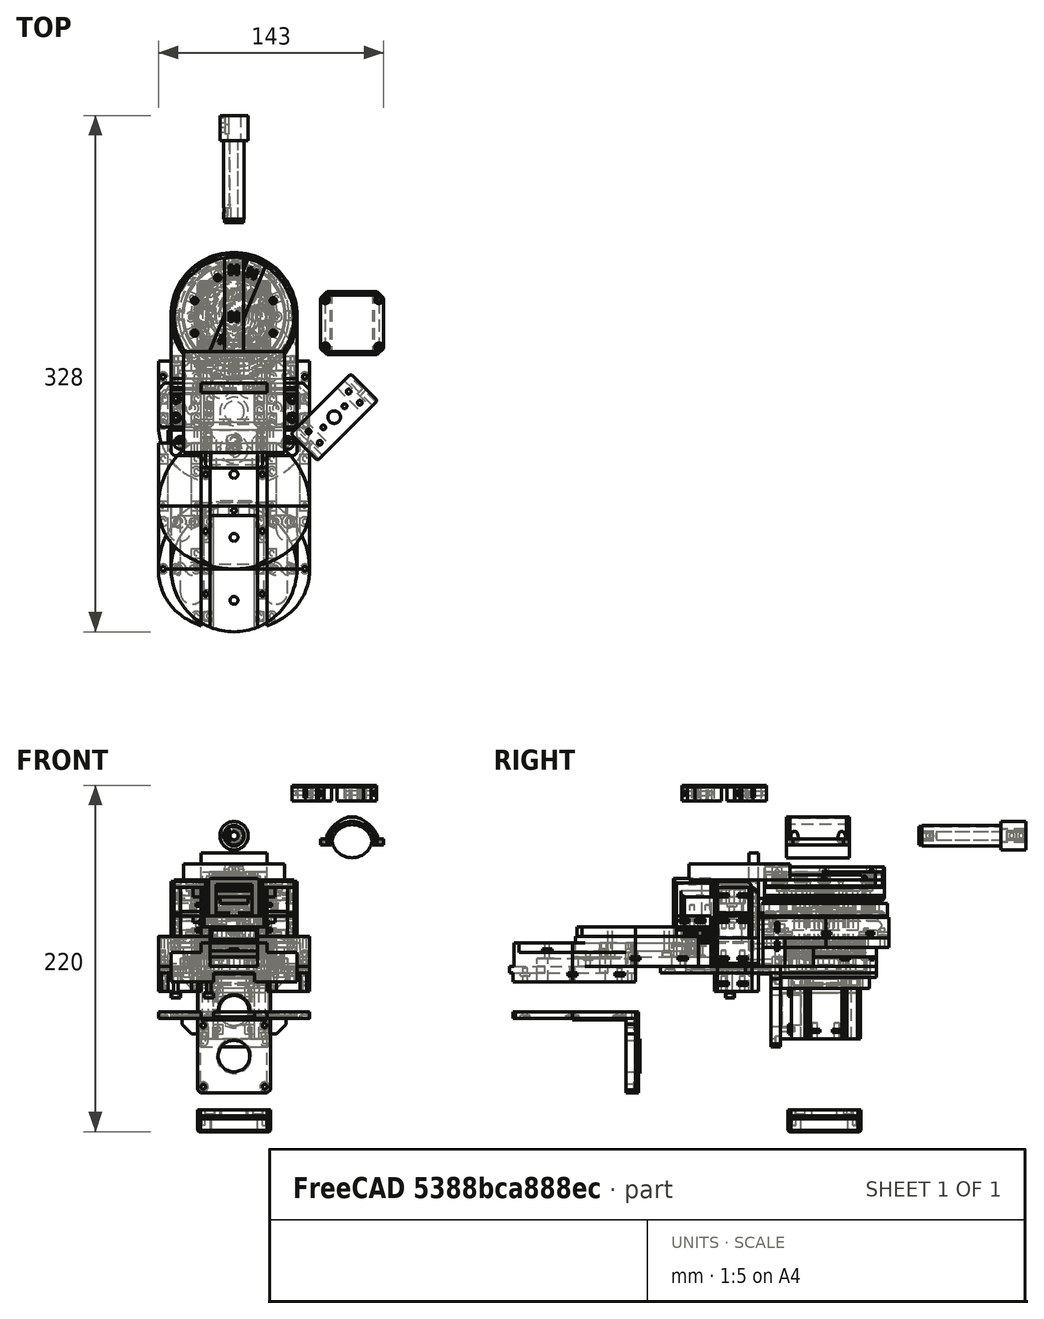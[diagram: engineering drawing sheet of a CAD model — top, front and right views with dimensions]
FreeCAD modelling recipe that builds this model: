
FCSTD DOCUMENT  (FreeCAD 0.19R24276 (Git))
Label: L-elbow_059
License: All rights reserved
LicenseURL: http://en.wikipedia.org/wiki/All_rights_reserved
objects: Part::Cylinder×884, Part::Box×401, Part::Cut×391, Part::Compound×387, Part::Chamfer×88, Part::FeaturePython×52, Mesh::Feature×41, Part::Fillet×8, Part::Common×8, Part::Torus×1, Part::Mirroring×1
note: 2221 computed .brp shape members not serialized (recipe doc carries the construction recipe); baked Part::Feature solids carry a one-line shape summary decoded from their .brp

FEATURE [Part::Cylinder] Cylinder2138  label="Válec2138"
  Angle = 360
  AttacherType = Attacher::AttachEngine3D
  Height = 15
  Placement = pos=(-34.5,-175,-69) rot=(0,0,1;0rad)
  Radius = 7.5
FEATURE [Part::Box] Box854  label="Krychle853"
  AttacherType = Attacher::AttachEngine3D
  Height = 30.1
  Length = 30.1
  Placement = pos=(-15.05,-310,-40.05) rot=(0,0,1;0rad)
  Width = 200
FEATURE [Part::Cylinder] Cylinder2140  label="Válec2140"
  Angle = 360
  AttacherType = Attacher::AttachEngine3D
  Height = 40
  Placement = pos=(24,-160,-70) rot=(0,0,1;0rad)
  Radius = 1.5
FEATURE [Part::Box] Box850  label="Krychle849"
  AttacherType = Attacher::AttachEngine3D
  Height = 30
  Length = 28
  Placement = pos=(-49,-210.5,-46) rot=(0,0,1;0rad)
  Width = 200
FEATURE [Part::Box] Box849  label="Krychle848"
  AttacherType = Attacher::AttachEngine3D
  Height = 30
  Length = 28
  Placement = pos=(21,-210.5,-46) rot=(0,0,1;0rad)
  Width = 200
FEATURE [Part::Cylinder] Cylinder2137  label="Válec2137"
  Angle = 360
  AttacherType = Attacher::AttachEngine3D
  Height = 25
  Placement = pos=(0,-160,-50) rot=(0,0,1;0rad)
  Radius = 48
FEATURE [Part::Box] Box851  label="Krychle850"
  AttacherType = Attacher::AttachEngine3D
  Height = 15
  Length = 15
  Placement = pos=(27,-175.6,-65) rot=(0,0,1;0rad)
  Width = 200
FEATURE [Part::Box] Box852  label="Krychle851"
  AttacherType = Attacher::AttachEngine3D
  Height = 15
  Length = 15
  Placement = pos=(-42,-175.5,-65) rot=(0,0,1;0rad)
  Width = 200
FEATURE [Part::Cylinder] Cylinder2139  label="Válec2139"
  Angle = 360
  AttacherType = Attacher::AttachEngine3D
  Height = 15
  Placement = pos=(34.5,-175,-69) rot=(0,0,1;0rad)
  Radius = 7.5
FEATURE [Part::Box] Box853  label="Krychle852"
  AttacherType = Attacher::AttachEngine3D
  Height = 30
  Length = 42
  Placement = pos=(-21,-290,-74) rot=(0,0,1;0rad)
  Width = 200
FEATURE [Part::Cylinder] Cylinder2142  label="Válec2142"
  Angle = 360
  AttacherType = Attacher::AttachEngine3D
  Height = 40
  Placement = pos=(-24,-190,-70) rot=(0,0,1;0rad)
  Radius = 1.5
FEATURE [Part::Cylinder] Cylinder2143  label="Válec2143"
  Angle = 360
  AttacherType = Attacher::AttachEngine3D
  Height = 20
  Placement = pos=(0,-140,-44) rot=(0,0,1;0rad)
  Radius = 2.5
FEATURE [Part::Cylinder] Cylinder2141  label="Válec2141"
  Angle = 360
  AttacherType = Attacher::AttachEngine3D
  Height = 40
  Placement = pos=(-45,-130,-70) rot=(0,0,1;0rad)
  Radius = 1.5
FEATURE [Part::Compound] Compound957
  Links = -> [Box850,Box849]
  Placement = pos=(0,0,15) rot=(0,0,1;0rad)
FEATURE [Part::Compound] Compound955
  Links = -> [Box852,Box851]
  Placement = pos=(0,0,15) rot=(0,0,1;0rad)
FEATURE [Part::Compound] Compound956
  Links = -> [Cylinder2138,Cylinder2139]
  Placement = pos=(0,0,19) rot=(0,0,1;0rad)
FEATURE [Part::Cut] Cut790
  Base = -> Cylinder2137
  Tool = -> Compound955
FEATURE [Part::Cut] Cut791
  Base = -> Cut790
  Tool = -> Box854
FEATURE [Part::Cut] Cut792
  Base = -> Cut791
  Tool = -> Box853
FEATURE [Part::Cut] Cut793
  Base = -> Cut792
  Tool = -> Compound956
FEATURE [Part::Cut] Cut796
  Base = -> Cut793
  Tool = -> Compound957
FEATURE [Part::Cylinder] Cylinder2149  label="Válec2149"
  Angle = 360
  AttacherType = Attacher::AttachEngine3D
  Height = 40
  Placement = pos=(-45,-160,-70) rot=(0,0,1;0rad)
  Radius = 1.5
FEATURE [Part::Box] Box855  label="Krychle854"
  AttacherType = Attacher::AttachEngine3D
  Height = 2
  Length = 6
  Placement = pos=(21,-193,-61) rot=(0,0,1;0rad)
  Width = 6
FEATURE [Part::Cylinder] Cylinder2145  label="Válec2145"
  Angle = 360
  AttacherType = Attacher::AttachEngine3D
  Height = 40
  Placement = pos=(24,-190,-70) rot=(0,0,1;0rad)
  Radius = 1.5
FEATURE [Part::Box] Box856  label="Krychle855"
  AttacherType = Attacher::AttachEngine3D
  Height = 2
  Length = 6
  Placement = pos=(-27,-133,-61) rot=(0,0,1;0rad)
  Width = 6
FEATURE [Part::Box] Box859  label="Krychle858"
  AttacherType = Attacher::AttachEngine3D
  Height = 2
  Length = 6
  Placement = pos=(-48,-163,-61) rot=(0,0,1;0rad)
  Width = 6
FEATURE [Part::Box] Box867  label="Krychle866"
  AttacherType = Attacher::AttachEngine3D
  Height = 2
  Length = 6
  Placement = pos=(-27,-163,-61) rot=(0,0,1;0rad)
  Width = 6
FEATURE [Part::Box] Box857  label="Krychle856"
  AttacherType = Attacher::AttachEngine3D
  Height = 2
  Length = 6
  Placement = pos=(42,-163,-61) rot=(0,0,1;0rad)
  Width = 6
FEATURE [Part::Cylinder] Cylinder2144  label="Válec2144"
  Angle = 360
  AttacherType = Attacher::AttachEngine3D
  Height = 40
  Placement = pos=(24,-130,-70) rot=(0,0,1;0rad)
  Radius = 1.5
FEATURE [Part::Box] Box861  label="Krychle860"
  AttacherType = Attacher::AttachEngine3D
  Height = 2
  Length = 6
  Placement = pos=(-21,-179,-31) rot=(0,0,1;0rad)
  Width = 6
FEATURE [Part::Cylinder] Cylinder2148  label="Válec2148"
  Angle = 360
  AttacherType = Attacher::AttachEngine3D
  Height = 20
  Placement = pos=(0,-180,-44) rot=(0,0,1;0rad)
  Radius = 2.5
FEATURE [Part::Compound] Compound958
  Links = -> [Cylinder2143,Cylinder2148]
FEATURE [Part::Cut] Cut786
  Base = -> Cut796
  Tool = -> Compound958
FEATURE [Part::Box] Box862  label="Krychle861"
  AttacherType = Attacher::AttachEngine3D
  Height = 2
  Length = 6
  Placement = pos=(-27,-193,-61) rot=(0,0,1;0rad)
  Width = 6
FEATURE [Part::Box] Box864  label="Krychle863"
  AttacherType = Attacher::AttachEngine3D
  Height = 2
  Length = 6
  Placement = pos=(-3,-126,-31) rot=(0,0,1;0rad)
  Width = 6
FEATURE [Part::Box] Box865  label="Krychle864"
  AttacherType = Attacher::AttachEngine3D
  Height = 2
  Length = 6
  Placement = pos=(21,-163,-61) rot=(0,0,1;0rad)
  Width = 6
FEATURE [Part::Cylinder] Cylinder2146  label="Válec2146"
  Angle = 360
  AttacherType = Attacher::AttachEngine3D
  Height = 40
  Placement = pos=(-24,-130,-70) rot=(0,0,1;0rad)
  Radius = 1.5
FEATURE [Part::Cylinder] Cylinder2147  label="Válec2147"
  Angle = 360
  AttacherType = Attacher::AttachEngine3D
  Height = 40
  Placement = pos=(45,-130,-70) rot=(0,0,1;0rad)
  Radius = 1.5
FEATURE [Part::Box] Box858  label="Krychle857"
  AttacherType = Attacher::AttachEngine3D
  Height = 2
  Length = 6
  Placement = pos=(42,-133,-61) rot=(0,0,1;0rad)
  Width = 6
FEATURE [Part::Cylinder] Cylinder2151  label="Válec2151"
  Angle = 360
  AttacherType = Attacher::AttachEngine3D
  Height = 40
  Placement = pos=(-24,-160,-70) rot=(0,0,1;0rad)
  Radius = 1.5
FEATURE [Part::Box] Box860  label="Krychle859"
  AttacherType = Attacher::AttachEngine3D
  Height = 2
  Length = 6
  Placement = pos=(15,-143,-31) rot=(0,0,1;0rad)
  Width = 6
FEATURE [Part::Cylinder] Cylinder2150  label="Válec2150"
  Angle = 360
  AttacherType = Attacher::AttachEngine3D
  Height = 40
  Placement = pos=(45,-160,-70) rot=(0,0,1;0rad)
  Radius = 1.5
FEATURE [Part::Compound] Compound959
  Links = -> [Cylinder2144,Cylinder2145,Cylinder2140,Cylinder2147,Cylinder2150,Cylinder2146,Cylinder2142,Cylinder2151,Cylinder2141,Cylinder2149]
  Placement = pos=(0,0,-11) rot=(0,0,1;0rad)
FEATURE [Part::Cut] Cut785
  Base = -> Cut786
  Tool = -> Compound959
FEATURE [Part::Box] Box863  label="Krychle862"
  AttacherType = Attacher::AttachEngine3D
  Height = 2
  Length = 6
  Placement = pos=(15,-179,-31) rot=(0,0,1;0rad)
  Width = 6
FEATURE [Part::Box] Box866  label="Krychle865"
  AttacherType = Attacher::AttachEngine3D
  Height = 2
  Length = 6
  Placement = pos=(21,-133,-61) rot=(0,0,1;0rad)
  Width = 6
FEATURE [Part::Cylinder] Cylinder2154  label="Válec2154"
  Angle = 360
  AttacherType = Attacher::AttachEngine3D
  Height = 40
  Placement = pos=(0,-123,-35) rot=(0,0,1;0rad)
  Radius = 1.5
FEATURE [Part::Box] Box868  label="Krychle867"
  AttacherType = Attacher::AttachEngine3D
  Height = 2
  Length = 6
  Placement = pos=(-21,-143,-31) rot=(0,0,1;0rad)
  Width = 6
FEATURE [Part::Box] Box872  label="Krychle871"
  AttacherType = Attacher::AttachEngine3D
  Height = 30
  Length = 29
  Placement = pos=(21,-210.5,-46) rot=(0,0,1;0rad)
  Width = 200
FEATURE [Part::Box] Box873  label="Krychle872"
  AttacherType = Attacher::AttachEngine3D
  Height = 25
  Length = 96
  Placement = pos=(-48,-160,-50) rot=(0,0,1;0rad)
  Width = 40
FEATURE [Part::Cylinder] Cylinder2153  label="Válec2153"
  Angle = 360
  AttacherType = Attacher::AttachEngine3D
  Height = 40
  Placement = pos=(18,-160,100) rot=(0,0,1;0rad)
  Radius = 1.5
FEATURE [Part::Cylinder] Cylinder2160  label="Válec2160"
  Angle = 360
  AttacherType = Attacher::AttachEngine3D
  Height = 40
  Placement = pos=(45,-130,-70) rot=(0,0,1;0rad)
  Radius = 1.5
FEATURE [Part::Cylinder] Cylinder2164  label="Válec2164"
  Angle = 360
  AttacherType = Attacher::AttachEngine3D
  Height = 20
  Placement = pos=(0,-140,-44) rot=(0,0,1;0rad)
  Radius = 2.5
FEATURE [Part::Cylinder] Cylinder2165  label="Válec2165"
  Angle = 360
  AttacherType = Attacher::AttachEngine3D
  Height = 40
  Placement = pos=(18,-176,-35) rot=(0,0,1;0rad)
  Radius = 1.5
FEATURE [Part::Box] Box869  label="Krychle868"
  AttacherType = Attacher::AttachEngine3D
  Height = 2
  Length = 6
  Placement = pos=(15,-163,100) rot=(0,0,1;0rad)
  Width = 6
FEATURE [Part::Cylinder] Cylinder2158  label="Válec2158"
  Angle = 360
  AttacherType = Attacher::AttachEngine3D
  Height = 40
  Placement = pos=(-45,-130,-70) rot=(0,0,1;0rad)
  Radius = 1.5
FEATURE [Part::Box] Box874  label="Krychle873"
  AttacherType = Attacher::AttachEngine3D
  Height = 30
  Length = 29
  Placement = pos=(-50,-210.5,-46) rot=(0,0,1;0rad)
  Width = 200
FEATURE [Part::Compound] Compound964
  Links = -> [Box874,Box872]
  Placement = pos=(0,0,15) rot=(0,0,1;0rad)
FEATURE [Part::Cylinder] Cylinder2152  label="Válec2152"
  Angle = 360
  AttacherType = Attacher::AttachEngine3D
  Height = 40
  Placement = pos=(-10,-123,100) rot=(0,0,1;0rad)
  Radius = 1.5
FEATURE [Part::Box] Box870  label="Krychle869"
  AttacherType = Attacher::AttachEngine3D
  Height = 2
  Length = 6
  Placement = pos=(-48,-133,-61) rot=(0,0,1;0rad)
  Width = 6
FEATURE [Part::Compound] Compound960
  Links = -> [Box870,Box859,Box856,Box867,Box862,Box858,Box857,Box866,Box865,Box855]
  Placement = pos=(0,0,15) rot=(0,0,1;0rad)
FEATURE [Part::Cylinder] Cylinder2156  label="Válec2156"
  Angle = 360
  AttacherType = Attacher::AttachEngine3D
  Height = 40
  Placement = pos=(-18,-140,-35) rot=(0,0,1;0rad)
  Radius = 1.5
FEATURE [Part::Cylinder] Cylinder2162  label="Válec2162"
  Angle = 360
  AttacherType = Attacher::AttachEngine3D
  Height = 40
  Placement = pos=(24,-130,-70) rot=(0,0,1;0rad)
  Radius = 1.5
FEATURE [Part::Cylinder] Cylinder2161  label="Válec2161"
  Angle = 360
  AttacherType = Attacher::AttachEngine3D
  Height = 40
  Placement = pos=(18,-140,-35) rot=(0,0,1;0rad)
  Radius = 1.5
FEATURE [Part::Box] Box871  label="Krychle870"
  AttacherType = Attacher::AttachEngine3D
  Height = 2
  Length = 6
  Placement = pos=(-21,-163,100) rot=(0,0,1;0rad)
  Width = 6
FEATURE [Part::Compound] Compound968
  Links = -> [Box864,Box871,Box861,Box868,Box869,Box863,Box860]
  Placement = pos=(0,0,20) rot=(0,0,1;0rad)
FEATURE [Part::Cylinder] Cylinder2155  label="Válec2155"
  Angle = 360
  AttacherType = Attacher::AttachEngine3D
  Height = 40
  Placement = pos=(-18,-176,-35) rot=(0,0,1;0rad)
  Radius = 1.5
FEATURE [Part::Cylinder] Cylinder2157  label="Válec2157"
  Angle = 360
  AttacherType = Attacher::AttachEngine3D
  Height = 40
  Placement = pos=(24,-160,-70) rot=(0,0,1;0rad)
  Radius = 1.5
FEATURE [Part::Cylinder] Cylinder2159  label="Válec2159"
  Angle = 360
  AttacherType = Attacher::AttachEngine3D
  Height = 20
  Placement = pos=(0,-180,-44) rot=(0,0,1;0rad)
  Radius = 2.5
FEATURE [Part::Compound] Compound961
  Links = -> [Cylinder2164,Cylinder2159]
FEATURE [Part::Box] Box875  label="Krychle874"
  AttacherType = Attacher::AttachEngine3D
  Height = 30.1
  Length = 30.1
  Placement = pos=(-15.05,-326,-40.05) rot=(0,0,1;0rad)
  Width = 200
FEATURE [Part::Cylinder] Cylinder2163  label="Válec2163"
  Angle = 360
  AttacherType = Attacher::AttachEngine3D
  Height = 40
  Placement = pos=(-18,-160,100) rot=(0,0,1;0rad)
  Radius = 1.5
FEATURE [Part::Compound] Compound970
  Links = -> [Cylinder2154,Cylinder2152,Cylinder2161,Cylinder2153,Cylinder2165,Cylinder2156,Cylinder2163,Cylinder2155]
FEATURE [Part::Cut] Cut787
  Base = -> Cut785
  Tool = -> Compound970
FEATURE [Part::Cut] Cut782
  Base = -> Cut787
  Tool = -> Compound968
FEATURE [Part::Cut] Cut794
  Base = -> Cut782
  Tool = -> Compound960
FEATURE [Part::Box] Box876  label="Krychle875"
  AttacherType = Attacher::AttachEngine3D
  Height = 30
  Length = 42
  Placement = pos=(-21,-290,-74) rot=(0,0,1;0rad)
  Width = 200
FEATURE [Part::Cut] Cut795
  Base = -> Box873
  Tool = -> Box876
FEATURE [Part::Cut] Cut788
  Base = -> Cut795
  Tool = -> Box875
FEATURE [Part::Box] Box878  label="Krychle877"
  AttacherType = Attacher::AttachEngine3D
  Height = 2
  Length = 6
  Placement = pos=(42,-133,-61) rot=(0,0,1;0rad)
  Width = 6
FEATURE [Part::Box] Box882  label="Krychle881"
  AttacherType = Attacher::AttachEngine3D
  Height = 2
  Length = 6
  Placement = pos=(42,-163,-61) rot=(0,0,1;0rad)
  Width = 6
FEATURE [Part::Cylinder] Cylinder2170  label="Válec2170"
  Angle = 360
  AttacherType = Attacher::AttachEngine3D
  Height = 40
  Placement = pos=(-24,-130,-70) rot=(0,0,1;0rad)
  Radius = 1.5
FEATURE [Part::Cylinder] Cylinder2166  label="Válec2166"
  Angle = 360
  AttacherType = Attacher::AttachEngine3D
  Height = 40
  Placement = pos=(-24,-160,-70) rot=(0,0,1;0rad)
  Radius = 1.5
FEATURE [Part::Box] Box879  label="Krychle878"
  AttacherType = Attacher::AttachEngine3D
  Height = 2
  Length = 6
  Placement = pos=(21,-163,-61) rot=(0,0,1;0rad)
  Width = 6
FEATURE [Part::Box] Box884  label="Krychle883"
  AttacherType = Attacher::AttachEngine3D
  Height = 2
  Length = 6
  Placement = pos=(-27,-193,-61) rot=(0,0,1;0rad)
  Width = 6
FEATURE [Part::Box] Box888  label="Krychle887"
  AttacherType = Attacher::AttachEngine3D
  Height = 2
  Length = 6
  Placement = pos=(15,-143,-31) rot=(0,0,1;0rad)
  Width = 6
FEATURE [Part::Box] Box877  label="Krychle876"
  AttacherType = Attacher::AttachEngine3D
  Height = 2
  Length = 6
  Placement = pos=(-48,-163,-61) rot=(0,0,1;0rad)
  Width = 6
FEATURE [Part::Box] Box881  label="Krychle880"
  AttacherType = Attacher::AttachEngine3D
  Height = 2
  Length = 6
  Placement = pos=(21,-193,-61) rot=(0,0,1;0rad)
  Width = 6
FEATURE [Part::Cylinder] Cylinder2169  label="Válec2169"
  Angle = 360
  AttacherType = Attacher::AttachEngine3D
  Height = 40
  Placement = pos=(-45,-160,-70) rot=(0,0,1;0rad)
  Radius = 1.5
FEATURE [Part::Box] Box880  label="Krychle879"
  AttacherType = Attacher::AttachEngine3D
  Height = 2
  Length = 6
  Placement = pos=(-27,-133,-61) rot=(0,0,1;0rad)
  Width = 6
FEATURE [Part::Cylinder] Cylinder2168  label="Válec2168"
  Angle = 360
  AttacherType = Attacher::AttachEngine3D
  Height = 40
  Placement = pos=(-24,-190,-70) rot=(0,0,1;0rad)
  Radius = 1.5
FEATURE [Part::Cylinder] Cylinder2167  label="Válec2167"
  Angle = 360
  AttacherType = Attacher::AttachEngine3D
  Height = 40
  Placement = pos=(24,-190,-70) rot=(0,0,1;0rad)
  Radius = 1.5
FEATURE [Part::Cylinder] Cylinder2171  label="Válec2171"
  Angle = 360
  AttacherType = Attacher::AttachEngine3D
  Height = 40
  Placement = pos=(45,-160,-70) rot=(0,0,1;0rad)
  Radius = 1.5
FEATURE [Part::Compound] Compound962
  Links = -> [Cylinder2162,Cylinder2167,Cylinder2157,Cylinder2160,Cylinder2171,Cylinder2170,Cylinder2168,Cylinder2166,Cylinder2158,Cylinder2169]
  Placement = pos=(0,0,-11) rot=(0,0,1;0rad)
FEATURE [Part::Box] Box886  label="Krychle885"
  AttacherType = Attacher::AttachEngine3D
  Height = 2
  Length = 6
  Placement = pos=(-48,-133,-61) rot=(0,0,1;0rad)
  Width = 6
FEATURE [Part::Cylinder] Cylinder2172  label="Válec2172"
  Angle = 360
  AttacherType = Attacher::AttachEngine3D
  Height = 40
  Placement = pos=(18,-176,-35) rot=(0,0,1;0rad)
  Radius = 1.5
FEATURE [Part::Box] Box883  label="Krychle882"
  AttacherType = Attacher::AttachEngine3D
  Height = 2
  Length = 6
  Placement = pos=(21,-133,-61) rot=(0,0,1;0rad)
  Width = 6
FEATURE [Part::Cylinder] Cylinder2173  label="Válec2173"
  Angle = 360
  AttacherType = Attacher::AttachEngine3D
  Height = 40
  Placement = pos=(-18,-140,-35) rot=(0,0,1;0rad)
  Radius = 1.5
FEATURE [Part::Box] Box885  label="Krychle884"
  AttacherType = Attacher::AttachEngine3D
  Height = 2
  Length = 6
  Placement = pos=(-27,-163,-61) rot=(0,0,1;0rad)
  Width = 6
FEATURE [Part::Compound] Compound965
  Links = -> [Box886,Box877,Box880,Box885,Box884,Box878,Box882,Box883,Box879,Box881]
  Placement = pos=(0,0,15) rot=(0,0,1;0rad)
FEATURE [Part::Cut] Cut778
  Base = -> Cut788
  Tool = -> Compound965
FEATURE [Part::Cut] Cut789
  Base = -> Cut778
  Tool = -> Compound962
FEATURE [Part::Cut] Cut779
  Base = -> Cut789
  Tool = -> Compound961
FEATURE [Part::Cut] Cut780
  Base = -> Cut779
  Tool = -> Compound964
FEATURE [Part::Box] Box887  label="Krychle886"
  AttacherType = Attacher::AttachEngine3D
  Height = 2
  Length = 6
  Placement = pos=(7,-126,100) rot=(0,0,1;0rad)
  Width = 6
FEATURE [Part::Cylinder] Cylinder2174  label="Válec2174"
  Angle = 360
  AttacherType = Attacher::AttachEngine3D
  Height = 40
  Placement = pos=(0,-123,-35) rot=(0,0,1;0rad)
  Radius = 1.5
FEATURE [Part::Box] Box889  label="Krychle888"
  AttacherType = Attacher::AttachEngine3D
  Height = 2
  Length = 6
  Placement = pos=(-3,-126,-31) rot=(0,0,1;0rad)
  Width = 6
FEATURE [Part::Box] Box890  label="Krychle889"
  AttacherType = Attacher::AttachEngine3D
  Height = 2
  Length = 6
  Placement = pos=(15,-179,-31) rot=(0,0,1;0rad)
  Width = 6
FEATURE [Part::Cylinder] Cylinder2178  label="Válec2178"
  Angle = 360
  AttacherType = Attacher::AttachEngine3D
  Height = 40
  Placement = pos=(-10,-123,100) rot=(0,0,1;0rad)
  Radius = 1.5
FEATURE [Part::Cylinder] Cylinder2180  label="Válec2180"
  Angle = 360
  AttacherType = Attacher::AttachEngine3D
  Height = 40
  Placement = pos=(18,-140,-35) rot=(0,0,1;0rad)
  Radius = 1.5
FEATURE [Part::Box] Box895  label="Krychle894"
  AttacherType = Attacher::AttachEngine3D
  Height = 15
  Length = 15
  Placement = pos=(-42,-175.5,-65) rot=(0,0,1;0rad)
  Width = 200
FEATURE [Part::Cylinder] Cylinder2184  label="Válec2184"
  Angle = 360
  AttacherType = Attacher::AttachEngine3D
  Height = 40
  Placement = pos=(18,-160,100) rot=(0,0,1;0rad)
  Radius = 1.5
FEATURE [Part::Cylinder] Cylinder2181  label="Válec2181"
  Angle = 360
  AttacherType = Attacher::AttachEngine3D
  Height = 40
  Placement = pos=(-18,-160,100) rot=(0,0,1;0rad)
  Radius = 1.5
FEATURE [Part::Cylinder] Cylinder2187  label="Válec2187"
  Angle = 360
  AttacherType = Attacher::AttachEngine3D
  Height = 40
  Placement = pos=(-18,-140,-35) rot=(0,0,1;0rad)
  Radius = 1.5
FEATURE [Part::Cylinder] Cylinder2189  label="Válec2189"
  Angle = 360
  AttacherType = Attacher::AttachEngine3D
  Height = 3
  Placement = pos=(-18,-160,100) rot=(0,0,1;0rad)
  Radius = 3
FEATURE [Part::Cylinder] Cylinder2191  label="Válec2191"
  Angle = 360
  AttacherType = Attacher::AttachEngine3D
  Height = 3
  Placement = pos=(-10,-123,100) rot=(0,0,1;0rad)
  Radius = 3
FEATURE [Part::Box] Box891  label="Krychle890"
  AttacherType = Attacher::AttachEngine3D
  Height = 2
  Length = 6
  Placement = pos=(15,-163,100) rot=(0,0,1;0rad)
  Width = 6
FEATURE [Part::Box] Box892  label="Krychle891"
  AttacherType = Attacher::AttachEngine3D
  Height = 2
  Length = 6
  Placement = pos=(-21,-163,100) rot=(0,0,1;0rad)
  Width = 6
FEATURE [Part::Box] Box893  label="Krychle892"
  AttacherType = Attacher::AttachEngine3D
  Height = 2
  Length = 6
  Placement = pos=(-21,-179,-31) rot=(0,0,1;0rad)
  Width = 6
FEATURE [Part::Box] Box894  label="Krychle893"
  AttacherType = Attacher::AttachEngine3D
  Height = 15
  Length = 15
  Placement = pos=(27,-175.6,-65) rot=(0,0,1;0rad)
  Width = 200
FEATURE [Part::Compound] Compound966
  Links = -> [Box895,Box894]
  Placement = pos=(0,0,15) rot=(0,0,1;0rad)
FEATURE [Part::Cut] Cut781
  Base = -> Cut780
  Tool = -> Compound966
FEATURE [Part::Cylinder] Cylinder2175  label="Válec2175"
  Angle = 360
  AttacherType = Attacher::AttachEngine3D
  Height = 40
  Placement = pos=(18,-140,-35) rot=(0,0,1;0rad)
  Radius = 1.5
FEATURE [Part::Cylinder] Cylinder2176  label="Válec2176"
  Angle = 360
  AttacherType = Attacher::AttachEngine3D
  Height = 40
  Placement = pos=(18,-160,100) rot=(0,0,1;0rad)
  Radius = 1.5
FEATURE [Part::Cylinder] Cylinder2177  label="Válec2177"
  Angle = 360
  AttacherType = Attacher::AttachEngine3D
  Height = 40
  Placement = pos=(-18,-160,100) rot=(0,0,1;0rad)
  Radius = 1.5
FEATURE [Part::Box] Box896  label="Krychle895"
  AttacherType = Attacher::AttachEngine3D
  Height = 2
  Length = 6
  Placement = pos=(-21,-143,-31) rot=(0,0,1;0rad)
  Width = 6
FEATURE [Part::Compound] Compound967
  Links = -> [Box889,Box892,Box893,Box896,Box887,Box891,Box890,Box888]
  Placement = pos=(0,0,20) rot=(0,0,1;0rad)
FEATURE [Part::Cut] Cut783
  Base = -> Cut781
  Tool = -> Compound967
FEATURE [Part::Cylinder] Cylinder2179  label="Válec2179"
  Angle = 360
  AttacherType = Attacher::AttachEngine3D
  Height = 40
  Placement = pos=(-18,-176,-35) rot=(0,0,1;0rad)
  Radius = 1.5
FEATURE [Part::Compound] Compound963
  Links = -> [Cylinder2174,Cylinder2178,Cylinder2175,Cylinder2176,Cylinder2172,Cylinder2173,Cylinder2177,Cylinder2179]
FEATURE [Part::Cut] Cut784
  Base = -> Cut783
  Tool = -> Compound963
FEATURE [Part::Cylinder] Cylinder2182  label="Válec2182"
  Angle = 360
  AttacherType = Attacher::AttachEngine3D
  Height = 40
  Placement = pos=(18,-176,-35) rot=(0,0,1;0rad)
  Radius = 1.5
FEATURE [Part::Cylinder] Cylinder2183  label="Válec2183"
  Angle = 360
  AttacherType = Attacher::AttachEngine3D
  Height = 40
  Placement = pos=(-10,-123,100) rot=(0,0,1;0rad)
  Radius = 1.5
FEATURE [Part::Cylinder] Cylinder2185  label="Válec2185"
  Angle = 360
  AttacherType = Attacher::AttachEngine3D
  Height = 40
  Placement = pos=(0,-123,-35) rot=(0,0,1;0rad)
  Radius = 1.5
FEATURE [Part::Cylinder] Cylinder2186  label="Válec2186"
  Angle = 360
  AttacherType = Attacher::AttachEngine3D
  Height = 40
  Placement = pos=(-18,-176,-35) rot=(0,0,1;0rad)
  Radius = 1.5
FEATURE [Part::Compound] Compound971
  Links = -> [Cylinder2185,Cylinder2183,Cylinder2180,Cylinder2184,Cylinder2182,Cylinder2187,Cylinder2181,Cylinder2186]
  Placement = pos=(0,0,-26) rot=(0,0,1;0rad)
FEATURE [Part::Cylinder] Cylinder2188  label="Válec2188"
  Angle = 360
  AttacherType = Attacher::AttachEngine3D
  Height = 3
  Placement = pos=(18,-140,-35) rot=(0,0,1;0rad)
  Radius = 3
FEATURE [Part::Cylinder] Cylinder2190  label="Válec2190"
  Angle = 360
  AttacherType = Attacher::AttachEngine3D
  Height = 3
  Placement = pos=(18,-176,-35) rot=(0,0,1;0rad)
  Radius = 3
FEATURE [Part::Cylinder] Cylinder2195  label="Válec2195"
  Angle = 360
  AttacherType = Attacher::AttachEngine3D
  Height = 3
  Placement = pos=(-18,-140,-35) rot=(0,0,1;0rad)
  Radius = 3
FEATURE [Part::Cylinder] Cylinder2203  label="Válec2203"
  Angle = 360
  AttacherType = Attacher::AttachEngine3D
  Height = 40
  Placement = pos=(-18,-140,-35) rot=(0,0,1;0rad)
  Radius = 1.5
FEATURE [Part::Cylinder] Cylinder2206  label="Válec2206"
  Angle = 360
  AttacherType = Attacher::AttachEngine3D
  Height = 3
  Placement = pos=(18,-176,-35) rot=(0,0,1;0rad)
  Radius = 3
FEATURE [Part::Cylinder] Cylinder2208  label="Válec2208"
  Angle = 360
  AttacherType = Attacher::AttachEngine3D
  Height = 3
  Placement = pos=(18,-160,100) rot=(0,0,1;0rad)
  Radius = 3
FEATURE [Part::Cylinder] Cylinder2210  label="Válec2210"
  Angle = 360
  AttacherType = Attacher::AttachEngine3D
  Height = 3
  Placement = pos=(-18,-176,-35) rot=(0,0,1;0rad)
  Radius = 3
FEATURE [Part::Cylinder] Cylinder2197  label="Válec2197"
  Angle = 360
  AttacherType = Attacher::AttachEngine3D
  Height = 40
  Placement = pos=(-18,-160,100) rot=(0,0,1;0rad)
  Radius = 1.5
FEATURE [Part::Cylinder] Cylinder2200  label="Válec2200"
  Angle = 360
  AttacherType = Attacher::AttachEngine3D
  Height = 40
  Placement = pos=(18,-160,100) rot=(0,0,1;0rad)
  Radius = 1.5
FEATURE [Part::Cylinder] Cylinder2199  label="Válec2199"
  Angle = 360
  AttacherType = Attacher::AttachEngine3D
  Height = 40
  Placement = pos=(-10,-123,100) rot=(0,0,1;0rad)
  Radius = 1.5
FEATURE [Part::Cylinder] Cylinder2198  label="Válec2198"
  Angle = 360
  AttacherType = Attacher::AttachEngine3D
  Height = 40
  Placement = pos=(18,-176,-35) rot=(0,0,1;0rad)
  Radius = 1.5
FEATURE [Part::Cylinder] Cylinder2193  label="Válec2193"
  Angle = 360
  AttacherType = Attacher::AttachEngine3D
  Height = 3
  Placement = pos=(0,-123,-35) rot=(0,0,1;0rad)
  Radius = 3
FEATURE [Part::Cylinder] Cylinder2196  label="Válec2196"
  Angle = 360
  AttacherType = Attacher::AttachEngine3D
  Height = 40
  Placement = pos=(18,-140,-35) rot=(0,0,1;0rad)
  Radius = 1.5
FEATURE [Part::Cylinder] Cylinder2201  label="Válec2201"
  Angle = 360
  AttacherType = Attacher::AttachEngine3D
  Height = 40
  Placement = pos=(0,-123,-35) rot=(0,0,1;0rad)
  Radius = 1.5
FEATURE [Part::Cylinder] Cylinder2194  label="Válec2194"
  Angle = 360
  AttacherType = Attacher::AttachEngine3D
  Height = 3
  Placement = pos=(-18,-176,-35) rot=(0,0,1;0rad)
  Radius = 3
FEATURE [Part::Cylinder] Cylinder2192  label="Válec2192"
  Angle = 360
  AttacherType = Attacher::AttachEngine3D
  Height = 3
  Placement = pos=(18,-160,100) rot=(0,0,1;0rad)
  Radius = 3
FEATURE [Part::Compound] Compound972
  Links = -> [Cylinder2193,Cylinder2191,Cylinder2188,Cylinder2192,Cylinder2190,Cylinder2195,Cylinder2189,Cylinder2194]
  Placement = pos=(0,0,-9) rot=(0,0,1;0rad)
FEATURE [Part::Cut] Cut800
  Base = -> Cut784
  Tool = -> Compound972
FEATURE [Part::Cut] Cut801
  Base = -> Cut800
  Tool = -> Compound971
FEATURE [Part::Fillet] Fillet003
  Base = -> Cut801
  Edges = 2 edges r=5: [Edge66,Edge70]
FEATURE [Part::Cylinder] Cylinder2202  label="Válec2202"
  Angle = 360
  AttacherType = Attacher::AttachEngine3D
  Height = 40
  Placement = pos=(-18,-176,-35) rot=(0,0,1;0rad)
  Radius = 1.5
FEATURE [Part::Compound] Compound973
  Links = -> [Cylinder2201,Cylinder2199,Cylinder2196,Cylinder2200,Cylinder2198,Cylinder2203,Cylinder2197,Cylinder2202]
  Placement = pos=(0,0,-26) rot=(0,0,1;0rad)
FEATURE [Part::Cylinder] Cylinder2204  label="Válec2204"
  Angle = 360
  AttacherType = Attacher::AttachEngine3D
  Height = 3
  Placement = pos=(18,-140,-35) rot=(0,0,1;0rad)
  Radius = 3
FEATURE [Part::Box] Box897  label="Krychle896"
  AttacherType = Attacher::AttachEngine3D
  Height = 25
  Length = 96
  Placement = pos=(-48,-120,-50) rot=(0,0,1;0rad)
  Width = 40
FEATURE [Part::Cut] Cut797
  Base = -> Cut794
  Tool = -> Box897
FEATURE [Part::Cylinder] Cylinder2205  label="Válec2205"
  Angle = 360
  AttacherType = Attacher::AttachEngine3D
  Height = 3
  Placement = pos=(-18,-160,100) rot=(0,0,1;0rad)
  Radius = 3
FEATURE [Part::Cylinder] Cylinder2207  label="Válec2207"
  Angle = 360
  AttacherType = Attacher::AttachEngine3D
  Height = 3
  Placement = pos=(-10,-123,100) rot=(0,0,1;0rad)
  Radius = 3
FEATURE [Part::Cylinder] Cylinder2209  label="Válec2209"
  Angle = 360
  AttacherType = Attacher::AttachEngine3D
  Height = 3
  Placement = pos=(0,-123,-35) rot=(0,0,1;0rad)
  Radius = 3
FEATURE [Part::Cylinder] Cylinder2211  label="Válec2211"
  Angle = 360
  AttacherType = Attacher::AttachEngine3D
  Height = 3
  Placement = pos=(-18,-140,-35) rot=(0,0,1;0rad)
  Radius = 3
FEATURE [Part::Compound] Compound974
  Links = -> [Cylinder2209,Cylinder2207,Cylinder2204,Cylinder2208,Cylinder2206,Cylinder2211,Cylinder2205,Cylinder2210]
  Placement = pos=(0,0,-9) rot=(0,0,1;0rad)
FEATURE [Part::Cut] Cut798
  Base = -> Cut797
  Tool = -> Compound974
FEATURE [Part::Cut] Cut799
  Base = -> Cut798
  Tool = -> Compound973
FEATURE [Part::Fillet] Fillet
  Base = -> Cut799
  Edges = 2 edges r=5: [Edge113,Edge122]
FEATURE [Part::Cylinder] Cylinder2337  label="Válec2337"
  Angle = 360
  AttacherType = Attacher::AttachEngine3D
  Height = 32
  Placement = pos=(0,-140,-57) rot=(0,0,1;0rad)
  Radius = 60
FEATURE [Part::FeaturePython] Tube  # WARN: FeaturePython — macro-defined, semantics opaque (R4)
  AttacherType = Attacher::AttachEngine3D
  Height = 10
  InnerRadius = 40
  OuterRadius = 60
  Placement = pos=(0,-160,-31) rot=(0,0,1;0rad)
FEATURE [Part::Common] Common
  Base = -> Fillet
  Tool = -> Cylinder2337
FEATURE [Part::Fillet] Fillet005
  Base = -> Common
  Edges = 2 edges r=4: [Edge150,Edge151]
FEATURE [Part::Fillet] Fillet006
  Base = -> Fillet005
  Edges = 2 edges r=36: [Edge21,Edge30]
FEATURE [Part::Cut] Cut843
  Base = -> Fillet006
  Tool = -> Tube
FEATURE [Part::Compound] Compound1019  label="L-elb_major-conno-moto"
  Links = -> [Fillet003,Cut843]
  Placement = pos=(0,40,10) rot=(0,0,1;0rad)
FEATURE [Part::Cylinder] Cylinder1647  label="Válec1647"
  Angle = 360
  AttacherType = Attacher::AttachEngine3D
  Height = 15
  Placement = pos=(26.5,-175,-69) rot=(0,0,1;0rad)
  Radius = 7.5
FEATURE [Part::Box] Box644  label="Krychle643"
  AttacherType = Attacher::AttachEngine3D
  Height = 15
  Length = 15
  Placement = pos=(-34,-175.5,-65) rot=(0,0,1;0rad)
  Width = 200
FEATURE [Part::Box] Box647  label="Krychle646"
  AttacherType = Attacher::AttachEngine3D
  Height = 30
  Length = 23
  Placement = pos=(21,-210.5,-46) rot=(0,0,1;0rad)
  Width = 200
FEATURE [Part::Box] Box648  label="Krychle647"
  AttacherType = Attacher::AttachEngine3D
  Height = 30
  Length = 23
  Placement = pos=(-44,-210.5,-46) rot=(0,0,1;0rad)
  Width = 200
FEATURE [Part::Box] Box643  label="Krychle642"
  AttacherType = Attacher::AttachEngine3D
  Height = 15
  Length = 15
  Placement = pos=(19,-175.6,-65) rot=(0,0,1;0rad)
  Width = 200
FEATURE [Part::Cylinder] Cylinder1645  label="Válec1645"
  Angle = 360
  AttacherType = Attacher::AttachEngine3D
  Height = 25
  Placement = pos=(0,-160,-50) rot=(0,0,1;0rad)
  Radius = 40
FEATURE [Part::Cylinder] Cylinder1646  label="Válec1646"
  Angle = 360
  AttacherType = Attacher::AttachEngine3D
  Height = 15
  Placement = pos=(-26.5,-175,-69) rot=(0,0,1;0rad)
  Radius = 7.5
FEATURE [Part::Compound] Compound783
  Links = -> [Box644,Box643]
  Placement = pos=(0,0,15) rot=(0,0,1;0rad)
FEATURE [Part::Compound] Compound784
  Links = -> [Box648,Box647]
  Placement = pos=(0,0,15) rot=(0,0,1;0rad)
FEATURE [Part::Compound] Compound782
  Links = -> [Cylinder1646,Cylinder1647]
  Placement = pos=(0,0,19) rot=(0,0,1;0rad)
FEATURE [Part::Box] Box646  label="Krychle645"
  AttacherType = Attacher::AttachEngine3D
  Height = 30.1
  Length = 30.1
  Placement = pos=(-15.05,-310,-40.05) rot=(0,0,1;0rad)
  Width = 200
FEATURE [Part::Cylinder] Cylinder1653  label="Válec1653"
  Angle = 360
  AttacherType = Attacher::AttachEngine3D
  Height = 40
  Placement = pos=(-37,-130,-70) rot=(0,0,1;0rad)
  Radius = 1.5
FEATURE [Part::Cylinder] Cylinder1654  label="Válec1654"
  Angle = 360
  AttacherType = Attacher::AttachEngine3D
  Height = 40
  Placement = pos=(-16,-190,-70) rot=(0,0,1;0rad)
  Radius = 1.5
FEATURE [Part::Cylinder] Cylinder1657  label="Válec1657"
  Angle = 360
  AttacherType = Attacher::AttachEngine3D
  Height = 40
  Placement = pos=(16,-160,-70) rot=(0,0,1;0rad)
  Radius = 1.5
FEATURE [Part::Cylinder] Cylinder1648  label="Válec1648"
  Angle = 360
  AttacherType = Attacher::AttachEngine3D
  Height = 20
  Placement = pos=(0,-140,-44) rot=(0,0,1;0rad)
  Radius = 2.5
FEATURE [Part::Cylinder] Cylinder1659  label="Válec1659"
  Angle = 360
  AttacherType = Attacher::AttachEngine3D
  Height = 40
  Placement = pos=(16,-130,-70) rot=(0,0,1;0rad)
  Radius = 1.5
FEATURE [Part::Box] Box645  label="Krychle644"
  AttacherType = Attacher::AttachEngine3D
  Height = 30
  Length = 26
  Placement = pos=(-13,-290,-74) rot=(0,0,1;0rad)
  Width = 200
FEATURE [Part::Box] Box650  label="Krychle649"
  AttacherType = Attacher::AttachEngine3D
  Height = 2
  Length = 6
  Placement = pos=(13,-193,-61) rot=(0,0,1;0rad)
  Width = 6
FEATURE [Part::Cut] Cut602
  Base = -> Cylinder1645
  Tool = -> Compound783
FEATURE [Part::Cut] Cut603
  Base = -> Cut602
  Tool = -> Box646
FEATURE [Part::Cut] Cut604
  Base = -> Cut603
  Tool = -> Box645
FEATURE [Part::Cut] Cut605
  Base = -> Cut604
  Tool = -> Compound782
FEATURE [Part::Cut] Cut606
  Base = -> Cut605
  Tool = -> Compound784
FEATURE [Part::Box] Box663  label="Krychle662"
  AttacherType = Attacher::AttachEngine3D
  Height = 2
  Length = 6
  Placement = pos=(15,-179,-31) rot=(0,0,1;0rad)
  Width = 6
FEATURE [Part::Box] Box662  label="Krychle661"
  AttacherType = Attacher::AttachEngine3D
  Height = 2
  Length = 6
  Placement = pos=(-3,-126,-31) rot=(0,0,1;0rad)
  Width = 6
FEATURE [Part::Cylinder] Cylinder1652  label="Válec1652"
  Angle = 360
  AttacherType = Attacher::AttachEngine3D
  Height = 40
  Placement = pos=(-16,-160,-70) rot=(0,0,1;0rad)
  Radius = 1.5
FEATURE [Part::Box] Box665  label="Krychle664"
  AttacherType = Attacher::AttachEngine3D
  Height = 2
  Length = 6
  Placement = pos=(15,-143,-31) rot=(0,0,1;0rad)
  Width = 6
FEATURE [Part::Box] Box660  label="Krychle659"
  AttacherType = Attacher::AttachEngine3D
  Height = 2
  Length = 6
  Placement = pos=(-21,-179,-31) rot=(0,0,1;0rad)
  Width = 6
FEATURE [Part::Cylinder] Cylinder1651  label="Válec1651"
  Angle = 360
  AttacherType = Attacher::AttachEngine3D
  Height = 40
  Placement = pos=(16,-190,-70) rot=(0,0,1;0rad)
  Radius = 1.5
FEATURE [Part::Box] Box651  label="Krychle650"
  AttacherType = Attacher::AttachEngine3D
  Height = 2
  Length = 6
  Placement = pos=(-19,-133,-61) rot=(0,0,1;0rad)
  Width = 6
FEATURE [Part::Cylinder] Cylinder1649  label="Válec1649"
  Angle = 360
  AttacherType = Attacher::AttachEngine3D
  Height = 20
  Placement = pos=(0,-180,-44) rot=(0,0,1;0rad)
  Radius = 2.5
FEATURE [Part::Compound] Compound785
  Links = -> [Cylinder1648,Cylinder1649]
FEATURE [Part::Cut] Cut607
  Base = -> Cut606
  Tool = -> Compound785
FEATURE [Part::Cylinder] Cylinder1655  label="Válec1655"
  Angle = 360
  AttacherType = Attacher::AttachEngine3D
  Height = 40
  Placement = pos=(-16,-130,-70) rot=(0,0,1;0rad)
  Radius = 1.5
FEATURE [Part::Cylinder] Cylinder1658  label="Válec1658"
  Angle = 360
  AttacherType = Attacher::AttachEngine3D
  Height = 40
  Placement = pos=(-37,-160,-70) rot=(0,0,1;0rad)
  Radius = 1.5
FEATURE [Part::Cylinder] Cylinder1650  label="Válec1650"
  Angle = 360
  AttacherType = Attacher::AttachEngine3D
  Height = 40
  Placement = pos=(37,-160,-70) rot=(0,0,1;0rad)
  Radius = 1.5
FEATURE [Part::Box] Box649  label="Krychle648"
  AttacherType = Attacher::AttachEngine3D
  Height = 2
  Length = 6
  Placement = pos=(34,-163,-61) rot=(0,0,1;0rad)
  Width = 6
FEATURE [Part::Cylinder] Cylinder1656  label="Válec1656"
  Angle = 360
  AttacherType = Attacher::AttachEngine3D
  Height = 40
  Placement = pos=(37,-130,-70) rot=(0,0,1;0rad)
  Radius = 1.5
FEATURE [Part::Compound] Compound786
  Links = -> [Cylinder1659,Cylinder1651,Cylinder1657,Cylinder1656,Cylinder1650,Cylinder1655,Cylinder1654,Cylinder1652,Cylinder1653,Cylinder1658]
  Placement = pos=(0,0,-11) rot=(0,0,1;0rad)
FEATURE [Part::Cut] Cut608
  Base = -> Cut607
  Tool = -> Compound786
FEATURE [Part::Box] Box652  label="Krychle651"
  AttacherType = Attacher::AttachEngine3D
  Height = 2
  Length = 6
  Placement = pos=(34,-133,-61) rot=(0,0,1;0rad)
  Width = 6
FEATURE [Part::Box] Box654  label="Krychle653"
  AttacherType = Attacher::AttachEngine3D
  Height = 2
  Length = 6
  Placement = pos=(-40,-163,-61) rot=(0,0,1;0rad)
  Width = 6
FEATURE [Part::Box] Box658  label="Krychle657"
  AttacherType = Attacher::AttachEngine3D
  Height = 2
  Length = 6
  Placement = pos=(-19,-193,-61) rot=(0,0,1;0rad)
  Width = 6
FEATURE [Part::Box] Box655  label="Krychle654"
  AttacherType = Attacher::AttachEngine3D
  Height = 2
  Length = 6
  Placement = pos=(13,-133,-61) rot=(0,0,1;0rad)
  Width = 6
FEATURE [Part::Box] Box656  label="Krychle655"
  AttacherType = Attacher::AttachEngine3D
  Height = 2
  Length = 6
  Placement = pos=(-19,-163,-61) rot=(0,0,1;0rad)
  Width = 6
FEATURE [Part::Cylinder] Cylinder1660  label="Válec1660"
  Angle = 360
  AttacherType = Attacher::AttachEngine3D
  Height = 40
  Placement = pos=(-10,-123,100) rot=(0,0,1;0rad)
  Radius = 1.5
FEATURE [Part::Box] Box664  label="Krychle663"
  AttacherType = Attacher::AttachEngine3D
  Height = 2
  Length = 6
  Placement = pos=(15,-163,100) rot=(0,0,1;0rad)
  Width = 6
FEATURE [Part::Cylinder] Cylinder1662  label="Válec1662"
  Angle = 360
  AttacherType = Attacher::AttachEngine3D
  Height = 40
  Placement = pos=(0,-123,-35) rot=(0,0,1;0rad)
  Radius = 1.5
FEATURE [Part::Box] Box661  label="Krychle660"
  AttacherType = Attacher::AttachEngine3D
  Height = 2
  Length = 6
  Placement = pos=(-21,-143,-31) rot=(0,0,1;0rad)
  Width = 6
FEATURE [Part::Box] Box657  label="Krychle656"
  AttacherType = Attacher::AttachEngine3D
  Height = 2
  Length = 6
  Placement = pos=(-40,-133,-61) rot=(0,0,1;0rad)
  Width = 6
FEATURE [Part::Box] Box653  label="Krychle652"
  AttacherType = Attacher::AttachEngine3D
  Height = 2
  Length = 6
  Placement = pos=(13,-163,-61) rot=(0,0,1;0rad)
  Width = 6
FEATURE [Part::Compound] Compound787
  Links = -> [Box657,Box654,Box651,Box656,Box658,Box652,Box649,Box655,Box653,Box650]
  Placement = pos=(0,0,15) rot=(0,0,1;0rad)
FEATURE [Part::Cylinder] Cylinder1672  label="Válec1672"
  Angle = 360
  AttacherType = Attacher::AttachEngine3D
  Height = 40
  Placement = pos=(16,-160,-70) rot=(0,0,1;0rad)
  Radius = 1.5
FEATURE [Part::Cylinder] Cylinder1673  label="Válec1673"
  Angle = 360
  AttacherType = Attacher::AttachEngine3D
  Height = 40
  Placement = pos=(-37,-130,-70) rot=(0,0,1;0rad)
  Radius = 1.5
FEATURE [Part::Box] Box666  label="Krychle665"
  AttacherType = Attacher::AttachEngine3D
  Height = 25
  Length = 80
  Placement = pos=(-40,-160,-50) rot=(0,0,1;0rad)
  Width = 40
FEATURE [Part::Cylinder] Cylinder1667  label="Válec1667"
  Angle = 360
  AttacherType = Attacher::AttachEngine3D
  Height = 40
  Placement = pos=(-18,-176,-35) rot=(0,0,1;0rad)
  Radius = 1.5
FEATURE [Part::Cylinder] Cylinder1669  label="Válec1669"
  Angle = 360
  AttacherType = Attacher::AttachEngine3D
  Height = 20
  Placement = pos=(0,-180,-44) rot=(0,0,1;0rad)
  Radius = 2.5
FEATURE [Part::Cylinder] Cylinder1670  label="Válec1670"
  Angle = 360
  AttacherType = Attacher::AttachEngine3D
  Height = 40
  Placement = pos=(37,-130,-70) rot=(0,0,1;0rad)
  Radius = 1.5
FEATURE [Part::Cylinder] Cylinder1665  label="Válec1665"
  Angle = 360
  AttacherType = Attacher::AttachEngine3D
  Height = 40
  Placement = pos=(18,-140,-35) rot=(0,0,1;0rad)
  Radius = 1.5
FEATURE [Part::Cylinder] Cylinder1671  label="Válec1671"
  Angle = 360
  AttacherType = Attacher::AttachEngine3D
  Height = 40
  Placement = pos=(16,-130,-70) rot=(0,0,1;0rad)
  Radius = 1.5
FEATURE [Part::Box] Box668  label="Krychle667"
  AttacherType = Attacher::AttachEngine3D
  Height = 30.1
  Length = 30.1
  Placement = pos=(-15.05,-326,-40.05) rot=(0,0,1;0rad)
  Width = 200
FEATURE [Part::Cylinder] Cylinder1668  label="Válec1668"
  Angle = 360
  AttacherType = Attacher::AttachEngine3D
  Height = 20
  Placement = pos=(0,-140,-44) rot=(0,0,1;0rad)
  Radius = 2.5
FEATURE [Part::Compound] Compound791
  Links = -> [Cylinder1668,Cylinder1669]
FEATURE [Part::Box] Box670  label="Krychle669"
  AttacherType = Attacher::AttachEngine3D
  Height = 30
  Length = 23
  Placement = pos=(-44,-210.5,-46) rot=(0,0,1;0rad)
  Width = 200
FEATURE [Part::Box] Box667  label="Krychle666"
  AttacherType = Attacher::AttachEngine3D
  Height = 30
  Length = 26
  Placement = pos=(-13,-290,-74) rot=(0,0,1;0rad)
  Width = 200
FEATURE [Part::Cut] Cut612
  Base = -> Box666
  Tool = -> Box667
FEATURE [Part::Cut] Cut613
  Base = -> Cut612
  Tool = -> Box668
FEATURE [Part::Cylinder] Cylinder1666  label="Válec1666"
  Angle = 360
  AttacherType = Attacher::AttachEngine3D
  Height = 40
  Placement = pos=(18,-176,-35) rot=(0,0,1;0rad)
  Radius = 1.5
FEATURE [Part::Box] Box659  label="Krychle658"
  AttacherType = Attacher::AttachEngine3D
  Height = 2
  Length = 6
  Placement = pos=(-21,-163,100) rot=(0,0,1;0rad)
  Width = 6
FEATURE [Part::Compound] Compound788
  Links = -> [Box662,Box659,Box660,Box661,Box664,Box663,Box665]
FEATURE [Part::Cylinder] Cylinder1663  label="Válec1663"
  Angle = 360
  AttacherType = Attacher::AttachEngine3D
  Height = 40
  Placement = pos=(-18,-140,-35) rot=(0,0,1;0rad)
  Radius = 1.5
FEATURE [Part::Box] Box669  label="Krychle668"
  AttacherType = Attacher::AttachEngine3D
  Height = 30
  Length = 23
  Placement = pos=(21,-210.5,-46) rot=(0,0,1;0rad)
  Width = 200
FEATURE [Part::Compound] Compound790
  Links = -> [Box670,Box669]
  Placement = pos=(0,0,15) rot=(0,0,1;0rad)
FEATURE [Part::Cylinder] Cylinder1674  label="Válec1674"
  Angle = 360
  AttacherType = Attacher::AttachEngine3D
  Height = 40
  Placement = pos=(-16,-190,-70) rot=(0,0,1;0rad)
  Radius = 1.5
FEATURE [Part::Box] Box673  label="Krychle672"
  AttacherType = Attacher::AttachEngine3D
  Height = 2
  Length = 6
  Placement = pos=(-19,-133,-61) rot=(0,0,1;0rad)
  Width = 6
FEATURE [Part::Box] Box679  label="Krychle678"
  AttacherType = Attacher::AttachEngine3D
  Height = 2
  Length = 6
  Placement = pos=(34,-163,-61) rot=(0,0,1;0rad)
  Width = 6
FEATURE [Part::Box] Box672  label="Krychle671"
  AttacherType = Attacher::AttachEngine3D
  Height = 2
  Length = 6
  Placement = pos=(-19,-193,-61) rot=(0,0,1;0rad)
  Width = 6
FEATURE [Part::Box] Box671  label="Krychle670"
  AttacherType = Attacher::AttachEngine3D
  Height = 2
  Length = 6
  Placement = pos=(-19,-163,-61) rot=(0,0,1;0rad)
  Width = 6
FEATURE [Part::Cylinder] Cylinder1676  label="Válec1676"
  Angle = 360
  AttacherType = Attacher::AttachEngine3D
  Height = 40
  Placement = pos=(37,-160,-70) rot=(0,0,1;0rad)
  Radius = 1.5
FEATURE [Part::Box] Box680  label="Krychle679"
  AttacherType = Attacher::AttachEngine3D
  Height = 2
  Length = 6
  Placement = pos=(13,-133,-61) rot=(0,0,1;0rad)
  Width = 6
FEATURE [Part::Box] Box674  label="Krychle673"
  AttacherType = Attacher::AttachEngine3D
  Height = 2
  Length = 6
  Placement = pos=(-40,-133,-61) rot=(0,0,1;0rad)
  Width = 6
FEATURE [Part::Box] Box675  label="Krychle674"
  AttacherType = Attacher::AttachEngine3D
  Height = 2
  Length = 6
  Placement = pos=(-40,-163,-61) rot=(0,0,1;0rad)
  Width = 6
FEATURE [Part::Cylinder] Cylinder1675  label="Válec1675"
  Angle = 360
  AttacherType = Attacher::AttachEngine3D
  Height = 40
  Placement = pos=(-16,-160,-70) rot=(0,0,1;0rad)
  Radius = 1.5
FEATURE [Part::Box] Box677  label="Krychle676"
  AttacherType = Attacher::AttachEngine3D
  Height = 2
  Length = 6
  Placement = pos=(34,-133,-61) rot=(0,0,1;0rad)
  Width = 6
FEATURE [Part::Cylinder] Cylinder1679  label="Válec1679"
  Angle = 360
  AttacherType = Attacher::AttachEngine3D
  Height = 40
  Placement = pos=(-37,-160,-70) rot=(0,0,1;0rad)
  Radius = 1.5
FEATURE [Part::Cylinder] Cylinder1678  label="Válec1678"
  Angle = 360
  AttacherType = Attacher::AttachEngine3D
  Height = 40
  Placement = pos=(16,-190,-70) rot=(0,0,1;0rad)
  Radius = 1.5
FEATURE [Part::Cylinder] Cylinder1677  label="Válec1677"
  Angle = 360
  AttacherType = Attacher::AttachEngine3D
  Height = 40
  Placement = pos=(-16,-130,-70) rot=(0,0,1;0rad)
  Radius = 1.5
FEATURE [Part::Compound] Compound792
  Links = -> [Cylinder1671,Cylinder1678,Cylinder1672,Cylinder1670,Cylinder1676,Cylinder1677,Cylinder1674,Cylinder1675,Cylinder1673,Cylinder1679]
  Placement = pos=(0,0,-11) rot=(0,0,1;0rad)
FEATURE [Part::Box] Box676  label="Krychle675"
  AttacherType = Attacher::AttachEngine3D
  Height = 2
  Length = 6
  Placement = pos=(13,-193,-61) rot=(0,0,1;0rad)
  Width = 6
FEATURE [Part::Box] Box678  label="Krychle677"
  AttacherType = Attacher::AttachEngine3D
  Height = 2
  Length = 6
  Placement = pos=(13,-163,-61) rot=(0,0,1;0rad)
  Width = 6
FEATURE [Part::Compound] Compound793
  Links = -> [Box674,Box675,Box673,Box671,Box672,Box677,Box679,Box680,Box678,Box676]
  Placement = pos=(0,0,15) rot=(0,0,1;0rad)
FEATURE [Part::Cut] Cut614
  Base = -> Cut613
  Tool = -> Compound793
FEATURE [Part::Cut] Cut615
  Base = -> Cut614
  Tool = -> Compound792
FEATURE [Part::Cut] Cut616
  Base = -> Cut615
  Tool = -> Compound791
FEATURE [Part::Cut] Cut617
  Base = -> Cut616
  Tool = -> Compound790
FEATURE [Part::Cylinder] Cylinder1680  label="Válec1680"
  Angle = 360
  AttacherType = Attacher::AttachEngine3D
  Height = 40
  Placement = pos=(-18,-160,100) rot=(0,0,1;0rad)
  Radius = 1.5
FEATURE [Part::Box] Box688  label="Krychle687"
  AttacherType = Attacher::AttachEngine3D
  Height = 2
  Length = 6
  Placement = pos=(7,-126,100) rot=(0,0,1;0rad)
  Width = 6
FEATURE [Part::Cylinder] Cylinder1684  label="Válec1684"
  Angle = 360
  AttacherType = Attacher::AttachEngine3D
  Height = 40
  Placement = pos=(18,-160,100) rot=(0,0,1;0rad)
  Radius = 1.5
FEATURE [Part::Box] Box682  label="Krychle681"
  AttacherType = Attacher::AttachEngine3D
  Height = 15
  Length = 15
  Placement = pos=(-34,-175.5,-65) rot=(0,0,1;0rad)
  Width = 200
FEATURE [Part::Cylinder] Cylinder1685  label="Válec1685"
  Angle = 360
  AttacherType = Attacher::AttachEngine3D
  Height = 40
  Placement = pos=(-18,-140,-35) rot=(0,0,1;0rad)
  Radius = 1.5
FEATURE [Part::Cylinder] Cylinder1682  label="Válec1682"
  Angle = 360
  AttacherType = Attacher::AttachEngine3D
  Height = 40
  Placement = pos=(18,-140,-35) rot=(0,0,1;0rad)
  Radius = 1.5
FEATURE [Part::Box] Box687  label="Krychle686"
  AttacherType = Attacher::AttachEngine3D
  Height = 2
  Length = 6
  Placement = pos=(15,-143,-31) rot=(0,0,1;0rad)
  Width = 6
FEATURE [Part::Cylinder] Cylinder1683  label="Válec1683"
  Angle = 360
  AttacherType = Attacher::AttachEngine3D
  Height = 40
  Placement = pos=(18,-176,-35) rot=(0,0,1;0rad)
  Radius = 1.5
FEATURE [Part::Cylinder] Cylinder1681  label="Válec1681"
  Angle = 360
  AttacherType = Attacher::AttachEngine3D
  Height = 40
  Placement = pos=(0,-123,-35) rot=(0,0,1;0rad)
  Radius = 1.5
FEATURE [Part::Box] Box684  label="Krychle683"
  AttacherType = Attacher::AttachEngine3D
  Height = 2
  Length = 6
  Placement = pos=(-3,-126,-31) rot=(0,0,1;0rad)
  Width = 6
FEATURE [Part::Box] Box685  label="Krychle684"
  AttacherType = Attacher::AttachEngine3D
  Height = 2
  Length = 6
  Placement = pos=(-21,-163,100) rot=(0,0,1;0rad)
  Width = 6
FEATURE [Part::Box] Box686  label="Krychle685"
  AttacherType = Attacher::AttachEngine3D
  Height = 2
  Length = 6
  Placement = pos=(15,-163,100) rot=(0,0,1;0rad)
  Width = 6
FEATURE [Part::Box] Box690  label="Krychle689"
  AttacherType = Attacher::AttachEngine3D
  Height = 2
  Length = 6
  Placement = pos=(15,-179,-31) rot=(0,0,1;0rad)
  Width = 6
FEATURE [Part::Box] Box681  label="Krychle680"
  AttacherType = Attacher::AttachEngine3D
  Height = 15
  Length = 15
  Placement = pos=(19,-175.6,-65) rot=(0,0,1;0rad)
  Width = 200
FEATURE [Part::Compound] Compound794
  Links = -> [Box682,Box681]
  Placement = pos=(0,0,15) rot=(0,0,1;0rad)
FEATURE [Part::Cut] Cut618
  Base = -> Cut617
  Tool = -> Compound794
FEATURE [Part::Box] Box689  label="Krychle688"
  AttacherType = Attacher::AttachEngine3D
  Height = 2
  Length = 6
  Placement = pos=(-21,-179,-31) rot=(0,0,1;0rad)
  Width = 6
FEATURE [Part::Box] Box683  label="Krychle682"
  AttacherType = Attacher::AttachEngine3D
  Height = 2
  Length = 6
  Placement = pos=(-21,-143,-31) rot=(0,0,1;0rad)
  Width = 6
FEATURE [Part::Compound] Compound795
  Links = -> [Box684,Box685,Box689,Box683,Box688,Box686,Box690,Box687]
FEATURE [Part::Cut] Cut619
  Base = -> Cut618
  Tool = -> Compound795
FEATURE [Part::Cylinder] Cylinder1687  label="Válec1687"
  Angle = 360
  AttacherType = Attacher::AttachEngine3D
  Height = 40
  Placement = pos=(-18,-176,-35) rot=(0,0,1;0rad)
  Radius = 1.5
FEATURE [Part::Cylinder] Cylinder1686  label="Válec1686"
  Angle = 360
  AttacherType = Attacher::AttachEngine3D
  Height = 40
  Placement = pos=(-10,-123,100) rot=(0,0,1;0rad)
  Radius = 1.5
FEATURE [Part::Compound] Compound796
  Links = -> [Cylinder1681,Cylinder1686,Cylinder1682,Cylinder1684,Cylinder1683,Cylinder1685,Cylinder1680,Cylinder1687]
FEATURE [Part::Cut] Cut620
  Base = -> Cut619
  Tool = -> Compound796
FEATURE [Part::Cylinder] Cylinder1664  label="Válec1664"
  Angle = 360
  AttacherType = Attacher::AttachEngine3D
  Height = 40
  Placement = pos=(-18,-160,100) rot=(0,0,1;0rad)
  Radius = 1.5
FEATURE [Part::Cylinder] Cylinder1661  label="Válec1661"
  Angle = 360
  AttacherType = Attacher::AttachEngine3D
  Height = 40
  Placement = pos=(18,-160,100) rot=(0,0,1;0rad)
  Radius = 1.5
FEATURE [Part::Compound] Compound789
  Links = -> [Cylinder1662,Cylinder1660,Cylinder1665,Cylinder1661,Cylinder1666,Cylinder1663,Cylinder1664,Cylinder1667]
FEATURE [Part::Cut] Cut609
  Base = -> Cut608
  Tool = -> Compound789
FEATURE [Part::Cut] Cut610
  Base = -> Cut609
  Tool = -> Compound788
FEATURE [Part::Cut] Cut611
  Base = -> Cut610
  Tool = -> Compound787
FEATURE [Part::Compound] Compound797  label="conno_major_redesi_nomoto1"
  Links = -> [Cut611,Cut620]
FEATURE [Part::Fillet] Fillet004  label="L-elb_major-conno-nomoto"
  Base = -> Compound797
  Edges = 2 edges r=5: [Edge418,Edge422]
FEATURE [Mesh::Feature] Mesh  label="L-elb_major-conno-moto (Meshed)"
FEATURE [Mesh::Feature] Mesh001  label="L-elb_major-conno-nomoto (Meshed)"
FEATURE [Part::Box] Box  label="Krychle"
  AttacherType = Attacher::AttachEngine3D
  Height = 18
  Length = 27
  Placement = pos=(-13.5,-66,-7) rot=(0,0,1;0rad)
  Width = 24
FEATURE [Part::Box] Box816  label="Krychle815"
  AttacherType = Attacher::AttachEngine3D
  Height = 15
  Length = 15
  Placement = pos=(-7.5,-174,-4) rot=(0,0,1;0rad)
  Width = 130
FEATURE [Part::Box] Box817  label="Krychle816"
  AttacherType = Attacher::AttachEngine3D
  Height = 50
  Length = 80
  Placement = pos=(-40,-48,-40) rot=(0,0,1;0rad)
  Width = 6
FEATURE [Part::Box] Box818  label="Krychle817"
  AttacherType = Attacher::AttachEngine3D
  Height = 18
  Length = 27
  Placement = pos=(-40,-66,-50) rot=(0,0,1;0rad)
  Width = 28
FEATURE [Part::Box] Box819  label="Krychle818"
  AttacherType = Attacher::AttachEngine3D
  Height = 18
  Length = 27
  Placement = pos=(13,-66,-50) rot=(0,0,1;0rad)
  Width = 28
FEATURE [Part::Box] Box824  label="Krychle823"
  AttacherType = Attacher::AttachEngine3D
  Height = 15
  Length = 15
  Placement = pos=(19,-174,-65) rot=(0,0,1;0rad)
  Width = 130
FEATURE [Part::Box] Box825  label="Krychle824"
  AttacherType = Attacher::AttachEngine3D
  Height = 15
  Length = 15
  Placement = pos=(-34,-174,-65) rot=(0,0,1;0rad)
  Width = 130
FEATURE [Part::Compound] Compound934
  Links = -> [Box825,Box824]
  Placement = pos=(0,-5,25) rot=(0,0,1;0rad)
FEATURE [Part::Box] Box826  label="Krychle825"
  AttacherType = Attacher::AttachEngine3D
  Height = 15
  Length = 15
  Placement = pos=(19,-174,-65) rot=(0,0,1;0rad)
  Width = 130
FEATURE [Part::Box] Box827  label="Krychle826"
  AttacherType = Attacher::AttachEngine3D
  Height = 15
  Length = 15
  Placement = pos=(-34,-174,-65) rot=(0,0,1;0rad)
  Width = 130
FEATURE [Part::Compound] Compound935
  Links = -> [Box827,Box826]
  Placement = pos=(0,0,15) rot=(0,0,1;0rad)
FEATURE [Part::Box] Box828  label="Krychle827"
  AttacherType = Attacher::AttachEngine3D
  Height = 15
  Length = 15
  Placement = pos=(19,-174,-65) rot=(0,0,1;0rad)
  Width = 130
FEATURE [Part::Box] Box829  label="Krychle828"
  AttacherType = Attacher::AttachEngine3D
  Height = 15
  Length = 15
  Placement = pos=(-34,-174,-65) rot=(0,0,1;0rad)
  Width = 130
FEATURE [Part::Cylinder] Cylinder  label="Válec"
  Angle = 360
  AttacherType = Attacher::AttachEngine3D
  Height = 20
  Placement = pos=(-16,-48,-60) rot=(0,0,1;0rad)
  Radius = 1.5
FEATURE [Part::Cylinder] Cylinder2098  label="Válec2098"
  Angle = 360
  AttacherType = Attacher::AttachEngine3D
  Height = 20
  Placement = pos=(-16,-60,-60) rot=(0,0,1;0rad)
  Radius = 1.5
FEATURE [Part::Cylinder] Cylinder2099  label="Válec2099"
  Angle = 360
  AttacherType = Attacher::AttachEngine3D
  Height = 20
  Placement = pos=(-37,-48,-60) rot=(0,0,1;0rad)
  Radius = 1.5
FEATURE [Part::Cylinder] Cylinder2100  label="Válec2100"
  Angle = 360
  AttacherType = Attacher::AttachEngine3D
  Height = 20
  Placement = pos=(-37,-60,-60) rot=(0,0,1;0rad)
  Radius = 1.5
FEATURE [Part::Box] Box830  label="Krychle829"
  AttacherType = Attacher::AttachEngine3D
  Height = 2
  Length = 6
  Placement = pos=(-19,-51,-46) rot=(0,0,1;0rad)
  Width = 6
FEATURE [Part::Box] Box831  label="Krychle830"
  AttacherType = Attacher::AttachEngine3D
  Height = 2
  Length = 6
  Placement = pos=(-19,-63,-46) rot=(0,0,1;0rad)
  Width = 6
FEATURE [Part::Box] Box832  label="Krychle831"
  AttacherType = Attacher::AttachEngine3D
  Height = 2
  Length = 6
  Placement = pos=(-40,-51,-46) rot=(0,0,1;0rad)
  Width = 6
FEATURE [Part::Box] Box833  label="Krychle832"
  AttacherType = Attacher::AttachEngine3D
  Height = 2
  Length = 6
  Placement = pos=(-40,-63,-46) rot=(0,0,1;0rad)
  Width = 6
FEATURE [Part::Cylinder] Cylinder2101  label="Válec2101"
  Angle = 360
  AttacherType = Attacher::AttachEngine3D
  Height = 20
  Placement = pos=(-37,-60,-60) rot=(0,0,1;0rad)
  Radius = 1.5
FEATURE [Part::Cylinder] Cylinder2102  label="Válec2102"
  Angle = 360
  AttacherType = Attacher::AttachEngine3D
  Height = 20
  Placement = pos=(-37,-48,-60) rot=(0,0,1;0rad)
  Radius = 1.5
FEATURE [Part::Cut] Cut757
  Base = -> Box
  Tool = -> Box816
FEATURE [Part::Cut] Cut758
  Base = -> Box817
  Tool = -> Compound934
FEATURE [Part::Cut] Cut759
  Base = -> Box819
  Tool = -> Compound935
FEATURE [Part::Compound] Compound936
  Links = -> [Box829,Box828]
  Placement = pos=(0,0,15) rot=(0,0,1;0rad)
FEATURE [Part::Cut] Cut760
  Base = -> Box818
  Tool = -> Compound936
FEATURE [Part::Compound] Compound937
  Links = -> [Box830,Box831,Box832,Box833]
FEATURE [Part::Compound] Compound938
  Links = -> [Cylinder,Cylinder2098,Cylinder2099,Cylinder2100]
FEATURE [Part::Cut] Cut761
  Base = -> Cut760
  Tool = -> Compound937
FEATURE [Part::Cut] Cut762
  Base = -> Cut761
  Placement = pos=(-8,-4,10) rot=(0,0,1;0rad)
  Tool = -> Compound938
FEATURE [Part::Cylinder] Cylinder2103  label="Válec2103"
  Angle = 360
  AttacherType = Attacher::AttachEngine3D
  Height = 20
  Placement = pos=(-16,-48,-60) rot=(0,0,1;0rad)
  Radius = 1.5
FEATURE [Part::Cylinder] Cylinder2104  label="Válec2104"
  Angle = 360
  AttacherType = Attacher::AttachEngine3D
  Height = 20
  Placement = pos=(-16,-60,-60) rot=(0,0,1;0rad)
  Radius = 1.5
FEATURE [Part::Compound] Compound940
  Links = -> [Cylinder2103,Cylinder2104,Cylinder2102,Cylinder2101]
  Placement = pos=(53,0,0) rot=(0,0,1;0rad)
FEATURE [Part::Box] Box834  label="Krychle833"
  AttacherType = Attacher::AttachEngine3D
  Height = 2
  Length = 6
  Placement = pos=(-19,-51,-46) rot=(0,0,1;0rad)
  Width = 6
FEATURE [Part::Box] Box835  label="Krychle834"
  AttacherType = Attacher::AttachEngine3D
  Height = 2
  Length = 6
  Placement = pos=(-19,-63,-46) rot=(0,0,1;0rad)
  Width = 6
FEATURE [Part::Box] Box836  label="Krychle835"
  AttacherType = Attacher::AttachEngine3D
  Height = 2
  Length = 6
  Placement = pos=(-40,-51,-46) rot=(0,0,1;0rad)
  Width = 6
FEATURE [Part::Box] Box837  label="Krychle836"
  AttacherType = Attacher::AttachEngine3D
  Height = 2
  Length = 6
  Placement = pos=(-40,-63,-46) rot=(0,0,1;0rad)
  Width = 6
FEATURE [Part::Compound] Compound939
  Links = -> [Box834,Box835,Box836,Box837]
  Placement = pos=(53,0,0) rot=(0,0,1;0rad)
FEATURE [Part::Cut] Cut763
  Base = -> Cut759
  Tool = -> Compound939
FEATURE [Part::Cut] Cut764
  Base = -> Cut763
  Placement = pos=(8,-4,10) rot=(0,0,1;0rad)
  Tool = -> Compound940
FEATURE [Part::Box] Box838  label="Krychle837"
  AttacherType = Attacher::AttachEngine3D
  Height = 2
  Length = 6
  Placement = pos=(-19,-51,-46) rot=(0,0,1;0rad)
  Width = 6
FEATURE [Part::Box] Box839  label="Krychle838"
  AttacherType = Attacher::AttachEngine3D
  Height = 2
  Length = 6
  Placement = pos=(-19,-63,-46) rot=(0,0,1;0rad)
  Width = 6
FEATURE [Part::Box] Box840  label="Krychle839"
  AttacherType = Attacher::AttachEngine3D
  Height = 2
  Length = 6
  Placement = pos=(-40,-51,-46) rot=(0,0,1;0rad)
  Width = 6
FEATURE [Part::Box] Box841  label="Krychle840"
  AttacherType = Attacher::AttachEngine3D
  Height = 2
  Length = 6
  Placement = pos=(-40,-63,-46) rot=(0,0,1;0rad)
  Width = 6
FEATURE [Part::Compound] Compound941
  Links = -> [Box838,Box839,Box840,Box841]
  Placement = pos=(-26.5,0,-39) rot=(0,1,0;3.14159rad)
FEATURE [Part::Cut] Cut765
  Base = -> Cut757
  Tool = -> Compound941
FEATURE [Part::Cylinder] Cylinder2105  label="Válec2105"
  Angle = 360
  AttacherType = Attacher::AttachEngine3D
  Height = 20
  Placement = pos=(-37,-60,-60) rot=(0,0,1;0rad)
  Radius = 1.5
FEATURE [Part::Cylinder] Cylinder2106  label="Válec2106"
  Angle = 360
  AttacherType = Attacher::AttachEngine3D
  Height = 20
  Placement = pos=(-16,-48,-60) rot=(0,0,1;0rad)
  Radius = 1.5
FEATURE [Part::Cylinder] Cylinder2107  label="Válec2107"
  Angle = 360
  AttacherType = Attacher::AttachEngine3D
  Height = 20
  Placement = pos=(-37,-48,-60) rot=(0,0,1;0rad)
  Radius = 1.5
FEATURE [Part::Cylinder] Cylinder2108  label="Válec2108"
  Angle = 360
  AttacherType = Attacher::AttachEngine3D
  Height = 20
  Placement = pos=(-16,-60,-60) rot=(0,0,1;0rad)
  Radius = 1.5
FEATURE [Part::Compound] Compound942
  Links = -> [Cylinder2106,Cylinder2108,Cylinder2107,Cylinder2105]
  Placement = pos=(-26.5,0,-39) rot=(0,1,0;3.14159rad)
FEATURE [Part::Cylinder] Cylinder2109  label="Válec2109"
  Angle = 360
  AttacherType = Attacher::AttachEngine3D
  Height = 20
  Placement = pos=(31,21,22) rot=(0,1,0;1.5708rad)
  Radius = 1.5
FEATURE [Part::Cylinder] Cylinder2110  label="Válec2110"
  Angle = 360
  AttacherType = Attacher::AttachEngine3D
  Height = 20
  Placement = pos=(31,-21,22) rot=(0,1,0;1.5708rad)
  Radius = 1.5
FEATURE [Part::Cylinder] Cylinder2111  label="Válec2111"
  Angle = 360
  AttacherType = Attacher::AttachEngine3D
  Height = 20
  Placement = pos=(26,37,19) rot=(0,1,0;1.5708rad)
  Radius = 1.5
FEATURE [Part::Cylinder] Cylinder2112  label="Válec2112"
  Angle = 360
  AttacherType = Attacher::AttachEngine3D
  Height = 20
  Placement = pos=(26,-37,19) rot=(0,1,0;1.5708rad)
  Radius = 1.5
FEATURE [Part::Compound] Compound943
  Links = -> [Cylinder2111,Cylinder2109,Cylinder2110,Cylinder2112]
  Placement = pos=(0,-80,-34) rot=(0,0,1;1.5708rad)
FEATURE [Part::Cylinder] Cylinder2113  label="Válec2113"
  Angle = 360
  AttacherType = Attacher::AttachEngine3D
  Height = 20
  Placement = pos=(28,8,-3) rot=(0,1,0;1.5708rad)
  Radius = 1.5
FEATURE [Part::Cylinder] Cylinder2114  label="Válec2114"
  Angle = 360
  AttacherType = Attacher::AttachEngine3D
  Height = 20
  Placement = pos=(26,37,7) rot=(0,1,0;1.5708rad)
  Radius = 1.5
FEATURE [Part::Cylinder] Cylinder2115  label="Válec2115"
  Angle = 360
  AttacherType = Attacher::AttachEngine3D
  Height = 20
  Placement = pos=(28,-8,-3) rot=(0,1,0;1.5708rad)
  Radius = 1.5
FEATURE [Part::Cylinder] Cylinder2116  label="Válec2116"
  Angle = 360
  AttacherType = Attacher::AttachEngine3D
  Height = 20
  Placement = pos=(26,-37,7) rot=(0,1,0;1.5708rad)
  Radius = 1.5
FEATURE [Part::Compound] Compound944
  Links = -> [Cylinder2116,Cylinder2113,Cylinder2114,Cylinder2115]
  Placement = pos=(0,-80,-34) rot=(0,0,1;1.5708rad)
FEATURE [Part::Cut] Cut766
  Base = -> Cut765
  Placement = pos=(26.5,-4,-1) rot=(0,0,1;0rad)
  Tool = -> Compound942
FEATURE [Part::Cut] Cut767
  Base = -> Cut758
  Tool = -> Compound943
FEATURE [Part::Cut] Cut768  label="xori_xoro"
  Base = -> Cut767
  Tool = -> Compound944
FEATURE [Part::Box] Box843  label="Krychle842"
  AttacherType = Attacher::AttachEngine3D
  Height = 18
  Length = 27
  Placement = pos=(-13.5,-66,-7) rot=(0,0,1;0rad)
  Width = 24
FEATURE [Part::Box] Box844  label="Krychle843"
  AttacherType = Attacher::AttachEngine3D
  Height = 15
  Length = 15
  Placement = pos=(-7.5,-174,-4) rot=(0,0,1;0rad)
  Width = 130
FEATURE [Part::Cylinder] Cylinder2133  label="Válec2133"
  Angle = 360
  AttacherType = Attacher::AttachEngine3D
  Height = 20
  Placement = pos=(-37,-60,-60) rot=(0,0,1;0rad)
  Radius = 1.5
FEATURE [Part::Box] Box845  label="Krychle844"
  AttacherType = Attacher::AttachEngine3D
  Height = 2
  Length = 6
  Placement = pos=(-40,-51,-46) rot=(0,0,1;0rad)
  Width = 6
FEATURE [Part::Box] Box846  label="Krychle845"
  AttacherType = Attacher::AttachEngine3D
  Height = 2
  Length = 6
  Placement = pos=(-19,-51,-46) rot=(0,0,1;0rad)
  Width = 6
FEATURE [Part::Box] Box847  label="Krychle846"
  AttacherType = Attacher::AttachEngine3D
  Height = 2
  Length = 6
  Placement = pos=(-19,-63,-46) rot=(0,0,1;0rad)
  Width = 6
FEATURE [Part::Box] Box848  label="Krychle847"
  AttacherType = Attacher::AttachEngine3D
  Height = 2
  Length = 6
  Placement = pos=(-40,-63,-46) rot=(0,0,1;0rad)
  Width = 6
FEATURE [Part::Cylinder] Cylinder2134  label="Válec2134"
  Angle = 360
  AttacherType = Attacher::AttachEngine3D
  Height = 20
  Placement = pos=(-16,-48,-60) rot=(0,0,1;0rad)
  Radius = 1.5
FEATURE [Part::Cylinder] Cylinder2135  label="Válec2135"
  Angle = 360
  AttacherType = Attacher::AttachEngine3D
  Height = 20
  Placement = pos=(-37,-48,-60) rot=(0,0,1;0rad)
  Radius = 1.5
FEATURE [Part::Cylinder] Cylinder2136  label="Válec2136"
  Angle = 360
  AttacherType = Attacher::AttachEngine3D
  Height = 20
  Placement = pos=(-16,-60,-60) rot=(0,0,1;0rad)
  Radius = 1.5
FEATURE [Part::Cut] Cut775
  Base = -> Box843
  Tool = -> Box844
FEATURE [Part::Compound] Compound952
  Links = -> [Cylinder2134,Cylinder2136,Cylinder2135,Cylinder2133]
  Placement = pos=(-26.5,0,-39) rot=(0,1,0;3.14159rad)
FEATURE [Part::Compound] Compound953
  Links = -> [Box846,Box847,Box845,Box848]
  Placement = pos=(-26.5,0,-39) rot=(0,1,0;3.14159rad)
FEATURE [Part::Cut] Cut776
  Base = -> Cut775
  Tool = -> Compound953
FEATURE [Part::Cut] Cut777
  Base = -> Cut776
  Placement = pos=(-26.5,-4,-1) rot=(0,0,1;0rad)
  Tool = -> Compound952
FEATURE [Part::Cylinder] Cylinder2282  label="Válec2282"
  Angle = 360
  AttacherType = Attacher::AttachEngine3D
  Height = 20
  Placement = pos=(28,8,-3) rot=(0,1,0;1.5708rad)
  Radius = 1.5
FEATURE [Part::Cylinder] Cylinder2283  label="Válec2283"
  Angle = 360
  AttacherType = Attacher::AttachEngine3D
  Height = 20
  Placement = pos=(26,37,7) rot=(0,1,0;1.5708rad)
  Radius = 1.5
FEATURE [Part::Cylinder] Cylinder2284  label="Válec2284"
  Angle = 360
  AttacherType = Attacher::AttachEngine3D
  Height = 20
  Placement = pos=(28,-8,-3) rot=(0,1,0;1.5708rad)
  Radius = 1.5
FEATURE [Part::Cylinder] Cylinder2285  label="Válec2285"
  Angle = 360
  AttacherType = Attacher::AttachEngine3D
  Height = 20
  Placement = pos=(26,-37,7) rot=(0,1,0;1.5708rad)
  Radius = 1.5
FEATURE [Part::Compound] Compound994  label="xori_drzaky"
  Links = -> [Cut762,Cut764,Cut766,Cut777]
FEATURE [Part::Compound] Compound996
  Links = -> [Cylinder2285,Cylinder2282,Cylinder2283,Cylinder2284]
  Placement = pos=(0,-80,-34) rot=(0,0,1;1.5708rad)
FEATURE [Part::Cylinder] Cylinder2298  label="Válec2298"
  Angle = 360
  AttacherType = Attacher::AttachEngine3D
  Height = 20
  Placement = pos=(26,37,7) rot=(0,1,0;1.5708rad)
  Radius = 3
FEATURE [Part::Cylinder] Cylinder2300  label="Válec2300"
  Angle = 360
  AttacherType = Attacher::AttachEngine3D
  Height = 20
  Placement = pos=(26,-37,7) rot=(0,1,0;1.5708rad)
  Radius = 3
FEATURE [Part::Compound] Compound1000
  Links = -> [Cylinder2300,Cylinder2298]
  Placement = pos=(0,-91,-34) rot=(0,0,1;1.5708rad)
FEATURE [Part::Cylinder] Cylinder2301  label="Válec2301"
  Angle = 360
  AttacherType = Attacher::AttachEngine3D
  Height = 30
  Placement = pos=(26,37,7) rot=(0,1,0;1.5708rad)
  Radius = 3
FEATURE [Part::Cylinder] Cylinder2302  label="Válec2302"
  Angle = 360
  AttacherType = Attacher::AttachEngine3D
  Height = 30
  Placement = pos=(26,-37,7) rot=(0,1,0;1.5708rad)
  Radius = 3
FEATURE [Part::Compound] Compound1001
  Links = -> [Cylinder2302,Cylinder2301]
  Placement = pos=(0,-101,-34) rot=(0,0,1;1.5708rad)
FEATURE [Part::Cut] Cut820
  Base = -> Cut768
  Tool = -> Compound1000
FEATURE [Part::Chamfer] Chamfer064
  Base = -> Cut820
  Edges = 1 edges r=4: [Edge24]
FEATURE [Part::Cut] Cut821
  Base = -> Compound994
  Tool = -> Compound1001
FEATURE [Part::Cut] Cut822
  Base = -> Cut821
  Tool = -> Compound996
FEATURE [Part::Chamfer] Chamfer065
  Base = -> Cut822
  Edges = 2 edges r=4: [Edge4,Edge141]
FEATURE [Part::Chamfer] Chamfer066
  Base = -> Chamfer065
  Edges = 8 edges r=2: [Edge3,Edge26,Edge123,Edge133,Edge223,Edge235,Edge319,Edge331]
FEATURE [Part::Compound] Compound1002  label="L-elb_xorior-old"
  Links = -> [Chamfer064,Chamfer066]
FEATURE [Part::Torus] Torus002  label="Anuloid002"
  Angle1 = -180
  Angle2 = 180
  Angle3 = 360
  AttacherType = Attacher::AttachEngine3D
  Placement = pos=(0,0,20) rot=(0,0,1;0rad)
  Radius1 = 32
  Radius2 = 3.1
FEATURE [Part::Cylinder] Cylinder190  label="Válec190"
  Angle = 360
  AttacherType = Attacher::AttachEngine3D
  Height = 20
  Placement = pos=(25.4558,-25.4558,0) rot=(0,0,-1;0.785398rad)
  Radius = 1.5
FEATURE [Part::Cylinder] Cylinder188  label="Válec188"
  Angle = 360
  AttacherType = Attacher::AttachEngine3D
  Height = 6
  Radius = 32
FEATURE [Part::Cylinder] Cylinder189  label="Válec189"
  Angle = 360
  AttacherType = Attacher::AttachEngine3D
  Height = 6
  Radius = 40
FEATURE [Part::Cylinder] Cylinder193  label="Válec193"
  Angle = 360
  AttacherType = Attacher::AttachEngine3D
  Height = 20
  Placement = pos=(25.4558,25.4558,0) rot=(0,0,1;0.785398rad)
  Radius = 1.5
FEATURE [Part::Cylinder] Cylinder196  label="Válec196"
  Angle = 360
  AttacherType = Attacher::AttachEngine3D
  Height = 20
  Placement = pos=(1.2e-14,-36,0) rot=(0,0,-1;1.5708rad)
  Radius = 1.5
FEATURE [Part::FeaturePython] wormgear032  # WARN: FeaturePython — macro-defined, semantics opaque (R4)
  AttacherType = Attacher::AttachEngine3D
  beta = 34.5085
  clearance = 0.25
  diameter = 48
  head = 0
  height = 20
  module = 1
  pressure_angle = 20
  reverse_pitch = true
  teeth = 33
  version = 0.0.3
FEATURE [Part::FeaturePython] wormgear033  # WARN: FeaturePython — macro-defined, semantics opaque (R4)
  AttacherType = Attacher::AttachEngine3D
  beta = 34.5085
  clearance = 0.25
  diameter = 48
  head = 0
  height = 20
  module = 1
  pressure_angle = 20
  reverse_pitch = false
  teeth = 33
  version = 0.0.3
FEATURE [Part::Cut] Cut141
  Base = -> Cylinder188
  Tool = -> wormgear033
FEATURE [Part::Cut] Cut142
  Base = -> Cylinder189
  Placement = pos=(0,0,6) rot=(0,0,-1;0.017453rad)
  Tool = -> wormgear032
FEATURE [Part::Cylinder] Cylinder191  label="Válec191"
  Angle = 360
  AttacherType = Attacher::AttachEngine3D
  Height = 20
  Placement = pos=(-25.4558,-25.4558,0) rot=(0,0,1;3.92699rad)
  Radius = 1.5
FEATURE [Part::Cylinder] Cylinder197  label="Válec197"
  Angle = 360
  AttacherType = Attacher::AttachEngine3D
  Height = 20
  Placement = pos=(-36,-1.1e-14,0) rot=(0,0,1;3.14159rad)
  Radius = 1.5
FEATURE [Part::Box] Box055  label="Krychle055"
  AttacherType = Attacher::AttachEngine3D
  Height = 2
  Length = 6
  Placement = pos=(22.8728,-12.7214,-2) rot=(0,0,-1;0.392699rad)
  Width = 6
FEATURE [Part::Cylinder] Cylinder194  label="Válec194"
  Angle = 360
  AttacherType = Attacher::AttachEngine3D
  Height = 20
  Placement = pos=(36,0,0) rot=(0,0,1;0rad)
  Radius = 1.5
FEATURE [Part::Cylinder] Cylinder192  label="Válec192"
  Angle = 360
  AttacherType = Attacher::AttachEngine3D
  Height = 20
  Placement = pos=(-25.4558,25.4558,0) rot=(0,0,1;2.35619rad)
  Radius = 1.5
FEATURE [Part::Cylinder] Cylinder195  label="Válec195"
  Angle = 360
  AttacherType = Attacher::AttachEngine3D
  Height = 20
  Placement = pos=(-4e-15,36,0) rot=(0,0,1;1.5708rad)
  Radius = 1.5
FEATURE [Part::Compound] Compound127
  Links = -> [Cylinder190,Cylinder194,Cylinder193,Cylinder195,Cylinder192,Cylinder197,Cylinder191,Cylinder196]
FEATURE [Part::Cut] Cut144
  Base = -> Cut142
  Tool = -> Compound127
FEATURE [Part::Box] Box061  label="Krychle061"
  AttacherType = Attacher::AttachEngine3D
  Height = 2
  Length = 6
  Placement = pos=(25.1689,7.17813,-2) rot=(0,0,1;0.392699rad)
  Width = 6
FEATURE [Part::Cylinder] Cylinder198  label="Válec198"
  Angle = 360
  AttacherType = Attacher::AttachEngine3D
  Height = 10
  Placement = pos=(11.0978,-26.7925,-10) rot=(0,0,-1;1.1781rad)
  Radius = 1.5
FEATURE [Part::FeaturePython] Tube010  # WARN: FeaturePython — macro-defined, semantics opaque (R4)
  AttacherType = Attacher::AttachEngine3D
  Height = 6
  InnerRadius = 26
  OuterRadius = 32
  Placement = pos=(0,0,-6) rot=(0,0,1;0rad)
FEATURE [Part::Box] Box056  label="Krychle056"
  AttacherType = Attacher::AttachEngine3D
  Height = 2
  Length = 6
  Placement = pos=(-7.17813,25.1689,-2) rot=(0,0,1;1.96349rad)
  Width = 6
FEATURE [Part::Box] Box058  label="Krychle058"
  AttacherType = Attacher::AttachEngine3D
  Height = 2
  Length = 6
  Placement = pos=(12.7214,22.8728,-2) rot=(0,0,1;1.1781rad)
  Width = 6
FEATURE [Part::Box] Box059  label="Krychle059"
  AttacherType = Attacher::AttachEngine3D
  Height = 2
  Length = 6
  Placement = pos=(-25.1689,-7.17813,-2) rot=(0,0,1;3.53429rad)
  Width = 6
FEATURE [Part::Cylinder] Cylinder199  label="Válec199"
  Angle = 360
  AttacherType = Attacher::AttachEngine3D
  Height = 10
  Placement = pos=(26.7925,11.0978,-10) rot=(0,0,1;0.392699rad)
  Radius = 1.5
FEATURE [Part::Box] Box057  label="Krychle057"
  AttacherType = Attacher::AttachEngine3D
  Height = 6
  Length = 2
  Placement = pos=(30,34,4) rot=(0,0,1;0rad)
  Width = 6
FEATURE [Part::Box] Box060  label="Krychle060"
  AttacherType = Attacher::AttachEngine3D
  Height = 2
  Length = 6
  Placement = pos=(-22.8728,12.7214,-2) rot=(0,0,1;2.74889rad)
  Width = 6
FEATURE [Part::Box] Box062  label="Krychle062"
  AttacherType = Attacher::AttachEngine3D
  Height = 2
  Length = 6
  Placement = pos=(-12.7214,-22.8728,-2) rot=(0,0,-1;1.96349rad)
  Width = 6
FEATURE [Part::Cylinder] Cylinder203  label="Válec203"
  Angle = 360
  AttacherType = Attacher::AttachEngine3D
  Height = 10
  Placement = pos=(-11.0978,-26.7925,-10) rot=(0,0,-1;1.96349rad)
  Radius = 1.5
FEATURE [Part::Cylinder] Cylinder202  label="Válec202"
  Angle = 360
  AttacherType = Attacher::AttachEngine3D
  Height = 10
  Placement = pos=(-26.7925,-11.0978,-10) rot=(0,0,1;3.53429rad)
  Radius = 1.5
FEATURE [Part::Cylinder] Cylinder205  label="Válec205"
  Angle = 360
  AttacherType = Attacher::AttachEngine3D
  Height = 10
  Placement = pos=(26.7925,-11.0978,-10) rot=(0,0,-1;0.392699rad)
  Radius = 1.5
FEATURE [Part::Cylinder] Cylinder201  label="Válec201"
  Angle = 360
  AttacherType = Attacher::AttachEngine3D
  Height = 10
  Placement = pos=(-11.0978,26.7925,-10) rot=(0,0,1;1.96349rad)
  Radius = 1.5
FEATURE [Part::Cylinder] Cylinder200  label="Válec200"
  Angle = 360
  AttacherType = Attacher::AttachEngine3D
  Height = 10
  Placement = pos=(11.0978,26.7925,-10) rot=(0,0,1;1.1781rad)
  Radius = 1.5
FEATURE [Part::Box] Box063  label="Krychle063"
  AttacherType = Attacher::AttachEngine3D
  Height = 2
  Length = 6
  Placement = pos=(7.17813,-25.1689,-2) rot=(0,0,-1;1.1781rad)
  Width = 6
FEATURE [Part::Compound] Compound126
  Links = -> [Box061,Box058,Box056,Box060,Box059,Box062,Box063,Box055]
FEATURE [Part::Cut] Cut151
  Base = -> Tube010
  Tool = -> Compound126
FEATURE [Part::Cylinder] Cylinder204  label="Válec204"
  Angle = 360
  AttacherType = Attacher::AttachEngine3D
  Height = 10
  Placement = pos=(-26.7925,11.0978,-10) rot=(0,0,1;2.74889rad)
  Radius = 1.5
FEATURE [Part::Compound] Compound125
  Links = -> [Cylinder199,Cylinder200,Cylinder201,Cylinder204,Cylinder202,Cylinder203,Cylinder198,Cylinder205]
FEATURE [Part::Cut] Cut136
  Base = -> Cut151
  Tool = -> Compound125
FEATURE [Part::Cylinder] Cylinder206  label="Válec206"
  Angle = 360
  AttacherType = Attacher::AttachEngine3D
  Height = 20
  Placement = pos=(26,37,7) rot=(0,1,0;1.5708rad)
  Radius = 1.5
FEATURE [Part::Cylinder] Cylinder210  label="Válec210"
  Angle = 360
  AttacherType = Attacher::AttachEngine3D
  Height = 30
  Placement = pos=(36,0,-24) rot=(0,0,1;0rad)
  Radius = 4
FEATURE [Part::Cylinder] Cylinder207  label="Válec207"
  Angle = 360
  AttacherType = Attacher::AttachEngine3D
  Height = 6
  Placement = pos=(0,0,6) rot=(0,0,1;0rad)
  Radius = 40
FEATURE [Part::Cylinder] Cylinder208  label="Válec208"
  Angle = 360
  AttacherType = Attacher::AttachEngine3D
  Height = 20
  Placement = pos=(36,0,0) rot=(0,0,1;0rad)
  Radius = 1.5
FEATURE [Part::Box] Box064  label="Krychle064"
  AttacherType = Attacher::AttachEngine3D
  Height = 6
  Length = 40
  Placement = pos=(0,0,6) rot=(0,0,1;0rad)
  Width = 40
FEATURE [Part::Cut] Cut138
  Base = -> Box064
  Tool = -> Cylinder207
FEATURE [Part::Cut] Cut135
  Base = -> Cut138
  Tool = -> Box057
FEATURE [Part::Cut] Cut134
  Base = -> Cut135
  Tool = -> Cylinder206
FEATURE [Part::Box] Box065  label="Krychle065"
  AttacherType = Attacher::AttachEngine3D
  Height = 6
  Length = 2
  Placement = pos=(30,34,4) rot=(0,0,1;0rad)
  Width = 6
FEATURE [Part::Cylinder] Cylinder209  label="Válec209"
  Angle = 360
  AttacherType = Attacher::AttachEngine3D
  Height = 20
  Placement = pos=(25.4558,25.4558,0) rot=(0,0,1;0.785398rad)
  Radius = 1.5
FEATURE [Part::Box] Box066  label="Krychle066"
  AttacherType = Attacher::AttachEngine3D
  Height = 18
  Length = 14
  Placement = pos=(26,0,-6) rot=(0,0,1;0rad)
  Width = 40
FEATURE [Part::Cylinder] Cylinder212  label="Válec212"
  Angle = 360
  AttacherType = Attacher::AttachEngine3D
  Height = 20
  Placement = pos=(26,37,7) rot=(0,1,0;1.5708rad)
  Radius = 1.5
FEATURE [Part::Cylinder] Cylinder213  label="Válec213"
  Angle = 360
  AttacherType = Attacher::AttachEngine3D
  Height = 30
  Placement = pos=(25.4558,25.4558,-24) rot=(0,0,1;0.785398rad)
  Radius = 4
FEATURE [Part::Box] Box068  label="Krychle068"
  AttacherType = Attacher::AttachEngine3D
  Height = 6
  Length = 2
  Placement = pos=(30,34,4) rot=(0,0,1;0rad)
  Width = 6
FEATURE [Part::Cylinder] Cylinder214  label="Válec214"
  Angle = 360
  AttacherType = Attacher::AttachEngine3D
  Height = 20
  Placement = pos=(28,16,-3) rot=(0,1,0;1.5708rad)
  Radius = 1.5
FEATURE [Part::Compound] Compound132
  Links = -> [Cylinder214,Cylinder212]
FEATURE [Part::Cylinder] Cylinder215  label="Válec215"
  Angle = 360
  AttacherType = Attacher::AttachEngine3D
  Height = 20
  Placement = pos=(26,37,7) rot=(0,1,0;1.5708rad)
  Radius = 1.5
FEATURE [Part::Cylinder] Cylinder216  label="Válec216"
  Angle = 360
  AttacherType = Attacher::AttachEngine3D
  Height = 20
  Placement = pos=(36,0,0) rot=(0,0,1;0rad)
  Radius = 1.5
FEATURE [Part::Cylinder] Cylinder211  label="Válec211"
  Angle = 360
  AttacherType = Attacher::AttachEngine3D
  Height = 12
  Placement = pos=(0,0,-6) rot=(0,0,1;0rad)
  Radius = 32
FEATURE [Part::Cut] Cut162
  Base = -> Box066
  Tool = -> Cylinder211
FEATURE [Part::Cut] Cut137
  Base = -> Cut162
  Tool = -> Cylinder210
FEATURE [Part::Cut] Cut140
  Base = -> Cut137
  Tool = -> Cylinder208
FEATURE [Part::Cut] Cut163
  Base = -> Cut140
  Tool = -> Cylinder213
FEATURE [Part::Cut] Cut146
  Base = -> Cut163
  Tool = -> Cylinder209
FEATURE [Part::Cut] Cut164
  Base = -> Cut146
  Tool = -> Compound132
FEATURE [Part::Box] Box067  label="Krychle067"
  AttacherType = Attacher::AttachEngine3D
  Height = 6
  Length = 2
  Placement = pos=(32,13,-6) rot=(0,0,1;0rad)
  Width = 6
FEATURE [Part::Compound] Compound131
  Links = -> [Box067,Box065]
FEATURE [Part::Cut] Cut145
  Base = -> Cut164
  Tool = -> Compound131
FEATURE [Part::Box] Box069  label="Krychle069"
  AttacherType = Attacher::AttachEngine3D
  Height = 6
  Length = 2
  Placement = pos=(30,34,4) rot=(0,0,1;0rad)
  Width = 6
FEATURE [Part::Cylinder] Cylinder221  label="Válec221"
  Angle = 360
  AttacherType = Attacher::AttachEngine3D
  Height = 6
  Placement = pos=(0,0,6) rot=(0,0,1;0rad)
  Radius = 40
FEATURE [Part::Box] Box070  label="Krychle070"
  AttacherType = Attacher::AttachEngine3D
  Height = 12
  Length = 18
  Placement = pos=(8,10,-6) rot=(0,0,1;0rad)
  Width = 30
FEATURE [Part::Box] Box071  label="Krychle071"
  AttacherType = Attacher::AttachEngine3D
  Height = 6
  Length = 40
  Placement = pos=(0,0,6) rot=(0,0,1;0rad)
  Width = 40
FEATURE [Part::Cut] Cut152
  Base = -> Box071
  Tool = -> Cylinder221
FEATURE [Part::Cut] Cut150
  Base = -> Cut152
  Tool = -> Box069
FEATURE [Part::Cut] Cut143
  Base = -> Cut150
  Tool = -> Cylinder215
FEATURE [Part::Cylinder] Cylinder220  label="Válec220"
  Angle = 360
  AttacherType = Attacher::AttachEngine3D
  Height = 30
  Placement = pos=(25.4558,25.4558,-24) rot=(0,0,1;0.785398rad)
  Radius = 4
FEATURE [Part::Cylinder] Cylinder217  label="Válec217"
  Angle = 360
  AttacherType = Attacher::AttachEngine3D
  Height = 12
  Placement = pos=(0,0,-6) rot=(0,0,1;0rad)
  Radius = 32
FEATURE [Part::Cylinder] Cylinder218  label="Válec218"
  Angle = 360
  AttacherType = Attacher::AttachEngine3D
  Height = 12
  Placement = pos=(0,0,-6) rot=(0,0,1;0rad)
  Radius = 32
FEATURE [Part::Cylinder] Cylinder219  label="Válec219"
  Angle = 360
  AttacherType = Attacher::AttachEngine3D
  Height = 12
  Placement = pos=(6,41.8,-6) rot=(0,0,1;0rad)
  Radius = 11
FEATURE [Part::Cut] Cut148
  Base = -> Box070
  Tool = -> Cylinder219
FEATURE [Part::Cut] Cut147
  Base = -> Cut148
  Tool = -> Cylinder218
FEATURE [Part::Cut] Cut149
  Base = -> Cut147
  Tool = -> Cylinder220
FEATURE [Part::Compound] Compound133
  Links = -> [Cut145,Cut149,Cut134]
FEATURE [Part::Box] Box072  label="Krychle072"
  AttacherType = Attacher::AttachEngine3D
  Height = 18
  Length = 14
  Placement = pos=(26,0,-6) rot=(0,0,1;0rad)
  Width = 40
FEATURE [Part::Cut] Cut160
  Base = -> Box072
  Tool = -> Cylinder217
FEATURE [Part::Cylinder] Cylinder225  label="Válec225"
  Angle = 360
  AttacherType = Attacher::AttachEngine3D
  Height = 12
  Placement = pos=(0,0,-6) rot=(0,0,1;0rad)
  Radius = 32
FEATURE [Part::Box] Box074  label="Krychle074"
  AttacherType = Attacher::AttachEngine3D
  Height = 6
  Length = 2
  Placement = pos=(32,13,-6) rot=(0,0,1;0rad)
  Width = 6
FEATURE [Part::Compound] Compound128
  Links = -> [Box074,Box068]
FEATURE [Part::Cylinder] Cylinder226  label="Válec226"
  Angle = 360
  AttacherType = Attacher::AttachEngine3D
  Height = 20
  Placement = pos=(26,37,7) rot=(0,1,0;1.5708rad)
  Radius = 1.5
FEATURE [Part::Cylinder] Cylinder222  label="Válec222"
  Angle = 360
  AttacherType = Attacher::AttachEngine3D
  Height = 20
  Placement = pos=(25.4558,25.4558,0) rot=(0,0,1;0.785398rad)
  Radius = 1.5
FEATURE [Part::Box] Box073  label="Krychle073"
  AttacherType = Attacher::AttachEngine3D
  Height = 12
  Length = 18
  Placement = pos=(8,10,-6) rot=(0,0,1;0rad)
  Width = 30
FEATURE [Part::Cylinder] Cylinder224  label="Válec224"
  Angle = 360
  AttacherType = Attacher::AttachEngine3D
  Height = 30
  Placement = pos=(25.4558,25.4558,-24) rot=(0,0,1;0.785398rad)
  Radius = 4
FEATURE [Part::Cylinder] Cylinder223  label="Válec223"
  Angle = 360
  AttacherType = Attacher::AttachEngine3D
  Height = 30
  Placement = pos=(36,0,-24) rot=(0,0,1;0rad)
  Radius = 4
FEATURE [Part::Cut] Cut139
  Base = -> Cut160
  Tool = -> Cylinder223
FEATURE [Part::Cut] Cut161
  Base = -> Cut139
  Tool = -> Cylinder216
FEATURE [Part::Cut] Cut157
  Base = -> Cut161
  Tool = -> Cylinder224
FEATURE [Part::Cut] Cut153
  Base = -> Cut157
  Tool = -> Cylinder222
FEATURE [Part::Cylinder] Cylinder228  label="Válec228"
  Angle = 360
  AttacherType = Attacher::AttachEngine3D
  Height = 30
  Placement = pos=(25.4558,25.4558,-24) rot=(0,0,1;0.785398rad)
  Radius = 4
FEATURE [Part::Cylinder] Cylinder229  label="Válec229"
  Angle = 360
  AttacherType = Attacher::AttachEngine3D
  Height = 20
  Placement = pos=(28,16,-3) rot=(0,1,0;1.5708rad)
  Radius = 1.5
FEATURE [Part::Compound] Compound130
  Links = -> [Cylinder229,Cylinder226]
FEATURE [Part::Cut] Cut159
  Base = -> Cut153
  Tool = -> Compound130
FEATURE [Part::Cut] Cut154
  Base = -> Cut159
  Tool = -> Compound128
FEATURE [Part::Cylinder] Cylinder227  label="Válec227"
  Angle = 360
  AttacherType = Attacher::AttachEngine3D
  Height = 12
  Placement = pos=(6,41.8,-6) rot=(0,0,1;0rad)
  Radius = 11
FEATURE [Part::Cut] Cut155
  Base = -> Box073
  Tool = -> Cylinder227
FEATURE [Part::Cut] Cut158
  Base = -> Cut155
  Tool = -> Cylinder225
FEATURE [Part::Cut] Cut156
  Base = -> Cut158
  Tool = -> Cylinder228
FEATURE [Part::Compound] Compound129
  Links = -> [Cut154,Cut156,Cut143]
FEATURE [Part::Mirroring] mirror001  label="Compound123 (mirrored)001"
  Base = (1,0,0)
  Normal = (1e-16,-1,0)
  Source = -> Compound129
FEATURE [Part::Compound] Compound134  label="jointovina_micro_monoblok_hrubo001"
  Links = -> [Compound133,mirror001,Cut136,Cut141,Cut144]
FEATURE [Part::Fillet] Fillet001  label="jointovina_micro_monoblok"
  Base = -> Compound134
  Edges = 2 edges r=8: [Edge90,Edge230]
  Placement = pos=(0,1,-34) rot=(0,0,-1;1.5708rad)
FEATURE [Part::Box] Box082  label="Krychle082"
  AttacherType = Attacher::AttachEngine3D
  Height = 2
  Length = 8
  Placement = pos=(-25.46,-21.21,14) rot=(0,0,1;3.92699rad)
  Width = 6
FEATURE [Part::Box] Box078  label="Krychle078"
  AttacherType = Attacher::AttachEngine3D
  Height = 2
  Length = 8
  Placement = pos=(25.46,21.21,14) rot=(0,0,1;0.785398rad)
  Width = 6
FEATURE [Part::Box] Box079  label="Krychle079"
  AttacherType = Attacher::AttachEngine3D
  Height = 2
  Length = 8
  Placement = pos=(3,33,14) rot=(0,0,1;1.5708rad)
  Width = 6
FEATURE [Part::FeaturePython] Tube011  # WARN: FeaturePython — macro-defined, semantics opaque (R4)
  AttacherType = Attacher::AttachEngine3D
  Height = 13
  InnerRadius = 33
  OuterRadius = 40
  Placement = pos=(0,0,12) rot=(0,0,1;0rad)
FEATURE [Part::Cut] Cut166
  Base = -> Tube011
  Tool = -> Torus002
FEATURE [Part::Box] Box077  label="Krychle077"
  AttacherType = Attacher::AttachEngine3D
  Height = 2
  Length = 8
  Placement = pos=(33,-3,14) rot=(0,0,1;0rad)
  Width = 6
FEATURE [Part::Box] Box080  label="Krychle080"
  AttacherType = Attacher::AttachEngine3D
  Height = 2
  Length = 8
  Placement = pos=(-21.21,25.46,14) rot=(0,0,1;2.35619rad)
  Width = 6
FEATURE [Part::Box] Box081  label="Krychle081"
  AttacherType = Attacher::AttachEngine3D
  Height = 2
  Length = 8
  Placement = pos=(-33,3,14) rot=(0,0,1;3.14159rad)
  Width = 6
FEATURE [Part::Cylinder] Cylinder231  label="Válec231"
  Angle = 360
  AttacherType = Attacher::AttachEngine3D
  Height = 18
  Placement = pos=(25.4558,25.4558,0) rot=(0,0,1;0.785398rad)
  Radius = 1.5
FEATURE [Part::Box] Box083  label="Krychle083"
  AttacherType = Attacher::AttachEngine3D
  Height = 2
  Length = 8
  Placement = pos=(-3,-33,14) rot=(0,0,-1;1.5708rad)
  Width = 6
FEATURE [Part::Box] Box084  label="Krychle084"
  AttacherType = Attacher::AttachEngine3D
  Height = 2
  Length = 8
  Placement = pos=(21.21,-25.46,14) rot=(0,0,-1;0.785398rad)
  Width = 6
FEATURE [Part::Compound] Compound136
  Links = -> [Box077,Box078,Box079,Box080,Box081,Box082,Box083,Box084]
FEATURE [Part::Cylinder] Cylinder230  label="Válec230"
  Angle = 360
  AttacherType = Attacher::AttachEngine3D
  Height = 18
  Placement = pos=(36,0,0) rot=(0,0,1;0rad)
  Radius = 1.5
FEATURE [Part::Cylinder] Cylinder235  label="Válec235"
  Angle = 360
  AttacherType = Attacher::AttachEngine3D
  Height = 18
  Placement = pos=(-25.4558,-25.4558,0) rot=(0,0,1;3.92699rad)
  Radius = 1.5
FEATURE [Part::Box] Box092  label="Krychle092"
  AttacherType = Attacher::AttachEngine3D
  Height = 6
  Length = 2
  Placement = pos=(34,18,19) rot=(0,0,1;0rad)
  Width = 6
FEATURE [Part::Cylinder] Cylinder246  label="Válec246"
  Angle = 360
  AttacherType = Attacher::AttachEngine3D
  Height = 20
  Placement = pos=(31,21,22) rot=(0,1,0;1.5708rad)
  Radius = 1.5
FEATURE [Part::Box] Box090  label="Krychle090"
  AttacherType = Attacher::AttachEngine3D
  Height = 13
  Length = 40
  Placement = pos=(0,-40,12) rot=(0,0,1;0rad)
  Width = 80
FEATURE [Part::Cylinder] Cylinder245  label="Válec245"
  Angle = 360
  AttacherType = Attacher::AttachEngine3D
  Height = 20
  Placement = pos=(26,37,19) rot=(0,1,0;1.5708rad)
  Radius = 1.5
FEATURE [Part::Box] Box093  label="Krychle093"
  AttacherType = Attacher::AttachEngine3D
  Height = 6
  Length = 2
  Placement = pos=(30,-40,16) rot=(0,0,1;0rad)
  Width = 6
FEATURE [Part::Cylinder] Cylinder234  label="Válec234"
  Angle = 360
  AttacherType = Attacher::AttachEngine3D
  Height = 18
  Placement = pos=(-36,-1.1e-14,0) rot=(0,0,1;3.14159rad)
  Radius = 1.5
FEATURE [Part::Cylinder] Cylinder247  label="Válec247"
  Angle = 360
  AttacherType = Attacher::AttachEngine3D
  Height = 20
  Placement = pos=(31,-21,22) rot=(0,1,0;1.5708rad)
  Radius = 1.5
FEATURE [Part::Box] Box091  label="Krychle091"
  AttacherType = Attacher::AttachEngine3D
  Height = 6
  Length = 2
  Placement = pos=(30,34,16) rot=(0,0,1;0rad)
  Width = 6
FEATURE [Part::Cylinder] Cylinder248  label="Válec248"
  Angle = 360
  AttacherType = Attacher::AttachEngine3D
  Height = 20
  Placement = pos=(26,-37,19) rot=(0,1,0;1.5708rad)
  Radius = 1.5
FEATURE [Part::Compound] Compound146
  Links = -> [Cylinder245,Cylinder246,Cylinder247,Cylinder248]
FEATURE [Part::Box] Box094  label="Krychle094"
  AttacherType = Attacher::AttachEngine3D
  Height = 6
  Length = 2
  Placement = pos=(34,-24,19) rot=(0,0,1;0rad)
  Width = 6
FEATURE [Part::Compound] Compound145
  Links = -> [Box091,Box092,Box093,Box094]
FEATURE [Part::Cylinder] Cylinder232  label="Válec232"
  Angle = 360
  AttacherType = Attacher::AttachEngine3D
  Height = 18
  Placement = pos=(-4e-15,36,0) rot=(0,0,1;1.5708rad)
  Radius = 1.5
FEATURE [Part::Cylinder] Cylinder236  label="Válec236"
  Angle = 360
  AttacherType = Attacher::AttachEngine3D
  Height = 18
  Placement = pos=(1.2e-14,-36,0) rot=(0,0,-1;1.5708rad)
  Radius = 1.5
FEATURE [Part::Cylinder] Cylinder233  label="Válec233"
  Angle = 360
  AttacherType = Attacher::AttachEngine3D
  Height = 18
  Placement = pos=(-25.4558,25.4558,0) rot=(0,0,1;2.35619rad)
  Radius = 1.5
FEATURE [Part::Cylinder] Cylinder237  label="Válec237"
  Angle = 360
  AttacherType = Attacher::AttachEngine3D
  Height = 18
  Placement = pos=(25.4558,-25.4558,0) rot=(0,0,-1;0.785398rad)
  Radius = 1.5
FEATURE [Part::Compound] Compound137
  Links = -> [Cylinder231,Cylinder232,Cylinder233,Cylinder234,Cylinder235,Cylinder236,Cylinder237,Cylinder230]
FEATURE [Part::Cylinder] Cylinder238  label="Válec238"
  Angle = 360
  AttacherType = Attacher::AttachEngine3D
  Height = 10
  Placement = pos=(0,-31.6,20) rot=(0,0,1;0rad)
  Radius = 3.5
FEATURE [Part::Cylinder] Cylinder244  label="Válec244"
  Angle = 360
  AttacherType = Attacher::AttachEngine3D
  Height = 13
  Placement = pos=(0,0,12) rot=(0,0,1;0rad)
  Radius = 40
FEATURE [Part::Cut] Cut173
  Base = -> Box090
  Tool = -> Cylinder244
FEATURE [Part::Cut] Cut174
  Base = -> Cut173
  Tool = -> Compound145
FEATURE [Part::Cut] Cut175
  Base = -> Cut174
  Tool = -> Compound146
FEATURE [Part::Box] Box097  label="Krychle097"
  AttacherType = Attacher::AttachEngine3D
  Height = 6
  Length = 2
  Placement = pos=(34,-24,19) rot=(0,0,1;0rad)
  Width = 6
FEATURE [Part::Cylinder] Cylinder250  label="Válec250"
  Angle = 360
  AttacherType = Attacher::AttachEngine3D
  Height = 20
  Placement = pos=(26,37,19) rot=(0,1,0;1.5708rad)
  Radius = 1.5
FEATURE [Part::Cylinder] Cylinder252  label="Válec252"
  Angle = 360
  AttacherType = Attacher::AttachEngine3D
  Height = 20
  Placement = pos=(26,-37,19) rot=(0,1,0;1.5708rad)
  Radius = 1.5
FEATURE [Part::Cylinder] Cylinder249  label="Válec249"
  Angle = 360
  AttacherType = Attacher::AttachEngine3D
  Height = 20
  Placement = pos=(31,21,22) rot=(0,1,0;1.5708rad)
  Radius = 1.5
FEATURE [Part::Box] Box096  label="Krychle096"
  AttacherType = Attacher::AttachEngine3D
  Height = 6
  Length = 2
  Placement = pos=(34,18,19) rot=(0,0,1;0rad)
  Width = 6
FEATURE [Part::Box] Box098  label="Krychle098"
  AttacherType = Attacher::AttachEngine3D
  Height = 6
  Length = 2
  Placement = pos=(30,-40,16) rot=(0,0,1;0rad)
  Width = 6
FEATURE [Part::Box] Box095  label="Krychle095"
  AttacherType = Attacher::AttachEngine3D
  Height = 6
  Length = 2
  Placement = pos=(30,34,16) rot=(0,0,1;0rad)
  Width = 6
FEATURE [Part::Compound] Compound147
  Links = -> [Box095,Box096,Box098,Box097]
FEATURE [Part::Cylinder] Cylinder251  label="Válec251"
  Angle = 360
  AttacherType = Attacher::AttachEngine3D
  Height = 20
  Placement = pos=(31,-21,22) rot=(0,1,0;1.5708rad)
  Radius = 1.5
FEATURE [Part::Compound] Compound148
  Links = -> [Cylinder250,Cylinder249,Cylinder251,Cylinder252]
FEATURE [Part::Cut] Cut167
  Base = -> Cut166
  Tool = -> Compound136
FEATURE [Part::Cut] Cut168
  Base = -> Cut167
  Tool = -> Compound137
FEATURE [Part::Cut] Cut169
  Base = -> Cut168
  Tool = -> Cylinder238
FEATURE [Part::Cut] Cut176
  Base = -> Cut169
  Tool = -> Compound147
FEATURE [Part::Cut] Cut177
  Base = -> Cut176
  Tool = -> Compound148
FEATURE [Part::Compound] Compound149  label="jointovina_micro_loziskovina"
  Links = -> [Cut177,Cut175]
  Placement = pos=(0,1,-34) rot=(0,0,-1;1.5708rad)
FEATURE [Part::Box] Box909  label="Krychle908"
  AttacherType = Attacher::AttachEngine3D
  Height = 7
  Length = 42
  Placement = pos=(-21,-12,34) rot=(0,0,1;0rad)
  Width = 24
FEATURE [Part::Cylinder] Cylinder2339  label="Válec2339"
  Angle = 360
  AttacherType = Attacher::AttachEngine3D
  Height = 5
  Placement = pos=(0,90,77) rot=(0,0,1;0rad)
  Radius = 5
FEATURE [Part::Cylinder] Cylinder2340  label="Válec2340"
  Angle = 360
  AttacherType = Attacher::AttachEngine3D
  Height = 5
  Placement = pos=(0,90,77) rot=(0,0,1;0rad)
  Radius = 3
FEATURE [Part::Box] Box910  label="Krychle909"
  AttacherType = Attacher::AttachEngine3D
  Height = 2
  Length = 6
  Placement = pos=(15,82,-56) rot=(0,0,1;0rad)
  Width = 6
FEATURE [Part::Box] Box911  label="Krychle910"
  AttacherType = Attacher::AttachEngine3D
  Height = 2
  Length = 6
  Placement = pos=(-21,82,-56) rot=(0,0,1;0rad)
  Width = 6
FEATURE [Part::Box] Box912  label="Krychle911"
  AttacherType = Attacher::AttachEngine3D
  Height = 2
  Length = 6
  Placement = pos=(-21,92,-56) rot=(0,0,1;0rad)
  Width = 6
FEATURE [Part::Box] Box913  label="Krychle912"
  AttacherType = Attacher::AttachEngine3D
  Height = 2
  Length = 6
  Placement = pos=(15,92,-56) rot=(0,0,1;0rad)
  Width = 6
FEATURE [Part::Cylinder] Cylinder1693  label="Válec1693"
  Angle = 360
  AttacherType = Attacher::AttachEngine3D
  Height = 60
  Placement = pos=(-18,85,-57) rot=(0,0,1;0rad)
  Radius = 1.5
FEATURE [Part::Cylinder] Cylinder1694  label="Válec1694"
  Angle = 360
  AttacherType = Attacher::AttachEngine3D
  Height = 60
  Placement = pos=(-18,95,-57) rot=(0,0,1;0rad)
  Radius = 1.5
FEATURE [Part::Cylinder] Cylinder1695  label="Válec1695"
  Angle = 360
  AttacherType = Attacher::AttachEngine3D
  Height = 60
  Placement = pos=(18,95,-57) rot=(0,0,1;0rad)
  Radius = 1.5
FEATURE [Part::Cylinder] Cylinder2341  label="Válec2341"
  Angle = 360
  AttacherType = Attacher::AttachEngine3D
  Height = 60
  Placement = pos=(18,85,-57) rot=(0,0,1;0rad)
  Radius = 1.5
FEATURE [Part::Box] Box914  label="Krychle913"
  AttacherType = Attacher::AttachEngine3D
  Height = 20
  Length = 28.8
  Placement = pos=(-14.4,-15.34,34) rot=(0,0,1;0rad)
  Width = 34.21
FEATURE [Part::Box] Box915  label="Krychle914"
  AttacherType = Attacher::AttachEngine3D
  Height = 24
  Length = 42
  Placement = pos=(-21,78,-49) rot=(0,0,1;0rad)
  Width = 24
FEATURE [Part::Cylinder] Cylinder2342  label="Válec2342"
  Angle = 360
  AttacherType = Attacher::AttachEngine3D
  Height = 48
  Placement = pos=(0,90,-55) rot=(0,0,1;0rad)
  Radius = 2.5
FEATURE [Part::Cylinder] Cylinder1699  label="Válec1699"
  Angle = 360
  AttacherType = Attacher::AttachEngine3D
  Height = 60
  Placement = pos=(18,95,-57) rot=(0,0,1;0rad)
  Radius = 1.5
FEATURE [Part::Cylinder] Cylinder1700  label="Válec1700"
  Angle = 360
  AttacherType = Attacher::AttachEngine3D
  Height = 60
  Placement = pos=(18,85,-57) rot=(0,0,1;0rad)
  Radius = 1.5
FEATURE [Part::Cylinder] Cylinder2343  label="Válec2343"
  Angle = 360
  AttacherType = Attacher::AttachEngine3D
  Height = 60
  Placement = pos=(-18,85,-57) rot=(0,0,1;0rad)
  Radius = 1.5
FEATURE [Part::Cylinder] Cylinder2344  label="Válec2344"
  Angle = 360
  AttacherType = Attacher::AttachEngine3D
  Height = 60
  Placement = pos=(-18,95,-57) rot=(0,0,1;0rad)
  Radius = 1.5
FEATURE [Part::Compound] Compound819
  Links = -> [Box909]
  Placement = pos=(63.64,-63.64,43) rot=(0,0,1;3.92699rad)
FEATURE [Part::Compound] Compound820
  Links = -> [Cylinder2339]
  Placement = pos=(0,0,2) rot=(0,0,1;3.92699rad)
FEATURE [Part::Cut] Cut473
  Base = -> Compound819
  Placement = pos=(0,0,-22) rot=(0,0,1;0rad)
  Tool = -> Compound820
FEATURE [Part::Compound] Compound821
  Links = -> [Cylinder2340]
  Placement = pos=(0,0,-24) rot=(0,0,1;3.92699rad)
FEATURE [Part::Cut] Cut474
  Base = -> Cut473
  Tool = -> Compound821
FEATURE [Part::Compound] Compound807
  Links = -> [Box911,Box912,Box910,Box913]
  Placement = pos=(0,0,117) rot=(0,0,1;3.92699rad)
FEATURE [Part::Compound] Compound1020
  Links = -> [Cylinder1695,Cylinder2341,Cylinder1693,Cylinder1694]
  Placement = pos=(0,0,100) rot=(0,0,1;3.92699rad)
FEATURE [Part::Compound] Compound805
  Links = -> [Box914]
  Placement = pos=(0,90,-83) rot=(0,0,1;0rad)
FEATURE [Part::Cut] Cut315
  Base = -> Box915
  Placement = pos=(0,0,21) rot=(0,0,1;0rad)
  Tool = -> Compound805
FEATURE [Part::Cut] Cut316
  Base = -> Cut315
  Tool = -> Cylinder2342
FEATURE [Part::Chamfer] Chamfer038
  Base = -> Cut316
  Edges = 2 edges r=6: [Edge6,Edge8]
FEATURE [Part::Compound] Compound843
  Links = -> [Cylinder1699,Cylinder1700,Cylinder2343,Cylinder2344]
  Placement = pos=(0,0,-16) rot=(0,0,1;0rad)
FEATURE [Part::Cut] Cut325
  Base = -> Chamfer038
  Tool = -> Compound843
FEATURE [Part::Chamfer] Chamfer039
  Base = -> Cut325
  Edges = 2 edges r=4: [Edge17,Edge20]
FEATURE [Part::Chamfer] Chamfer044
  Base = -> Chamfer039
  Edges = 2 edges r=2: [Edge14,Edge35]
  Placement = pos=(0,0,31) rot=(0.92388,0.382683,0;3.14159rad)
FEATURE [Part::FeaturePython] Tube037  # WARN: FeaturePython — macro-defined, semantics opaque (R4)
  AttacherType = Attacher::AttachEngine3D
  Height = 1
  InnerRadius = 4
  OuterRadius = 5
  Placement = pos=(0,90,81) rot=(0,0,1;0rad)
FEATURE [Part::Compound] Compound822
  Links = -> [Tube037]
  Placement = pos=(0,0,-24) rot=(0,0,1;3.92699rad)
FEATURE [Part::Compound] Compound823
  Links = -> [Compound822,Cut474]
  Placement = pos=(0,0,4) rot=(0,0,1;0rad)
FEATURE [Part::Cut] Cut482
  Base = -> Compound823
  Tool = -> Compound1020
FEATURE [Part::Cut] Cut486
  Base = -> Cut482
  Tool = -> Compound807
FEATURE [Part::Chamfer] Chamfer045
  Base = -> Cut486
  Edges = 2 edges r=2: [Edge10,Edge36]
FEATURE [Part::Compound] Compound845  label="Base_encoder-uphold"
  Links = -> [Chamfer044,Chamfer045]
  Placement = pos=(0,11,43) rot=(-0.382683,0.92388,0;3.14159rad)
FEATURE [Part::Box] Box923  label="Krychle922"
  AttacherType = Attacher::AttachEngine3D
  Height = 20
  Length = 22.8
  Placement = pos=(-11.4,-15.34,34) rot=(0,0,1;0rad)
  Width = 34.21
FEATURE [Part::Box] Box924  label="Krychle923"
  AttacherType = Attacher::AttachEngine3D
  Height = 24
  Length = 36
  Placement = pos=(-18,78,-49) rot=(0,0,1;0rad)
  Width = 24
FEATURE [Part::Cylinder] Cylinder2356  label="Válec2356"
  Angle = 360
  AttacherType = Attacher::AttachEngine3D
  Height = 48
  Placement = pos=(0,90,-55) rot=(0,0,1;0rad)
  Radius = 2.5
FEATURE [Part::Cylinder] Cylinder2357  label="Válec2357"
  Angle = 360
  AttacherType = Attacher::AttachEngine3D
  Height = 60
  Placement = pos=(18,95,-57) rot=(0,0,1;0rad)
  Radius = 1.5
FEATURE [Part::Cylinder] Cylinder2358  label="Válec2358"
  Angle = 360
  AttacherType = Attacher::AttachEngine3D
  Height = 60
  Placement = pos=(18,85,-57) rot=(0,0,1;0rad)
  Radius = 1.5
FEATURE [Part::Cylinder] Cylinder2359  label="Válec2359"
  Angle = 360
  AttacherType = Attacher::AttachEngine3D
  Height = 60
  Placement = pos=(-18,85,-57) rot=(0,0,1;0rad)
  Radius = 1.5
FEATURE [Part::Cylinder] Cylinder2360  label="Válec2360"
  Angle = 360
  AttacherType = Attacher::AttachEngine3D
  Height = 60
  Placement = pos=(-18,95,-57) rot=(0,0,1;0rad)
  Radius = 1.5
FEATURE [Part::Compound] Compound1031
  Links = -> [Box923]
  Placement = pos=(0,90,-83) rot=(0,0,1;0rad)
FEATURE [Part::Cut] Cut851
  Base = -> Box924
  Placement = pos=(0,0,21) rot=(0,0,1;0rad)
  Tool = -> Compound1031
FEATURE [Part::Compound] Compound1032
  Links = -> [Cylinder2357,Cylinder2358,Cylinder2359,Cylinder2360]
  Placement = pos=(0,0,-31) rot=(0,0,1;0rad)
FEATURE [Part::Cut] Cut852
  Base = -> Cut851
  Tool = -> Cylinder2356
FEATURE [Part::Chamfer] Chamfer071
  Base = -> Cut852
  Edges = 2 edges r=6: [Edge6,Edge8]
FEATURE [Part::Cut] Cut853
  Base = -> Chamfer071
  Tool = -> Compound1032
FEATURE [Part::Chamfer] Chamfer
  Base = -> Cut853
  Edges = 2 edges r=3: [Edge25,Edge33]
  Placement = pos=(0,180,0) rot=(0,0,1;3.14159rad)
FEATURE [Part::FeaturePython] Tube039  # WARN: FeaturePython — macro-defined, semantics opaque (R4)
  AttacherType = Attacher::AttachEngine3D
  Height = 1
  InnerRadius = 4
  OuterRadius = 5
  Placement = pos=(0,90,81) rot=(0,0,1;0rad)
FEATURE [Part::Box] Box925  label="Krychle924"
  AttacherType = Attacher::AttachEngine3D
  Height = 7
  Length = 42
  Placement = pos=(-21,-12,34) rot=(0,0,1;0rad)
  Width = 24
FEATURE [Part::Cylinder] Cylinder2361  label="Válec2361"
  Angle = 360
  AttacherType = Attacher::AttachEngine3D
  Height = 5
  Placement = pos=(0,90,77) rot=(0,0,1;0rad)
  Radius = 5
FEATURE [Part::Cylinder] Cylinder2362  label="Válec2362"
  Angle = 360
  AttacherType = Attacher::AttachEngine3D
  Height = 5
  Placement = pos=(0,90,77) rot=(0,0,1;0rad)
  Radius = 3
FEATURE [Part::Box] Box926  label="Krychle925"
  AttacherType = Attacher::AttachEngine3D
  Height = 2
  Length = 6
  Placement = pos=(15,82,-56) rot=(0,0,1;0rad)
  Width = 6
FEATURE [Part::Box] Box927  label="Krychle926"
  AttacherType = Attacher::AttachEngine3D
  Height = 2
  Length = 6
  Placement = pos=(-21,82,-56) rot=(0,0,1;0rad)
  Width = 6
FEATURE [Part::Box] Box928  label="Krychle927"
  AttacherType = Attacher::AttachEngine3D
  Height = 2
  Length = 6
  Placement = pos=(-21,92,-56) rot=(0,0,1;0rad)
  Width = 6
FEATURE [Part::Box] Box929  label="Krychle928"
  AttacherType = Attacher::AttachEngine3D
  Height = 2
  Length = 6
  Placement = pos=(15,92,-56) rot=(0,0,1;0rad)
  Width = 6
FEATURE [Part::Cylinder] Cylinder2363  label="Válec2363"
  Angle = 360
  AttacherType = Attacher::AttachEngine3D
  Height = 60
  Placement = pos=(-18,85,-57) rot=(0,0,1;0rad)
  Radius = 1.5
FEATURE [Part::Cylinder] Cylinder2364  label="Válec2364"
  Angle = 360
  AttacherType = Attacher::AttachEngine3D
  Height = 60
  Placement = pos=(-18,95,-57) rot=(0,0,1;0rad)
  Radius = 1.5
FEATURE [Part::Cylinder] Cylinder2365  label="Válec2365"
  Angle = 360
  AttacherType = Attacher::AttachEngine3D
  Height = 60
  Placement = pos=(18,95,-57) rot=(0,0,1;0rad)
  Radius = 1.5
FEATURE [Part::Cylinder] Cylinder2366  label="Válec2366"
  Angle = 360
  AttacherType = Attacher::AttachEngine3D
  Height = 60
  Placement = pos=(18,85,-57) rot=(0,0,1;0rad)
  Radius = 1.5
FEATURE [Part::Compound] Compound1033
  Links = -> [Box925]
  Placement = pos=(63.64,-63.64,43) rot=(0,0,1;3.92699rad)
FEATURE [Part::Compound] Compound1034
  Links = -> [Cylinder2361]
  Placement = pos=(0,0,2) rot=(0,0,1;3.92699rad)
FEATURE [Part::Cut] Cut854
  Base = -> Compound1033
  Placement = pos=(0,0,-22) rot=(0,0,1;0rad)
  Tool = -> Compound1034
FEATURE [Part::Compound] Compound1035
  Links = -> [Cylinder2362]
  Placement = pos=(0,0,-24) rot=(0,0,1;3.92699rad)
FEATURE [Part::Cut] Cut855
  Base = -> Cut854
  Tool = -> Compound1035
FEATURE [Part::Compound] Compound1036
  Links = -> [Tube039]
  Placement = pos=(0,0,-24) rot=(0,0,1;3.92699rad)
FEATURE [Part::Compound] Compound1037
  Links = -> [Compound1036,Cut855]
  Placement = pos=(0,0,4) rot=(0,0,1;0rad)
FEATURE [Part::Compound] Compound1038
  Links = -> [Box927,Box928,Box926,Box929]
  Placement = pos=(0,0,117) rot=(0,0,1;3.92699rad)
FEATURE [Part::Compound] Compound1039
  Links = -> [Cylinder2365,Cylinder2366,Cylinder2363,Cylinder2364]
  Placement = pos=(0,0,100) rot=(0,0,1;3.92699rad)
FEATURE [Part::Cut] Cut856
  Base = -> Compound1037
  Tool = -> Compound1039
FEATURE [Part::Cut] Cut857
  Base = -> Cut856
  Tool = -> Compound1038
FEATURE [Part::Chamfer] Chamfer072
  Base = -> Cut857
  Edges = 2 edges r=2: [Edge10,Edge36]
  Placement = pos=(0,180,31) rot=(-0.382683,0.92388,0;3.14159rad)
FEATURE [Part::Compound] Compound  label="L-elb_encoder-uphold2"
  Links = -> [Chamfer,Chamfer072]
  Placement = pos=(0,-174,20) rot=(0,0,1;0rad)
FEATURE [Part::Box] Box930  label="Krychle929"
  AttacherType = Attacher::AttachEngine3D
  Height = 2
  Length = 42
  Placement = pos=(-21,-12,34) rot=(0,0,1;0rad)
  Width = 24
FEATURE [Part::Cylinder] Cylinder2367  label="Válec2367"
  Angle = 360
  AttacherType = Attacher::AttachEngine3D
  Height = 4
  Placement = pos=(63.64,-63.64,76) rot=(0,0,1;3.92699rad)
  Radius = 4
FEATURE [Part::Compound] Compound818
  Links = -> [Box930]
  Placement = pos=(63.64,-63.64,42) rot=(0,0,1;3.92699rad)
FEATURE [Part::Cut] Cut472
  Base = -> Compound818
  Placement = pos=(0,0,-10) rot=(0,0,1;0rad)
  Tool = -> Cylinder2367
FEATURE [Part::Cylinder] Cylinder1689  label="Válec1689"
  Angle = 360
  AttacherType = Attacher::AttachEngine3D
  Height = 60
  Placement = pos=(-18,85,-57) rot=(0,0,1;0rad)
  Radius = 1.5
FEATURE [Part::Cylinder] Cylinder1690  label="Válec1690"
  Angle = 360
  AttacherType = Attacher::AttachEngine3D
  Height = 60
  Placement = pos=(-18,95,-57) rot=(0,0,1;0rad)
  Radius = 1.5
FEATURE [Part::Cylinder] Cylinder1691  label="Válec1691"
  Angle = 360
  AttacherType = Attacher::AttachEngine3D
  Height = 60
  Placement = pos=(18,95,-57) rot=(0,0,1;0rad)
  Radius = 1.5
FEATURE [Part::Cylinder] Cylinder1692  label="Válec1692"
  Angle = 360
  AttacherType = Attacher::AttachEngine3D
  Height = 60
  Placement = pos=(18,85,-57) rot=(0,0,1;0rad)
  Radius = 1.5
FEATURE [Part::Compound] Compound833
  Links = -> [Cylinder1691,Cylinder1692,Cylinder1689,Cylinder1690]
  Placement = pos=(0,0,100) rot=(0,0,1;3.92699rad)
FEATURE [Part::Cut] Cut481  label="Base_encoder-washer1"
  Base = -> Cut472
  Placement = pos=(0,0,-3) rot=(0,0,1;0rad)
  Tool = -> Compound833
FEATURE [Part::Box] Box711  label="Krychle711"
  AttacherType = Attacher::AttachEngine3D
  Height = 4
  Length = 28.8
  Placement = pos=(-14.4,10,24) rot=(0,0,1;0rad)
  Width = 2
FEATURE [Part::Cylinder] Cylinder1760  label="Válec1760"
  Angle = 360
  AttacherType = Attacher::AttachEngine3D
  Height = 4
  Placement = pos=(63.64,-63.64,64) rot=(0,0,1;3.92699rad)
  Radius = 9
FEATURE [Part::Compound] Compound890
  Links = -> [Box711]
  Placement = pos=(63.64,-63.64,38) rot=(0,0,1;3.92699rad)
FEATURE [Part::Cut] Cut522
  Base = -> Cut481
  Tool = -> Compound890
FEATURE [Part::Cut] Cut523
  Base = -> Cut522
  Tool = -> Cylinder1760
FEATURE [Part::Chamfer] Chamfer058  label="L-elb_encoder-washer"
  Base = -> Cut523
  Edges = 2 edges r=2: [Edge3,Edge31]
  Placement = pos=(0,6,48) rot=(-0.382683,0.92388,0;3.14159rad)
FEATURE [Part::Box] Box931  label="Krychle930"
  AttacherType = Attacher::AttachEngine3D
  Height = 9
  Length = 28.8
  Placement = pos=(-14.4,-14,34) rot=(0,0,1;0rad)
  Width = 34.4
FEATURE [Part::Compound] Compound804
  Links = -> [Box931]
  Placement = pos=(63.64,-63.64,33) rot=(0,0,1;3.92699rad)
FEATURE [Part::Box] Box932  label="Krychle931"
  AttacherType = Attacher::AttachEngine3D
  Height = 9
  Length = 42
  Placement = pos=(-21,-12,34) rot=(0,0,1;0rad)
  Width = 24
FEATURE [Part::Box] Box933  label="Krychle932"
  AttacherType = Attacher::AttachEngine3D
  Height = 1
  Length = 54
  Placement = pos=(-27,-12,34) rot=(0,0,1;0rad)
  Width = 24
FEATURE [Part::Compound] Compound809
  Links = -> [Box932]
  Placement = pos=(63.64,-63.64,33) rot=(0,0,1;3.92699rad)
FEATURE [Part::Cut] Cut469
  Base = -> Compound809
  Tool = -> Compound804
FEATURE [Part::Compound] Compound811
  Links = -> [Box933]
  Placement = pos=(63.64,-63.64,42) rot=(0,0,1;3.92699rad)
FEATURE [Part::Cylinder] Cylinder1643  label="Válec1643"
  Angle = 360
  AttacherType = Attacher::AttachEngine3D
  Height = 1
  Placement = pos=(63.64,-63.64,76) rot=(0,0,1;3.92699rad)
  Radius = 4
FEATURE [Part::Cut] Cut470
  Base = -> Compound811
  Tool = -> Cylinder1643
FEATURE [Part::Box] Box934  label="Krychle933"
  AttacherType = Attacher::AttachEngine3D
  Height = 9
  Length = 42
  Placement = pos=(-21,-14,34) rot=(0,0,1;0rad)
  Width = 28
FEATURE [Part::Box] Box935  label="Krychle934"
  AttacherType = Attacher::AttachEngine3D
  Height = 9
  Length = 54
  Placement = pos=(-27,-12,34) rot=(0,0,1;0rad)
  Width = 24
FEATURE [Part::Compound] Compound824
  Links = -> [Box934]
  Placement = pos=(63.64,-63.64,33) rot=(0,0,1;3.92699rad)
FEATURE [Part::Compound] Compound825
  Links = -> [Box935]
  Placement = pos=(63.64,-63.64,33) rot=(0,0,1;3.92699rad)
FEATURE [Part::Cut] Cut475
  Base = -> Compound825
  Tool = -> Compound824
FEATURE [Part::Cylinder] Cylinder2368  label="Válec2368"
  Angle = 360
  AttacherType = Attacher::AttachEngine3D
  Height = 20
  Placement = pos=(15.75,114,39.48) rot=(0,0.707107,0.707107;3.14159rad)
  Radius = 1.5
FEATURE [Part::Cylinder] Cylinder2369  label="Válec2369"
  Angle = 360
  AttacherType = Attacher::AttachEngine3D
  Height = 20
  Placement = pos=(15.75,114,58.525) rot=(0,0.707107,0.707107;3.14159rad)
  Radius = 1.5
FEATURE [Part::Compound] Compound826
  Links = -> [Cylinder2368,Cylinder2369]
  Placement = pos=(-49,0,-96) rot=(0.57735,0.57735,0.57735;2.0944rad)
FEATURE [Part::Compound] Compound827
  Links = -> [Compound826]
  Placement = pos=(52.33,-52.33,52) rot=(0,0,1;3.92699rad)
FEATURE [Part::Cut] Cut477
  Base = -> Cut470
  Tool = -> Compound827
FEATURE [Part::Cylinder] Cylinder1621  label="Válec1621"
  Angle = 360
  AttacherType = Attacher::AttachEngine3D
  Height = 60
  Placement = pos=(18,95,-57) rot=(0,0,1;0rad)
  Radius = 1.5
FEATURE [Part::Cylinder] Cylinder2370  label="Válec2370"
  Angle = 360
  AttacherType = Attacher::AttachEngine3D
  Height = 60
  Placement = pos=(18,85,-57) rot=(0,0,1;0rad)
  Radius = 1.5
FEATURE [Part::Cylinder] Cylinder2371  label="Válec2371"
  Angle = 360
  AttacherType = Attacher::AttachEngine3D
  Height = 60
  Placement = pos=(-18,85,-57) rot=(0,0,1;0rad)
  Radius = 1.5
FEATURE [Part::Cylinder] Cylinder2372  label="Válec2372"
  Angle = 360
  AttacherType = Attacher::AttachEngine3D
  Height = 60
  Placement = pos=(-18,95,-57) rot=(0,0,1;0rad)
  Radius = 1.5
FEATURE [Part::Compound] Compound806
  Links = -> [Cylinder1621,Cylinder2370,Cylinder2371,Cylinder2372]
  Placement = pos=(0,0,100) rot=(0,0,1;3.92699rad)
FEATURE [Part::Cylinder] Cylinder2373  label="Válec2373"
  Angle = 360
  AttacherType = Attacher::AttachEngine3D
  Height = 60
  Placement = pos=(-18,85,-57) rot=(0,0,1;0rad)
  Radius = 1.5
FEATURE [Part::Cylinder] Cylinder2374  label="Válec2374"
  Angle = 360
  AttacherType = Attacher::AttachEngine3D
  Height = 60
  Placement = pos=(-18,95,-57) rot=(0,0,1;0rad)
  Radius = 1.5
FEATURE [Part::Cylinder] Cylinder2375  label="Válec2375"
  Angle = 360
  AttacherType = Attacher::AttachEngine3D
  Height = 60
  Placement = pos=(18,95,-57) rot=(0,0,1;0rad)
  Radius = 1.5
FEATURE [Part::Cylinder] Cylinder2376  label="Válec2376"
  Angle = 360
  AttacherType = Attacher::AttachEngine3D
  Height = 60
  Placement = pos=(18,85,-57) rot=(0,0,1;0rad)
  Radius = 1.5
FEATURE [Part::Compound] Compound831
  Links = -> [Cylinder2375,Cylinder2376,Cylinder2373,Cylinder2374]
  Placement = pos=(0,0,100) rot=(0,0,1;3.92699rad)
FEATURE [Part::Cut] Cut480
  Base = -> Cut477
  Tool = -> Compound831
FEATURE [Part::Compound] Compound835
  Links = -> [Cut469,Cut475]
FEATURE [Part::Cut] Cut483
  Base = -> Compound835
  Tool = -> Compound806
FEATURE [Part::Compound] Compound836  label="Base_encoder-sidehold2"
  Links = -> [Cut483,Cut480]
FEATURE [Part::Box] Box936  label="Krychle935"
  AttacherType = Attacher::AttachEngine3D
  Height = 6
  Length = 6
  Placement = pos=(21,90,69) rot=(0,0,1;0rad)
  Width = 2
FEATURE [Part::Compound] Compound837
  Links = -> [Box936]
  Placement = pos=(0,0,0) rot=(0,0,1;3.92699rad)
FEATURE [Part::Box] Box937  label="Krychle936"
  AttacherType = Attacher::AttachEngine3D
  Height = 6
  Length = 6
  Placement = pos=(-27,90,69) rot=(0,0,1;0rad)
  Width = 2
FEATURE [Part::Compound] Compound838
  Links = -> [Box937]
  Placement = pos=(0,0,0) rot=(0,0,1;3.92699rad)
FEATURE [Part::Cylinder] Cylinder2377  label="Válec2377"
  Angle = 360
  AttacherType = Attacher::AttachEngine3D
  Height = 100
  Placement = pos=(-24,110,72) rot=(1,0,0;1.5708rad)
  Radius = 1.5
FEATURE [Part::Compound] Compound839
  Links = -> [Cylinder2377]
  Placement = pos=(0,0,0) rot=(0,0,1;3.92699rad)
FEATURE [Part::Cylinder] Cylinder1697  label="Válec1697"
  Angle = 360
  AttacherType = Attacher::AttachEngine3D
  Height = 100
  Placement = pos=(24,110,72) rot=(1,0,0;1.5708rad)
  Radius = 1.5
FEATURE [Part::Compound] Compound840
  Links = -> [Cylinder1697]
  Placement = pos=(0,0,0) rot=(0,0,1;3.92699rad)
FEATURE [Part::Compound] Compound841
  Links = -> [Compound837,Compound838]
FEATURE [Part::Cut] Cut484
  Base = -> Compound836
  Tool = -> Compound841
FEATURE [Part::Compound] Compound842
  Links = -> [Compound839,Compound840]
FEATURE [Part::Cut] Cut485  label="Base_encoder-sidehold004"
  Base = -> Cut484
  Tool = -> Compound842
FEATURE [Part::Chamfer] Chamfer049
  Base = -> Cut485
  Edges = 4 edges r=1: [Edge48,Edge82,Edge99,Edge114]
FEATURE [Part::Chamfer] Chamfer050
  Base = -> Chamfer049
  Edges = 2 edges r=1: [Edge3,Edge68]
FEATURE [Part::Chamfer] Chamfer051  label="Base_encoder-sidehold"
  Base = -> Chamfer050
  Edges = 2 edges r=1: [Edge69,Edge97]
  Placement = pos=(0,0,-2) rot=(0,0,1;0rad)
FEATURE [Part::Box] Box938  label="Krychle937"
  AttacherType = Attacher::AttachEngine3D
  Height = 9
  Length = 28.8
  Placement = pos=(-14.4,-14,34) rot=(0,0,1;0rad)
  Width = 34.4
FEATURE [Part::Box] Box939  label="Krychle938"
  AttacherType = Attacher::AttachEngine3D
  Height = 9
  Length = 42
  Placement = pos=(-21,-12,34) rot=(0,0,1;0rad)
  Width = 24
FEATURE [Part::Compound] Compound1040
  Links = -> [Box938]
  Placement = pos=(63.64,-63.64,33) rot=(0,0,1;3.92699rad)
FEATURE [Part::Compound] Compound1041
  Links = -> [Box939]
  Placement = pos=(63.64,-63.64,33) rot=(0,0,1;3.92699rad)
FEATURE [Part::Cut] Cut858
  Base = -> Compound1041
  Tool = -> Compound1040
FEATURE [Part::Cylinder] Cylinder2378  label="Válec2378"
  Angle = 360
  AttacherType = Attacher::AttachEngine3D
  Height = 60
  Placement = pos=(18,95,-57) rot=(0,0,1;0rad)
  Radius = 1.5
FEATURE [Part::Cylinder] Cylinder2379  label="Válec2379"
  Angle = 360
  AttacherType = Attacher::AttachEngine3D
  Height = 60
  Placement = pos=(18,85,-57) rot=(0,0,1;0rad)
  Radius = 1.5
FEATURE [Part::Cylinder] Cylinder2380  label="Válec2380"
  Angle = 360
  AttacherType = Attacher::AttachEngine3D
  Height = 60
  Placement = pos=(-18,85,-57) rot=(0,0,1;0rad)
  Radius = 1.5
FEATURE [Part::Cylinder] Cylinder2381  label="Válec2381"
  Angle = 360
  AttacherType = Attacher::AttachEngine3D
  Height = 60
  Placement = pos=(-18,95,-57) rot=(0,0,1;0rad)
  Radius = 1.5
FEATURE [Part::Compound] Compound1042
  Links = -> [Cylinder2378,Cylinder2379,Cylinder2380,Cylinder2381]
  Placement = pos=(0,0,100) rot=(0,0,1;3.92699rad)
FEATURE [Part::Cut] Cut
  Base = -> Cut858
  Placement = pos=(0,-174,50) rot=(0.92388,0.382683,0;3.14159rad)
  Tool = -> Compound1042
FEATURE [Part::Box] Box940  label="Krychle939"
  AttacherType = Attacher::AttachEngine3D
  Height = 1
  Length = 42
  Placement = pos=(-21,-12,34) rot=(0,0,1;0rad)
  Width = 24
FEATURE [Part::Cylinder] Cylinder2382  label="Válec2382"
  Angle = 360
  AttacherType = Attacher::AttachEngine3D
  Height = 1
  Placement = pos=(63.64,-63.64,76) rot=(0,0,1;3.92699rad)
  Radius = 4
FEATURE [Part::Cylinder] Cylinder2383  label="Válec2383"
  Angle = 360
  AttacherType = Attacher::AttachEngine3D
  Height = 20
  Placement = pos=(15.75,114,39.48) rot=(0,0.707107,0.707107;3.14159rad)
  Radius = 1.5
FEATURE [Part::Cylinder] Cylinder2384  label="Válec2384"
  Angle = 360
  AttacherType = Attacher::AttachEngine3D
  Height = 20
  Placement = pos=(15.75,114,58.525) rot=(0,0.707107,0.707107;3.14159rad)
  Radius = 1.5
FEATURE [Part::Cylinder] Cylinder2385  label="Válec2385"
  Angle = 360
  AttacherType = Attacher::AttachEngine3D
  Height = 60
  Placement = pos=(-18,95,-57) rot=(0,0,1;0rad)
  Radius = 1.5
FEATURE [Part::Cylinder] Cylinder2386  label="Válec2386"
  Angle = 360
  AttacherType = Attacher::AttachEngine3D
  Height = 60
  Placement = pos=(-18,85,-57) rot=(0,0,1;0rad)
  Radius = 1.5
FEATURE [Part::Compound] Compound1043
  Links = -> [Box940]
  Placement = pos=(63.64,-63.64,42) rot=(0,0,1;3.92699rad)
FEATURE [Part::Compound] Compound1044
  Links = -> [Cylinder2383,Cylinder2384]
  Placement = pos=(-49,0,-96) rot=(0.57735,0.57735,0.57735;2.0944rad)
FEATURE [Part::Compound] Compound1045
  Links = -> [Compound1044]
  Placement = pos=(52.33,-52.33,52) rot=(0,0,1;3.92699rad)
FEATURE [Part::Cut] Cut860
  Base = -> Compound1043
  Tool = -> Cylinder2382
FEATURE [Part::Cut] Cut861
  Base = -> Cut860
  Tool = -> Compound1045
FEATURE [Part::Cylinder] Cylinder2387  label="Válec2387"
  Angle = 360
  AttacherType = Attacher::AttachEngine3D
  Height = 60
  Placement = pos=(18,95,-57) rot=(0,0,1;0rad)
  Radius = 1.5
FEATURE [Part::Cylinder] Cylinder2388  label="Válec2388"
  Angle = 360
  AttacherType = Attacher::AttachEngine3D
  Height = 60
  Placement = pos=(18,85,-57) rot=(0,0,1;0rad)
  Radius = 1.5
FEATURE [Part::Compound] Compound1046
  Links = -> [Cylinder2387,Cylinder2388,Cylinder2386,Cylinder2385]
  Placement = pos=(0,0,100) rot=(0,0,1;3.92699rad)
FEATURE [Part::Cut] Cut859
  Base = -> Cut861
  Placement = pos=(0,-174,50) rot=(0.92388,0.382683,0;3.14159rad)
  Tool = -> Compound1046
FEATURE [Part::Chamfer] Chamfer073
  Base = -> Cut
  Edges = 1 edges r=2: [Edge20]
FEATURE [Part::Chamfer] Chamfer074
  Base = -> Cut
  Edges = 1 edges r=2: [Edge20]
FEATURE [Part::Chamfer] Chamfer075
  Base = -> Cut859
  Edges = 1 edges r=2: [Edge6]
FEATURE [Part::Chamfer] Chamfer076
  Base = -> Chamfer075
  Edges = 1 edges r=2: [Edge2]
FEATURE [Part::Chamfer] Chamfer077
  Base = -> Chamfer073
  Edges = 1 edges r=2: [Edge22]
FEATURE [Part::Chamfer] Chamfer078
  Base = -> Chamfer074
  Edges = 1 edges r=2: [Edge22]
FEATURE [Part::Compound] Compound1047
  Links = -> [Chamfer076,Chamfer078]
FEATURE [Part::Box] Box941  label="Krychle940"
  AttacherType = Attacher::AttachEngine3D
  Height = 4
  Length = 21
  Placement = pos=(-42,-88,-25) rot=(0,0,1;0rad)
  Width = 16
FEATURE [Part::Box] Box942  label="Krychle941"
  AttacherType = Attacher::AttachEngine3D
  Height = 4
  Length = 21
  Placement = pos=(21,-88,-25) rot=(0,0,1;0rad)
  Width = 16
FEATURE [Part::Cylinder] Cylinder2389  label="Válec2389"
  Angle = 360
  AttacherType = Attacher::AttachEngine3D
  Height = 20
  Placement = pos=(34,-80,-32) rot=(0,0,1;0rad)
  Radius = 2
FEATURE [Part::Cylinder] Cylinder2390  label="Válec2390"
  Angle = 360
  AttacherType = Attacher::AttachEngine3D
  Height = 20
  Placement = pos=(-34,-80,-32) rot=(0,0,1;0rad)
  Radius = 2
FEATURE [Part::Chamfer] Chamfer079
  Base = -> Box941
  Edges = 1 edges r=4: [Edge1]
FEATURE [Part::Chamfer] Chamfer080
  Base = -> Box942
  Edges = 1 edges r=4: [Edge5]
FEATURE [Part::Chamfer] Chamfer081
  Base = -> Chamfer079
  Edges = 1 edges r=2: [Edge1]
FEATURE [Part::Chamfer] Chamfer082
  Base = -> Chamfer080
  Edges = 1 edges r=2: [Edge1]
FEATURE [Part::Compound] Compound1048
  Links = -> [Cylinder2390,Cylinder2389]
FEATURE [Part::Cylinder] Cylinder2391  label="Válec2391"
  Angle = 360
  AttacherType = Attacher::AttachEngine3D
  Height = 3
  Placement = pos=(-34,-80,-32) rot=(0,0,1;0rad)
  Radius = 3
FEATURE [Part::Cylinder] Cylinder2392  label="Válec2392"
  Angle = 360
  AttacherType = Attacher::AttachEngine3D
  Height = 3
  Placement = pos=(34,-80,-32) rot=(0,0,1;0rad)
  Radius = 3
FEATURE [Part::Compound] Compound1049
  Links = -> [Cylinder2391,Cylinder2392]
  Placement = pos=(0,0,-13) rot=(0,0,1;0rad)
FEATURE [Part::Compound] Compound1050
  Links = -> [Chamfer081,Chamfer082]
FEATURE [Part::Box] Box943  label="Krychle942"
  AttacherType = Attacher::AttachEngine3D
  Height = 4
  Length = 84
  Placement = pos=(-42,-88,-44) rot=(0,0,1;0rad)
  Width = 16
FEATURE [Part::Chamfer] Chamfer083
  Base = -> Box943
  Edges = 2 edges r=4: [Edge1,Edge5]
FEATURE [Part::Chamfer] Chamfer084
  Base = -> Chamfer083
  Edges = 2 edges r=2: [Edge3,Edge16]
FEATURE [Part::Cylinder] Cylinder2393  label="Válec2393"
  Angle = 360
  AttacherType = Attacher::AttachEngine3D
  Height = 20
  Placement = pos=(-34,-80,-32) rot=(0,0,1;0rad)
  Radius = 1.5
FEATURE [Part::Cylinder] Cylinder2394  label="Válec2394"
  Angle = 360
  AttacherType = Attacher::AttachEngine3D
  Height = 20
  Placement = pos=(34,-80,-32) rot=(0,0,1;0rad)
  Radius = 1.5
FEATURE [Part::Compound] Compound1051
  Links = -> [Cylinder2393,Cylinder2394]
  Placement = pos=(0,0,-20) rot=(0,0,1;0rad)
FEATURE [Part::Cylinder] Cylinder2395  label="Válec2395"
  Angle = 360
  AttacherType = Attacher::AttachEngine3D
  Height = 3
  Placement = pos=(34,-80,-32) rot=(0,0,1;0rad)
  Radius = 4
FEATURE [Part::Cylinder] Cylinder2396  label="Válec2396"
  Angle = 360
  AttacherType = Attacher::AttachEngine3D
  Height = 3
  Placement = pos=(-34,-80,-32) rot=(0,0,1;0rad)
  Radius = 4
FEATURE [Part::Compound] Compound1052
  Links = -> [Cylinder2396,Cylinder2395]
  Placement = pos=(0,0,9) rot=(0,0,1;0rad)
FEATURE [Part::Cut] Cut862
  Base = -> Compound1050
  Tool = -> Compound1052
FEATURE [Part::Cut] Cut863
  Base = -> Cut862
  Tool = -> Compound1048
FEATURE [Part::Cut] Cut864
  Base = -> Chamfer084
  Tool = -> Compound1051
FEATURE [Part::Cut] Cut865
  Base = -> Cut864
  Tool = -> Compound1049
FEATURE [Part::FeaturePython] Tube040  # WARN: FeaturePython — macro-defined, semantics opaque (R4)
  AttacherType = Attacher::AttachEngine3D
  Height = 1
  InnerRadius = 4
  OuterRadius = 5
  Placement = pos=(0,90,81) rot=(0,0,1;0rad)
FEATURE [Part::Box] Box944  label="Krychle943"
  AttacherType = Attacher::AttachEngine3D
  Height = 7
  Length = 42
  Placement = pos=(-21,-12,34) rot=(0,0,1;0rad)
  Width = 24
FEATURE [Part::Compound] Compound814
  Links = -> [Tube040]
  Placement = pos=(0,0,0) rot=(0,0,1;3.92699rad)
FEATURE [Part::Compound] Compound815
  Links = -> [Box944]
  Placement = pos=(63.64,-63.64,43) rot=(0,0,1;3.92699rad)
FEATURE [Part::Cylinder] Cylinder1644  label="Válec1644"
  Angle = 360
  AttacherType = Attacher::AttachEngine3D
  Height = 5
  Placement = pos=(0,90,77) rot=(0,0,1;0rad)
  Radius = 5
FEATURE [Part::Compound] Compound816
  Links = -> [Cylinder1644]
  Placement = pos=(0,0,0) rot=(0,0,1;3.92699rad)
FEATURE [Part::Cut] Cut471
  Base = -> Compound815
  Tool = -> Compound816
FEATURE [Part::Compound] Compound817
  Links = -> [Compound814,Cut471]
FEATURE [Part::Cylinder] Cylinder2397  label="Válec2397"
  Angle = 360
  AttacherType = Attacher::AttachEngine3D
  Height = 20
  Placement = pos=(15.75,114,39.48) rot=(0,0.707107,0.707107;3.14159rad)
  Radius = 1.5
FEATURE [Part::Cylinder] Cylinder2398  label="Válec2398"
  Angle = 360
  AttacherType = Attacher::AttachEngine3D
  Height = 20
  Placement = pos=(15.75,114,58.525) rot=(0,0.707107,0.707107;3.14159rad)
  Radius = 1.5
FEATURE [Part::Compound] Compound828
  Links = -> [Cylinder2397,Cylinder2398]
  Placement = pos=(-49,0,-96) rot=(0.57735,0.57735,0.57735;2.0944rad)
FEATURE [Part::Compound] Compound829
  Links = -> [Compound828]
  Placement = pos=(52.33,-52.33,52) rot=(0,0,1;3.92699rad)
FEATURE [Part::Cut] Cut476
  Base = -> Compound817
  Tool = -> Compound829
FEATURE [Part::Cylinder] Cylinder2399  label="Válec2399"
  Angle = 360
  AttacherType = Attacher::AttachEngine3D
  Height = 3
  Placement = pos=(-18,85,-57) rot=(0,0,1;0rad)
  Radius = 3
FEATURE [Part::Cylinder] Cylinder2400  label="Válec2400"
  Angle = 360
  AttacherType = Attacher::AttachEngine3D
  Height = 3
  Placement = pos=(-18,95,-57) rot=(0,0,1;0rad)
  Radius = 3
FEATURE [Part::Cylinder] Cylinder2401  label="Válec2401"
  Angle = 360
  AttacherType = Attacher::AttachEngine3D
  Height = 3
  Placement = pos=(18,95,-57) rot=(0,0,1;0rad)
  Radius = 3
FEATURE [Part::Cylinder] Cylinder2402  label="Válec2402"
  Angle = 360
  AttacherType = Attacher::AttachEngine3D
  Height = 3
  Placement = pos=(18,85,-57) rot=(0,0,1;0rad)
  Radius = 3
FEATURE [Part::Compound] Compound830
  Links = -> [Cylinder2401,Cylinder2402,Cylinder2399,Cylinder2400]
  Placement = pos=(0,0,138) rot=(0,0,1;3.92699rad)
FEATURE [Part::Cut] Cut487
  Base = -> Cut476
  Tool = -> Compound830
FEATURE [Part::Cylinder] Cylinder1703  label="Válec1703"
  Angle = 360
  AttacherType = Attacher::AttachEngine3D
  Height = 60
  Placement = pos=(-18,85,-57) rot=(0,0,1;0rad)
  Radius = 1.5
FEATURE [Part::Cylinder] Cylinder1704  label="Válec1704"
  Angle = 360
  AttacherType = Attacher::AttachEngine3D
  Height = 60
  Placement = pos=(-18,95,-57) rot=(0,0,1;0rad)
  Radius = 1.5
FEATURE [Part::Cylinder] Cylinder1705  label="Válec1705"
  Angle = 360
  AttacherType = Attacher::AttachEngine3D
  Height = 60
  Placement = pos=(18,95,-57) rot=(0,0,1;0rad)
  Radius = 1.5
FEATURE [Part::Cylinder] Cylinder1706  label="Válec1706"
  Angle = 360
  AttacherType = Attacher::AttachEngine3D
  Height = 60
  Placement = pos=(18,85,-57) rot=(0,0,1;0rad)
  Radius = 1.5
FEATURE [Part::Compound] Compound844
  Links = -> [Cylinder1705,Cylinder1706,Cylinder1703,Cylinder1704]
  Placement = pos=(0,0,100) rot=(0,0,1;3.92699rad)
FEATURE [Part::Cut] Cut488
  Base = -> Cut487
  Placement = pos=(0,-174,52) rot=(0.92388,0.382683,0;3.14159rad)
  Tool = -> Compound844
FEATURE [Part::Box] Box945  label="Krychle944"
  AttacherType = Attacher::AttachEngine3D
  Height = 15
  Length = 4
  Placement = pos=(-25,-88,-40) rot=(0,0,1;0rad)
  Width = 16
FEATURE [Part::Chamfer] Chamfer085
  Base = -> Cut488
  Edges = 2 edges r=2: [Edge7,Edge16]
  Placement = pos=(0,0,-2) rot=(0,0,1;0rad)
FEATURE [Part::Box] Box946  label="Krychle945"
  AttacherType = Attacher::AttachEngine3D
  Height = 15
  Length = 4
  Placement = pos=(21,-88,-40) rot=(0,0,1;0rad)
  Width = 16
FEATURE [Part::Box] Box947  label="Krychle946"
  AttacherType = Attacher::AttachEngine3D
  Height = 15
  Length = 42
  Placement = pos=(-21,-89,-49) rot=(0,0,1;0rad)
  Width = 18
FEATURE [Part::Cut] Cut866
  Base = -> Cut865
  Tool = -> Box947
FEATURE [Part::Compound] Compound1053  label="L-elb_encoder-bottomhold1"
  Links = -> [Cut866,Box946,Box945,Chamfer085]
FEATURE [Part::Chamfer] Chamfer086  label="L-elb_encoder-bottomhold-old"
  Base = -> Compound1053
  Edges = 2 edges r=2: [Edge17,Edge30]
FEATURE [Part::Cylinder] Cylinder1641  label="Válec1641"
  Angle = 360
  AttacherType = Attacher::AttachEngine3D
  Height = 9
  Placement = pos=(0,-60,0) rot=(0,0,1;0.523599rad)
  Radius = 9
FEATURE [Part::Cylinder] Cylinder2403  label="L-elb_pulley-GT2-16-B"
  Angle = 360
  AttacherType = Attacher::AttachEngine3D
  Height = 9
  Placement = pos=(9,-45,-6) rot=(0,0,1;0.523599rad)
  Radius = 6.5
FEATURE [Part::Cylinder] Cylinder2404  label="Válec2404"
  Angle = 360
  AttacherType = Attacher::AttachEngine3D
  Height = 9
  Placement = pos=(0,-60,0) rot=(0,0,1;0.523599rad)
  Radius = 6.5
FEATURE [Part::Cylinder] Cylinder2405  label="L-elb_pulley-GT2-16-A"
  Angle = 360
  AttacherType = Attacher::AttachEngine3D
  Height = 9
  Placement = pos=(-9,-45,-6) rot=(0,0,1;0.523599rad)
  Radius = 6.5
FEATURE [Part::Box] Box948  label="Krychle947"
  AttacherType = Attacher::AttachEngine3D
  Height = 50
  Length = 80
  Placement = pos=(-40,-48,-40) rot=(0,0,1;0rad)
  Width = 6
FEATURE [Part::Box] Box949  label="Krychle948"
  AttacherType = Attacher::AttachEngine3D
  Height = 15
  Length = 15
  Placement = pos=(19,-174,-65) rot=(0,0,1;0rad)
  Width = 130
FEATURE [Part::Box] Box950  label="Krychle949"
  AttacherType = Attacher::AttachEngine3D
  Height = 15
  Length = 15
  Placement = pos=(-34,-174,-65) rot=(0,0,1;0rad)
  Width = 130
FEATURE [Part::Compound] Compound1054
  Links = -> [Box950,Box949]
  Placement = pos=(0,-5,25) rot=(0,0,1;0rad)
FEATURE [Part::Cut] Cut867
  Base = -> Box948
  Tool = -> Compound1054
FEATURE [Part::Cylinder] Cylinder2406  label="Válec2406"
  Angle = 360
  AttacherType = Attacher::AttachEngine3D
  Height = 20
  Placement = pos=(31,21,22) rot=(0,1,0;1.5708rad)
  Radius = 1.5
FEATURE [Part::Cylinder] Cylinder2407  label="Válec2407"
  Angle = 360
  AttacherType = Attacher::AttachEngine3D
  Height = 20
  Placement = pos=(31,-21,22) rot=(0,1,0;1.5708rad)
  Radius = 1.5
FEATURE [Part::Cylinder] Cylinder2408  label="Válec2408"
  Angle = 360
  AttacherType = Attacher::AttachEngine3D
  Height = 20
  Placement = pos=(26,37,19) rot=(0,1,0;1.5708rad)
  Radius = 1.5
FEATURE [Part::Cylinder] Cylinder2409  label="Válec2409"
  Angle = 360
  AttacherType = Attacher::AttachEngine3D
  Height = 20
  Placement = pos=(26,-37,19) rot=(0,1,0;1.5708rad)
  Radius = 1.5
FEATURE [Part::Compound] Compound1055
  Links = -> [Cylinder2408,Cylinder2406,Cylinder2407,Cylinder2409]
  Placement = pos=(0,-80,-34) rot=(0,0,1;1.5708rad)
FEATURE [Part::Cylinder] Cylinder2410  label="Válec2410"
  Angle = 360
  AttacherType = Attacher::AttachEngine3D
  Height = 20
  Placement = pos=(28,16,-3) rot=(0,1,0;1.5708rad)
  Radius = 1.5
FEATURE [Part::Cylinder] Cylinder2411  label="Válec2411"
  Angle = 360
  AttacherType = Attacher::AttachEngine3D
  Height = 20
  Placement = pos=(26,37,7) rot=(0,1,0;1.5708rad)
  Radius = 1.5
FEATURE [Part::Cylinder] Cylinder2412  label="Válec2412"
  Angle = 360
  AttacherType = Attacher::AttachEngine3D
  Height = 20
  Placement = pos=(28,-16,-3) rot=(0,1,0;1.5708rad)
  Radius = 1.5
FEATURE [Part::Cylinder] Cylinder2413  label="Válec2413"
  Angle = 360
  AttacherType = Attacher::AttachEngine3D
  Height = 20
  Placement = pos=(26,-37,7) rot=(0,1,0;1.5708rad)
  Radius = 1.5
FEATURE [Part::Compound] Compound1056
  Links = -> [Cylinder2413,Cylinder2410,Cylinder2411,Cylinder2412]
  Placement = pos=(0,-80,-34) rot=(0,0,1;1.5708rad)
FEATURE [Part::Cut] Cut868
  Base = -> Cut867
  Tool = -> Compound1055
FEATURE [Part::Cut] Cut869  label="xori_xoro001"
  Base = -> Cut868
  Tool = -> Compound1056
FEATURE [Part::Cylinder] Cylinder2414  label="Válec2414"
  Angle = 360
  AttacherType = Attacher::AttachEngine3D
  Height = 20
  Placement = pos=(26,37,7) rot=(0,1,0;1.5708rad)
  Radius = 3
FEATURE [Part::Cylinder] Cylinder2415  label="Válec2415"
  Angle = 360
  AttacherType = Attacher::AttachEngine3D
  Height = 20
  Placement = pos=(26,-37,7) rot=(0,1,0;1.5708rad)
  Radius = 3
FEATURE [Part::Compound] Compound1057
  Links = -> [Cylinder2415,Cylinder2414]
  Placement = pos=(0,-91,-34) rot=(0,0,1;1.5708rad)
FEATURE [Part::Cut] Cut870
  Base = -> Cut869
  Tool = -> Compound1057
FEATURE [Part::Chamfer] Chamfer087
  Base = -> Cut870
  Edges = 1 edges r=3: [Edge24]
FEATURE [Part::Box] Box951  label="Krychle950"
  AttacherType = Attacher::AttachEngine3D
  Height = 28
  Length = 26
  Placement = pos=(-13,-49,-9) rot=(0,0,1;0rad)
  Width = 8
FEATURE [Part::Cut] Cut871
  Base = -> Chamfer087
  Tool = -> Box951
FEATURE [Part::Cylinder] Cylinder2416  label="L-elb_pulley-GT2-16-A001"
  Angle = 360
  AttacherType = Attacher::AttachEngine3D
  Height = 19
  Placement = pos=(-8,-45,-9) rot=(0,0,1;0.523599rad)
  Radius = 9
FEATURE [Part::Cylinder] Cylinder2417  label="L-elb_pulley-GT2-16-B001"
  Angle = 360
  AttacherType = Attacher::AttachEngine3D
  Height = 19
  Placement = pos=(8,-45,-9) rot=(0,0,1;0.523599rad)
  Radius = 9
FEATURE [Part::Compound] Compound1058
  Links = -> [Cylinder2416,Cylinder2417]
FEATURE [Part::Cut] Cut872
  Base = -> Cut871
  Tool = -> Compound1058
FEATURE [Part::Box] Box952  label="Krychle951"
  AttacherType = Attacher::AttachEngine3D
  Height = 28
  Length = 42
  Placement = pos=(-21,-48,4) rot=(0,0,1;0rad)
  Width = 6
FEATURE [Part::Box] Box953  label="Krychle952"
  AttacherType = Attacher::AttachEngine3D
  Height = 6
  Length = 52
  Placement = pos=(-26,-48,4) rot=(0,0,1;0rad)
  Width = 6
FEATURE [Part::Chamfer] Chamfer088
  Base = -> Box953
  Edges = 1 edges r=3: [Edge12]
FEATURE [Part::Box] Box954  label="Krychle953"
  AttacherType = Attacher::AttachEngine3D
  Height = 6
  Length = 52
  Placement = pos=(-26,-48,4) rot=(0,0,1;0rad)
  Width = 6
FEATURE [Part::Cut] Cut873
  Base = -> Cut872
  Tool = -> Box954
FEATURE [Part::Cylinder] Cylinder2418  label="L-elb_pulley-GT2-16-A002"
  Angle = 360
  AttacherType = Attacher::AttachEngine3D
  Height = 20
  Placement = pos=(-21,-45,-8) rot=(0,0,1;0.523599rad)
  Radius = 1.5
FEATURE [Part::Box] Box955  label="Krychle954"
  AttacherType = Attacher::AttachEngine3D
  Height = 2
  Length = 6
  Placement = pos=(-24,-48,-2) rot=(0,0,1;0rad)
  Width = 6
FEATURE [Part::Cylinder] Cylinder2419  label="L-elb_pulley-GT2-16-A003"
  Angle = 360
  AttacherType = Attacher::AttachEngine3D
  Height = 20
  Placement = pos=(21,-45,-8) rot=(0,0,1;0.523599rad)
  Radius = 1.5
FEATURE [Part::Box] Box956  label="Krychle955"
  AttacherType = Attacher::AttachEngine3D
  Height = 2
  Length = 6
  Placement = pos=(18,-48,-2) rot=(0,0,1;0rad)
  Width = 6
FEATURE [Part::Compound] Compound1059
  Links = -> [Box955,Box956]
FEATURE [Part::Cut] Cut874
  Base = -> Cut873
  Tool = -> Compound1059
FEATURE [Part::Compound] Compound1060
  Links = -> [Cylinder2418,Cylinder2419]
FEATURE [Part::Cylinder] Cylinder2420  label="L-elb_pulley-GT2-16-A004"
  Angle = 360
  AttacherType = Attacher::AttachEngine3D
  Height = 3
  Placement = pos=(21,-45,-8) rot=(0,0,1;0.523599rad)
  Radius = 3
FEATURE [Part::Cylinder] Cylinder2421  label="L-elb_pulley-GT2-16-A005"
  Angle = 360
  AttacherType = Attacher::AttachEngine3D
  Height = 3
  Placement = pos=(-21,-45,-8) rot=(0,0,1;0.523599rad)
  Radius = 3
FEATURE [Part::Compound] Compound1061
  Links = -> [Cylinder2421,Cylinder2420]
  Placement = pos=(0,0,15) rot=(0,0,1;0rad)
FEATURE [Part::Cut] Cut875
  Base = -> Chamfer088
  Tool = -> Compound1061
FEATURE [Part::Cut] Cut876
  Base = -> Cut875
  Tool = -> Compound1060
FEATURE [Part::Cylinder] Cylinder2422  label="L-elb_pulley-GT2-16-B002"
  Angle = 360
  AttacherType = Attacher::AttachEngine3D
  Height = 36
  Placement = pos=(9,-45,-6) rot=(0,0,1;0.523599rad)
  Radius = 1.5
FEATURE [Part::Cylinder] Cylinder2423  label="L-elb_pulley-GT2-16-A006"
  Angle = 360
  AttacherType = Attacher::AttachEngine3D
  Height = 36
  Placement = pos=(-9,-45,-6) rot=(0,0,1;0.523599rad)
  Radius = 1.5
FEATURE [Part::Cylinder] Cylinder2424  label="L-elb_pulley-GT2-16-B003"
  Angle = 360
  AttacherType = Attacher::AttachEngine3D
  Height = 3
  Placement = pos=(9,-45,-6) rot=(0,0,1;0.523599rad)
  Radius = 3
FEATURE [Part::Cylinder] Cylinder2425  label="L-elb_pulley-GT2-16-A007"
  Angle = 360
  AttacherType = Attacher::AttachEngine3D
  Height = 3
  Placement = pos=(-9,-45,-6) rot=(0,0,1;0.523599rad)
  Radius = 3
FEATURE [Part::Compound] Compound1062
  Links = -> [Cylinder2424,Cylinder2425]
  Placement = pos=(0,0,13) rot=(0,0,1;0rad)
FEATURE [Part::Box] Box957  label="Krychle956"
  AttacherType = Attacher::AttachEngine3D
  Height = 2
  Length = 6
  Placement = pos=(-12,-48,8) rot=(0,0,1;0rad)
  Width = 6
FEATURE [Part::Box] Box958  label="Krychle957"
  AttacherType = Attacher::AttachEngine3D
  Height = 2
  Length = 6
  Placement = pos=(6,-48,8) rot=(0,0,1;0rad)
  Width = 6
FEATURE [Part::Compound] Compound1063
  Links = -> [Box957,Box958]
  Placement = pos=(0,0,-23) rot=(0,0,1;0rad)
FEATURE [Part::Cut] Cut877
  Base = -> Cut874
  Tool = -> Compound1063
FEATURE [Part::Compound] Compound1064
  Links = -> [Cylinder2423,Cylinder2422]
  Placement = pos=(0,0,-16) rot=(0,0,1;0rad)
FEATURE [Part::Cut] Cut878
  Base = -> Cut877
  Tool = -> Compound1064
FEATURE [Part::Cylinder] Cylinder2426  label="L-elb_pulley-GT2-16-B004"
  Angle = 360
  AttacherType = Attacher::AttachEngine3D
  Height = 36
  Placement = pos=(9,-45,-6) rot=(0,0,1;0.523599rad)
  Radius = 1.5
FEATURE [Part::Cylinder] Cylinder2427  label="L-elb_pulley-GT2-16-A008"
  Angle = 360
  AttacherType = Attacher::AttachEngine3D
  Height = 36
  Placement = pos=(-9,-45,-6) rot=(0,0,1;0.523599rad)
  Radius = 1.5
FEATURE [Part::Compound] Compound1065
  Links = -> [Cylinder2427,Cylinder2426]
  Placement = pos=(0,0,-16) rot=(0,0,1;0rad)
FEATURE [Part::Cut] Cut879
  Base = -> Cut876
  Tool = -> Compound1062
FEATURE [Part::Cut] Cut880
  Base = -> Cut879
  Tool = -> Compound1065
FEATURE [Part::Cylinder] Cylinder2428  label="L-elb_pulley-GT2-16-A009"
  Angle = 360
  AttacherType = Attacher::AttachEngine3D
  Height = 20
  Placement = pos=(21,-45,-8) rot=(0,0,1;0.523599rad)
  Radius = 1.5
FEATURE [Part::Cylinder] Cylinder2429  label="L-elb_pulley-GT2-16-A010"
  Angle = 360
  AttacherType = Attacher::AttachEngine3D
  Height = 20
  Placement = pos=(-21,-45,-8) rot=(0,0,1;0.523599rad)
  Radius = 1.5
FEATURE [Part::Compound] Compound1066
  Links = -> [Cylinder2429,Cylinder2428]
FEATURE [Part::Cut] Cut881
  Base = -> Cut878
  Tool = -> Compound1066
FEATURE [Part::Cylinder] Cylinder2430  label="Válec2416"
  Angle = 360
  AttacherType = Attacher::AttachEngine3D
  Height = 20
  Placement = pos=(31,21,22) rot=(0,1,0;1.5708rad)
  Radius = 1.5
FEATURE [Part::Cylinder] Cylinder2431  label="Válec2417"
  Angle = 360
  AttacherType = Attacher::AttachEngine3D
  Height = 20
  Placement = pos=(31,-21,22) rot=(0,1,0;1.5708rad)
  Radius = 1.5
FEATURE [Part::Cylinder] Cylinder2432  label="Válec2418"
  Angle = 360
  AttacherType = Attacher::AttachEngine3D
  Height = 20
  Placement = pos=(26,37,19) rot=(0,1,0;1.5708rad)
  Radius = 1.5
FEATURE [Part::Cylinder] Cylinder2433  label="Válec2419"
  Angle = 360
  AttacherType = Attacher::AttachEngine3D
  Height = 20
  Placement = pos=(26,-37,19) rot=(0,1,0;1.5708rad)
  Radius = 1.5
FEATURE [Part::Compound] Compound1067
  Links = -> [Cylinder2432,Cylinder2430,Cylinder2431,Cylinder2433]
  Placement = pos=(0,-80,-34) rot=(0,0,1;1.5708rad)
FEATURE [Part::Cylinder] Cylinder2434  label="Válec2420"
  Angle = 360
  AttacherType = Attacher::AttachEngine3D
  Height = 20
  Placement = pos=(28,16,-3) rot=(0,1,0;1.5708rad)
  Radius = 1.5
FEATURE [Part::Cylinder] Cylinder2435  label="Válec2421"
  Angle = 360
  AttacherType = Attacher::AttachEngine3D
  Height = 20
  Placement = pos=(26,37,7) rot=(0,1,0;1.5708rad)
  Radius = 1.5
FEATURE [Part::Cylinder] Cylinder2436  label="Válec2422"
  Angle = 360
  AttacherType = Attacher::AttachEngine3D
  Height = 20
  Placement = pos=(28,-16,-3) rot=(0,1,0;1.5708rad)
  Radius = 1.5
FEATURE [Part::Cylinder] Cylinder2437  label="Válec2423"
  Angle = 360
  AttacherType = Attacher::AttachEngine3D
  Height = 20
  Placement = pos=(26,-37,7) rot=(0,1,0;1.5708rad)
  Radius = 1.5
FEATURE [Part::Compound] Compound1068
  Links = -> [Cylinder2437,Cylinder2434,Cylinder2435,Cylinder2436]
  Placement = pos=(0,-80,-34) rot=(0,0,1;1.5708rad)
FEATURE [Part::Box] Box959  label="Krychle958"
  AttacherType = Attacher::AttachEngine3D
  Height = 31
  Length = 80
  Placement = pos=(-40,-42,-40) rot=(0,0,1;0rad)
  Width = 3
FEATURE [Part::Cut] Cut882
  Base = -> Box959
  Tool = -> Compound1068
FEATURE [Part::Cut] Cut883  label="L-elb_xorior-washer"
  Base = -> Cut882
  Tool = -> Compound1067
FEATURE [Part::FeaturePython] Tube038  # WARN: FeaturePython — macro-defined, semantics opaque (R4)
  AttacherType = Attacher::AttachEngine3D
  Height = 1
  InnerRadius = 4.5
  OuterRadius = 5
  Placement = pos=(16,0,54) rot=(0,0,1;0rad)
FEATURE [Part::FeaturePython] Tube041  # WARN: FeaturePython — macro-defined, semantics opaque (R4)
  AttacherType = Attacher::AttachEngine3D
  Height = 1
  InnerRadius = 4.5
  OuterRadius = 5
  Placement = pos=(-8,-13.8564,54) rot=(0,0,1;4.18879rad)
FEATURE [Part::FeaturePython] Tube042  # WARN: FeaturePython — macro-defined, semantics opaque (R4)
  AttacherType = Attacher::AttachEngine3D
  Height = 1
  InnerRadius = 4.5
  OuterRadius = 5
  Placement = pos=(-8,13.8564,54) rot=(0,0,1;2.0944rad)
FEATURE [Part::FeaturePython] Tube046  # WARN: FeaturePython — macro-defined, semantics opaque (R4)
  AttacherType = Attacher::AttachEngine3D
  Height = 1
  InnerRadius = 7
  OuterRadius = 8
  Placement = pos=(0,0,55) rot=(0,0,1;0rad)
FEATURE [Part::Cylinder] Cylinder1195  label="Válec1195"
  Angle = 360
  AttacherType = Attacher::AttachEngine3D
  Height = 16
  Placement = pos=(0,0,100) rot=(0,0,1;0rad)
  Radius = 8
FEATURE [Part::Cylinder] Cylinder1196  label="Válec1196"
  Angle = 360
  AttacherType = Attacher::AttachEngine3D
  Height = 5
  Placement = pos=(-8,13.8564,50) rot=(0,0,1;2.0944rad)
  Radius = 5
FEATURE [Part::Cylinder] Cylinder1197  label="Válec1197"
  Angle = 360
  AttacherType = Attacher::AttachEngine3D
  Height = 5
  Placement = pos=(16,0,50) rot=(0,0,1;0rad)
  Radius = 5
FEATURE [Part::Cylinder] Cylinder1198  label="Válec1198"
  Angle = 360
  AttacherType = Attacher::AttachEngine3D
  Height = 8
  Placement = pos=(0,0,50) rot=(0,0,1;0rad)
  Radius = 24
FEATURE [Part::Cylinder] Cylinder1199  label="Válec1199"
  Angle = 360
  AttacherType = Attacher::AttachEngine3D
  Height = 3
  Placement = pos=(3.5,16,55) rot=(0,0,1;0rad)
  Radius = 3
FEATURE [Part::Cylinder] Cylinder1200  label="Válec1200"
  Angle = 360
  AttacherType = Attacher::AttachEngine3D
  Height = 3
  Placement = pos=(-3.5,16,55) rot=(0,0,1;0rad)
  Radius = 3
FEATURE [Part::Compound] Compound639
  Links = -> [Cylinder1199,Cylinder1200]
  Placement = pos=(0,0,0) rot=(0,0,-1;0.523599rad)
FEATURE [Part::Cylinder] Cylinder1202  label="Válec1202"
  Angle = 360
  AttacherType = Attacher::AttachEngine3D
  Height = 20
  Placement = pos=(3.5,16,40) rot=(0,0,1;0rad)
  Radius = 1.5
FEATURE [Part::Cylinder] Cylinder1203  label="Válec1203"
  Angle = 360
  AttacherType = Attacher::AttachEngine3D
  Height = 5
  Placement = pos=(-8,-13.8564,50) rot=(0,0,1;4.18879rad)
  Radius = 5
FEATURE [Part::Compound] Compound638
  Links = -> [Cylinder1203,Cylinder1196,Cylinder1197]
FEATURE [Part::Cylinder] Cylinder1205  label="Válec1205"
  Angle = 360
  AttacherType = Attacher::AttachEngine3D
  Height = 20
  Placement = pos=(-3.5,16,40) rot=(0,0,1;0rad)
  Radius = 1.5
FEATURE [Part::Cylinder] Cylinder829  label="Válec829"
  Angle = 360
  AttacherType = Attacher::AttachEngine3D
  Height = 6
  Placement = pos=(0,0,50) rot=(0,0,1;0rad)
  Radius = 8
FEATURE [Part::Cut] Cut442
  Base = -> Cylinder1198
  Tool = -> Cylinder1195
FEATURE [Part::Cut] Cut445
  Base = -> Cut442
  Tool = -> Compound638
FEATURE [Part::Compound] Compound642
  Links = -> [Cylinder1199,Cylinder1200]
  Placement = pos=(0,0,0) rot=(0,0,1;1.5708rad)
FEATURE [Part::Compound] Compound643
  Links = -> [Cylinder1202,Cylinder1205]
  Placement = pos=(0,0,0) rot=(0,0,-1;0.523599rad)
FEATURE [Part::Compound] Compound644
  Links = -> [Cylinder1199,Cylinder1200]
  Placement = pos=(0,0,0) rot=(0,0,1;3.66519rad)
FEATURE [Part::Compound] Compound641
  Links = -> [Compound639,Compound644,Compound642]
FEATURE [Part::Cut] Cut443
  Base = -> Cut445
  Tool = -> Compound641
FEATURE [Part::Compound] Compound645
  Links = -> [Cylinder1202,Cylinder1205]
  Placement = pos=(0,0,0) rot=(0,0,1;3.66519rad)
FEATURE [Part::Compound] Compound649
  Links = -> [Tube042,Tube041,Tube038]
FEATURE [Part::Compound] Compound650
  Links = -> [Cylinder1202,Cylinder1205]
  Placement = pos=(0,0,0) rot=(0,0,1;1.5708rad)
FEATURE [Part::Compound] Compound646
  Links = -> [Compound643,Compound645,Compound650]
FEATURE [Part::Cut] Cut447
  Base = -> Cut443
  Tool = -> Compound646
FEATURE [Part::Compound] Compound640  label="jointovina_micro_quikovina1"
  Links = -> [Compound649,Cut447]
FEATURE [Part::Cut] Cut448
  Base = -> Compound640
  Tool = -> Cylinder829
FEATURE [Part::Compound] Compound651  label="jointovina_micro_quikovina"
  Links = -> [Cut448,Tube046]
FEATURE [Part::Cylinder] Cylinder1920  label="Válec1920"
  Angle = 360
  AttacherType = Attacher::AttachEngine3D
  Height = 8
  Placement = pos=(0,0,88) rot=(0,0,1;0rad)
  Radius = 6
FEATURE [Part::Chamfer] Chamfer011
  Base = -> Cylinder1920
  Edges = 1 edges r=1: [Edge1]
  Placement = pos=(0,0,-30) rot=(0,0,1;0rad)
FEATURE [Part::FeaturePython] Tube083  # WARN: FeaturePython — macro-defined, semantics opaque (R4)
  AttacherType = Attacher::AttachEngine3D
  Height = 1
  InnerRadius = 6
  OuterRadius = 8
  Placement = pos=(0,0,58) rot=(0,0,1;0rad)
FEATURE [Part::Compound] Compound874  label="J-mini_quikovina"
  Links = -> [Compound651,Chamfer011,Tube083]
  Placement = pos=(0,0,-58) rot=(0,0,1;0rad)
FEATURE [Part::Cylinder] Cylinder1512  label="Válec1512"
  Angle = 360
  AttacherType = Attacher::AttachEngine3D
  Height = 8
  Radius = 40
FEATURE [Part::Cylinder] Cylinder1513  label="Válec1513"
  Angle = 360
  AttacherType = Attacher::AttachEngine3D
  Height = 30
  Placement = pos=(1.1e-14,-27,19) rot=(0,0,1;3.14159rad)
  Radius = 1
FEATURE [Part::Cylinder] Cylinder1514  label="Válec1514"
  Angle = 360
  AttacherType = Attacher::AttachEngine3D
  Height = 30
  Placement = pos=(-19.0919,19.0919,19) rot=(0,0,1;0.785398rad)
  Radius = 1
FEATURE [Part::Cylinder] Cylinder1515  label="Válec1515"
  Angle = 360
  AttacherType = Attacher::AttachEngine3D
  Height = 30
  Placement = pos=(19.0919,19.0919,19) rot=(0,0,-1;0.785398rad)
  Radius = 1
FEATURE [Part::Cylinder] Cylinder1517  label="Válec1517"
  Angle = 360
  AttacherType = Attacher::AttachEngine3D
  Height = 30
  Placement = pos=(19.0919,-19.0919,19) rot=(0,0,1;3.92699rad)
  Radius = 1
FEATURE [Part::Cylinder] Cylinder1518  label="Válec1518"
  Angle = 360
  AttacherType = Attacher::AttachEngine3D
  Height = 30
  Placement = pos=(0,27,19) rot=(0,0,1;0rad)
  Radius = 1
FEATURE [Part::Cylinder] Cylinder1519  label="Válec1519"
  Angle = 360
  AttacherType = Attacher::AttachEngine3D
  Height = 30
  Placement = pos=(27,1e-14,19) rot=(0,0,-1;1.5708rad)
  Radius = 1
FEATURE [Part::Cylinder] Cylinder1520  label="Válec1520"
  Angle = 360
  AttacherType = Attacher::AttachEngine3D
  Height = 30
  Placement = pos=(-27,-4e-15,19) rot=(0,0,1;1.5708rad)
  Radius = 1
FEATURE [Part::Cylinder] Cylinder1521  label="Válec1521"
  Angle = 360
  AttacherType = Attacher::AttachEngine3D
  Height = 30
  Placement = pos=(-19.0919,-19.0919,19) rot=(0,0,1;2.35619rad)
  Radius = 1
FEATURE [Part::Compound] Compound743
  Links = -> [Cylinder1518,Cylinder1514,Cylinder1520,Cylinder1521,Cylinder1513,Cylinder1517,Cylinder1519,Cylinder1515]
  Placement = pos=(0,0,-33) rot=(0,0,1;0rad)
FEATURE [Part::Cut] Cut554  label="boko"
  Base = -> Cylinder1512
  Tool = -> Compound743
FEATURE [Part::Cylinder] Cylinder2438  label="Válec2424"
  Angle = 360
  AttacherType = Attacher::AttachEngine3D
  Height = 34
  Placement = pos=(0,0,-21) rot=(0,0,1;0rad)
  Radius = 25
FEATURE [Part::Cut] Cut884  label="J-mini_belt-ring-lower"
  Base = -> Cut554
  Placement = pos=(0,0,-8) rot=(0,0,1;0rad)
  Tool = -> Cylinder2438
FEATURE [Part::Cylinder] Cylinder2439  label="Válec2425"
  Angle = 360
  AttacherType = Attacher::AttachEngine3D
  Height = 34
  Placement = pos=(0,0,-21) rot=(0,0,1;0rad)
  Radius = 25
FEATURE [Part::Cylinder] Cylinder2440  label="Válec2426"
  Angle = 360
  AttacherType = Attacher::AttachEngine3D
  Height = 3
  Radius = 38
FEATURE [Part::Cut] Cut885
  Base = -> Cylinder2440
  Tool = -> Cylinder2439
FEATURE [Part::Chamfer] Chamfer089
  Base = -> Cut885
  Edges = 1 edges r=1: [Edge1]
FEATURE [Part::FeaturePython] Tube084  # WARN: FeaturePython — macro-defined, semantics opaque (R4)
  AttacherType = Attacher::AttachEngine3D
  Height = 7
  InnerRadius = 25
  OuterRadius = 35
  Placement = pos=(0,0,3) rot=(0,0,1;0rad)
FEATURE [Part::Cylinder] Cylinder1833  label="Válec1833"
  Angle = 360
  AttacherType = Attacher::AttachEngine3D
  Height = 7
  Placement = pos=(0,0,-22) rot=(0,0,1;0rad)
  Radius = 31
FEATURE [Part::Box] Box736  label="Krychle736"
  AttacherType = Attacher::AttachEngine3D
  Height = 7
  Length = 1.4
  Placement = pos=(0,0,-22) rot=(0,0,-1;0.05236rad)
  Width = 60
FEATURE [Part::Box] Box737  label="Krychle737"
  AttacherType = Attacher::AttachEngine3D
  Height = 7
  Length = 1.4
  Placement = pos=(0,0,-22) rot=(0,0,1;0.099484rad)
  Width = 60
FEATURE [Part::Compound] Compound906
  Links = -> [Box736,Box737]
FEATURE [Part::Cut] Cut549
  Base = -> Compound906
  Placement = pos=(0,0,25) rot=(0,0,1;0rad)
  Tool = -> Cylinder1833
FEATURE [Part::Box] Box731  label="Krychle731"
  AttacherType = Attacher::AttachEngine3D
  Height = 7
  Length = 60
  Placement = pos=(0,0,-22) rot=(0,0,-1;0.349066rad)
  Width = 60
FEATURE [Part::Box] Box732  label="Krychle732"
  AttacherType = Attacher::AttachEngine3D
  Height = 7
  Length = 60
  Placement = pos=(-56.3816,-20.5212,-22) rot=(0,0,1;0.349066rad)
  Width = 60
FEATURE [Part::Box] Box733  label="Krychle733"
  AttacherType = Attacher::AttachEngine3D
  Height = 7
  Length = 60
  Placement = pos=(0,0,-22) rot=(0,0,-1;0.034907rad)
  Width = 60
FEATURE [Part::Box] Box739  label="Krychle739"
  AttacherType = Attacher::AttachEngine3D
  Height = 7
  Length = 120
  Placement = pos=(-60,-60,-22) rot=(0,0,-1;0rad)
  Width = 60
FEATURE [Part::Box] Box740  label="Krychle740"
  AttacherType = Attacher::AttachEngine3D
  Height = 7
  Length = 60
  Placement = pos=(-59.9909,-1.04714,-22) rot=(0,0,1;0.017453rad)
  Width = 60
FEATURE [Part::Compound] Compound904
  Links = -> [Box733,Box740]
FEATURE [Part::Box] Box741  label="Krychle741"
  AttacherType = Attacher::AttachEngine3D
  Height = 7
  Length = 120
  Placement = pos=(-60,-60,-22) rot=(0,0,-1;0rad)
  Width = 60
FEATURE [Part::FeaturePython] Tube093  # WARN: FeaturePython — macro-defined, semantics opaque (R4)
  AttacherType = Attacher::AttachEngine3D
  Height = 7
  InnerRadius = 31
  OuterRadius = 32.4
  Placement = pos=(0,0,-22) rot=(0,0,1;0rad)
FEATURE [Part::Cut] Cut560
  Base = -> Tube093
  Tool = -> Box739
FEATURE [Part::FeaturePython] Tube094  # WARN: FeaturePython — macro-defined, semantics opaque (R4)
  AttacherType = Attacher::AttachEngine3D
  Height = 7
  InnerRadius = 31
  OuterRadius = 32.4
  Placement = pos=(0,0,-22) rot=(0,0,1;0rad)
FEATURE [Part::Cut] Cut556
  Base = -> Tube094
  Tool = -> Box741
FEATURE [Part::Cut] Cut555
  Base = -> Cut556
  Placement = pos=(0,0,-7) rot=(0,0,1;0rad)
  Tool = -> Compound904
FEATURE [Part::Compound] Compound908
  Links = -> [Box731,Box732]
FEATURE [Part::Cut] Cut557
  Base = -> Cut560
  Placement = pos=(0,0,-7) rot=(0,0,1;0rad)
  Tool = -> Compound908
FEATURE [Part::Cut] Cut553
  Base = -> Cut557
  Placement = pos=(0,0,32) rot=(0,0,1;0rad)
  Tool = -> Cut555
FEATURE [Part::Cut] Cut886
  Base = -> Tube084
  Tool = -> Cut549
FEATURE [Part::Cut] Cut887
  Base = -> Cut886
  Tool = -> Cut553
FEATURE [Part::Cylinder] Cylinder2441  label="Válec2427"
  Angle = 360
  AttacherType = Attacher::AttachEngine3D
  Height = 34
  Placement = pos=(0,0,-21) rot=(0,0,1;0rad)
  Radius = 14
FEATURE [Part::Cylinder] Cylinder2442  label="Válec2428"
  Angle = 360
  AttacherType = Attacher::AttachEngine3D
  Height = 3
  Radius = 38
FEATURE [Part::Cut] Cut888
  Base = -> Cylinder2442
  Placement = pos=(0,0,10) rot=(0,0,1;0rad)
  Tool = -> Cylinder2441
FEATURE [Part::Chamfer] Chamfer090  label="J-mini_encoder-belt-ring_front1"
  Base = -> Cut888
  Edges = 1 edges r=1: [Edge3]
  Placement = pos=(0,0,-8) rot=(0,0,1;0rad)
FEATURE [Part::Compound] Compound1069  label="J-mini_encoder-belt-ring_rear1"
  Links = -> [Chamfer089,Cut887]
  Placement = pos=(0,0,-8) rot=(0,0,1;0rad)
FEATURE [Part::FeaturePython] Tube100  # WARN: FeaturePython — macro-defined, semantics opaque (R4)
  AttacherType = Attacher::AttachEngine3D
  Height = 1
  InnerRadius = 12
  OuterRadius = 18
  Placement = pos=(0,0,96) rot=(0,0,1;0rad)
FEATURE [Part::FeaturePython] Tube099  # WARN: FeaturePython — macro-defined, semantics opaque (R4)
  AttacherType = Attacher::AttachEngine3D
  Height = 8
  InnerRadius = 14.1
  OuterRadius = 18
  Placement = pos=(0,0,88) rot=(0,0,1;0rad)
FEATURE [Part::Chamfer] Chamfer091
  Base = -> Tube099
  Edges = 1 edges r=1: [Edge5]
FEATURE [Part::Compound] Compound1070
  Links = -> [Tube100,Chamfer091]
  Placement = pos=(0,0,-88) rot=(0,0,1;0rad)
FEATURE [Part::FeaturePython] Tube057  label="6001-2RS"  # WARN: FeaturePython — macro-defined, semantics opaque (R4)
  AttacherType = Attacher::AttachEngine3D
  Height = 8
  InnerRadius = 6
  OuterRadius = 14
  Placement = pos=(0,0,1) rot=(0,0,1;0rad)
FEATURE [Part::Box] Box781  label="Krychle780"
  AttacherType = Attacher::AttachEngine3D
  Height = 80
  Length = 31
  Placement = pos=(-16,330,-48) rot=(0,0,1;0rad)
  Width = 6
FEATURE [Part::Box] Box782  label="Krychle781"
  AttacherType = Attacher::AttachEngine3D
  Height = 80
  Length = 12
  Placement = pos=(-6,25,-48) rot=(0,0,1;0rad)
  Width = 8
FEATURE [Part::Cylinder] Cylinder1983  label="Válec1983"
  Angle = 360
  AttacherType = Attacher::AttachEngine3D
  Height = 30
  Placement = pos=(51,-30,0) rot=(0,0,1;0rad)
  Radius = 1.5
FEATURE [Part::Cylinder] Cylinder1984  label="Válec1984"
  Angle = 360
  AttacherType = Attacher::AttachEngine3D
  Height = 30
  Placement = pos=(51,0,0) rot=(0,0,1;0rad)
  Radius = 1.5
FEATURE [Part::Cylinder] Cylinder1985  label="Válec1985"
  Angle = 360
  AttacherType = Attacher::AttachEngine3D
  Height = 30
  Placement = pos=(51,30,0) rot=(0,0,1;0rad)
  Radius = 1.5
FEATURE [Part::Compound] Compound896
  Links = -> [Cylinder1983,Cylinder1984,Cylinder1985]
FEATURE [Part::Box] Box783  label="Krychle782"
  AttacherType = Attacher::AttachEngine3D
  Height = 2
  Length = 6
  Placement = pos=(48,-3,7) rot=(0,0,1;0rad)
  Width = 6
FEATURE [Part::Box] Box784  label="Krychle783"
  AttacherType = Attacher::AttachEngine3D
  Height = 2
  Length = 6
  Placement = pos=(48,-3,11) rot=(0,0,1;0rad)
  Width = 6
FEATURE [Part::Box] Box785  label="Krychle784"
  AttacherType = Attacher::AttachEngine3D
  Height = 2
  Length = 6
  Placement = pos=(48,-33,11) rot=(0,0,1;0rad)
  Width = 6
FEATURE [Part::Box] Box786  label="Krychle785"
  AttacherType = Attacher::AttachEngine3D
  Height = 2
  Length = 6
  Placement = pos=(48,-33,7) rot=(0,0,1;0rad)
  Width = 6
FEATURE [Part::Box] Box787  label="Krychle786"
  AttacherType = Attacher::AttachEngine3D
  Height = 2
  Length = 6
  Placement = pos=(48,27,11) rot=(0,0,1;0rad)
  Width = 6
FEATURE [Part::Box] Box788  label="Krychle787"
  AttacherType = Attacher::AttachEngine3D
  Height = 2
  Length = 6
  Placement = pos=(48,27,7) rot=(0,0,1;0rad)
  Width = 6
FEATURE [Part::Compound] Compound897
  Links = -> [Box783,Box784,Box785,Box786,Box787,Box788]
FEATURE [Part::Cylinder] Cylinder1987  label="Válec1987"
  Angle = 360
  AttacherType = Attacher::AttachEngine3D
  Height = 10
  Placement = pos=(46,0,10) rot=(0,1,0;1.5708rad)
  Radius = 38
FEATURE [Part::Cylinder] Cylinder1988  label="Válec1988"
  Angle = 360
  AttacherType = Attacher::AttachEngine3D
  Height = 4
  Radius = 38
FEATURE [Part::Compound] Compound893
  Links = -> [Box782,Box781]
  Placement = pos=(79,-8,10) rot=(0.57735,-0.57735,0.57735;2.0944rad)
FEATURE [Part::Common] Common001
  Base = -> Compound893
  Tool = -> Cylinder1987
FEATURE [Part::Cut] Cut889
  Base = -> Common001
  Tool = -> Compound897
FEATURE [Part::Cut] Cut561
  Base = -> Cut889
  Tool = -> Compound896
FEATURE [Part::Cylinder] Cylinder1997  label="Válec1997"
  Angle = 360
  AttacherType = Attacher::AttachEngine3D
  Height = 20
  Placement = pos=(-27,-4e-15,19) rot=(0,0,1;1.5708rad)
  Radius = 1
FEATURE [Part::Cylinder] Cylinder1998  label="Válec1998"
  Angle = 360
  AttacherType = Attacher::AttachEngine3D
  Height = 20
  Placement = pos=(19.0919,19.0919,19) rot=(0,0,-1;0.785398rad)
  Radius = 1
FEATURE [Part::Cylinder] Cylinder1999  label="Válec1999"
  Angle = 360
  AttacherType = Attacher::AttachEngine3D
  Height = 20
  Placement = pos=(1.1e-14,-27,19) rot=(0,0,1;3.14159rad)
  Radius = 1
FEATURE [Part::Cylinder] Cylinder2000  label="Válec2000"
  Angle = 360
  AttacherType = Attacher::AttachEngine3D
  Height = 20
  Placement = pos=(19.0919,-19.0919,19) rot=(0,0,1;3.92699rad)
  Radius = 1
FEATURE [Part::Cylinder] Cylinder2001  label="Válec2001"
  Angle = 360
  AttacherType = Attacher::AttachEngine3D
  Height = 20
  Placement = pos=(27,1e-14,19) rot=(0,0,-1;1.5708rad)
  Radius = 1
FEATURE [Part::Cylinder] Cylinder2002  label="Válec2002"
  Angle = 360
  AttacherType = Attacher::AttachEngine3D
  Height = 20
  Placement = pos=(0,27,19) rot=(0,0,1;0rad)
  Radius = 1
FEATURE [Part::Cylinder] Cylinder2003  label="Válec2003"
  Angle = 360
  AttacherType = Attacher::AttachEngine3D
  Height = 20
  Placement = pos=(-19.0919,-19.0919,19) rot=(0,0,1;2.35619rad)
  Radius = 1
FEATURE [Part::Cylinder] Cylinder2004  label="Válec2004"
  Angle = 360
  AttacherType = Attacher::AttachEngine3D
  Height = 20
  Placement = pos=(-19.0919,19.0919,19) rot=(0,0,1;0.785398rad)
  Radius = 1
FEATURE [Part::Compound] Compound899
  Links = -> [Cylinder2002,Cylinder2004,Cylinder1997,Cylinder2003,Cylinder1999,Cylinder2000,Cylinder2001,Cylinder1998]
  Placement = pos=(0,0,-33) rot=(0,0,1;0rad)
FEATURE [Part::Cylinder] Cylinder2005  label="Válec2005"
  Angle = 360
  AttacherType = Attacher::AttachEngine3D
  Height = 2
  Placement = pos=(-27,-4e-15,19) rot=(0,0,1;1.5708rad)
  Radius = 2
FEATURE [Part::Cylinder] Cylinder2006  label="Válec2006"
  Angle = 360
  AttacherType = Attacher::AttachEngine3D
  Height = 2
  Placement = pos=(19.0919,19.0919,19) rot=(0,0,-1;0.785398rad)
  Radius = 2
FEATURE [Part::Cylinder] Cylinder2007  label="Válec2007"
  Angle = 360
  AttacherType = Attacher::AttachEngine3D
  Height = 2
  Placement = pos=(1.1e-14,-27,19) rot=(0,0,1;3.14159rad)
  Radius = 2
FEATURE [Part::Cylinder] Cylinder2008  label="Válec2008"
  Angle = 360
  AttacherType = Attacher::AttachEngine3D
  Height = 2
  Placement = pos=(-19.0919,-19.0919,19) rot=(0,0,1;2.35619rad)
  Radius = 2
FEATURE [Part::Cylinder] Cylinder2009  label="Válec2009"
  Angle = 360
  AttacherType = Attacher::AttachEngine3D
  Height = 2
  Placement = pos=(0,27,19) rot=(0,0,1;0rad)
  Radius = 2
FEATURE [Part::Cylinder] Cylinder2010  label="Válec2010"
  Angle = 360
  AttacherType = Attacher::AttachEngine3D
  Height = 2
  Placement = pos=(-19.0919,19.0919,19) rot=(0,0,1;0.785398rad)
  Radius = 2
FEATURE [Part::Cylinder] Cylinder2011  label="Válec2011"
  Angle = 360
  AttacherType = Attacher::AttachEngine3D
  Height = 2
  Placement = pos=(19.0919,-19.0919,19) rot=(0,0,1;3.92699rad)
  Radius = 2
FEATURE [Part::Cylinder] Cylinder2012  label="Válec2012"
  Angle = 360
  AttacherType = Attacher::AttachEngine3D
  Height = 2
  Placement = pos=(27,1e-14,19) rot=(0,0,-1;1.5708rad)
  Radius = 2
FEATURE [Part::Compound] Compound900
  Links = -> [Cylinder2009,Cylinder2010,Cylinder2005,Cylinder2008,Cylinder2007,Cylinder2011,Cylinder2012,Cylinder2006]
  Placement = pos=(0,0,-20) rot=(0,0,1;0rad)
FEATURE [Part::Cut] Cut621
  Base = -> Cylinder1988
  Tool = -> Compound900
FEATURE [Part::Cut] Cut622
  Base = -> Cut621
  Placement = pos=(46,0,10) rot=(-0.19148,-0.962637,0.19148;1.60887rad)
  Tool = -> Compound899
FEATURE [Part::Compound] Compound1071  label="J-mini_side-actuator"
  Links = -> [Cut622,Cut561]
  Placement = pos=(10,0,-31) rot=(0,-1,0;1.5708rad)
FEATURE [Part::Cylinder] Cylinder2443  label="Válec2429"
  Angle = 360
  AttacherType = Attacher::AttachEngine3D
  Height = 34
  Placement = pos=(0,0,-21) rot=(0,0,1;0rad)
  Radius = 25
FEATURE [Part::Cylinder] Cylinder2444  label="Válec2430"
  Angle = 360
  AttacherType = Attacher::AttachEngine3D
  Height = 5
  Radius = 38
FEATURE [Part::Cut] Cut890
  Base = -> Cylinder2444
  Placement = pos=(0,0,4) rot=(0,0,1;0rad)
  Tool = -> Cylinder2443
FEATURE [Part::FeaturePython] Tube101  # WARN: FeaturePython — macro-defined, semantics opaque (R4)
  AttacherType = Attacher::AttachEngine3D
  Height = 1
  InnerRadius = 25
  OuterRadius = 38
  Placement = pos=(0,0,9) rot=(0,0,1;0rad)
FEATURE [Part::Compound] Compound1072  label="J-micro_actuator-underwasher"
  Links = -> [Compound1070,Cut890,Tube101]
  Placement = pos=(0,0,1) rot=(0,0,1;0rad)
FEATURE [Part::Cylinder] Cylinder1911  label="Válec1911"
  Angle = 360
  AttacherType = Attacher::AttachEngine3D
  Height = 8
  Placement = pos=(0,0,50) rot=(0,0,1;0rad)
  Radius = 24
FEATURE [Part::Cylinder] Cylinder1909  label="Válec1909"
  Angle = 360
  AttacherType = Attacher::AttachEngine3D
  Height = 5
  Placement = pos=(16,0,50) rot=(0,0,1;0rad)
  Radius = 5
FEATURE [Part::Cylinder] Cylinder1910  label="Válec1910"
  Angle = 360
  AttacherType = Attacher::AttachEngine3D
  Height = 16
  Placement = pos=(0,0,48) rot=(0,0,1;0rad)
  Radius = 8
FEATURE [Part::Cylinder] Cylinder1912  label="Válec1912"
  Angle = 360
  AttacherType = Attacher::AttachEngine3D
  Height = 5
  Placement = pos=(-8,13.8564,50) rot=(0,0,1;2.0944rad)
  Radius = 5
FEATURE [Part::Cylinder] Cylinder1913  label="Válec1913"
  Angle = 360
  AttacherType = Attacher::AttachEngine3D
  Height = 5
  Placement = pos=(-8,-13.8564,50) rot=(0,0,1;4.18879rad)
  Radius = 5
FEATURE [Part::Cut] Cut699
  Base = -> Cylinder1911
  Tool = -> Cylinder1910
FEATURE [Part::FeaturePython] Tube079  # WARN: FeaturePython — macro-defined, semantics opaque (R4)
  AttacherType = Attacher::AttachEngine3D
  Height = 1
  InnerRadius = 4.5
  OuterRadius = 5
  Placement = pos=(16,0,54) rot=(0,0,1;0rad)
FEATURE [Part::FeaturePython] Tube080  # WARN: FeaturePython — macro-defined, semantics opaque (R4)
  AttacherType = Attacher::AttachEngine3D
  Height = 1
  InnerRadius = 4.5
  OuterRadius = 5
  Placement = pos=(-8,13.8564,54) rot=(0,0,1;2.0944rad)
FEATURE [Part::FeaturePython] Tube081  # WARN: FeaturePython — macro-defined, semantics opaque (R4)
  AttacherType = Attacher::AttachEngine3D
  Height = 1
  InnerRadius = 4.5
  OuterRadius = 5
  Placement = pos=(-8,-13.8564,54) rot=(0,0,1;4.18879rad)
FEATURE [Part::FeaturePython] Tube082  # WARN: FeaturePython — macro-defined, semantics opaque (R4)
  AttacherType = Attacher::AttachEngine3D
  Height = 27
  InnerRadius = 12
  OuterRadius = 20.5
  Placement = pos=(0,0,23) rot=(0,0,1;0rad)
FEATURE [Part::Compound] Compound861
  Links = -> [Cylinder1913,Cylinder1912,Cylinder1909]
FEATURE [Part::Cut] Cut700
  Base = -> Cut699
  Tool = -> Compound861
FEATURE [Part::Compound] Compound871
  Links = -> [Tube080,Tube081,Tube079]
FEATURE [Part::Cylinder] Cylinder1914  label="Válec1914"
  Angle = 360
  AttacherType = Attacher::AttachEngine3D
  Height = 3
  Placement = pos=(3.5,16,55) rot=(0,0,1;0rad)
  Radius = 3
FEATURE [Part::Cylinder] Cylinder1915  label="Válec1915"
  Angle = 360
  AttacherType = Attacher::AttachEngine3D
  Height = 3
  Placement = pos=(-3.5,16,55) rot=(0,0,1;0rad)
  Radius = 3
FEATURE [Part::Compound] Compound863
  Links = -> [Cylinder1914,Cylinder1915]
  Placement = pos=(0,0,0) rot=(0,0,-1;0.523599rad)
FEATURE [Part::Compound] Compound864
  Links = -> [Cylinder1914,Cylinder1915]
  Placement = pos=(0,0,0) rot=(0,0,1;3.66519rad)
FEATURE [Part::Compound] Compound865
  Links = -> [Cylinder1914,Cylinder1915]
  Placement = pos=(0,0,0) rot=(0,0,1;1.5708rad)
FEATURE [Part::Compound] Compound866
  Links = -> [Compound863,Compound864,Compound865]
FEATURE [Part::Cut] Cut704
  Base = -> Cut700
  Tool = -> Compound866
FEATURE [Part::Box] Box755  label="Krychle754"
  AttacherType = Attacher::AttachEngine3D
  Height = 60
  Length = 20
  Placement = pos=(-19.32,-5.18,0) rot=(0,0,1;0.383972rad)
  Width = 40
FEATURE [Part::Box] Box756  label="Krychle755"
  AttacherType = Attacher::AttachEngine3D
  Height = 60
  Length = 60
  Placement = pos=(-30,-35,0) rot=(0,0,1;0rad)
  Width = 40
FEATURE [Part::Cut] Cut701
  Base = -> Tube082
  Tool = -> Box756
FEATURE [Part::Cut] Cut702
  Base = -> Cut701
  Tool = -> Box755
FEATURE [Part::Box] Box757  label="Krychle756"
  AttacherType = Attacher::AttachEngine3D
  Height = 60
  Length = 20
  Placement = pos=(0,0,0) rot=(0,0,-1;0.383972rad)
  Width = 40
FEATURE [Part::Cut] Cut703
  Base = -> Cut702
  Tool = -> Box757
FEATURE [Part::Cylinder] Cylinder1916  label="Válec1916"
  Angle = 360
  AttacherType = Attacher::AttachEngine3D
  Height = 60
  Placement = pos=(3.5,16,0) rot=(0,0,1;0rad)
  Radius = 1.5
FEATURE [Part::Cylinder] Cylinder1917  label="Válec1917"
  Angle = 360
  AttacherType = Attacher::AttachEngine3D
  Height = 60
  Placement = pos=(-3.5,16,0) rot=(0,0,1;0rad)
  Radius = 1.5
FEATURE [Part::Compound] Compound862
  Links = -> [Cylinder1916,Cylinder1917]
FEATURE [Part::Cut] Cut708
  Base = -> Cut703
  Placement = pos=(0,0,0) rot=(0,0,1;3.66519rad)
  Tool = -> Compound862
FEATURE [Part::Cut] Cut707
  Base = -> Cut703
  Placement = pos=(0,0,0) rot=(0,0,1;1.5708rad)
  Tool = -> Compound862
FEATURE [Part::Cut] Cut706
  Base = -> Cut703
  Placement = pos=(0,0,0) rot=(0,0,-1;0.523599rad)
  Tool = -> Compound862
FEATURE [Part::Cylinder] Cylinder1918  label="Válec1918"
  Angle = 360
  AttacherType = Attacher::AttachEngine3D
  Height = 20
  Placement = pos=(3.5,16,40) rot=(0,0,1;0rad)
  Radius = 1.5
FEATURE [Part::Cylinder] Cylinder1919  label="Válec1919"
  Angle = 360
  AttacherType = Attacher::AttachEngine3D
  Height = 20
  Placement = pos=(-3.5,16,40) rot=(0,0,1;0rad)
  Radius = 1.5
FEATURE [Part::Compound] Compound867
  Links = -> [Cylinder1918,Cylinder1919]
  Placement = pos=(0,0,0) rot=(0,0,-1;0.523599rad)
FEATURE [Part::Compound] Compound868
  Links = -> [Cylinder1918,Cylinder1919]
  Placement = pos=(0,0,0) rot=(0,0,1;3.66519rad)
FEATURE [Part::Compound] Compound869
  Links = -> [Cylinder1918,Cylinder1919]
  Placement = pos=(0,0,0) rot=(0,0,1;1.5708rad)
FEATURE [Part::Compound] Compound870
  Links = -> [Compound867,Compound868,Compound869]
FEATURE [Part::Cut] Cut705
  Base = -> Cut704
  Tool = -> Compound870
FEATURE [Part::Compound] Compound872  label="jointovina_micro_pikovina002"
  Links = -> [Compound871,Cut705]
FEATURE [Part::Compound] Compound873  label="jointovina_micro_pikovina_rot"
  Links = -> [Compound872,Cut706,Cut707,Cut708]
  Placement = pos=(0,1,15) rot=(1,0,0;3.14159rad)
FEATURE [Part::FeaturePython] Tube012  # WARN: FeaturePython — macro-defined, semantics opaque (R4)
  AttacherType = Attacher::AttachEngine3D
  Height = 4
  InnerRadius = 26
  OuterRadius = 32
  Placement = pos=(0,0,-47) rot=(0,0,1;0rad)
FEATURE [Part::Cylinder] Cylinder1896  label="Válec1896"
  Angle = 360
  AttacherType = Attacher::AttachEngine3D
  Height = 20
  Placement = pos=(11.1,26.79,-50) rot=(0,0,1;1.1781rad)
  Radius = 1.5
FEATURE [Part::Cylinder] Cylinder1897  label="Válec1897"
  Angle = 360
  AttacherType = Attacher::AttachEngine3D
  Height = 20
  Placement = pos=(11.1,-26.79,-50) rot=(0,0,-1;1.1781rad)
  Radius = 1.5
FEATURE [Part::Cylinder] Cylinder1898  label="Válec1898"
  Angle = 360
  AttacherType = Attacher::AttachEngine3D
  Height = 20
  Placement = pos=(26.79,11.1,-50) rot=(0,0,1;0.392699rad)
  Radius = 1.5
FEATURE [Part::Cylinder] Cylinder1899  label="Válec1899"
  Angle = 360
  AttacherType = Attacher::AttachEngine3D
  Height = 20
  Placement = pos=(-11.1,26.79,-50) rot=(0,0,1;1.96349rad)
  Radius = 1.5
FEATURE [Part::Cylinder] Cylinder1900  label="Válec1900"
  Angle = 360
  AttacherType = Attacher::AttachEngine3D
  Height = 20
  Placement = pos=(-11.1,-26.79,-50) rot=(0,0,-1;1.96349rad)
  Radius = 1.5
FEATURE [Part::Cylinder] Cylinder1901  label="Válec1901"
  Angle = 360
  AttacherType = Attacher::AttachEngine3D
  Height = 20
  Placement = pos=(26.79,-11.1,-50) rot=(0,0,-1;0.392699rad)
  Radius = 1.5
FEATURE [Part::Cylinder] Cylinder1902  label="Válec1902"
  Angle = 360
  AttacherType = Attacher::AttachEngine3D
  Height = 20
  Placement = pos=(-26.79,11.1,-50) rot=(0,0,1;2.74889rad)
  Radius = 1.5
FEATURE [Part::Cylinder] Cylinder1903  label="Válec1903"
  Angle = 360
  AttacherType = Attacher::AttachEngine3D
  Height = 20
  Placement = pos=(-26.79,-11.1,-50) rot=(0,0,1;3.53429rad)
  Radius = 1.5
FEATURE [Part::Compound] Compound855
  Links = -> [Cylinder1898,Cylinder1896,Cylinder1899,Cylinder1902,Cylinder1903,Cylinder1900,Cylinder1897,Cylinder1901]
FEATURE [Part::Cut] Cut692
  Base = -> Tube012
  Placement = pos=(0,0,2) rot=(0,0,1;0rad)
  Tool = -> Compound855
FEATURE [Part::Cylinder] Cylinder1904  label="Válec1904"
  Angle = 360
  AttacherType = Attacher::AttachEngine3D
  Height = 3
  Placement = pos=(26.79,11.1,-50) rot=(0,0,1;0.392699rad)
  Radius = 3
FEATURE [Part::Cylinder] Cylinder1905  label="Válec1905"
  Angle = 360
  AttacherType = Attacher::AttachEngine3D
  Height = 3
  Placement = pos=(-11.1,26.79,-50) rot=(0,0,1;1.96349rad)
  Radius = 3
FEATURE [Part::Cylinder] Cylinder1906  label="Válec1906"
  Angle = 360
  AttacherType = Attacher::AttachEngine3D
  Height = 3
  Placement = pos=(11.1,-26.79,-50) rot=(0,0,-1;1.1781rad)
  Radius = 3
FEATURE [Part::Cylinder] Cylinder1907  label="Válec1907"
  Angle = 360
  AttacherType = Attacher::AttachEngine3D
  Height = 3
  Placement = pos=(11.1,26.79,-50) rot=(0,0,1;1.1781rad)
  Radius = 3
FEATURE [Part::Cylinder] Cylinder1908  label="Válec1908"
  Angle = 360
  AttacherType = Attacher::AttachEngine3D
  Height = 3
  Placement = pos=(-26.79,-11.1,-50) rot=(0,0,1;3.53429rad)
  Radius = 3
FEATURE [Part::Cylinder] Cylinder1296  label="Válec1296"
  Angle = 360
  AttacherType = Attacher::AttachEngine3D
  Height = 3
  Placement = pos=(-11.1,-26.79,-50) rot=(0,0,-1;1.96349rad)
  Radius = 3
FEATURE [Part::Cylinder] Cylinder1298  label="Válec1298"
  Angle = 360
  AttacherType = Attacher::AttachEngine3D
  Height = 3
  Placement = pos=(26.79,-11.1,-50) rot=(0,0,-1;0.392699rad)
  Radius = 3
FEATURE [Part::Cylinder] Cylinder1297  label="Válec1297"
  Angle = 360
  AttacherType = Attacher::AttachEngine3D
  Height = 3
  Placement = pos=(-26.79,11.1,-50) rot=(0,0,1;2.74889rad)
  Radius = 3
FEATURE [Part::Compound] Compound856
  Links = -> [Cylinder1904,Cylinder1907,Cylinder1905,Cylinder1297,Cylinder1908,Cylinder1296,Cylinder1906,Cylinder1298]
FEATURE [Part::Cut] Cut693  label="T-mini_washer"
  Base = -> Cut692
  Placement = pos=(0,1,1) rot=(0,0,1;0rad)
  Tool = -> Compound856
FEATURE [Part::FeaturePython] Tube049  # WARN: FeaturePython — macro-defined, semantics opaque (R4)
  AttacherType = Attacher::AttachEngine3D
  Height = 1
  InnerRadius = 8
  OuterRadius = 12
  Placement = pos=(0,0,-1) rot=(0,0,1;0rad)
FEATURE [Part::FeaturePython] Tube102  # WARN: FeaturePython — macro-defined, semantics opaque (R4)
  AttacherType = Attacher::AttachEngine3D
  Height = 7
  InnerRadius = 8
  OuterRadius = 9.9
  Placement = pos=(0,0,-8) rot=(0,0,1;0rad)
FEATURE [Part::Compound] Compound1073
  Links = -> [Tube049,Tube102]
  Placement = pos=(0,1,-43) rot=(0,0,1;0rad)
FEATURE [Part::FeaturePython] Tube103  label="ZKL-16006"  # WARN: FeaturePython — macro-defined, semantics opaque (R4)
  AttacherType = Attacher::AttachEngine3D
  Height = 9
  InnerRadius = 15
  OuterRadius = 27.5
  Placement = pos=(0,1,-54) rot=(0,0,1;0rad)
FEATURE [Part::FeaturePython] Tube104  label="ZKL-16005"  # WARN: FeaturePython — macro-defined, semantics opaque (R4)
  AttacherType = Attacher::AttachEngine3D
  Height = 8
  InnerRadius = 12.5
  OuterRadius = 23.5
  Placement = pos=(0,1,-54) rot=(0,0,1;0rad)
FEATURE [Part::FeaturePython] Tube105  label="ZKL-16004"  # WARN: FeaturePython — macro-defined, semantics opaque (R4)
  AttacherType = Attacher::AttachEngine3D
  Height = 8
  InnerRadius = 10
  OuterRadius = 21
  Placement = pos=(0,1,-52) rot=(0,0,1;0rad)
FEATURE [Part::Chamfer] Chamfer092
  Base = -> Compound1073
  Edges = 1 edges r=0.5: [Edge9]
FEATURE [Part::Box] Box525  label="Krychle525"
  AttacherType = Attacher::AttachEngine3D
  Height = 39
  Length = 44
  Placement = pos=(-22,-22,-116) rot=(0,0,1;0rad)
  Width = 44
FEATURE [Part::Box] Box524  label="Krychle524"
  AttacherType = Attacher::AttachEngine3D
  Height = 49
  Length = 32
  Placement = pos=(-16,-16,-126) rot=(0,0,1;0rad)
  Width = 32
FEATURE [Part::Cut] Cut503
  Base = -> Box525
  Tool = -> Box524
FEATURE [Part::Cylinder] Cylinder1364  label="Válec1364"
  Angle = 360
  AttacherType = Attacher::AttachEngine3D
  Height = 50
  Placement = pos=(22,-22,-126) rot=(0,0,1;0rad)
  Radius = 12
FEATURE [Part::Cylinder] Cylinder1367  label="Válec1367"
  Angle = 360
  AttacherType = Attacher::AttachEngine3D
  Height = 7
  Placement = pos=(0,-22,-98) rot=(1,0,0;1.5708rad)
  Radius = 11
FEATURE [Part::Cylinder] Cylinder1374  label="Válec1374"
  Angle = 360
  AttacherType = Attacher::AttachEngine3D
  Height = 20
  Placement = pos=(-19,7,-136) rot=(0,0,1;0rad)
  Radius = 1.5
FEATURE [Part::Box] Box531  label="Krychle531"
  AttacherType = Attacher::AttachEngine3D
  Height = 2
  Length = 6
  Placement = pos=(-22,4,-122) rot=(0,0,1;0rad)
  Width = 6
FEATURE [Part::Cylinder] Cylinder1376  label="Válec1376"
  Angle = 360
  AttacherType = Attacher::AttachEngine3D
  Height = 20
  Placement = pos=(10,-20,-112) rot=(1,0,0;1.5708rad)
  Radius = 1.5
FEATURE [Part::Box] Box528  label="Krychle528"
  AttacherType = Attacher::AttachEngine3D
  Height = 42
  Length = 26
  Placement = pos=(-13,-29,-116) rot=(0,0,1;0rad)
  Width = 7
FEATURE [Part::Cut] Cut506
  Base = -> Box528
  Tool = -> Cylinder1367
FEATURE [Part::Box] Box527  label="Krychle527"
  AttacherType = Attacher::AttachEngine3D
  Height = 39
  Length = 44
  Placement = pos=(-22,-22,-116) rot=(0,0,1;0rad)
  Width = 44
FEATURE [Part::Cylinder] Cylinder1365  label="Válec1365"
  Angle = 360
  AttacherType = Attacher::AttachEngine3D
  Height = 50
  Placement = pos=(-22,22,-126) rot=(0,0,1;0rad)
  Radius = 12
FEATURE [Part::Cylinder] Cylinder1363  label="Válec1363"
  Angle = 360
  AttacherType = Attacher::AttachEngine3D
  Height = 50
  Placement = pos=(22,22,-126) rot=(0,0,1;0rad)
  Radius = 12
FEATURE [Part::Cylinder] Cylinder1366  label="Válec1366"
  Angle = 360
  AttacherType = Attacher::AttachEngine3D
  Height = 50
  Placement = pos=(-22,-22,-126) rot=(0,0,1;0rad)
  Radius = 12
FEATURE [Part::Compound] Compound702
  Links = -> [Cylinder1366,Cylinder1364,Cylinder1365,Cylinder1363]
FEATURE [Part::Cut] Cut504
  Base = -> Cut503
  Tool = -> Compound702
FEATURE [Part::Cylinder] Cylinder1369  label="Válec1369"
  Angle = 360
  AttacherType = Attacher::AttachEngine3D
  Height = 20
  Placement = pos=(0,-22,-98) rot=(1,0,0;1.5708rad)
  Radius = 11
FEATURE [Part::Cut] Cut507
  Base = -> Cut504
  Tool = -> Cylinder1369
FEATURE [Part::Cylinder] Cylinder1370  label="Válec1370"
  Angle = 360
  AttacherType = Attacher::AttachEngine3D
  Height = 20
  Placement = pos=(0,-22,-98) rot=(1,0,0;1.5708rad)
  Radius = 11
FEATURE [Part::Cylinder] Cylinder1371  label="Válec1371"
  Angle = 360
  AttacherType = Attacher::AttachEngine3D
  Height = 20
  Placement = pos=(0,-10,-98) rot=(1,0,0;1.5708rad)
  Radius = 9.5
FEATURE [Part::Cut] Cut509
  Base = -> Cut507
  Tool = -> Cylinder1371
FEATURE [Part::Cylinder] Cylinder1372  label="Válec1372"
  Angle = 360
  AttacherType = Attacher::AttachEngine3D
  Height = 20
  Placement = pos=(19,7,-136) rot=(0,0,1;0rad)
  Radius = 1.5
FEATURE [Part::Box] Box529  label="Krychle529"
  AttacherType = Attacher::AttachEngine3D
  Height = 2
  Length = 6
  Placement = pos=(16,-10,-122) rot=(0,0,1;0rad)
  Width = 6
FEATURE [Part::Cylinder] Cylinder1373  label="Válec1373"
  Angle = 360
  AttacherType = Attacher::AttachEngine3D
  Height = 20
  Placement = pos=(19,-7,-136) rot=(0,0,1;0rad)
  Radius = 1.5
FEATURE [Part::Box] Box530  label="Krychle530"
  AttacherType = Attacher::AttachEngine3D
  Height = 2
  Length = 6
  Placement = pos=(16,4,-122) rot=(0,0,1;0rad)
  Width = 6
FEATURE [Part::Cylinder] Cylinder1375  label="Válec1375"
  Angle = 360
  AttacherType = Attacher::AttachEngine3D
  Height = 20
  Placement = pos=(-19,-7,-136) rot=(0,0,1;0rad)
  Radius = 1.5
FEATURE [Part::Compound] Compound704
  Links = -> [Cylinder1372,Cylinder1373,Cylinder1374,Cylinder1375]
  Placement = pos=(0,0,10) rot=(0,0,1;0rad)
FEATURE [Part::Cut] Cut510
  Base = -> Cut509
  Tool = -> Compound704
FEATURE [Part::Box] Box532  label="Krychle532"
  AttacherType = Attacher::AttachEngine3D
  Height = 2
  Length = 6
  Placement = pos=(-22,-10,-122) rot=(0,0,1;0rad)
  Width = 6
FEATURE [Part::Compound] Compound705
  Links = -> [Box529,Box530,Box531,Box532]
  Placement = pos=(0,0,10) rot=(0,0,1;0rad)
FEATURE [Part::Cut] Cut511
  Base = -> Cut510
  Tool = -> Compound705
FEATURE [Part::Cylinder] Cylinder1387  label="Válec1387"
  Angle = 360
  AttacherType = Attacher::AttachEngine3D
  Height = 20
  Placement = pos=(-10,-20,-88) rot=(1,0,0;1.5708rad)
  Radius = 1.5
FEATURE [Part::Cylinder] Cylinder1379  label="Válec1379"
  Angle = 360
  AttacherType = Attacher::AttachEngine3D
  Height = 20
  Placement = pos=(-10,-20,-88) rot=(1,0,0;1.5708rad)
  Radius = 1.5
FEATURE [Part::Cylinder] Cylinder1381  label="Válec1381"
  Angle = 360
  AttacherType = Attacher::AttachEngine3D
  Height = 20
  Placement = pos=(-10,-20,-112) rot=(1,0,0;1.5708rad)
  Radius = 1.5
FEATURE [Part::Cylinder] Cylinder1377  label="Válec1377"
  Angle = 360
  AttacherType = Attacher::AttachEngine3D
  Height = 20
  Placement = pos=(-10,-20,-112) rot=(1,0,0;1.5708rad)
  Radius = 1.5
FEATURE [Part::Box] Box533  label="Krychle533"
  AttacherType = Attacher::AttachEngine3D
  Height = 6
  Length = 6
  Placement = pos=(7,-24,-115) rot=(0,0,1;0rad)
  Width = 2
FEATURE [Part::Cylinder] Cylinder1378  label="Válec1378"
  Angle = 360
  AttacherType = Attacher::AttachEngine3D
  Height = 20
  Placement = pos=(10,-20,-88) rot=(1,0,0;1.5708rad)
  Radius = 1.5
FEATURE [Part::Compound] Compound707
  Links = -> [Cylinder1376,Cylinder1377,Cylinder1378,Cylinder1379]
  Placement = pos=(0,0,2) rot=(0,0,1;0rad)
FEATURE [Part::Cylinder] Cylinder1384  label="Válec1384"
  Angle = 360
  AttacherType = Attacher::AttachEngine3D
  Height = 20
  Placement = pos=(10,-20,-112) rot=(1,0,0;1.5708rad)
  Radius = 1.5
FEATURE [Part::Box] Box534  label="Krychle534"
  AttacherType = Attacher::AttachEngine3D
  Height = 6
  Length = 6
  Placement = pos=(7,-24,-91) rot=(0,0,1;0rad)
  Width = 2
FEATURE [Part::Box] Box535  label="Krychle535"
  AttacherType = Attacher::AttachEngine3D
  Height = 6
  Length = 6
  Placement = pos=(-13,-24,-91) rot=(0,0,1;0rad)
  Width = 2
FEATURE [Part::Cylinder] Cylinder1380  label="Válec1380"
  Angle = 360
  AttacherType = Attacher::AttachEngine3D
  Height = 20
  Placement = pos=(10,-20,-112) rot=(1,0,0;1.5708rad)
  Radius = 1.5
FEATURE [Part::Cylinder] Cylinder1382  label="Válec1382"
  Angle = 360
  AttacherType = Attacher::AttachEngine3D
  Height = 20
  Placement = pos=(10,-20,-88) rot=(1,0,0;1.5708rad)
  Radius = 1.5
FEATURE [Part::Cylinder] Cylinder1383  label="Válec1383"
  Angle = 360
  AttacherType = Attacher::AttachEngine3D
  Height = 20
  Placement = pos=(-10,-20,-88) rot=(1,0,0;1.5708rad)
  Radius = 1.5
FEATURE [Part::Compound] Compound708
  Links = -> [Cylinder1380,Cylinder1381,Cylinder1382,Cylinder1383]
  Placement = pos=(0,0,2) rot=(0,0,1;0rad)
FEATURE [Part::Cylinder] Cylinder1385  label="Válec1385"
  Angle = 360
  AttacherType = Attacher::AttachEngine3D
  Height = 20
  Placement = pos=(-10,-20,-112) rot=(1,0,0;1.5708rad)
  Radius = 1.5
FEATURE [Part::Box] Box536  label="Krychle536"
  AttacherType = Attacher::AttachEngine3D
  Height = 6
  Length = 6
  Placement = pos=(-13,-24,-115) rot=(0,0,1;0rad)
  Width = 2
FEATURE [Part::Compound] Compound706
  Links = -> [Box533,Box534,Box535,Box536]
  Placement = pos=(0,0,2) rot=(0,0,1;0rad)
FEATURE [Part::Cut] Cut512
  Base = -> Cut506
  Tool = -> Compound706
FEATURE [Part::Cylinder] Cylinder1386  label="Válec1386"
  Angle = 360
  AttacherType = Attacher::AttachEngine3D
  Height = 20
  Placement = pos=(10,-20,-88) rot=(1,0,0;1.5708rad)
  Radius = 1.5
FEATURE [Part::Compound] Compound709
  Links = -> [Cylinder1384,Cylinder1385,Cylinder1386,Cylinder1387]
  Placement = pos=(0,0,2) rot=(0,0,1;0rad)
FEATURE [Part::Cylinder] Cylinder1851  label="Válec1851"
  Angle = 360
  AttacherType = Attacher::AttachEngine3D
  Height = 10
  Placement = pos=(11.0978,-26.7925,-10) rot=(0,0,-1;1.1781rad)
  Radius = 1.5
FEATURE [Part::Cylinder] Cylinder1852  label="Válec1852"
  Angle = 360
  AttacherType = Attacher::AttachEngine3D
  Height = 10
  Placement = pos=(26.7925,11.0978,-10) rot=(0,0,1;0.392699rad)
  Radius = 1.5
FEATURE [Part::Cylinder] Cylinder1853  label="Válec1853"
  Angle = 360
  AttacherType = Attacher::AttachEngine3D
  Height = 10
  Placement = pos=(-26.7925,-11.0978,-10) rot=(0,0,1;3.53429rad)
  Radius = 1.5
FEATURE [Part::Cylinder] Cylinder1854  label="Válec1854"
  Angle = 360
  AttacherType = Attacher::AttachEngine3D
  Height = 10
  Placement = pos=(-11.0978,-26.7925,-10) rot=(0,0,-1;1.96349rad)
  Radius = 1.5
FEATURE [Part::Cylinder] Cylinder1855  label="Válec1855"
  Angle = 360
  AttacherType = Attacher::AttachEngine3D
  Height = 10
  Placement = pos=(11.0978,26.7925,-10) rot=(0,0,1;1.1781rad)
  Radius = 1.5
FEATURE [Part::Cylinder] Cylinder1856  label="Válec1856"
  Angle = 360
  AttacherType = Attacher::AttachEngine3D
  Height = 10
  Placement = pos=(-11.0978,26.7925,-10) rot=(0,0,1;1.96349rad)
  Radius = 1.5
FEATURE [Part::Cylinder] Cylinder1857  label="Válec1857"
  Angle = 360
  AttacherType = Attacher::AttachEngine3D
  Height = 10
  Placement = pos=(-26.7925,11.0978,-10) rot=(0,0,1;2.74889rad)
  Radius = 1.5
FEATURE [Part::Cylinder] Cylinder1858  label="Válec1858"
  Angle = 360
  AttacherType = Attacher::AttachEngine3D
  Height = 10
  Placement = pos=(26.7925,-11.0978,-10) rot=(0,0,-1;0.392699rad)
  Radius = 1.5
FEATURE [Part::Compound] Compound852
  Links = -> [Cylinder1852,Cylinder1855,Cylinder1856,Cylinder1857,Cylinder1853,Cylinder1854,Cylinder1851,Cylinder1858]
  Placement = pos=(0,0,-70) rot=(0,0,1;0rad)
FEATURE [Part::FeaturePython] Tube059  # WARN: FeaturePython — macro-defined, semantics opaque (R4)
  AttacherType = Attacher::AttachEngine3D
  Height = 9
  InnerRadius = 16.1
  OuterRadius = 20
  Placement = pos=(0,0,-87) rot=(0,0,1;0rad)
FEATURE [Part::Compound] Compound851  label="turno_bednicka_mikro1"
  Links = -> [Tube059]
FEATURE [Part::FeaturePython] Tube060  # WARN: FeaturePython — macro-defined, semantics opaque (R4)
  AttacherType = Attacher::AttachEngine3D
  Height = 49
  InnerRadius = 9
  OuterRadius = 12
  Placement = pos=(-22,-22,-126) rot=(0,0,1;0rad)
FEATURE [Part::FeaturePython] Tube061  # WARN: FeaturePython — macro-defined, semantics opaque (R4)
  AttacherType = Attacher::AttachEngine3D
  Height = 49
  InnerRadius = 9
  OuterRadius = 12
  Placement = pos=(-22,22,-126) rot=(0,0,1;0rad)
FEATURE [Part::FeaturePython] Tube062  # WARN: FeaturePython — macro-defined, semantics opaque (R4)
  AttacherType = Attacher::AttachEngine3D
  Height = 49
  InnerRadius = 9
  OuterRadius = 12
  Placement = pos=(22,-22,-126) rot=(0,0,1;0rad)
FEATURE [Part::FeaturePython] Tube063  # WARN: FeaturePython — macro-defined, semantics opaque (R4)
  AttacherType = Attacher::AttachEngine3D
  Height = 49
  InnerRadius = 9
  OuterRadius = 12
  Placement = pos=(22,22,-126) rot=(0,0,1;0rad)
FEATURE [Part::Compound] Compound703
  Links = -> [Tube060,Tube062,Tube061,Tube063]
FEATURE [Part::Common] Common002
  Base = -> Compound703
  Tool = -> Box527
FEATURE [Part::Cut] Cut508
  Base = -> Common002
  Tool = -> Cylinder1370
FEATURE [Part::Cut] Cut514
  Base = -> Cut508
  Tool = -> Compound709
FEATURE [Part::FeaturePython] Tube064  # WARN: FeaturePython — macro-defined, semantics opaque (R4)
  AttacherType = Attacher::AttachEngine3D
  Height = 3
  InnerRadius = 11.5
  OuterRadius = 32
  Placement = pos=(0,0,-77) rot=(0,0,1;0rad)
FEATURE [Part::Cut] Cut513
  Base = -> Cut512
  Tool = -> Compound707
FEATURE [Part::Cut] Cut515
  Base = -> Cut511
  Tool = -> Compound708
FEATURE [Part::Cut] Cut669
  Base = -> Tube064
  Tool = -> Compound852
FEATURE [Part::Compound] Compound853  label="turno_mikro_bednicka_zmensena1"
  Links = -> [Cut669,Cut515,Cut513,Cut514]
FEATURE [Part::Chamfer] Chamfer093
  Base = -> Compound853
  Edges = 4 edges r=2: [Edge336,Edge340,Edge349,Edge353]
FEATURE [Part::Chamfer] Chamfer006  label="turno_mikro_bednicka_zmensena002"
  Base = -> Chamfer093
  Edges = 2 edges r=2: [Edge323,Edge365]
FEATURE [Part::Compound] Compound854  label="T-mini_box"
  Links = -> [Compound851,Chamfer006]
  Placement = pos=(0,1,30) rot=(0,0,1;0rad)
FEATURE [Part::Compound] Compound1074  label="L-elb_encoder-sidehold"
  Links = -> [Cut863,Compound1047]
FEATURE [Part::Chamfer] Chamfer094  label="L-elb_encoder-uphold-old"
  Base = -> Compound
  Edges = 2 edges r=2: [Edge18,Edge45]
FEATURE [Part::Box] Box960  label="Krychle959"
  AttacherType = Attacher::AttachEngine3D
  Height = 15
  Length = 15
  Placement = pos=(19,-174,-65) rot=(0,0,1;0rad)
  Width = 130
FEATURE [Part::Box] Box961  label="Krychle960"
  AttacherType = Attacher::AttachEngine3D
  Height = 18
  Length = 27
  Placement = pos=(-13.5,-66,-7) rot=(0,0,1;0rad)
  Width = 24
FEATURE [Part::Box] Box962  label="Krychle961"
  AttacherType = Attacher::AttachEngine3D
  Height = 15
  Length = 15
  Placement = pos=(-7.5,-174,-4) rot=(0,0,1;0rad)
  Width = 130
FEATURE [Part::Cut] Cut891
  Base = -> Box961
  Tool = -> Box962
FEATURE [Part::Box] Box963  label="Krychle962"
  AttacherType = Attacher::AttachEngine3D
  Height = 18
  Length = 27
  Placement = pos=(-40,-66,-50) rot=(0,0,1;0rad)
  Width = 28
FEATURE [Part::Box] Box964  label="Krychle963"
  AttacherType = Attacher::AttachEngine3D
  Height = 18
  Length = 27
  Placement = pos=(13,-66,-50) rot=(0,0,1;0rad)
  Width = 28
FEATURE [Part::Box] Box965  label="Krychle964"
  AttacherType = Attacher::AttachEngine3D
  Height = 15
  Length = 15
  Placement = pos=(-34,-174,-65) rot=(0,0,1;0rad)
  Width = 130
FEATURE [Part::Compound] Compound1081
  Links = -> [Box965,Box960]
  Placement = pos=(0,0,15) rot=(0,0,1;0rad)
FEATURE [Part::Box] Box966  label="Krychle965"
  AttacherType = Attacher::AttachEngine3D
  Height = 15
  Length = 15
  Placement = pos=(19,-174,-65) rot=(0,0,1;0rad)
  Width = 130
FEATURE [Part::Box] Box967  label="Krychle966"
  AttacherType = Attacher::AttachEngine3D
  Height = 15
  Length = 15
  Placement = pos=(-34,-174,-65) rot=(0,0,1;0rad)
  Width = 130
FEATURE [Part::Compound] Compound1083
  Links = -> [Box967,Box966]
  Placement = pos=(0,0,15) rot=(0,0,1;0rad)
FEATURE [Part::Cylinder] Cylinder2445  label="Válec2431"
  Angle = 360
  AttacherType = Attacher::AttachEngine3D
  Height = 20
  Placement = pos=(-16,-60,-60) rot=(0,0,1;0rad)
  Radius = 1.5
FEATURE [Part::Cylinder] Cylinder2446  label="Válec2432"
  Angle = 360
  AttacherType = Attacher::AttachEngine3D
  Height = 20
  Placement = pos=(-16,-48,-60) rot=(0,0,1;0rad)
  Radius = 1.5
FEATURE [Part::Cylinder] Cylinder2447  label="Válec2433"
  Angle = 360
  AttacherType = Attacher::AttachEngine3D
  Height = 20
  Placement = pos=(-37,-48,-60) rot=(0,0,1;0rad)
  Radius = 1.5
FEATURE [Part::Cylinder] Cylinder2448  label="Válec2434"
  Angle = 360
  AttacherType = Attacher::AttachEngine3D
  Height = 20
  Placement = pos=(-37,-60,-60) rot=(0,0,1;0rad)
  Radius = 1.5
FEATURE [Part::Compound] Compound1076
  Links = -> [Cylinder2446,Cylinder2445,Cylinder2447,Cylinder2448]
FEATURE [Part::Box] Box968  label="Krychle967"
  AttacherType = Attacher::AttachEngine3D
  Height = 2
  Length = 6
  Placement = pos=(-19,-51,-46) rot=(0,0,1;0rad)
  Width = 6
FEATURE [Part::Box] Box969  label="Krychle968"
  AttacherType = Attacher::AttachEngine3D
  Height = 2
  Length = 6
  Placement = pos=(-40,-51,-46) rot=(0,0,1;0rad)
  Width = 6
FEATURE [Part::Box] Box970  label="Krychle969"
  AttacherType = Attacher::AttachEngine3D
  Height = 2
  Length = 6
  Placement = pos=(-40,-63,-46) rot=(0,0,1;0rad)
  Width = 6
FEATURE [Part::Box] Box971  label="Krychle970"
  AttacherType = Attacher::AttachEngine3D
  Height = 2
  Length = 6
  Placement = pos=(-40,-51,-46) rot=(0,0,1;0rad)
  Width = 6
FEATURE [Part::Box] Box972  label="Krychle971"
  AttacherType = Attacher::AttachEngine3D
  Height = 2
  Length = 6
  Placement = pos=(-19,-51,-46) rot=(0,0,1;0rad)
  Width = 6
FEATURE [Part::Box] Box973  label="Krychle972"
  AttacherType = Attacher::AttachEngine3D
  Height = 2
  Length = 6
  Placement = pos=(-40,-63,-46) rot=(0,0,1;0rad)
  Width = 6
FEATURE [Part::Box] Box974  label="Krychle973"
  AttacherType = Attacher::AttachEngine3D
  Height = 2
  Length = 6
  Placement = pos=(-40,-51,-46) rot=(0,0,1;0rad)
  Width = 6
FEATURE [Part::Cylinder] Cylinder2449  label="Válec2435"
  Angle = 360
  AttacherType = Attacher::AttachEngine3D
  Height = 20
  Placement = pos=(-16,-60,-60) rot=(0,0,1;0rad)
  Radius = 1.5
FEATURE [Part::Cylinder] Cylinder2450  label="Válec2436"
  Angle = 360
  AttacherType = Attacher::AttachEngine3D
  Height = 20
  Placement = pos=(-37,-48,-60) rot=(0,0,1;0rad)
  Radius = 1.5
FEATURE [Part::Cylinder] Cylinder2451  label="Válec2437"
  Angle = 360
  AttacherType = Attacher::AttachEngine3D
  Height = 20
  Placement = pos=(-16,-55,-60) rot=(0,0,1;0rad)
  Radius = 1.5
FEATURE [Part::Box] Box976  label="Krychle975"
  AttacherType = Attacher::AttachEngine3D
  Height = 2
  Length = 6
  Placement = pos=(-40,-63,-46) rot=(0,0,1;0rad)
  Width = 6
FEATURE [Part::Cylinder] Cylinder2452  label="Válec2438"
  Angle = 360
  AttacherType = Attacher::AttachEngine3D
  Height = 20
  Placement = pos=(-37,-60,-60) rot=(0,0,1;0rad)
  Radius = 1.5
FEATURE [Part::Cylinder] Cylinder2453  label="Válec2439"
  Angle = 360
  AttacherType = Attacher::AttachEngine3D
  Height = 20
  Placement = pos=(-16,-48,-60) rot=(0,0,1;0rad)
  Radius = 1.5
FEATURE [Part::Compound] Compound1075
  Links = -> [Cylinder2453,Cylinder2449,Cylinder2450,Cylinder2452]
  Placement = pos=(53,0,0) rot=(0,0,1;0rad)
FEATURE [Part::Box] Box977  label="Krychle976"
  AttacherType = Attacher::AttachEngine3D
  Height = 2
  Length = 6
  Placement = pos=(-19,-63,-46) rot=(0,0,1;0rad)
  Width = 6
FEATURE [Part::Compound] Compound1082
  Links = -> [Box968,Box977,Box971,Box976]
FEATURE [Part::Box] Box978  label="Krychle977"
  AttacherType = Attacher::AttachEngine3D
  Height = 2
  Length = 6
  Placement = pos=(-19,-63,-46) rot=(0,0,1;0rad)
  Width = 6
FEATURE [Part::Compound] Compound1084
  Links = -> [Box972,Box978,Box969,Box973]
  Placement = pos=(53,0,0) rot=(0,0,1;0rad)
FEATURE [Part::Box] Box979  label="Krychle978"
  AttacherType = Attacher::AttachEngine3D
  Height = 2
  Length = 6
  Placement = pos=(-19,-58,-46) rot=(0,0,1;0rad)
  Width = 6
FEATURE [Part::Compound] Compound1078
  Links = -> [Box979,Box974,Box970]
  Placement = pos=(-26.5,0,-39) rot=(0,1,0;3.14159rad)
FEATURE [Part::Cylinder] Cylinder2455  label="Válec2441"
  Angle = 360
  AttacherType = Attacher::AttachEngine3D
  Height = 20
  Placement = pos=(-37,-60,-60) rot=(0,0,1;0rad)
  Radius = 1.5
FEATURE [Part::Cylinder] Cylinder2456  label="Válec2442"
  Angle = 360
  AttacherType = Attacher::AttachEngine3D
  Height = 20
  Placement = pos=(-37,-48,-60) rot=(0,0,1;0rad)
  Radius = 1.5
FEATURE [Part::Compound] Compound1079
  Links = -> [Cylinder2451,Cylinder2456,Cylinder2455]
  Placement = pos=(-26.5,0,-39) rot=(0,1,0;3.14159rad)
FEATURE [Part::Box] Box980  label="Krychle979"
  AttacherType = Attacher::AttachEngine3D
  Height = 18
  Length = 27
  Placement = pos=(-13.5,-66,-7) rot=(0,0,1;0rad)
  Width = 24
FEATURE [Part::Box] Box981  label="Krychle980"
  AttacherType = Attacher::AttachEngine3D
  Height = 2
  Length = 6
  Placement = pos=(-19,-51,-46) rot=(0,0,1;0rad)
  Width = 6
FEATURE [Part::Box] Box982  label="Krychle981"
  AttacherType = Attacher::AttachEngine3D
  Height = 15
  Length = 15
  Placement = pos=(-7.5,-174,-4) rot=(0,0,1;0rad)
  Width = 130
FEATURE [Part::Box] Box984  label="Krychle983"
  AttacherType = Attacher::AttachEngine3D
  Height = 2
  Length = 6
  Placement = pos=(-19,-63,-46) rot=(0,0,1;0rad)
  Width = 6
FEATURE [Part::Cut] Cut892
  Base = -> Box980
  Tool = -> Box982
FEATURE [Part::Cut] Cut898
  Base = -> Cut891
  Tool = -> Compound1078
FEATURE [Part::Cut] Cut894
  Base = -> Cut898
  Placement = pos=(26.5,-4,-1) rot=(0,0,1;0rad)
  Tool = -> Compound1079
FEATURE [Part::Cut] Cut900
  Base = -> Box963
  Tool = -> Compound1083
FEATURE [Part::Cut] Cut901
  Base = -> Box964
  Tool = -> Compound1081
FEATURE [Part::Cut] Cut902
  Base = -> Cut900
  Tool = -> Compound1082
FEATURE [Part::Cut] Cut903
  Base = -> Cut901
  Tool = -> Compound1084
FEATURE [Part::Cut] Cut895
  Base = -> Cut903
  Placement = pos=(8,-4,10) rot=(0,0,1;0rad)
  Tool = -> Compound1075
FEATURE [Part::Cut] Cut904
  Base = -> Cut902
  Placement = pos=(-8,-4,10) rot=(0,0,1;0rad)
  Tool = -> Compound1076
FEATURE [Part::Cylinder] Cylinder2458  label="Válec2444"
  Angle = 360
  AttacherType = Attacher::AttachEngine3D
  Height = 30
  Placement = pos=(26,-37,7) rot=(0,1,0;1.5708rad)
  Radius = 3
FEATURE [Part::Cylinder] Cylinder2459  label="Válec2445"
  Angle = 360
  AttacherType = Attacher::AttachEngine3D
  Height = 20
  Placement = pos=(-16,-60,-60) rot=(0,0,1;0rad)
  Radius = 1.5
FEATURE [Part::Cylinder] Cylinder2460  label="Válec2446"
  Angle = 360
  AttacherType = Attacher::AttachEngine3D
  Height = 20
  Placement = pos=(28,-8,-3) rot=(0,1,0;1.5708rad)
  Radius = 1.5
FEATURE [Part::Cylinder] Cylinder2461  label="Válec2447"
  Angle = 360
  AttacherType = Attacher::AttachEngine3D
  Height = 20
  Placement = pos=(26,-37,7) rot=(0,1,0;1.5708rad)
  Radius = 1.5
FEATURE [Part::Cylinder] Cylinder2462  label="Válec2448"
  Angle = 360
  AttacherType = Attacher::AttachEngine3D
  Height = 20
  Placement = pos=(-37,-55,-60) rot=(0,0,1;0rad)
  Radius = 1.5
FEATURE [Part::Cylinder] Cylinder2463  label="Válec2449"
  Angle = 360
  AttacherType = Attacher::AttachEngine3D
  Height = 20
  Placement = pos=(28,8,-3) rot=(0,1,0;1.5708rad)
  Radius = 1.5
FEATURE [Part::Cylinder] Cylinder2464  label="Válec2450"
  Angle = 360
  AttacherType = Attacher::AttachEngine3D
  Height = 20
  Placement = pos=(26,37,7) rot=(0,1,0;1.5708rad)
  Radius = 1.5
FEATURE [Part::Cylinder] Cylinder2465  label="Válec2451"
  Angle = 360
  AttacherType = Attacher::AttachEngine3D
  Height = 30
  Placement = pos=(26,37,7) rot=(0,1,0;1.5708rad)
  Radius = 3
FEATURE [Part::Cylinder] Cylinder2466  label="Válec2452"
  Angle = 360
  AttacherType = Attacher::AttachEngine3D
  Height = 20
  Placement = pos=(-16,-48,-60) rot=(0,0,1;0rad)
  Radius = 1.5
FEATURE [Part::Compound] Compound1085
  Links = -> [Cylinder2466,Cylinder2459,Cylinder2462]
  Placement = pos=(-26.5,0,-39) rot=(0,1,0;3.14159rad)
FEATURE [Part::Box] Box985  label="Krychle984"
  AttacherType = Attacher::AttachEngine3D
  Height = 2
  Length = 6
  Placement = pos=(-40,-58,-46) rot=(0,0,1;0rad)
  Width = 6
FEATURE [Part::Compound] Compound1077
  Links = -> [Box984,Box981,Box985]
  Placement = pos=(-26.5,0,-39) rot=(0,1,0;3.14159rad)
FEATURE [Part::Cut] Cut893
  Base = -> Cut892
  Tool = -> Compound1077
FEATURE [Part::Cut] Cut899
  Base = -> Cut893
  Placement = pos=(-26.5,-4,-1) rot=(0,0,1;0rad)
  Tool = -> Compound1085
FEATURE [Part::Compound] Compound1080  label="xori_drzaky001"
  Links = -> [Cut904,Cut895,Cut894,Cut899]
FEATURE [Part::Compound] Compound1086
  Links = -> [Cylinder2461,Cylinder2463,Cylinder2464,Cylinder2460]
  Placement = pos=(0,-80,-34) rot=(0,0,1;1.5708rad)
FEATURE [Part::Compound] Compound1087
  Links = -> [Cylinder2458,Cylinder2465]
  Placement = pos=(0,-101,-34) rot=(0,0,1;1.5708rad)
FEATURE [Part::Cut] Cut896
  Base = -> Compound1080
  Tool = -> Compound1087
FEATURE [Part::Cut] Cut897
  Base = -> Cut896
  Tool = -> Compound1086
FEATURE [Part::Cylinder] Cylinder2467  label="L-elb_pulley-GT2-16-A011"
  Angle = 360
  AttacherType = Attacher::AttachEngine3D
  Height = 36
  Placement = pos=(-9,-45,-6) rot=(0,0,1;0.523599rad)
  Radius = 1.5
FEATURE [Part::Cylinder] Cylinder2468  label="L-elb_pulley-GT2-16-B005"
  Angle = 360
  AttacherType = Attacher::AttachEngine3D
  Height = 36
  Placement = pos=(9,-45,-6) rot=(0,0,1;0.523599rad)
  Radius = 1.5
FEATURE [Part::Cylinder] Cylinder2469  label="L-elb_pulley-GT2-16-A012"
  Angle = 360
  AttacherType = Attacher::AttachEngine3D
  Height = 20
  Placement = pos=(-21,-45,-8) rot=(0,0,1;0.523599rad)
  Radius = 1.5
FEATURE [Part::Cylinder] Cylinder2470  label="L-elb_pulley-GT2-16-A013"
  Angle = 360
  AttacherType = Attacher::AttachEngine3D
  Height = 20
  Placement = pos=(21,-45,-8) rot=(0,0,1;0.523599rad)
  Radius = 1.5
FEATURE [Part::Compound] Compound1089
  Links = -> [Cylinder2469,Cylinder2470]
FEATURE [Part::Cylinder] Cylinder2471  label="L-elb_pulley-GT2-16-A014"
  Angle = 360
  AttacherType = Attacher::AttachEngine3D
  Height = 13
  Placement = pos=(-8,-45,-9) rot=(0,0,1;0.523599rad)
  Radius = 9
FEATURE [Part::Cylinder] Cylinder2472  label="L-elb_pulley-GT2-16-B006"
  Angle = 360
  AttacherType = Attacher::AttachEngine3D
  Height = 13
  Placement = pos=(8,-45,-9) rot=(0,0,1;0.523599rad)
  Radius = 9
FEATURE [Part::Compound] Compound1090
  Links = -> [Cylinder2471,Cylinder2472]
FEATURE [Part::Cut] Cut905
  Base = -> Cut897
  Tool = -> Compound1090
FEATURE [Part::Box] Box987  label="Krychle986"
  AttacherType = Attacher::AttachEngine3D
  Height = 6
  Length = 52
  Placement = pos=(-26,-48,4) rot=(0,0,1;0rad)
  Width = 6
FEATURE [Part::Cut] Cut906
  Base = -> Cut905
  Tool = -> Box987
FEATURE [Part::Cut] Cut907
  Base = -> Cut906
  Tool = -> Compound1089
FEATURE [Part::Box] Box988  label="Krychle987"
  AttacherType = Attacher::AttachEngine3D
  Height = 2
  Length = 6
  Placement = pos=(-24,-48,-2) rot=(0,0,1;0rad)
  Width = 6
FEATURE [Part::Box] Box989  label="Krychle988"
  AttacherType = Attacher::AttachEngine3D
  Height = 2
  Length = 6
  Placement = pos=(18,-48,-2) rot=(0,0,1;0rad)
  Width = 6
FEATURE [Part::Compound] Compound1091
  Links = -> [Box988,Box989]
FEATURE [Part::Cut] Cut908
  Base = -> Cut907
  Tool = -> Compound1091
FEATURE [Part::Cylinder] Cylinder2473  label="L-elb_pulley-GT2-16-A015"
  Angle = 360
  AttacherType = Attacher::AttachEngine3D
  Height = 13
  Placement = pos=(-8,-45,-9) rot=(0,0,1;0.523599rad)
  Radius = 9
FEATURE [Part::Cylinder] Cylinder2474  label="L-elb_pulley-GT2-16-B007"
  Angle = 360
  AttacherType = Attacher::AttachEngine3D
  Height = 13
  Placement = pos=(8,-45,-9) rot=(0,0,1;0.523599rad)
  Radius = 9
FEATURE [Part::Compound] Compound1092
  Links = -> [Cylinder2473,Cylinder2474]
  Placement = pos=(0,0,6) rot=(0,0,1;0rad)
FEATURE [Part::Chamfer] Chamfer095
  Base = -> Cut908
  Edges = 2 edges r=5.9: [Edge227,Edge405]
FEATURE [Part::Cut] Cut909
  Base = -> Chamfer095
  Tool = -> Compound1092
FEATURE [Part::Chamfer] Chamfer096
  Base = -> Cut909
  Edges = 2 edges r=2: [Edge134,Edge161]
FEATURE [Part::Chamfer] Chamfer097
  Base = -> Chamfer096
  Edges = 2 edges r=2: [Edge137,Edge162]
FEATURE [Part::Chamfer] Chamfer098
  Base = -> Chamfer097
  Edges = 2 edges r=2: [Edge269,Edge288]
FEATURE [Part::Chamfer] Chamfer099
  Base = -> Chamfer098
  Edges = 2 edges r=2: [Edge383,Edge402]
FEATURE [Part::Chamfer] Chamfer100
  Base = -> Chamfer099
  Edges = 2 edges r=4: [Edge21,Edge117]
FEATURE [Part::Compound] Compound1088
  Links = -> [Cylinder2467,Cylinder2468,Chamfer100]
  Placement = pos=(0,0,-16) rot=(0,0,1;0rad)
FEATURE [Part::Cylinder] Cylinder2475  label="Válec2453"
  Angle = 360
  AttacherType = Attacher::AttachEngine3D
  Height = 20
  Placement = pos=(-37,-60,-60) rot=(0,0,1;0rad)
  Radius = 1.5
FEATURE [Part::Box] Box990  label="Krychle989"
  AttacherType = Attacher::AttachEngine3D
  Height = 2
  Length = 6
  Placement = pos=(-40,-51,-46) rot=(0,0,1;0rad)
  Width = 6
FEATURE [Part::Box] Box991  label="Krychle990"
  AttacherType = Attacher::AttachEngine3D
  Height = 18
  Length = 27
  Placement = pos=(-40,-66,-50) rot=(0,0,1;0rad)
  Width = 28
FEATURE [Part::Box] Box992  label="Krychle991"
  AttacherType = Attacher::AttachEngine3D
  Height = 2
  Length = 6
  Placement = pos=(-19,-51,-46) rot=(0,0,1;0rad)
  Width = 6
FEATURE [Part::Box] Box993  label="Krychle992"
  AttacherType = Attacher::AttachEngine3D
  Height = 2
  Length = 6
  Placement = pos=(-40,-51,-46) rot=(0,0,1;0rad)
  Width = 6
FEATURE [Part::Cylinder] Cylinder2476  label="Válec2454"
  Angle = 360
  AttacherType = Attacher::AttachEngine3D
  Height = 20
  Placement = pos=(-37,-48,-60) rot=(0,0,1;0rad)
  Radius = 1.5
FEATURE [Part::Box] Box994  label="Krychle993"
  AttacherType = Attacher::AttachEngine3D
  Height = 18
  Length = 27
  Placement = pos=(-13.5,-66,-7) rot=(0,0,1;0rad)
  Width = 24
FEATURE [Part::Box] Box995  label="Krychle994"
  AttacherType = Attacher::AttachEngine3D
  Height = 15
  Length = 15
  Placement = pos=(-7.5,-174,-4) rot=(0,0,1;0rad)
  Width = 130
FEATURE [Part::Cut] Cut910
  Base = -> Box994
  Tool = -> Box995
FEATURE [Part::Box] Box996  label="Krychle995"
  AttacherType = Attacher::AttachEngine3D
  Height = 15
  Length = 15
  Placement = pos=(19,-174,-65) rot=(0,0,1;0rad)
  Width = 130
FEATURE [Part::Box] Box997  label="Krychle996"
  AttacherType = Attacher::AttachEngine3D
  Height = 18
  Length = 27
  Placement = pos=(13,-66,-50) rot=(0,0,1;0rad)
  Width = 28
FEATURE [Part::Box] Box998  label="Krychle997"
  AttacherType = Attacher::AttachEngine3D
  Height = 15
  Length = 15
  Placement = pos=(19,-174,-65) rot=(0,0,1;0rad)
  Width = 130
FEATURE [Part::Cylinder] Cylinder2477  label="Válec2455"
  Angle = 360
  AttacherType = Attacher::AttachEngine3D
  Height = 20
  Placement = pos=(-16,-48,-60) rot=(0,0,1;0rad)
  Radius = 1.5
FEATURE [Part::Box] Box999  label="Krychle998"
  AttacherType = Attacher::AttachEngine3D
  Height = 15
  Length = 15
  Placement = pos=(-34,-174,-65) rot=(0,0,1;0rad)
  Width = 130
FEATURE [Part::Box] Box1000  label="Krychle999"
  AttacherType = Attacher::AttachEngine3D
  Height = 15
  Length = 15
  Placement = pos=(-34,-174,-65) rot=(0,0,1;0rad)
  Width = 130
FEATURE [Part::Cylinder] Cylinder2478  label="Válec2456"
  Angle = 360
  AttacherType = Attacher::AttachEngine3D
  Height = 20
  Placement = pos=(-16,-60,-60) rot=(0,0,1;0rad)
  Radius = 1.5
FEATURE [Part::Cylinder] Cylinder2479  label="Válec2457"
  Angle = 360
  AttacherType = Attacher::AttachEngine3D
  Height = 20
  Placement = pos=(-37,-48,-60) rot=(0,0,1;0rad)
  Radius = 1.5
FEATURE [Part::Box] Box1001  label="Krychle1000"
  AttacherType = Attacher::AttachEngine3D
  Height = 2
  Length = 6
  Placement = pos=(-19,-51,-46) rot=(0,0,1;0rad)
  Width = 6
FEATURE [Part::Box] Box1002  label="Krychle1001"
  AttacherType = Attacher::AttachEngine3D
  Height = 2
  Length = 6
  Placement = pos=(-40,-63,-46) rot=(0,0,1;0rad)
  Width = 6
FEATURE [Part::Box] Box1003  label="Krychle1002"
  AttacherType = Attacher::AttachEngine3D
  Height = 2
  Length = 6
  Placement = pos=(-40,-51,-46) rot=(0,0,1;0rad)
  Width = 6
FEATURE [Part::Box] Box1004  label="Krychle1003"
  AttacherType = Attacher::AttachEngine3D
  Height = 2
  Length = 6
  Placement = pos=(-40,-63,-46) rot=(0,0,1;0rad)
  Width = 6
FEATURE [Part::Cylinder] Cylinder2480  label="Válec2458"
  Angle = 360
  AttacherType = Attacher::AttachEngine3D
  Height = 20
  Placement = pos=(-16,-60,-60) rot=(0,0,1;0rad)
  Radius = 1.5
FEATURE [Part::Box] Box1005  label="Krychle1004"
  AttacherType = Attacher::AttachEngine3D
  Height = 2
  Length = 6
  Placement = pos=(-19,-63,-46) rot=(0,0,1;0rad)
  Width = 6
FEATURE [Part::Cylinder] Cylinder2481  label="Válec2459"
  Angle = 360
  AttacherType = Attacher::AttachEngine3D
  Height = 20
  Placement = pos=(-16,-60,-60) rot=(0,0,1;0rad)
  Radius = 1.5
FEATURE [Part::Box] Box1006  label="Krychle1005"
  AttacherType = Attacher::AttachEngine3D
  Height = 2
  Length = 6
  Placement = pos=(-40,-63,-46) rot=(0,0,1;0rad)
  Width = 6
FEATURE [Part::Cylinder] Cylinder2482  label="Válec2460"
  Angle = 360
  AttacherType = Attacher::AttachEngine3D
  Height = 20
  Placement = pos=(-37,-60,-60) rot=(0,0,1;0rad)
  Radius = 1.5
FEATURE [Part::Cylinder] Cylinder2483  label="Válec2461"
  Angle = 360
  AttacherType = Attacher::AttachEngine3D
  Height = 20
  Placement = pos=(26,37,7) rot=(0,1,0;1.5708rad)
  Radius = 1.5
FEATURE [Part::Box] Box1007  label="Krychle1006"
  AttacherType = Attacher::AttachEngine3D
  Height = 2
  Length = 6
  Placement = pos=(-19,-63,-46) rot=(0,0,1;0rad)
  Width = 6
FEATURE [Part::Cylinder] Cylinder2484  label="Válec2462"
  Angle = 360
  AttacherType = Attacher::AttachEngine3D
  Height = 20
  Placement = pos=(-37,-48,-60) rot=(0,0,1;0rad)
  Radius = 1.5
FEATURE [Part::Cylinder] Cylinder2485  label="Válec2463"
  Angle = 360
  AttacherType = Attacher::AttachEngine3D
  Height = 20
  Placement = pos=(-37,-60,-60) rot=(0,0,1;0rad)
  Radius = 1.5
FEATURE [Part::Cylinder] Cylinder2486  label="Válec2464"
  Angle = 360
  AttacherType = Attacher::AttachEngine3D
  Height = 20
  Placement = pos=(-16,-55,-54) rot=(0,0,1;0rad)
  Radius = 1.5
FEATURE [Part::Box] Box1008  label="Krychle1007"
  AttacherType = Attacher::AttachEngine3D
  Height = 2
  Length = 6
  Placement = pos=(-19,-58,-40) rot=(0,0,1;0rad)
  Width = 6
FEATURE [Part::Box] Box1009  label="Krychle1008"
  AttacherType = Attacher::AttachEngine3D
  Height = 18
  Length = 27
  Placement = pos=(-13.5,-66,-7) rot=(0,0,1;0rad)
  Width = 24
FEATURE [Part::Box] Box1010  label="Krychle1009"
  AttacherType = Attacher::AttachEngine3D
  Height = 2
  Length = 6
  Placement = pos=(-19,-63,-46) rot=(0,0,1;0rad)
  Width = 6
FEATURE [Part::Cylinder] Cylinder2487  label="Válec2465"
  Angle = 360
  AttacherType = Attacher::AttachEngine3D
  Height = 20
  Placement = pos=(-16,-48,-60) rot=(0,0,1;0rad)
  Radius = 1.5
FEATURE [Part::Box] Box1011  label="Krychle1010"
  AttacherType = Attacher::AttachEngine3D
  Height = 2
  Length = 6
  Placement = pos=(-19,-51,-46) rot=(0,0,1;0rad)
  Width = 6
FEATURE [Part::Box] Box1012  label="Krychle1011"
  AttacherType = Attacher::AttachEngine3D
  Height = 15
  Length = 15
  Placement = pos=(-7.5,-174,-4) rot=(0,0,1;0rad)
  Width = 130
FEATURE [Part::Cut] Cut911
  Base = -> Box1009
  Tool = -> Box1012
FEATURE [Part::Cylinder] Cylinder2488  label="Válec2466"
  Angle = 360
  AttacherType = Attacher::AttachEngine3D
  Height = 30
  Placement = pos=(26,-37,7) rot=(0,1,0;1.5708rad)
  Radius = 3
FEATURE [Part::Cylinder] Cylinder2489  label="Válec2467"
  Angle = 360
  AttacherType = Attacher::AttachEngine3D
  Height = 20
  Placement = pos=(26,-37,7) rot=(0,1,0;1.5708rad)
  Radius = 1.5
FEATURE [Part::Cylinder] Cylinder2490  label="Válec2468"
  Angle = 360
  AttacherType = Attacher::AttachEngine3D
  Height = 20
  Placement = pos=(-37,-55,-54) rot=(0,0,1;0rad)
  Radius = 1.5
FEATURE [Part::Cylinder] Cylinder2491  label="Válec2469"
  Angle = 360
  AttacherType = Attacher::AttachEngine3D
  Height = 20
  Placement = pos=(28,-8,-3) rot=(0,1,0;1.5708rad)
  Radius = 1.5
FEATURE [Part::Cylinder] Cylinder2492  label="Válec2470"
  Angle = 360
  AttacherType = Attacher::AttachEngine3D
  Height = 20
  Placement = pos=(28,8,-3) rot=(0,1,0;1.5708rad)
  Radius = 1.5
FEATURE [Part::Cylinder] Cylinder2493  label="L-elb_pulley-GT2-16-A016"
  Angle = 360
  AttacherType = Attacher::AttachEngine3D
  Height = 13
  Placement = pos=(-8,-45,-9) rot=(0,0,1;0.523599rad)
  Radius = 9
FEATURE [Part::Box] Box1013  label="Krychle1012"
  AttacherType = Attacher::AttachEngine3D
  Height = 2
  Length = 6
  Placement = pos=(-24,-48,-2) rot=(0,0,1;0rad)
  Width = 6
FEATURE [Part::Cylinder] Cylinder2494  label="L-elb_pulley-GT2-16-A017"
  Angle = 360
  AttacherType = Attacher::AttachEngine3D
  Height = 20
  Placement = pos=(21,-45,-8) rot=(0,0,1;0.523599rad)
  Radius = 1.5
FEATURE [Part::Cylinder] Cylinder2495  label="Válec2471"
  Angle = 360
  AttacherType = Attacher::AttachEngine3D
  Height = 30
  Placement = pos=(26,37,7) rot=(0,1,0;1.5708rad)
  Radius = 3
FEATURE [Part::Cylinder] Cylinder2496  label="L-elb_pulley-GT2-16-B008"
  Angle = 360
  AttacherType = Attacher::AttachEngine3D
  Height = 13
  Placement = pos=(8,-45,-9) rot=(0,0,1;0.523599rad)
  Radius = 9
FEATURE [Part::Box] Box1014  label="Krychle1013"
  AttacherType = Attacher::AttachEngine3D
  Height = 2
  Length = 6
  Placement = pos=(-40,-58,-40) rot=(0,0,1;0rad)
  Width = 6
FEATURE [Part::Box] Box1015  label="Krychle1014"
  AttacherType = Attacher::AttachEngine3D
  Height = 6
  Length = 52
  Placement = pos=(-26,-48,4) rot=(0,0,1;0rad)
  Width = 6
FEATURE [Part::Cylinder] Cylinder2497  label="L-elb_pulley-GT2-16-A018"
  Angle = 360
  AttacherType = Attacher::AttachEngine3D
  Height = 20
  Placement = pos=(-21,-45,-8) rot=(0,0,1;0.523599rad)
  Radius = 1.5
FEATURE [Part::Cylinder] Cylinder2498  label="Válec2472"
  Angle = 360
  AttacherType = Attacher::AttachEngine3D
  Height = 20
  Placement = pos=(-16,-48,-60) rot=(0,0,1;0rad)
  Radius = 1.5
FEATURE [Part::Box] Box1016  label="Krychle1015"
  AttacherType = Attacher::AttachEngine3D
  Height = 2
  Length = 6
  Placement = pos=(18,-48,-2) rot=(0,0,1;0rad)
  Width = 6
FEATURE [Part::Compound] Compound1094
  Links = -> [Cylinder2487,Cylinder2480,Cylinder2476,Cylinder2485]
  Placement = pos=(53,0,0) rot=(0,0,1;0rad)
FEATURE [Part::Compound] Compound1095
  Links = -> [Box992,Box1007,Box990,Box1004]
  Placement = pos=(53,0,0) rot=(0,0,1;0rad)
FEATURE [Part::Compound] Compound1096
  Links = -> [Cylinder2477,Cylinder2478,Cylinder2479,Cylinder2475]
FEATURE [Part::Compound] Compound1097
  Links = -> [Box1008,Box993,Box1002]
  Placement = pos=(-26.5,0,-39) rot=(0,1,0;3.14159rad)
FEATURE [Part::Compound] Compound1099
  Links = -> [Box999,Box996]
  Placement = pos=(0,0,15) rot=(0,0,1;0rad)
FEATURE [Part::Compound] Compound1100
  Links = -> [Box1005,Box1011,Box1014]
  Placement = pos=(-26.5,0,-39) rot=(0,1,0;3.14159rad)
FEATURE [Part::Compound] Compound1101
  Links = -> [Cylinder2486,Cylinder2484,Cylinder2482]
  Placement = pos=(-26.5,0,-39) rot=(0,1,0;3.14159rad)
FEATURE [Part::Compound] Compound1102
  Links = -> [Box1001,Box1010,Box1003,Box1006]
FEATURE [Part::Compound] Compound1103
  Links = -> [Box1000,Box998]
  Placement = pos=(0,0,15) rot=(0,0,1;0rad)
FEATURE [Part::Compound] Compound1104
  Links = -> [Cylinder2489,Cylinder2492,Cylinder2483,Cylinder2491]
  Placement = pos=(0,-80,-34) rot=(0,0,1;1.5708rad)
FEATURE [Part::Compound] Compound1105
  Links = -> [Cylinder2488,Cylinder2495]
  Placement = pos=(0,-101,-34) rot=(0,0,1;1.5708rad)
FEATURE [Part::Compound] Compound1106
  Links = -> [Cylinder2498,Cylinder2481,Cylinder2490]
  Placement = pos=(-26.5,0,-39) rot=(0,1,0;3.14159rad)
FEATURE [Part::Compound] Compound1107
  Links = -> [Box1013,Box1016]
FEATURE [Part::Compound] Compound1108
  Links = -> [Cylinder2497,Cylinder2494]
FEATURE [Part::Compound] Compound1109
  Links = -> [Cylinder2493,Cylinder2496]
FEATURE [Part::Cut] Cut912
  Base = -> Box997
  Tool = -> Compound1099
FEATURE [Part::Cut] Cut914
  Base = -> Cut912
  Tool = -> Compound1095
FEATURE [Part::Cut] Cut916
  Base = -> Box991
  Tool = -> Compound1103
FEATURE [Part::Cut] Cut921
  Base = -> Cut916
  Tool = -> Compound1102
FEATURE [Part::Cut] Cut919
  Base = -> Cut921
  Placement = pos=(-8,-4,10) rot=(0,0,1;0rad)
  Tool = -> Compound1096
FEATURE [Part::Cut] Cut923
  Base = -> Cut914
  Placement = pos=(8,-4,10) rot=(0,0,1;0rad)
  Tool = -> Compound1094
FEATURE [Part::Cut] Cut924
  Base = -> Cut910
  Tool = -> Compound1097
FEATURE [Part::Cut] Cut925
  Base = -> Cut924
  Placement = pos=(26.5,-4,-1) rot=(0,0,1;0rad)
  Tool = -> Compound1101
FEATURE [Part::Cut] Cut926
  Base = -> Cut911
  Tool = -> Compound1100
FEATURE [Part::Cut] Cut918
  Base = -> Cut926
  Placement = pos=(-26.5,-4,-1) rot=(0,0,1;0rad)
  Tool = -> Compound1106
FEATURE [Part::Compound] Compound1098  label="xori_drzaky002"
  Links = -> [Cut919,Cut923,Cut925,Cut918]
FEATURE [Part::Cut] Cut917
  Base = -> Compound1098
  Tool = -> Compound1105
FEATURE [Part::Cut] Cut922
  Base = -> Cut917
  Tool = -> Compound1104
FEATURE [Part::Cut] Cut913
  Base = -> Cut922
  Tool = -> Compound1109
FEATURE [Part::Cut] Cut927
  Base = -> Cut913
  Tool = -> Box1015
FEATURE [Part::Cut] Cut920
  Base = -> Cut927
  Tool = -> Compound1108
FEATURE [Part::Cut] Cut915
  Base = -> Cut920
  Tool = -> Compound1107
FEATURE [Part::Box] Box1017  label="Krychle1016"
  AttacherType = Attacher::AttachEngine3D
  Height = 6
  Length = 52
  Placement = pos=(-26,-70,4) rot=(0,0,1;0rad)
  Width = 28
FEATURE [Part::Chamfer] Chamfer101
  Base = -> Cut915
  Edges = 4 edges r=2: [Edge222,Edge243,Edge339,Edge351]
FEATURE [Part::Chamfer] Chamfer102
  Base = -> Chamfer101
  Edges = 4 edges r=2: [Edge257,Edge276,Edge365,Edge384]
FEATURE [Part::Chamfer] Chamfer103
  Base = -> Chamfer102
  Edges = 2 edges r=4: [Edge3,Edge135]
FEATURE [Part::Box] Box1018  label="Krychle1017"
  AttacherType = Attacher::AttachEngine3D
  Height = 2
  Length = 6
  Placement = pos=(-40,-51,-46) rot=(0,0,1;0rad)
  Width = 6
FEATURE [Part::Box] Box1019  label="Krychle1018"
  AttacherType = Attacher::AttachEngine3D
  Height = 15
  Length = 15
  Placement = pos=(19,-174,-65) rot=(0,0,1;0rad)
  Width = 130
FEATURE [Part::Box] Box1020  label="Krychle1019"
  AttacherType = Attacher::AttachEngine3D
  Height = 15
  Length = 15
  Placement = pos=(-34,-174,-65) rot=(0,0,1;0rad)
  Width = 130
FEATURE [Part::Cylinder] Cylinder2499  label="Válec2473"
  Angle = 360
  AttacherType = Attacher::AttachEngine3D
  Height = 20
  Placement = pos=(-37,-60,-60) rot=(0,0,1;0rad)
  Radius = 1.5
FEATURE [Part::Box] Box1021  label="Krychle1020"
  AttacherType = Attacher::AttachEngine3D
  Height = 15
  Length = 15
  Placement = pos=(19,-174,-65) rot=(0,0,1;0rad)
  Width = 130
FEATURE [Part::Box] Box1022  label="Krychle1021"
  AttacherType = Attacher::AttachEngine3D
  Height = 18
  Length = 27
  Placement = pos=(-40,-66,-50) rot=(0,0,1;0rad)
  Width = 28
FEATURE [Part::Box] Box1023  label="Krychle1022"
  AttacherType = Attacher::AttachEngine3D
  Height = 2
  Length = 6
  Placement = pos=(-19,-51,-46) rot=(0,0,1;0rad)
  Width = 6
FEATURE [Part::Cylinder] Cylinder2500  label="Válec2474"
  Angle = 360
  AttacherType = Attacher::AttachEngine3D
  Height = 20
  Placement = pos=(-37,-48,-60) rot=(0,0,1;0rad)
  Radius = 1.5
FEATURE [Part::Box] Box1024  label="Krychle1023"
  AttacherType = Attacher::AttachEngine3D
  Height = 15
  Length = 15
  Placement = pos=(-7.5,-174,-4) rot=(0,0,1;0rad)
  Width = 130
FEATURE [Part::Box] Box1025  label="Krychle1024"
  AttacherType = Attacher::AttachEngine3D
  Height = 18
  Length = 27
  Placement = pos=(13,-66,-50) rot=(0,0,1;0rad)
  Width = 28
FEATURE [Part::Box] Box1026  label="Krychle1025"
  AttacherType = Attacher::AttachEngine3D
  Height = 2
  Length = 6
  Placement = pos=(-40,-51,-46) rot=(0,0,1;0rad)
  Width = 6
FEATURE [Part::Box] Box1027  label="Krychle1026"
  AttacherType = Attacher::AttachEngine3D
  Height = 18
  Length = 27
  Placement = pos=(-13.5,-66,-7) rot=(0,0,1;0rad)
  Width = 24
FEATURE [Part::Cylinder] Cylinder2501  label="Válec2475"
  Angle = 360
  AttacherType = Attacher::AttachEngine3D
  Height = 20
  Placement = pos=(-16,-48,-60) rot=(0,0,1;0rad)
  Radius = 1.5
FEATURE [Part::Box] Box1028  label="Krychle1027"
  AttacherType = Attacher::AttachEngine3D
  Height = 15
  Length = 15
  Placement = pos=(-34,-174,-65) rot=(0,0,1;0rad)
  Width = 130
FEATURE [Part::Cylinder] Cylinder2502  label="Válec2476"
  Angle = 360
  AttacherType = Attacher::AttachEngine3D
  Height = 20
  Placement = pos=(-16,-60,-60) rot=(0,0,1;0rad)
  Radius = 1.5
FEATURE [Part::Cylinder] Cylinder2503  label="Válec2477"
  Angle = 360
  AttacherType = Attacher::AttachEngine3D
  Height = 20
  Placement = pos=(-37,-48,-60) rot=(0,0,1;0rad)
  Radius = 1.5
FEATURE [Part::Cylinder] Cylinder2504  label="Válec2478"
  Angle = 360
  AttacherType = Attacher::AttachEngine3D
  Height = 20
  Placement = pos=(-16,-60,-60) rot=(0,0,1;0rad)
  Radius = 1.5
FEATURE [Part::Cylinder] Cylinder2505  label="Válec2479"
  Angle = 360
  AttacherType = Attacher::AttachEngine3D
  Height = 20
  Placement = pos=(-37,-60,-60) rot=(0,0,1;0rad)
  Radius = 1.5
FEATURE [Part::Box] Box1029  label="Krychle1028"
  AttacherType = Attacher::AttachEngine3D
  Height = 2
  Length = 6
  Placement = pos=(-40,-63,-46) rot=(0,0,1;0rad)
  Width = 6
FEATURE [Part::Box] Box1030  label="Krychle1029"
  AttacherType = Attacher::AttachEngine3D
  Height = 2
  Length = 6
  Placement = pos=(-40,-51,-46) rot=(0,0,1;0rad)
  Width = 6
FEATURE [Part::Box] Box1031  label="Krychle1030"
  AttacherType = Attacher::AttachEngine3D
  Height = 2
  Length = 6
  Placement = pos=(-19,-63,-46) rot=(0,0,1;0rad)
  Width = 6
FEATURE [Part::Cylinder] Cylinder2506  label="Válec2480"
  Angle = 360
  AttacherType = Attacher::AttachEngine3D
  Height = 20
  Placement = pos=(-37,-60,-60) rot=(0,0,1;0rad)
  Radius = 1.5
FEATURE [Part::Box] Box1032  label="Krychle1031"
  AttacherType = Attacher::AttachEngine3D
  Height = 2
  Length = 6
  Placement = pos=(-19,-63,-46) rot=(0,0,1;0rad)
  Width = 6
FEATURE [Part::Box] Box1033  label="Krychle1032"
  AttacherType = Attacher::AttachEngine3D
  Height = 2
  Length = 6
  Placement = pos=(-19,-51,-46) rot=(0,0,1;0rad)
  Width = 6
FEATURE [Part::Box] Box1034  label="Krychle1033"
  AttacherType = Attacher::AttachEngine3D
  Height = 2
  Length = 6
  Placement = pos=(-40,-63,-46) rot=(0,0,1;0rad)
  Width = 6
FEATURE [Part::Cylinder] Cylinder2507  label="Válec2481"
  Angle = 360
  AttacherType = Attacher::AttachEngine3D
  Height = 20
  Placement = pos=(-16,-60,-60) rot=(0,0,1;0rad)
  Radius = 1.5
FEATURE [Part::Cylinder] Cylinder2508  label="Válec2482"
  Angle = 360
  AttacherType = Attacher::AttachEngine3D
  Height = 20
  Placement = pos=(26,37,7) rot=(0,1,0;1.5708rad)
  Radius = 1.5
FEATURE [Part::Box] Box1035  label="Krychle1034"
  AttacherType = Attacher::AttachEngine3D
  Height = 2
  Length = 6
  Placement = pos=(-40,-63,-46) rot=(0,0,1;0rad)
  Width = 6
FEATURE [Part::Cylinder] Cylinder2509  label="Válec2483"
  Angle = 360
  AttacherType = Attacher::AttachEngine3D
  Height = 20
  Placement = pos=(-37,-48,-60) rot=(0,0,1;0rad)
  Radius = 1.5
FEATURE [Part::Cylinder] Cylinder2510  label="Válec2484"
  Angle = 360
  AttacherType = Attacher::AttachEngine3D
  Height = 30
  Placement = pos=(26,-37,7) rot=(0,1,0;1.5708rad)
  Radius = 3
FEATURE [Part::Cylinder] Cylinder2511  label="L-elb_pulley-GT2-16-B009"
  Angle = 360
  AttacherType = Attacher::AttachEngine3D
  Height = 13
  Placement = pos=(8,-45,-9) rot=(0,0,1;0.523599rad)
  Radius = 9
FEATURE [Part::Cylinder] Cylinder2512  label="Válec2485"
  Angle = 360
  AttacherType = Attacher::AttachEngine3D
  Height = 20
  Placement = pos=(-16,-48,-60) rot=(0,0,1;0rad)
  Radius = 1.5
FEATURE [Part::Box] Box1036  label="Krychle1035"
  AttacherType = Attacher::AttachEngine3D
  Height = 2
  Length = 6
  Placement = pos=(-19,-63,-46) rot=(0,0,1;0rad)
  Width = 6
FEATURE [Part::Cylinder] Cylinder2513  label="Válec2486"
  Angle = 360
  AttacherType = Attacher::AttachEngine3D
  Height = 20
  Placement = pos=(-37,-55,-54) rot=(0,0,1;0rad)
  Radius = 1.5
FEATURE [Part::Cylinder] Cylinder2514  label="Válec2487"
  Angle = 360
  AttacherType = Attacher::AttachEngine3D
  Height = 20
  Placement = pos=(28,-8,-3) rot=(0,1,0;1.5708rad)
  Radius = 1.5
FEATURE [Part::Box] Box1037  label="Krychle1036"
  AttacherType = Attacher::AttachEngine3D
  Height = 2
  Length = 6
  Placement = pos=(-19,-51,-46) rot=(0,0,1;0rad)
  Width = 6
FEATURE [Part::Cylinder] Cylinder2515  label="Válec2488"
  Angle = 360
  AttacherType = Attacher::AttachEngine3D
  Height = 20
  Placement = pos=(28,8,-3) rot=(0,1,0;1.5708rad)
  Radius = 1.5
FEATURE [Part::Cylinder] Cylinder2516  label="L-elb_pulley-GT2-16-A019"
  Angle = 360
  AttacherType = Attacher::AttachEngine3D
  Height = 20
  Placement = pos=(21,-45,-8) rot=(0,0,1;0.523599rad)
  Radius = 1.5
FEATURE [Part::Box] Box1038  label="Krychle1037"
  AttacherType = Attacher::AttachEngine3D
  Height = 15
  Length = 15
  Placement = pos=(-7.5,-174,-4) rot=(0,0,1;0rad)
  Width = 130
FEATURE [Part::Cylinder] Cylinder2517  label="Válec2489"
  Angle = 360
  AttacherType = Attacher::AttachEngine3D
  Height = 20
  Placement = pos=(-16,-55,-54) rot=(0,0,1;0rad)
  Radius = 1.5
FEATURE [Part::Box] Box1039  label="Krychle1038"
  AttacherType = Attacher::AttachEngine3D
  Height = 2
  Length = 6
  Placement = pos=(-19,-58,-40) rot=(0,0,1;0rad)
  Width = 6
FEATURE [Part::Cylinder] Cylinder2518  label="Válec2490"
  Angle = 360
  AttacherType = Attacher::AttachEngine3D
  Height = 20
  Placement = pos=(26,-37,7) rot=(0,1,0;1.5708rad)
  Radius = 1.5
FEATURE [Part::Box] Box1040  label="Krychle1039"
  AttacherType = Attacher::AttachEngine3D
  Height = 18
  Length = 27
  Placement = pos=(-13.5,-66,-7) rot=(0,0,1;0rad)
  Width = 24
FEATURE [Part::Cylinder] Cylinder2519  label="L-elb_pulley-GT2-16-A020"
  Angle = 360
  AttacherType = Attacher::AttachEngine3D
  Height = 13
  Placement = pos=(-8,-45,-9) rot=(0,0,1;0.523599rad)
  Radius = 9
FEATURE [Part::Box] Box1041  label="Krychle1040"
  AttacherType = Attacher::AttachEngine3D
  Height = 2
  Length = 6
  Placement = pos=(-24,-48,-2) rot=(0,0,1;0rad)
  Width = 6
FEATURE [Part::Cylinder] Cylinder2520  label="Válec2491"
  Angle = 360
  AttacherType = Attacher::AttachEngine3D
  Height = 30
  Placement = pos=(26,37,7) rot=(0,1,0;1.5708rad)
  Radius = 3
FEATURE [Part::Cylinder] Cylinder2521  label="L-elb_pulley-GT2-16-A021"
  Angle = 360
  AttacherType = Attacher::AttachEngine3D
  Height = 20
  Placement = pos=(-21,-45,-8) rot=(0,0,1;0.523599rad)
  Radius = 1.5
FEATURE [Part::Box] Box1042  label="Krychle1041"
  AttacherType = Attacher::AttachEngine3D
  Height = 2
  Length = 6
  Placement = pos=(-40,-58,-40) rot=(0,0,1;0rad)
  Width = 6
FEATURE [Part::Cylinder] Cylinder2522  label="Válec2492"
  Angle = 360
  AttacherType = Attacher::AttachEngine3D
  Height = 20
  Placement = pos=(-16,-48,-60) rot=(0,0,1;0rad)
  Radius = 1.5
FEATURE [Part::Box] Box1043  label="Krychle1042"
  AttacherType = Attacher::AttachEngine3D
  Height = 6
  Length = 52
  Placement = pos=(-26,-48,4) rot=(0,0,1;0rad)
  Width = 6
FEATURE [Part::Box] Box1044  label="Krychle1043"
  AttacherType = Attacher::AttachEngine3D
  Height = 2
  Length = 6
  Placement = pos=(18,-48,-2) rot=(0,0,1;0rad)
  Width = 6
FEATURE [Part::Cut] Cut928
  Base = -> Box1040
  Tool = -> Box1038
FEATURE [Part::Cut] Cut929
  Base = -> Box1027
  Tool = -> Box1024
FEATURE [Part::Compound] Compound1110
  Links = -> [Cylinder2510,Cylinder2520]
  Placement = pos=(0,-101,-34) rot=(0,0,1;1.5708rad)
FEATURE [Part::Compound] Compound1111
  Links = -> [Cylinder2517,Cylinder2509,Cylinder2506]
  Placement = pos=(-26.5,0,-39) rot=(0,1,0;3.14159rad)
FEATURE [Part::Compound] Compound1112
  Links = -> [Box1033,Box1036,Box1030,Box1035]
FEATURE [Part::Compound] Compound1113
  Links = -> [Box1020,Box1019]
  Placement = pos=(0,0,15) rot=(0,0,1;0rad)
FEATURE [Part::Cut] Cut935
  Base = -> Box1022
  Tool = -> Compound1113
FEATURE [Part::Cut] Cut931
  Base = -> Cut935
  Tool = -> Compound1112
FEATURE [Part::Compound] Compound1114
  Links = -> [Cylinder2518,Cylinder2515,Cylinder2508,Cylinder2514]
  Placement = pos=(0,-80,-34) rot=(0,0,1;1.5708rad)
FEATURE [Part::Compound] Compound1115
  Links = -> [Cylinder2522,Cylinder2507,Cylinder2513]
  Placement = pos=(-26.5,0,-39) rot=(0,1,0;3.14159rad)
FEATURE [Part::Compound] Compound1116
  Links = -> [Cylinder2521,Cylinder2516]
FEATURE [Part::Compound] Compound1117
  Links = -> [Cylinder2519,Cylinder2511]
FEATURE [Part::Compound] Compound1118
  Links = -> [Box1041,Box1044]
FEATURE [Part::Compound] Compound1119
  Links = -> [Box1039,Box1018,Box1029]
  Placement = pos=(-26.5,0,-39) rot=(0,1,0;3.14159rad)
FEATURE [Part::Cut] Cut942
  Base = -> Cut929
  Tool = -> Compound1119
FEATURE [Part::Cut] Cut944
  Base = -> Cut942
  Placement = pos=(26.5,-4,-1) rot=(0,0,1;0rad)
  Tool = -> Compound1111
FEATURE [Part::Compound] Compound1120
  Links = -> [Cylinder2512,Cylinder2504,Cylinder2500,Cylinder2505]
  Placement = pos=(53,0,0) rot=(0,0,1;0rad)
FEATURE [Part::Compound] Compound1121
  Links = -> [Box1023,Box1032,Box1026,Box1034]
  Placement = pos=(53,0,0) rot=(0,0,1;0rad)
FEATURE [Part::Compound] Compound1122
  Links = -> [Cylinder2501,Cylinder2502,Cylinder2503,Cylinder2499]
FEATURE [Part::Cut] Cut933
  Base = -> Cut931
  Placement = pos=(-8,-4,10) rot=(0,0,1;0rad)
  Tool = -> Compound1122
FEATURE [Part::Compound] Compound1123
  Links = -> [Box1028,Box1021]
  Placement = pos=(0,0,15) rot=(0,0,1;0rad)
FEATURE [Part::Cut] Cut945
  Base = -> Box1025
  Tool = -> Compound1123
FEATURE [Part::Cut] Cut937
  Base = -> Cut945
  Tool = -> Compound1121
FEATURE [Part::Cut] Cut943
  Base = -> Cut937
  Placement = pos=(8,-4,10) rot=(0,0,1;0rad)
  Tool = -> Compound1120
FEATURE [Part::Compound] Compound1125
  Links = -> [Box1031,Box1037,Box1042]
  Placement = pos=(-26.5,0,-39) rot=(0,1,0;3.14159rad)
FEATURE [Part::Cut] Cut940
  Base = -> Cut928
  Tool = -> Compound1125
FEATURE [Part::Cut] Cut930
  Base = -> Cut940
  Placement = pos=(-26.5,-4,-1) rot=(0,0,1;0rad)
  Tool = -> Compound1115
FEATURE [Part::Compound] Compound1124  label="xori_drzaky003"
  Links = -> [Cut933,Cut943,Cut944,Cut930]
FEATURE [Part::Cut] Cut939
  Base = -> Compound1124
  Tool = -> Compound1110
FEATURE [Part::Cut] Cut932
  Base = -> Cut939
  Tool = -> Compound1114
FEATURE [Part::Cut] Cut936
  Base = -> Cut932
  Tool = -> Compound1117
FEATURE [Part::Cut] Cut941
  Base = -> Cut936
  Tool = -> Box1043
FEATURE [Part::Cut] Cut934
  Base = -> Cut941
  Tool = -> Compound1116
FEATURE [Part::Cut] Cut938
  Base = -> Cut934
  Tool = -> Compound1118
FEATURE [Part::Chamfer] Chamfer104
  Base = -> Cut938
  Edges = 4 edges r=2: [Edge222,Edge243,Edge339,Edge351]
FEATURE [Part::Chamfer] Chamfer105
  Base = -> Chamfer104
  Edges = 4 edges r=2: [Edge257,Edge276,Edge365,Edge384]
FEATURE [Part::Chamfer] Chamfer106
  Base = -> Chamfer105
  Edges = 2 edges r=4: [Edge3,Edge135]
FEATURE [Part::Common] Common003
  Base = -> Box1017
  Tool = -> Chamfer106
FEATURE [Part::Compound] Compound1126  label="L-elb_xorior-cover"
  Links = -> [Common003,Cut880]
FEATURE [Part::Box] Box1045  label="Krychle1044"
  AttacherType = Attacher::AttachEngine3D
  Height = 6
  Length = 52
  Placement = pos=(-26,-70,4) rot=(0,0,1;0rad)
  Width = 28
FEATURE [Part::Cut] Cut946
  Base = -> Chamfer103
  Tool = -> Box1045
FEATURE [Part::Compound] Compound1093  label="L-elb_xorior-hole"
  Links = -> [Cut881,Cut946]
FEATURE [Mesh::Feature] Mesh006  label="L-elb_xorior-hole (Meshed)"
FEATURE [Mesh::Feature] Mesh007  label="L-elb_xorior-cover (Meshed)"
FEATURE [Part::Cylinder] Cylinder2531  label="Válec2501"
  Angle = 360
  AttacherType = Attacher::AttachEngine3D
  Height = 20
  Placement = pos=(-19.4454,-19.4454,10) rot=(0,0,1;2.35619rad)
  Radius = 1.5
FEATURE [Part::Cylinder] Cylinder2532  label="Válec2502"
  Angle = 360
  AttacherType = Attacher::AttachEngine3D
  Height = 20
  Placement = pos=(-19.4454,19.4454,10) rot=(0,0,1;0.785398rad)
  Radius = 1.5
FEATURE [Part::Cylinder] Cylinder2533  label="Válec2503"
  Angle = 360
  AttacherType = Attacher::AttachEngine3D
  Height = 20
  Placement = pos=(27.5,1.2e-14,10) rot=(0,0,-1;1.5708rad)
  Radius = 1.5
FEATURE [Part::Cylinder] Cylinder2534  label="Válec2504"
  Angle = 360
  AttacherType = Attacher::AttachEngine3D
  Height = 20
  Placement = pos=(19.4454,-19.4454,10) rot=(0,0,1;3.92699rad)
  Radius = 1.5
FEATURE [Part::Cylinder] Cylinder2535  label="Válec2505"
  Angle = 360
  AttacherType = Attacher::AttachEngine3D
  Height = 20
  Placement = pos=(0,27.5,10) rot=(0,0,1;0rad)
  Radius = 1.5
FEATURE [Part::Cylinder] Cylinder2536  label="Válec2506"
  Angle = 360
  AttacherType = Attacher::AttachEngine3D
  Height = 20
  Placement = pos=(-27.5,-4e-15,10) rot=(0,0,1;1.5708rad)
  Radius = 1.5
FEATURE [Part::Cylinder] Cylinder2537  label="Válec2507"
  Angle = 360
  AttacherType = Attacher::AttachEngine3D
  Height = 20
  Placement = pos=(19.4454,19.4454,10) rot=(0,0,-1;0.785398rad)
  Radius = 1.5
FEATURE [Part::Cylinder] Cylinder2538  label="Válec2508"
  Angle = 360
  AttacherType = Attacher::AttachEngine3D
  Height = 20
  Placement = pos=(1.1e-14,-27.5,10) rot=(0,0,1;3.14159rad)
  Radius = 1.5
FEATURE [Part::Compound] Compound1128
  Links = -> [Cylinder2535,Cylinder2532,Cylinder2536,Cylinder2531,Cylinder2538,Cylinder2533,Cylinder2534,Cylinder2537]
  Placement = pos=(0,0,-16) rot=(0,0,1;0.392699rad)
FEATURE [Part::Cylinder] Cylinder2539  label="Válec2509"
  Angle = 360
  AttacherType = Attacher::AttachEngine3D
  Height = 20
  Placement = pos=(-27.5,-4e-15,10) rot=(0,0,1;1.5708rad)
  Radius = 1.5
FEATURE [Part::Cylinder] Cylinder2540  label="Válec2510"
  Angle = 360
  AttacherType = Attacher::AttachEngine3D
  Height = 20
  Placement = pos=(-19.4454,19.4454,10) rot=(0,0,1;0.785398rad)
  Radius = 1.5
FEATURE [Part::Cylinder] Cylinder2541  label="Válec2511"
  Angle = 360
  AttacherType = Attacher::AttachEngine3D
  Height = 20
  Placement = pos=(0,27.5,10) rot=(0,0,1;0rad)
  Radius = 1.5
FEATURE [Part::Cylinder] Cylinder2542  label="Válec2512"
  Angle = 360
  AttacherType = Attacher::AttachEngine3D
  Height = 20
  Placement = pos=(-19.4454,-19.4454,10) rot=(0,0,1;2.35619rad)
  Radius = 1.5
FEATURE [Part::Cylinder] Cylinder2543  label="Válec2513"
  Angle = 360
  AttacherType = Attacher::AttachEngine3D
  Height = 20
  Placement = pos=(27.5,1.2e-14,10) rot=(0,0,-1;1.5708rad)
  Radius = 1.5
FEATURE [Part::Cylinder] Cylinder2544  label="Válec2514"
  Angle = 360
  AttacherType = Attacher::AttachEngine3D
  Height = 20
  Placement = pos=(19.4454,-19.4454,10) rot=(0,0,1;3.92699rad)
  Radius = 1.5
FEATURE [Part::Cylinder] Cylinder2545  label="Válec2515"
  Angle = 360
  AttacherType = Attacher::AttachEngine3D
  Height = 20
  Placement = pos=(19.4454,19.4454,10) rot=(0,0,-1;0.785398rad)
  Radius = 1.5
FEATURE [Part::Cylinder] Cylinder2546  label="Válec2516"
  Angle = 360
  AttacherType = Attacher::AttachEngine3D
  Height = 20
  Placement = pos=(1.1e-14,-27.5,10) rot=(0,0,1;3.14159rad)
  Radius = 1.5
FEATURE [Part::Compound] Compound1129
  Links = -> [Cylinder2541,Cylinder2540,Cylinder2539,Cylinder2542,Cylinder2546,Cylinder2543,Cylinder2544,Cylinder2545]
  Placement = pos=(0,0,-27) rot=(0,0,1;0.392699rad)
FEATURE [Part::Cut] Cut947  label="J-mini_encoder-belt-ring_rear"
  Base = -> Compound1069
  Tool = -> Compound1129
FEATURE [Part::Cut] Cut948  label="J-mini_encoder-belt-ring_front2"
  Base = -> Chamfer090
  Tool = -> Compound1128
FEATURE [Mesh::Feature] Mesh008  label="L-elb_xorior-washer (Meshed)"
FEATURE [Mesh::Feature] Mesh009  label="J-mini_encoder-belt-ring_rear (Meshed)"
FEATURE [Part::Box] Box1046  label="Krychle1045"
  AttacherType = Attacher::AttachEngine3D
  Height = 20
  Length = 22.8
  Placement = pos=(-11.4,-15.34,34) rot=(0,0,1;0rad)
  Width = 34.21
FEATURE [Part::Box] Box1047  label="Krychle1046"
  AttacherType = Attacher::AttachEngine3D
  Height = 7
  Length = 42
  Placement = pos=(-21,-12,34) rot=(0,0,1;0rad)
  Width = 24
FEATURE [Part::Cylinder] Cylinder2547  label="Válec2517"
  Angle = 360
  AttacherType = Attacher::AttachEngine3D
  Height = 60
  Placement = pos=(-18,95,-57) rot=(0,0,1;0rad)
  Radius = 1.5
FEATURE [Part::Cylinder] Cylinder2548  label="Válec2518"
  Angle = 360
  AttacherType = Attacher::AttachEngine3D
  Height = 48
  Placement = pos=(0,90,-53) rot=(0,0,1;0rad)
  Radius = 2.6
FEATURE [Part::Box] Box1048  label="Krychle1047"
  AttacherType = Attacher::AttachEngine3D
  Height = 2
  Length = 6
  Placement = pos=(15,82,-56) rot=(0,0,1;0rad)
  Width = 6
FEATURE [Part::Cylinder] Cylinder2549  label="Válec2519"
  Angle = 360
  AttacherType = Attacher::AttachEngine3D
  Height = 5
  Placement = pos=(0,90,77) rot=(0,0,1;0rad)
  Radius = 3
FEATURE [Part::Box] Box1049  label="Krychle1048"
  AttacherType = Attacher::AttachEngine3D
  Height = 24
  Length = 36
  Placement = pos=(-18,78,-49) rot=(0,0,1;0rad)
  Width = 24
FEATURE [Part::Cylinder] Cylinder2550  label="Válec2520"
  Angle = 360
  AttacherType = Attacher::AttachEngine3D
  Height = 5
  Placement = pos=(0,90,77) rot=(0,0,1;0rad)
  Radius = 5
FEATURE [Part::Box] Box1050  label="Krychle1049"
  AttacherType = Attacher::AttachEngine3D
  Height = 2
  Length = 6
  Placement = pos=(-21,92,-56) rot=(0,0,1;0rad)
  Width = 6
FEATURE [Part::Cylinder] Cylinder2551  label="Válec2521"
  Angle = 360
  AttacherType = Attacher::AttachEngine3D
  Height = 60
  Placement = pos=(18,85,-57) rot=(0,0,1;0rad)
  Radius = 1.5
FEATURE [Part::Cylinder] Cylinder2552  label="Válec2522"
  Angle = 360
  AttacherType = Attacher::AttachEngine3D
  Height = 60
  Placement = pos=(-18,85,-57) rot=(0,0,1;0rad)
  Radius = 1.5
FEATURE [Part::Box] Box1051  label="Krychle1050"
  AttacherType = Attacher::AttachEngine3D
  Height = 2
  Length = 6
  Placement = pos=(15,92,-56) rot=(0,0,1;0rad)
  Width = 6
FEATURE [Part::Cylinder] Cylinder2553  label="Válec2523"
  Angle = 360
  AttacherType = Attacher::AttachEngine3D
  Height = 60
  Placement = pos=(-18,95,-57) rot=(0,0,1;0rad)
  Radius = 1.5
FEATURE [Part::Cylinder] Cylinder2554  label="Válec2524"
  Angle = 360
  AttacherType = Attacher::AttachEngine3D
  Height = 60
  Placement = pos=(-18,85,-57) rot=(0,0,1;0rad)
  Radius = 1.5
FEATURE [Part::Cylinder] Cylinder2555  label="Válec2525"
  Angle = 360
  AttacherType = Attacher::AttachEngine3D
  Height = 60
  Placement = pos=(18,85,-57) rot=(0,0,1;0rad)
  Radius = 1.5
FEATURE [Part::Cylinder] Cylinder2556  label="Válec2526"
  Angle = 360
  AttacherType = Attacher::AttachEngine3D
  Height = 60
  Placement = pos=(18,95,-57) rot=(0,0,1;0rad)
  Radius = 1.5
FEATURE [Part::Cylinder] Cylinder2557  label="Válec2527"
  Angle = 360
  AttacherType = Attacher::AttachEngine3D
  Height = 60
  Placement = pos=(18,95,-57) rot=(0,0,1;0rad)
  Radius = 1.5
FEATURE [Part::Box] Box1052  label="Krychle1051"
  AttacherType = Attacher::AttachEngine3D
  Height = 2
  Length = 6
  Placement = pos=(-21,82,-56) rot=(0,0,1;0rad)
  Width = 6
FEATURE [Part::FeaturePython] Tube106  # WARN: FeaturePython — macro-defined, semantics opaque (R4)
  AttacherType = Attacher::AttachEngine3D
  Height = 1
  InnerRadius = 4
  OuterRadius = 5
  Placement = pos=(0,90,81) rot=(0,0,1;0rad)
FEATURE [Part::Compound] Compound1131
  Links = -> [Cylinder2556,Cylinder2551,Cylinder2552,Cylinder2547]
  Placement = pos=(0,0,-31) rot=(0,0,1;0rad)
FEATURE [Part::Compound] Compound1132
  Links = -> [Cylinder2549]
  Placement = pos=(0,0,-24) rot=(0,0,1;3.92699rad)
FEATURE [Part::Compound] Compound1133
  Links = -> [Box1047]
  Placement = pos=(63.64,-63.64,43) rot=(0,0,1;3.92699rad)
FEATURE [Part::Compound] Compound1134
  Links = -> [Box1046]
  Placement = pos=(0,90,-83) rot=(0,0,1;0rad)
FEATURE [Part::Cut] Cut950
  Base = -> Box1049
  Placement = pos=(0,0,21) rot=(0,0,1;0rad)
  Tool = -> Compound1134
FEATURE [Part::Cut] Cut949
  Base = -> Cut950
  Tool = -> Cylinder2548
FEATURE [Part::Chamfer] Chamfer108
  Base = -> Cut949
  Edges = 2 edges r=6: [Edge6,Edge8]
FEATURE [Part::Cut] Cut952
  Base = -> Chamfer108
  Tool = -> Compound1131
FEATURE [Part::Chamfer] Chamfer107
  Base = -> Cut952
  Edges = 2 edges r=3: [Edge25,Edge33]
  Placement = pos=(0,180,0) rot=(0,0,1;3.14159rad)
FEATURE [Part::Compound] Compound1135
  Links = -> [Box1052,Box1050,Box1048,Box1051]
  Placement = pos=(0,0,117) rot=(0,0,1;3.92699rad)
FEATURE [Part::Compound] Compound1136
  Links = -> [Cylinder2557,Cylinder2555,Cylinder2554,Cylinder2553]
  Placement = pos=(0,0,100) rot=(0,0,1;3.92699rad)
FEATURE [Part::Compound] Compound1137
  Links = -> [Cylinder2550]
  Placement = pos=(0,0,2) rot=(0,0,1;3.92699rad)
FEATURE [Part::Cut] Cut951
  Base = -> Compound1133
  Placement = pos=(0,0,-22) rot=(0,0,1;0rad)
  Tool = -> Compound1137
FEATURE [Part::Cut] Cut953
  Base = -> Cut951
  Tool = -> Compound1132
FEATURE [Part::Compound] Compound1139
  Links = -> [Tube106]
  Placement = pos=(0,0,-24) rot=(0,0,1;3.92699rad)
FEATURE [Part::Compound] Compound1138
  Links = -> [Compound1139,Cut953]
  Placement = pos=(0,0,4) rot=(0,0,1;0rad)
FEATURE [Part::Cut] Cut954
  Base = -> Compound1138
  Tool = -> Compound1136
FEATURE [Part::Cut] Cut955
  Base = -> Cut954
  Tool = -> Compound1135
FEATURE [Part::Chamfer] Chamfer109
  Base = -> Cut955
  Edges = 2 edges r=2: [Edge10,Edge36]
  Placement = pos=(0,180,31) rot=(-0.382683,0.92388,0;3.14159rad)
FEATURE [Part::Compound] Compound1130  label="L-elb_encoder-uphold003"
  Links = -> [Chamfer107,Chamfer109]
  Placement = pos=(0,-174,20) rot=(0,0,1;0rad)
FEATURE [Part::Chamfer] Chamfer110  label="L-elb_encoder-uphold"
  Base = -> Compound1130
  Edges = 2 edges r=2: [Edge18,Edge45]
FEATURE [Part::Cylinder] Cylinder2558  label="Válec2528"
  Angle = 360
  AttacherType = Attacher::AttachEngine3D
  Height = 3
  Placement = pos=(-34,-80,-32) rot=(0,0,1;0rad)
  Radius = 4
FEATURE [Part::Cylinder] Cylinder2559  label="Válec2529"
  Angle = 360
  AttacherType = Attacher::AttachEngine3D
  Height = 3
  Placement = pos=(-18,85,-57) rot=(0,0,1;0rad)
  Radius = 3
FEATURE [Part::Cylinder] Cylinder2560  label="Válec2530"
  Angle = 360
  AttacherType = Attacher::AttachEngine3D
  Height = 20
  Placement = pos=(15.75,114,39.48) rot=(0,0.707107,0.707107;3.14159rad)
  Radius = 1.5
FEATURE [Part::Cylinder] Cylinder2561  label="Válec2531"
  Angle = 360
  AttacherType = Attacher::AttachEngine3D
  Height = 3
  Placement = pos=(18,85,-57) rot=(0,0,1;0rad)
  Radius = 3
FEATURE [Part::Box] Box1053  label="Krychle1052"
  AttacherType = Attacher::AttachEngine3D
  Height = 7
  Length = 42
  Placement = pos=(-21,-12,34) rot=(0,0,1;0rad)
  Width = 24
FEATURE [Part::Cylinder] Cylinder2562  label="Válec2532"
  Angle = 360
  AttacherType = Attacher::AttachEngine3D
  Height = 3
  Placement = pos=(34,-80,-32) rot=(0,0,1;0rad)
  Radius = 4
FEATURE [Part::Cylinder] Cylinder2563  label="Válec2533"
  Angle = 360
  AttacherType = Attacher::AttachEngine3D
  Height = 5
  Placement = pos=(0,90,77) rot=(0,0,1;0rad)
  Radius = 5
FEATURE [Part::Cylinder] Cylinder2564  label="Válec2534"
  Angle = 360
  AttacherType = Attacher::AttachEngine3D
  Height = 60
  Placement = pos=(18,95,-57) rot=(0,0,1;0rad)
  Radius = 1.5
FEATURE [Part::Cylinder] Cylinder2565  label="Válec2535"
  Angle = 360
  AttacherType = Attacher::AttachEngine3D
  Height = 20
  Placement = pos=(15.75,114,58.525) rot=(0,0.707107,0.707107;3.14159rad)
  Radius = 1.5
FEATURE [Part::Cylinder] Cylinder2566  label="Válec2536"
  Angle = 360
  AttacherType = Attacher::AttachEngine3D
  Height = 3
  Placement = pos=(-18,95,-57) rot=(0,0,1;0rad)
  Radius = 3
FEATURE [Part::Cylinder] Cylinder2567  label="Válec2537"
  Angle = 360
  AttacherType = Attacher::AttachEngine3D
  Height = 3
  Placement = pos=(18,95,-57) rot=(0,0,1;0rad)
  Radius = 3
FEATURE [Part::Cylinder] Cylinder2568  label="Válec2538"
  Angle = 360
  AttacherType = Attacher::AttachEngine3D
  Height = 60
  Placement = pos=(-18,95,-57) rot=(0,0,1;0rad)
  Radius = 1.5
FEATURE [Part::Box] Box1054  label="Krychle1053"
  AttacherType = Attacher::AttachEngine3D
  Height = 15
  Length = 42
  Placement = pos=(-21,-89,-49) rot=(0,0,1;0rad)
  Width = 18
FEATURE [Part::Cylinder] Cylinder2569  label="Válec2539"
  Angle = 360
  AttacherType = Attacher::AttachEngine3D
  Height = 60
  Placement = pos=(-18,85,-57) rot=(0,0,1;0rad)
  Radius = 1.5
FEATURE [Part::Cylinder] Cylinder2570  label="Válec2540"
  Angle = 360
  AttacherType = Attacher::AttachEngine3D
  Height = 60
  Placement = pos=(18,85,-57) rot=(0,0,1;0rad)
  Radius = 1.5
FEATURE [Part::Box] Box1055  label="Krychle1054"
  AttacherType = Attacher::AttachEngine3D
  Height = 4
  Length = 84
  Placement = pos=(-42,-88,-44) rot=(0,0,1;0rad)
  Width = 16
FEATURE [Part::Cylinder] Cylinder2571  label="Válec2541"
  Angle = 360
  AttacherType = Attacher::AttachEngine3D
  Height = 20
  Placement = pos=(34,-80,-32) rot=(0,0,1;0rad)
  Radius = 2
FEATURE [Part::Cylinder] Cylinder2572  label="Válec2542"
  Angle = 360
  AttacherType = Attacher::AttachEngine3D
  Height = 20
  Placement = pos=(-34,-80,-32) rot=(0,0,1;0rad)
  Radius = 2
FEATURE [Part::Box] Box1056  label="Krychle1055"
  AttacherType = Attacher::AttachEngine3D
  Height = 15
  Length = 4
  Placement = pos=(21,-88,-40) rot=(0,0,1;0rad)
  Width = 16
FEATURE [Part::Box] Box1057  label="Krychle1056"
  AttacherType = Attacher::AttachEngine3D
  Height = 15
  Length = 4
  Placement = pos=(-25,-88,-40) rot=(0,0,1;0rad)
  Width = 16
FEATURE [Part::Chamfer] Chamfer112
  Base = -> Box1055
  Edges = 2 edges r=4: [Edge1,Edge5]
FEATURE [Part::Chamfer] Chamfer111
  Base = -> Chamfer112
  Edges = 2 edges r=2: [Edge3,Edge16]
FEATURE [Part::Compound] Compound1143
  Links = -> [Cylinder2567,Cylinder2561,Cylinder2559,Cylinder2566]
  Placement = pos=(0,0,140) rot=(0,0,1;3.92699rad)
FEATURE [Part::Compound] Compound1144
  Links = -> [Box1053]
  Placement = pos=(63.64,-63.64,43) rot=(0,0,1;3.92699rad)
FEATURE [Part::Compound] Compound1146
  Links = -> [Cylinder2563]
  Placement = pos=(0,0,0) rot=(0,0,1;3.92699rad)
FEATURE [Part::Compound] Compound1147
  Links = -> [Cylinder2564,Cylinder2570,Cylinder2569,Cylinder2568]
  Placement = pos=(0,0,100) rot=(0,0,1;3.92699rad)
FEATURE [Part::Compound] Compound1148
  Links = -> [Cylinder2558,Cylinder2562]
  Placement = pos=(0,0,-13) rot=(0,0,1;0rad)
FEATURE [Part::Compound] Compound1149
  Links = -> [Cylinder2560,Cylinder2565]
  Placement = pos=(-49,0,-96) rot=(0.57735,0.57735,0.57735;2.0944rad)
FEATURE [Part::Compound] Compound1145
  Links = -> [Compound1149]
  Placement = pos=(52.33,-52.33,52) rot=(0,0,1;3.92699rad)
FEATURE [Part::Compound] Compound1150
  Links = -> [Cylinder2572,Cylinder2571]
  Placement = pos=(0,0,-20) rot=(0,0,1;0rad)
FEATURE [Part::Cut] Cut956
  Base = -> Compound1144
  Tool = -> Compound1146
FEATURE [Part::Cut] Cut962
  Base = -> Chamfer111
  Tool = -> Compound1150
FEATURE [Part::Cut] Cut961
  Base = -> Cut962
  Tool = -> Compound1148
FEATURE [Part::Cut] Cut959
  Base = -> Cut961
  Tool = -> Box1054
FEATURE [Part::FeaturePython] Tube107  # WARN: FeaturePython — macro-defined, semantics opaque (R4)
  AttacherType = Attacher::AttachEngine3D
  Height = 1
  InnerRadius = 4
  OuterRadius = 5
  Placement = pos=(0,90,81) rot=(0,0,1;0rad)
FEATURE [Part::Compound] Compound1141
  Links = -> [Tube107]
  Placement = pos=(0,0,0) rot=(0,0,1;3.92699rad)
FEATURE [Part::Compound] Compound1140
  Links = -> [Compound1141,Cut956]
FEATURE [Part::Cut] Cut957
  Base = -> Compound1140
  Tool = -> Compound1145
FEATURE [Part::Cut] Cut960
  Base = -> Cut957
  Tool = -> Compound1143
FEATURE [Part::Cut] Cut958
  Base = -> Cut960
  Placement = pos=(0,-174,52) rot=(0.92388,0.382683,0;3.14159rad)
  Tool = -> Compound1147
FEATURE [Part::Chamfer] Chamfer113
  Base = -> Cut958
  Edges = 2 edges r=2: [Edge7,Edge16]
  Placement = pos=(0,0,-2) rot=(0,0,1;0rad)
FEATURE [Part::Compound] Compound1142  label="L-elb_encoder-bottomhold002"
  Links = -> [Cut959,Box1056,Box1057,Chamfer113]
FEATURE [Part::Chamfer] Chamfer114  label="L-elb_encoder-bottomhold"
  Base = -> Compound1142
  Edges = 2 edges r=2: [Edge17,Edge30]
FEATURE [Mesh::Feature] Mesh010  label="L-elb_encoder-uphold (Meshed)"
FEATURE [Part::FeaturePython] Tube108  label="L-elb_encoder-washer-2mm"  # WARN: FeaturePython — macro-defined, semantics opaque (R4)
  AttacherType = Attacher::AttachEngine3D
  Height = 2
  InnerRadius = 1.6
  OuterRadius = 3
FEATURE [Part::FeaturePython] Tube109  label="L-elb_encoder-washer-3mm"  # WARN: FeaturePython — macro-defined, semantics opaque (R4)
  AttacherType = Attacher::AttachEngine3D
  Height = 3
  InnerRadius = 1.6
  OuterRadius = 3
FEATURE [Part::FeaturePython] Tube110  label="L-elb_encoder-washer-4mm"  # WARN: FeaturePython — macro-defined, semantics opaque (R4)
  AttacherType = Attacher::AttachEngine3D
  Height = 4
  InnerRadius = 1.6
  OuterRadius = 3
FEATURE [Mesh::Feature] Mesh011  label="L-elb_encoder-washer-2mm (Meshed)"
FEATURE [Mesh::Feature] Mesh012  label="L-elb_encoder-washer-3mm (Meshed)"
FEATURE [Mesh::Feature] Mesh013  label="L-elb_encoder-washer-4mm (Meshed)"
FEATURE [Part::FeaturePython] Tube111  # WARN: FeaturePython — macro-defined, semantics opaque (R4)
  AttacherType = Attacher::AttachEngine3D
  Height = 4
  InnerRadius = 14
  OuterRadius = 18
  Placement = pos=(0,0,1) rot=(0,0,1;0rad)
FEATURE [Part::FeaturePython] Tube112  # WARN: FeaturePython — macro-defined, semantics opaque (R4)
  AttacherType = Attacher::AttachEngine3D
  Height = 1
  InnerRadius = 12
  OuterRadius = 18
  Placement = pos=(0,0,8) rot=(0,0,1;0rad)
FEATURE [Part::Box] Box1058  label="Krychle1057"
  AttacherType = Attacher::AttachEngine3D
  Height = 80
  Length = 31
  Placement = pos=(-16,330,-48) rot=(0,0,1;0rad)
  Width = 6
FEATURE [Part::Box] Box1059  label="Krychle1058"
  AttacherType = Attacher::AttachEngine3D
  Height = 80
  Length = 12
  Placement = pos=(-6,25,-48) rot=(0,0,1;0rad)
  Width = 8
FEATURE [Part::Compound] Compound1152
  Links = -> [Box1059,Box1058]
  Placement = pos=(79,-8,10) rot=(0.57735,-0.57735,0.57735;2.0944rad)
FEATURE [Part::Cylinder] Cylinder2573  label="Válec2543"
  Angle = 360
  AttacherType = Attacher::AttachEngine3D
  Height = 30
  Placement = pos=(51,-30,0) rot=(0,0,1;0rad)
  Radius = 1.5
FEATURE [Part::Box] Box1060  label="Krychle1059"
  AttacherType = Attacher::AttachEngine3D
  Height = 2
  Length = 6
  Placement = pos=(48,-3,7) rot=(0,0,1;0rad)
  Width = 6
FEATURE [Part::Cylinder] Cylinder2574  label="Válec2544"
  Angle = 360
  AttacherType = Attacher::AttachEngine3D
  Height = 30
  Placement = pos=(51,30,0) rot=(0,0,1;0rad)
  Radius = 1.5
FEATURE [Part::Cylinder] Cylinder2575  label="Válec2545"
  Angle = 360
  AttacherType = Attacher::AttachEngine3D
  Height = 30
  Placement = pos=(51,0,0) rot=(0,0,1;0rad)
  Radius = 1.5
FEATURE [Part::Compound] Compound1153
  Links = -> [Cylinder2573,Cylinder2575,Cylinder2574]
FEATURE [Part::Box] Box1061  label="Krychle1060"
  AttacherType = Attacher::AttachEngine3D
  Height = 2
  Length = 6
  Placement = pos=(48,-3,11) rot=(0,0,1;0rad)
  Width = 6
FEATURE [Part::Box] Box1062  label="Krychle1061"
  AttacherType = Attacher::AttachEngine3D
  Height = 2
  Length = 6
  Placement = pos=(48,27,7) rot=(0,0,1;0rad)
  Width = 6
FEATURE [Part::Box] Box1063  label="Krychle1062"
  AttacherType = Attacher::AttachEngine3D
  Height = 2
  Length = 6
  Placement = pos=(48,-33,11) rot=(0,0,1;0rad)
  Width = 6
FEATURE [Part::Box] Box1064  label="Krychle1063"
  AttacherType = Attacher::AttachEngine3D
  Height = 2
  Length = 6
  Placement = pos=(48,27,11) rot=(0,0,1;0rad)
  Width = 6
FEATURE [Part::Box] Box1065  label="Krychle1064"
  AttacherType = Attacher::AttachEngine3D
  Height = 2
  Length = 6
  Placement = pos=(48,-33,7) rot=(0,0,1;0rad)
  Width = 6
FEATURE [Part::Compound] Compound1151
  Links = -> [Box1060,Box1061,Box1063,Box1065,Box1064,Box1062]
FEATURE [Part::Cylinder] Cylinder2576  label="Válec2546"
  Angle = 360
  AttacherType = Attacher::AttachEngine3D
  Height = 10
  Placement = pos=(46,0,10) rot=(0,1,0;1.5708rad)
  Radius = 38
FEATURE [Part::Common] Common004
  Base = -> Compound1152
  Tool = -> Cylinder2576
FEATURE [Part::Cut] Cut964
  Base = -> Common004
  Tool = -> Compound1151
FEATURE [Part::Cut] Cut963
  Base = -> Cut964
  Tool = -> Compound1153
FEATURE [Part::Cylinder] Cylinder2577  label="Válec2547"
  Angle = 360
  AttacherType = Attacher::AttachEngine3D
  Height = 5
  Radius = 38
FEATURE [Part::Cylinder] Cylinder2578  label="Válec2548"
  Angle = 360
  AttacherType = Attacher::AttachEngine3D
  Height = 20
  Placement = pos=(-27,-4e-15,19) rot=(0,0,1;1.5708rad)
  Radius = 1
FEATURE [Part::Cylinder] Cylinder2579  label="Válec2549"
  Angle = 360
  AttacherType = Attacher::AttachEngine3D
  Height = 20
  Placement = pos=(-19.0919,19.0919,19) rot=(0,0,1;0.785398rad)
  Radius = 1
FEATURE [Part::Cylinder] Cylinder2580  label="Válec2550"
  Angle = 360
  AttacherType = Attacher::AttachEngine3D
  Height = 2
  Placement = pos=(-19.0919,-19.0919,19) rot=(0,0,1;2.35619rad)
  Radius = 2
FEATURE [Part::Cylinder] Cylinder2581  label="Válec2551"
  Angle = 360
  AttacherType = Attacher::AttachEngine3D
  Height = 2
  Placement = pos=(-19.0919,19.0919,19) rot=(0,0,1;0.785398rad)
  Radius = 2
FEATURE [Part::Cylinder] Cylinder2582  label="Válec2552"
  Angle = 360
  AttacherType = Attacher::AttachEngine3D
  Height = 20
  Placement = pos=(19.0919,19.0919,19) rot=(0,0,-1;0.785398rad)
  Radius = 1
FEATURE [Part::Cylinder] Cylinder2583  label="Válec2553"
  Angle = 360
  AttacherType = Attacher::AttachEngine3D
  Height = 20
  Placement = pos=(27,1e-14,19) rot=(0,0,-1;1.5708rad)
  Radius = 1
FEATURE [Part::Cylinder] Cylinder2584  label="Válec2554"
  Angle = 360
  AttacherType = Attacher::AttachEngine3D
  Height = 2
  Placement = pos=(19.0919,19.0919,19) rot=(0,0,-1;0.785398rad)
  Radius = 2
FEATURE [Part::Cylinder] Cylinder2585  label="Válec2555"
  Angle = 360
  AttacherType = Attacher::AttachEngine3D
  Height = 2
  Placement = pos=(-27,-4e-15,19) rot=(0,0,1;1.5708rad)
  Radius = 2
FEATURE [Part::Cylinder] Cylinder2586  label="Válec2556"
  Angle = 360
  AttacherType = Attacher::AttachEngine3D
  Height = 20
  Placement = pos=(19.0919,-19.0919,19) rot=(0,0,1;3.92699rad)
  Radius = 1
FEATURE [Part::Cylinder] Cylinder2587  label="Válec2557"
  Angle = 360
  AttacherType = Attacher::AttachEngine3D
  Height = 20
  Placement = pos=(1.1e-14,-27,19) rot=(0,0,1;3.14159rad)
  Radius = 1
FEATURE [Part::Cylinder] Cylinder2588  label="Válec2558"
  Angle = 360
  AttacherType = Attacher::AttachEngine3D
  Height = 20
  Placement = pos=(0,27,19) rot=(0,0,1;0rad)
  Radius = 1
FEATURE [Part::Cylinder] Cylinder2589  label="Válec2559"
  Angle = 360
  AttacherType = Attacher::AttachEngine3D
  Height = 2
  Placement = pos=(0,27,19) rot=(0,0,1;0rad)
  Radius = 2
FEATURE [Part::Cylinder] Cylinder2590  label="Válec2560"
  Angle = 360
  AttacherType = Attacher::AttachEngine3D
  Height = 2
  Placement = pos=(1.1e-14,-27,19) rot=(0,0,1;3.14159rad)
  Radius = 2
FEATURE [Part::Cylinder] Cylinder2591  label="Válec2561"
  Angle = 360
  AttacherType = Attacher::AttachEngine3D
  Height = 20
  Placement = pos=(-19.0919,-19.0919,19) rot=(0,0,1;2.35619rad)
  Radius = 1
FEATURE [Part::Compound] Compound1154
  Links = -> [Cylinder2588,Cylinder2579,Cylinder2578,Cylinder2591,Cylinder2587,Cylinder2586,Cylinder2583,Cylinder2582]
  Placement = pos=(0,0,-33) rot=(0,0,1;0rad)
FEATURE [Part::Cylinder] Cylinder2592  label="Válec2562"
  Angle = 360
  AttacherType = Attacher::AttachEngine3D
  Height = 2
  Placement = pos=(19.0919,-19.0919,19) rot=(0,0,1;3.92699rad)
  Radius = 2
FEATURE [Part::Cylinder] Cylinder2593  label="Válec2563"
  Angle = 360
  AttacherType = Attacher::AttachEngine3D
  Height = 2
  Placement = pos=(27,1e-14,19) rot=(0,0,-1;1.5708rad)
  Radius = 2
FEATURE [Part::Compound] Compound1156
  Links = -> [Cylinder2589,Cylinder2581,Cylinder2585,Cylinder2580,Cylinder2590,Cylinder2592,Cylinder2593,Cylinder2584]
  Placement = pos=(0,0,-20) rot=(0,0,1;0rad)
FEATURE [Part::Cut] Cut966
  Base = -> Cylinder2577
  Tool = -> Compound1156
FEATURE [Part::Cut] Cut965
  Base = -> Cut966
  Placement = pos=(46,0,10) rot=(-0.19148,-0.962637,0.19148;1.60887rad)
  Tool = -> Compound1154
FEATURE [Part::Compound] Compound1155  label="bokovadlo_rede"
  Links = -> [Cut965,Cut963]
  Placement = pos=(10,0,-36) rot=(0,-1,0;1.5708rad)
FEATURE [Part::Cylinder] Cylinder2594  label="Válec2564"
  Angle = 360
  AttacherType = Attacher::AttachEngine3D
  Height = 20
  Placement = pos=(-19.4454,19.4454,10) rot=(0,0,1;0.785398rad)
  Radius = 1.5
FEATURE [Part::Cylinder] Cylinder2595  label="Válec2565"
  Angle = 360
  AttacherType = Attacher::AttachEngine3D
  Height = 3
  Radius = 38
FEATURE [Part::Cylinder] Cylinder2596  label="Válec2566"
  Angle = 360
  AttacherType = Attacher::AttachEngine3D
  Height = 34
  Placement = pos=(0,0,-21) rot=(0,0,1;0rad)
  Radius = 14
FEATURE [Part::Cylinder] Cylinder2597  label="Válec2567"
  Angle = 360
  AttacherType = Attacher::AttachEngine3D
  Height = 20
  Placement = pos=(19.4454,19.4454,10) rot=(0,0,-1;0.785398rad)
  Radius = 1.5
FEATURE [Part::Cylinder] Cylinder2598  label="Válec2568"
  Angle = 360
  AttacherType = Attacher::AttachEngine3D
  Height = 20
  Placement = pos=(27.5,1.2e-14,10) rot=(0,0,-1;1.5708rad)
  Radius = 1.5
FEATURE [Part::Cylinder] Cylinder2599  label="Válec2569"
  Angle = 360
  AttacherType = Attacher::AttachEngine3D
  Height = 20
  Placement = pos=(1.1e-14,-27.5,10) rot=(0,0,1;3.14159rad)
  Radius = 1.5
FEATURE [Part::Cylinder] Cylinder2600  label="Válec2570"
  Angle = 360
  AttacherType = Attacher::AttachEngine3D
  Height = 20
  Placement = pos=(19.4454,-19.4454,10) rot=(0,0,1;3.92699rad)
  Radius = 1.5
FEATURE [Part::Cylinder] Cylinder2601  label="Válec2571"
  Angle = 360
  AttacherType = Attacher::AttachEngine3D
  Height = 20
  Placement = pos=(-19.4454,-19.4454,10) rot=(0,0,1;2.35619rad)
  Radius = 1.5
FEATURE [Part::Cylinder] Cylinder2602  label="Válec2572"
  Angle = 360
  AttacherType = Attacher::AttachEngine3D
  Height = 20
  Placement = pos=(-27.5,-4e-15,10) rot=(0,0,1;1.5708rad)
  Radius = 1.5
FEATURE [Part::Cylinder] Cylinder2603  label="Válec2573"
  Angle = 360
  AttacherType = Attacher::AttachEngine3D
  Height = 20
  Placement = pos=(0,27.5,10) rot=(0,0,1;0rad)
  Radius = 1.5
FEATURE [Part::Cut] Cut967
  Base = -> Cylinder2595
  Placement = pos=(0,0,10) rot=(0,0,1;0rad)
  Tool = -> Cylinder2596
FEATURE [Part::Chamfer] Chamfer116  label="J-mini_encoder-belt-ring_front004"
  Base = -> Cut967
  Edges = 1 edges r=1: [Edge3]
  Placement = pos=(0,0,-8) rot=(0,0,1;0rad)
FEATURE [Part::Compound] Compound1158
  Links = -> [Cylinder2603,Cylinder2594,Cylinder2602,Cylinder2601,Cylinder2599,Cylinder2598,Cylinder2600,Cylinder2597]
  Placement = pos=(0,0,-16) rot=(0,0,1;0.392699rad)
FEATURE [Part::Cut] Cut968  label="J-mini_encoder-belt-ring_front003"
  Base = -> Chamfer116
  Tool = -> Compound1158
FEATURE [Part::FeaturePython] Tube113  # WARN: FeaturePython — macro-defined, semantics opaque (R4)
  AttacherType = Attacher::AttachEngine3D
  Height = 4
  InnerRadius = 14
  OuterRadius = 18
  Placement = pos=(0,0,1) rot=(0,0,1;0rad)
FEATURE [Part::Chamfer] Chamfer115
  Base = -> Tube113
  Edges = 1 edges r=1: [Edge5]
FEATURE [Part::Compound] Compound1157  label="J-mini_encoder-belt-ring_front"
  Links = -> [Cut968,Chamfer115]
FEATURE [Part::Cylinder] Cylinder2608  label="Válec2578"
  Angle = 360
  AttacherType = Attacher::AttachEngine3D
  Height = 3
  Placement = pos=(1.1e-14,-27.5,19) rot=(0,0,1;3.14159rad)
  Radius = 3
FEATURE [Part::Cylinder] Cylinder2607  label="Válec2577"
  Angle = 360
  AttacherType = Attacher::AttachEngine3D
  Height = 3
  Placement = pos=(-19.4454,-19.4454,19) rot=(0,0,1;2.35619rad)
  Radius = 3
FEATURE [Part::Cylinder] Cylinder2613  label="Válec2583"
  Angle = 360
  AttacherType = Attacher::AttachEngine3D
  Height = 20
  Placement = pos=(-19.4454,19.4454,19) rot=(0,0,1;0.785398rad)
  Radius = 1.5
FEATURE [Part::Cylinder] Cylinder2615  label="Válec2585"
  Angle = 360
  AttacherType = Attacher::AttachEngine3D
  Height = 20
  Placement = pos=(-19.4454,-19.4454,19) rot=(0,0,1;2.35619rad)
  Radius = 1.5
FEATURE [Part::Cylinder] Cylinder2617  label="Válec2587"
  Angle = 360
  AttacherType = Attacher::AttachEngine3D
  Height = 20
  Placement = pos=(19.4454,-19.4454,19) rot=(0,0,1;3.92699rad)
  Radius = 1.5
FEATURE [Part::Cylinder] Cylinder2605  label="Válec2575"
  Angle = 360
  AttacherType = Attacher::AttachEngine3D
  Height = 3
  Placement = pos=(-19.4454,19.4454,19) rot=(0,0,1;0.785398rad)
  Radius = 3
FEATURE [Part::Cylinder] Cylinder2606  label="Válec2576"
  Angle = 360
  AttacherType = Attacher::AttachEngine3D
  Height = 3
  Placement = pos=(-27.5,-4e-15,19) rot=(0,0,1;1.5708rad)
  Radius = 3
FEATURE [Part::Cylinder] Cylinder2609  label="Válec2579"
  Angle = 360
  AttacherType = Attacher::AttachEngine3D
  Height = 3
  Placement = pos=(19.4454,-19.4454,19) rot=(0,0,1;3.92699rad)
  Radius = 3
FEATURE [Part::Cylinder] Cylinder2610  label="Válec2580"
  Angle = 360
  AttacherType = Attacher::AttachEngine3D
  Height = 3
  Placement = pos=(27.5,1.2e-14,19) rot=(0,0,-1;1.5708rad)
  Radius = 3
FEATURE [Part::Cylinder] Cylinder2611  label="Válec2581"
  Angle = 360
  AttacherType = Attacher::AttachEngine3D
  Height = 3
  Placement = pos=(19.4454,19.4454,19) rot=(0,0,-1;0.785398rad)
  Radius = 3
FEATURE [Part::Cylinder] Cylinder2614  label="Válec2584"
  Angle = 360
  AttacherType = Attacher::AttachEngine3D
  Height = 20
  Placement = pos=(-27.5,-4e-15,19) rot=(0,0,1;1.5708rad)
  Radius = 1.5
FEATURE [Part::Cylinder] Cylinder2616  label="Válec2586"
  Angle = 360
  AttacherType = Attacher::AttachEngine3D
  Height = 20
  Placement = pos=(1.1e-14,-27.5,19) rot=(0,0,1;3.14159rad)
  Radius = 1.5
FEATURE [Part::Cylinder] Cylinder2031  label="Válec2031"
  Angle = 360
  AttacherType = Attacher::AttachEngine3D
  Height = 30
  Placement = pos=(51,-30,0) rot=(0,0,1;0rad)
  Radius = 1.5
FEATURE [Part::Cylinder] Cylinder2014  label="Válec2014"
  Angle = 360
  AttacherType = Attacher::AttachEngine3D
  Height = 3
  Placement = pos=(0,27.5,19) rot=(0,0,1;0rad)
  Radius = 3
FEATURE [Part::Cylinder] Cylinder2619  label="Válec2589"
  Angle = 360
  AttacherType = Attacher::AttachEngine3D
  Height = 20
  Placement = pos=(19.4454,19.4454,19) rot=(0,0,-1;0.785398rad)
  Radius = 1.5
FEATURE [Part::Cylinder] Cylinder2618  label="Válec2588"
  Angle = 360
  AttacherType = Attacher::AttachEngine3D
  Height = 20
  Placement = pos=(27.5,1.2e-14,19) rot=(0,0,-1;1.5708rad)
  Radius = 1.5
FEATURE [Part::Cylinder] Cylinder2016  label="Válec2016"
  Angle = 360
  AttacherType = Attacher::AttachEngine3D
  Height = 6
  Radius = 38
FEATURE [Part::Cylinder] Cylinder2023  label="Válec2023"
  Angle = 360
  AttacherType = Attacher::AttachEngine3D
  Height = 20
  Placement = pos=(0,27.5,19) rot=(0,0,1;0rad)
  Radius = 1.5
FEATURE [Part::Box] Box790  label="Krychle789"
  AttacherType = Attacher::AttachEngine3D
  Height = 80
  Length = 12
  Placement = pos=(-6,25,-48) rot=(0,0,1;0rad)
  Width = 10
FEATURE [Part::Cylinder] Cylinder2035  label="Válec2035"
  Angle = 360
  AttacherType = Attacher::AttachEngine3D
  Height = 30
  Placement = pos=(51,16,0) rot=(0,0,1;0rad)
  Radius = 1.5
FEATURE [Part::Cylinder] Cylinder2033  label="Válec2033"
  Angle = 360
  AttacherType = Attacher::AttachEngine3D
  Height = 11
  Placement = pos=(44,0,10) rot=(0,1,0;1.5708rad)
  Radius = 38
FEATURE [Part::Box] Box796  label="Krychle795"
  AttacherType = Attacher::AttachEngine3D
  Height = 2
  Length = 8
  Placement = pos=(48,-33,7) rot=(0,0,1;0rad)
  Width = 6
FEATURE [Part::Box] Box793  label="Krychle792"
  AttacherType = Attacher::AttachEngine3D
  Height = 2
  Length = 8
  Placement = pos=(48,-3,11) rot=(0,0,1;0rad)
  Width = 6
FEATURE [Part::Cylinder] Cylinder2030  label="Válec2030"
  Angle = 360
  AttacherType = Attacher::AttachEngine3D
  Height = 5
  Placement = pos=(0,0,1) rot=(0,0,1;0rad)
  Radius = 14
FEATURE [Part::Box] Box792  label="Krychle791"
  AttacherType = Attacher::AttachEngine3D
  Height = 2
  Length = 8
  Placement = pos=(48,-3,7) rot=(0,0,1;0rad)
  Width = 6
FEATURE [Part::Box] Box794  label="Krychle793"
  AttacherType = Attacher::AttachEngine3D
  Height = 2
  Length = 8
  Placement = pos=(48,27,11) rot=(0,0,1;0rad)
  Width = 6
FEATURE [Part::Cylinder] Cylinder2034  label="Válec2034"
  Angle = 360
  AttacherType = Attacher::AttachEngine3D
  Height = 30
  Placement = pos=(51,30,0) rot=(0,0,1;0rad)
  Radius = 1.5
FEATURE [Part::Box] Box795  label="Krychle794"
  AttacherType = Attacher::AttachEngine3D
  Height = 2
  Length = 8
  Placement = pos=(48,-33,11) rot=(0,0,1;0rad)
  Width = 6
FEATURE [Part::Box] Box798  label="Krychle797"
  AttacherType = Attacher::AttachEngine3D
  Height = 2
  Length = 8
  Placement = pos=(48,27,7) rot=(0,0,1;0rad)
  Width = 6
FEATURE [Part::Box] Box797  label="Krychle796"
  AttacherType = Attacher::AttachEngine3D
  Height = 2
  Length = 8
  Placement = pos=(48,27,11) rot=(0,0,1;0rad)
  Width = 6
FEATURE [Part::Cylinder] Cylinder2032  label="Válec2032"
  Angle = 360
  AttacherType = Attacher::AttachEngine3D
  Height = 30
  Placement = pos=(51,0,0) rot=(0,0,1;0rad)
  Radius = 1.5
FEATURE [Part::Box] Box789  label="Krychle788"
  AttacherType = Attacher::AttachEngine3D
  Height = 2
  Length = 8
  Placement = pos=(48,27,7) rot=(0,0,1;0rad)
  Width = 6
FEATURE [Part::Compound] Compound902
  Links = -> [Cylinder2023,Cylinder2613,Cylinder2614,Cylinder2615,Cylinder2616,Cylinder2617,Cylinder2618,Cylinder2619]
  Placement = pos=(0,0,-23) rot=(0,0,1;0rad)
FEATURE [Part::Compound] Compound905
  Links = -> [Cylinder2031,Cylinder2032,Cylinder2034,Cylinder2035]
FEATURE [Part::Compound] Compound1160
  Links = -> [Box790]
  Placement = pos=(80,-8,10) rot=(0.57735,-0.57735,0.57735;2.0944rad)
FEATURE [Part::Compound] Compound901
  Links = -> [Cylinder2014,Cylinder2605,Cylinder2606,Cylinder2607,Cylinder2608,Cylinder2609,Cylinder2610,Cylinder2611]
  Placement = pos=(0,0,-19) rot=(0,0,1;0rad)
FEATURE [Part::Compound] Compound1159
  Links = -> [Box797,Box798]
  Placement = pos=(0,-14,0) rot=(0,0,1;0rad)
FEATURE [Part::Compound] Compound903
  Links = -> [Box792,Box793,Box795,Box796,Box794,Box789,Compound1159]
FEATURE [Part::FeaturePython] Tube114  # WARN: FeaturePython — macro-defined, semantics opaque (R4)
  AttacherType = Attacher::AttachEngine3D
  Height = 1
  InnerRadius = 12
  OuterRadius = 14
  Placement = pos=(0,0,1) rot=(0,0,1;0rad)
FEATURE [Part::Common] Common005
  Base = -> Compound1160
  Tool = -> Cylinder2033
FEATURE [Part::Cut] Cut626
  Base = -> Common005
  Tool = -> Compound903
FEATURE [Part::Cut] Cut623
  Base = -> Cylinder2016
  Tool = -> Compound901
FEATURE [Part::Cut] Cut624
  Base = -> Cut623
  Tool = -> Compound902
FEATURE [Part::Cut] Cut625
  Base = -> Cut624
  Tool = -> Cylinder2030
FEATURE [Part::Chamfer] Chamfer117
  Base = -> Cut625
  Edges = 1 edges r=1: [Edge3]
FEATURE [Part::Cut] Cut627
  Base = -> Cut626
  Placement = pos=(-9.2388,-3.82683,46) rot=(-0.19148,0.962637,0.19148;1.60887rad)
  Tool = -> Compound905
FEATURE [Part::Compound] Compound907  label="J-mini_wrist-side-rotator"
  Links = -> [Tube114,Cut627,Chamfer117]
  Placement = pos=(0,0,11) rot=(1,0,0;3.14159rad)
FEATURE [Mesh::Feature] Mesh014  label="J-mini_wrist-side-rotator (Meshed)"
FEATURE [Part::Cylinder] Cylinder2212  label="Válec2212"
  Angle = 360
  AttacherType = Attacher::AttachEngine3D
  Height = 4
  Placement = pos=(0,-160,-69) rot=(0,0,1;0rad)
  Radius = 40
FEATURE [Part::Cylinder] Cylinder2214  label="Válec2214"
  Angle = 360
  AttacherType = Attacher::AttachEngine3D
  Height = 40
  Placement = pos=(16,-190,-70) rot=(0,0,1;0rad)
  Radius = 1.5
FEATURE [Part::Cylinder] Cylinder2215  label="Válec2215"
  Angle = 360
  AttacherType = Attacher::AttachEngine3D
  Height = 40
  Placement = pos=(16,-160,-70) rot=(0,0,1;0rad)
  Radius = 1.5
FEATURE [Part::Cylinder] Cylinder2216  label="Válec2216"
  Angle = 360
  AttacherType = Attacher::AttachEngine3D
  Height = 40
  Placement = pos=(37,-130,-70) rot=(0,0,1;0rad)
  Radius = 1.5
FEATURE [Part::Cylinder] Cylinder2217  label="Válec2217"
  Angle = 360
  AttacherType = Attacher::AttachEngine3D
  Height = 40
  Placement = pos=(37,-160,-70) rot=(0,0,1;0rad)
  Radius = 1.5
FEATURE [Part::Cylinder] Cylinder2218  label="Válec2218"
  Angle = 360
  AttacherType = Attacher::AttachEngine3D
  Height = 40
  Placement = pos=(-16,-130,-70) rot=(0,0,1;0rad)
  Radius = 1.5
FEATURE [Part::Cylinder] Cylinder2219  label="Válec2219"
  Angle = 360
  AttacherType = Attacher::AttachEngine3D
  Height = 40
  Placement = pos=(-16,-190,-70) rot=(0,0,1;0rad)
  Radius = 1.5
FEATURE [Part::Box] Box899  label="Krychle898"
  AttacherType = Attacher::AttachEngine3D
  Height = 4
  Length = 80
  Placement = pos=(-40,-160,-69) rot=(0,0,1;0rad)
  Width = 40
FEATURE [Part::Cylinder] Cylinder2213  label="Válec2213"
  Angle = 360
  AttacherType = Attacher::AttachEngine3D
  Height = 40
  Placement = pos=(16,-130,-70) rot=(0,0,1;0rad)
  Radius = 1.5
FEATURE [Part::Cylinder] Cylinder2222  label="Válec2222"
  Angle = 360
  AttacherType = Attacher::AttachEngine3D
  Height = 40
  Placement = pos=(-37,-160,-70) rot=(0,0,1;0rad)
  Radius = 1.5
FEATURE [Part::Cylinder] Cylinder2220  label="Válec2220"
  Angle = 360
  AttacherType = Attacher::AttachEngine3D
  Height = 40
  Placement = pos=(-16,-160,-70) rot=(0,0,1;0rad)
  Radius = 1.5
FEATURE [Part::Cylinder] Cylinder2221  label="Válec2221"
  Angle = 360
  AttacherType = Attacher::AttachEngine3D
  Height = 40
  Placement = pos=(-37,-130,-70) rot=(0,0,1;0rad)
  Radius = 1.5
FEATURE [Part::Cylinder] Cylinder2233  label="Válec2233"
  Angle = 360
  AttacherType = Attacher::AttachEngine3D
  Height = 3
  Placement = pos=(16,-130,-70) rot=(0,0,1;0rad)
  Radius = 3
FEATURE [Part::Cylinder] Cylinder2239  label="Válec2239"
  Angle = 360
  AttacherType = Attacher::AttachEngine3D
  Height = 3
  Placement = pos=(-16,-190,-70) rot=(0,0,1;0rad)
  Radius = 3
FEATURE [Part::Cylinder] Cylinder2231  label="Válec2231"
  Angle = 360
  AttacherType = Attacher::AttachEngine3D
  Height = 40
  Placement = pos=(-37,-130,-70) rot=(0,0,1;0rad)
  Radius = 1.5
FEATURE [Part::Cylinder] Cylinder2227  label="Válec2227"
  Angle = 360
  AttacherType = Attacher::AttachEngine3D
  Height = 40
  Placement = pos=(37,-160,-70) rot=(0,0,1;0rad)
  Radius = 1.5
FEATURE [Part::Cylinder] Cylinder2228  label="Válec2228"
  Angle = 360
  AttacherType = Attacher::AttachEngine3D
  Height = 40
  Placement = pos=(-16,-130,-70) rot=(0,0,1;0rad)
  Radius = 1.5
FEATURE [Part::Cylinder] Cylinder2223  label="Válec2223"
  Angle = 360
  AttacherType = Attacher::AttachEngine3D
  Height = 40
  Placement = pos=(16,-130,-70) rot=(0,0,1;0rad)
  Radius = 1.5
FEATURE [Part::Cylinder] Cylinder2224  label="Válec2224"
  Angle = 360
  AttacherType = Attacher::AttachEngine3D
  Height = 40
  Placement = pos=(16,-190,-70) rot=(0,0,1;0rad)
  Radius = 1.5
FEATURE [Part::Cylinder] Cylinder2226  label="Válec2226"
  Angle = 360
  AttacherType = Attacher::AttachEngine3D
  Height = 40
  Placement = pos=(37,-130,-70) rot=(0,0,1;0rad)
  Radius = 1.5
FEATURE [Part::Cylinder] Cylinder2229  label="Válec2229"
  Angle = 360
  AttacherType = Attacher::AttachEngine3D
  Height = 40
  Placement = pos=(-16,-190,-70) rot=(0,0,1;0rad)
  Radius = 1.5
FEATURE [Part::Cylinder] Cylinder2235  label="Válec2235"
  Angle = 360
  AttacherType = Attacher::AttachEngine3D
  Height = 3
  Placement = pos=(16,-160,-70) rot=(0,0,1;0rad)
  Radius = 3
FEATURE [Part::Cylinder] Cylinder2225  label="Válec2225"
  Angle = 360
  AttacherType = Attacher::AttachEngine3D
  Height = 40
  Placement = pos=(16,-160,-70) rot=(0,0,1;0rad)
  Radius = 1.5
FEATURE [Part::Cylinder] Cylinder2236  label="Válec2236"
  Angle = 360
  AttacherType = Attacher::AttachEngine3D
  Height = 3
  Placement = pos=(37,-130,-70) rot=(0,0,1;0rad)
  Radius = 3
FEATURE [Part::Cylinder] Cylinder2234  label="Válec2234"
  Angle = 360
  AttacherType = Attacher::AttachEngine3D
  Height = 3
  Placement = pos=(16,-190,-70) rot=(0,0,1;0rad)
  Radius = 3
FEATURE [Part::Cylinder] Cylinder2237  label="Válec2237"
  Angle = 360
  AttacherType = Attacher::AttachEngine3D
  Height = 3
  Placement = pos=(37,-160,-70) rot=(0,0,1;0rad)
  Radius = 3
FEATURE [Part::Cylinder] Cylinder2232  label="Válec2232"
  Angle = 360
  AttacherType = Attacher::AttachEngine3D
  Height = 40
  Placement = pos=(-37,-160,-70) rot=(0,0,1;0rad)
  Radius = 1.5
FEATURE [Part::Cylinder] Cylinder2230  label="Válec2230"
  Angle = 360
  AttacherType = Attacher::AttachEngine3D
  Height = 40
  Placement = pos=(-16,-160,-70) rot=(0,0,1;0rad)
  Radius = 1.5
FEATURE [Part::Cylinder] Cylinder2238  label="Válec2238"
  Angle = 360
  AttacherType = Attacher::AttachEngine3D
  Height = 3
  Placement = pos=(-16,-130,-70) rot=(0,0,1;0rad)
  Radius = 3
FEATURE [Part::Cylinder] Cylinder2246  label="Válec2246"
  Angle = 360
  AttacherType = Attacher::AttachEngine3D
  Height = 3
  Placement = pos=(37,-130,-70) rot=(0,0,1;0rad)
  Radius = 3
FEATURE [Part::Cylinder] Cylinder2243  label="Válec2243"
  Angle = 360
  AttacherType = Attacher::AttachEngine3D
  Height = 3
  Placement = pos=(16,-130,-70) rot=(0,0,1;0rad)
  Radius = 3
FEATURE [Part::Cylinder] Cylinder2252  label="Válec2252"
  Angle = 360
  AttacherType = Attacher::AttachEngine3D
  Height = 3
  Placement = pos=(-37,-160,-70) rot=(0,0,1;0rad)
  Radius = 3
FEATURE [Part::Cylinder] Cylinder2241  label="Válec2241"
  Angle = 360
  AttacherType = Attacher::AttachEngine3D
  Height = 3
  Placement = pos=(-37,-130,-70) rot=(0,0,1;0rad)
  Radius = 3
FEATURE [Part::Cylinder] Cylinder2264  label="Válec2264"
  Angle = 360
  AttacherType = Attacher::AttachEngine3D
  Height = 20
  Placement = pos=(0,-160,20) rot=(0,0,1;0rad)
  Radius = 2
FEATURE [Part::Cylinder] Cylinder2247  label="Válec2247"
  Angle = 360
  AttacherType = Attacher::AttachEngine3D
  Height = 3
  Placement = pos=(37,-160,-70) rot=(0,0,1;0rad)
  Radius = 3
FEATURE [Part::Cylinder] Cylinder2267  label="Válec2267"
  Angle = 360
  AttacherType = Attacher::AttachEngine3D
  Height = 4
  Placement = pos=(0,-160,20) rot=(0,0,1;0rad)
  Radius = 4
FEATURE [Part::Cylinder] Cylinder2249  label="Válec2249"
  Angle = 360
  AttacherType = Attacher::AttachEngine3D
  Height = 3
  Placement = pos=(-16,-190,-70) rot=(0,0,1;0rad)
  Radius = 3
FEATURE [Part::Cylinder] Cylinder2270  label="Válec2270"
  Angle = 360
  AttacherType = Attacher::AttachEngine3D
  Height = 4
  Placement = pos=(0,-130,20) rot=(0,0,1;0rad)
  Radius = 4
FEATURE [Part::Cylinder] Cylinder2248  label="Válec2248"
  Angle = 360
  AttacherType = Attacher::AttachEngine3D
  Height = 3
  Placement = pos=(-16,-130,-70) rot=(0,0,1;0rad)
  Radius = 3
FEATURE [Part::Box] Box901  label="Krychle900"
  AttacherType = Attacher::AttachEngine3D
  Height = 30
  Length = 26
  Placement = pos=(-13,-290,-73) rot=(0,0,1;0rad)
  Width = 200
FEATURE [Part::Cylinder] Cylinder2242  label="Válec2242"
  Angle = 360
  AttacherType = Attacher::AttachEngine3D
  Height = 3
  Placement = pos=(-37,-160,-70) rot=(0,0,1;0rad)
  Radius = 3
FEATURE [Part::Box] Box900  label="Krychle899"
  AttacherType = Attacher::AttachEngine3D
  Height = 30
  Length = 26
  Placement = pos=(-13,-290,-73) rot=(0,0,1;0rad)
  Width = 200
FEATURE [Part::Cylinder] Cylinder2240  label="Válec2240"
  Angle = 360
  AttacherType = Attacher::AttachEngine3D
  Height = 3
  Placement = pos=(-16,-160,-70) rot=(0,0,1;0rad)
  Radius = 3
FEATURE [Part::Cylinder] Cylinder2244  label="Válec2244"
  Angle = 360
  AttacherType = Attacher::AttachEngine3D
  Height = 3
  Placement = pos=(16,-190,-70) rot=(0,0,1;0rad)
  Radius = 3
FEATURE [Part::Cylinder] Cylinder2245  label="Válec2245"
  Angle = 360
  AttacherType = Attacher::AttachEngine3D
  Height = 3
  Placement = pos=(16,-160,-70) rot=(0,0,1;0rad)
  Radius = 3
FEATURE [Part::Cylinder] Cylinder2250  label="Válec2250"
  Angle = 360
  AttacherType = Attacher::AttachEngine3D
  Height = 3
  Placement = pos=(-16,-160,-70) rot=(0,0,1;0rad)
  Radius = 3
FEATURE [Part::Cylinder] Cylinder2251  label="Válec2251"
  Angle = 360
  AttacherType = Attacher::AttachEngine3D
  Height = 3
  Placement = pos=(-37,-130,-70) rot=(0,0,1;0rad)
  Radius = 3
FEATURE [Part::Cylinder] Cylinder2262  label="Válec2262"
  Angle = 360
  AttacherType = Attacher::AttachEngine3D
  Height = 4
  Placement = pos=(0,-130,20) rot=(0,0,1;0rad)
  Radius = 4
FEATURE [Part::Cylinder] Cylinder2263  label="Válec2263"
  Angle = 360
  AttacherType = Attacher::AttachEngine3D
  Height = 4
  Placement = pos=(0,-160,20) rot=(0,0,1;0rad)
  Radius = 4
FEATURE [Part::Cylinder] Cylinder2265  label="Válec2265"
  Angle = 360
  AttacherType = Attacher::AttachEngine3D
  Height = 20
  Placement = pos=(0,-130,20) rot=(0,0,1;0rad)
  Radius = 2
FEATURE [Part::Cylinder] Cylinder2266  label="Válec2266"
  Angle = 360
  AttacherType = Attacher::AttachEngine3D
  Height = 4
  Placement = pos=(0,-130,20) rot=(0,0,1;0rad)
  Radius = 4
FEATURE [Part::Cylinder] Cylinder2268  label="Válec2268"
  Angle = 360
  AttacherType = Attacher::AttachEngine3D
  Height = 20
  Placement = pos=(0,-130,20) rot=(0,0,1;0rad)
  Radius = 2
FEATURE [Part::Cylinder] Cylinder2269  label="Válec2269"
  Angle = 360
  AttacherType = Attacher::AttachEngine3D
  Height = 20
  Placement = pos=(0,-160,20) rot=(0,0,1;0rad)
  Radius = 2
FEATURE [Part::Cylinder] Cylinder2274  label="Válec2274"
  Angle = 360
  AttacherType = Attacher::AttachEngine3D
  Height = 4
  Placement = pos=(0,-130,20) rot=(0,0,1;0rad)
  Radius = 4
FEATURE [Part::Cylinder] Cylinder2275  label="Válec2275"
  Angle = 360
  AttacherType = Attacher::AttachEngine3D
  Height = 4
  Placement = pos=(0,-160,20) rot=(0,0,1;0rad)
  Radius = 4
FEATURE [Part::Cylinder] Cylinder2273  label="Válec2273"
  Angle = 360
  AttacherType = Attacher::AttachEngine3D
  Height = 20
  Placement = pos=(0,-160,20) rot=(0,0,1;0rad)
  Radius = 2
FEATURE [Part::Cylinder] Cylinder2272  label="Válec2272"
  Angle = 360
  AttacherType = Attacher::AttachEngine3D
  Height = 20
  Placement = pos=(0,-130,20) rot=(0,0,1;0rad)
  Radius = 2
FEATURE [Part::Cylinder] Cylinder2277  label="Válec2277"
  Angle = 360
  AttacherType = Attacher::AttachEngine3D
  Height = 20
  Placement = pos=(0,-160,20) rot=(0,0,1;0rad)
  Radius = 2
FEATURE [Part::Cylinder] Cylinder2271  label="Válec2271"
  Angle = 360
  AttacherType = Attacher::AttachEngine3D
  Height = 4
  Placement = pos=(0,-160,20) rot=(0,0,1;0rad)
  Radius = 4
FEATURE [Part::Cylinder] Cylinder2276  label="Válec2276"
  Angle = 360
  AttacherType = Attacher::AttachEngine3D
  Height = 20
  Placement = pos=(0,-130,20) rot=(0,0,1;0rad)
  Radius = 2
FEATURE [Part::Compound] Compound980
  Links = -> [Cylinder2243,Cylinder2244,Cylinder2245,Cylinder2246,Cylinder2247,Cylinder2248,Cylinder2249,Cylinder2250,Cylinder2251,Cylinder2252]
FEATURE [Part::Compound] Compound983
  Links = -> [Cylinder2263,Cylinder2262]
  Placement = pos=(-26.5,0,-91) rot=(0,0,1;0rad)
FEATURE [Part::Compound] Compound985
  Links = -> [Cylinder2267,Cylinder2266]
  Placement = pos=(26.5,0,-91) rot=(0,0,1;0rad)
FEATURE [Part::Compound] Compound977
  Links = -> [Cylinder2213,Cylinder2214,Cylinder2215,Cylinder2216,Cylinder2217,Cylinder2218,Cylinder2219,Cylinder2220,Cylinder2221,Cylinder2222]
  Placement = pos=(0,0,-20) rot=(0,0,1;0rad)
FEATURE [Part::Cut] Cut803
  Base = -> Box899
  Tool = -> Compound977
FEATURE [Part::Cut] Cut806
  Base = -> Cut803
  Tool = -> Compound980
FEATURE [Part::Cut] Cut807
  Base = -> Cut806
  Tool = -> Box900
FEATURE [Part::Cut] Cut812
  Base = -> Cut807
  Tool = -> Compound983
FEATURE [Part::Compound] Compound984
  Links = -> [Cylinder2264,Cylinder2265]
  Placement = pos=(-26.5,0,-100) rot=(0,0,1;0rad)
FEATURE [Part::Compound] Compound989
  Links = -> [Cylinder2271,Cylinder2270]
  Placement = pos=(-26.5,0,-91) rot=(0,0,1;0rad)
FEATURE [Part::Compound] Compound990
  Links = -> [Cylinder2273,Cylinder2272]
  Placement = pos=(-26.5,0,-100) rot=(0,0,1;0rad)
FEATURE [Part::Cut] Cut815
  Base = -> Cut812
  Tool = -> Compound990
FEATURE [Part::Compound] Compound979
  Links = -> [Cylinder2233,Cylinder2234,Cylinder2235,Cylinder2236,Cylinder2237,Cylinder2238,Cylinder2239,Cylinder2240,Cylinder2241,Cylinder2242]
FEATURE [Part::Compound] Compound986
  Links = -> [Cylinder2269,Cylinder2268]
  Placement = pos=(26.5,0,-100) rot=(0,0,1;0rad)
FEATURE [Part::Compound] Compound991
  Links = -> [Cylinder2275,Cylinder2274]
  Placement = pos=(26.5,0,-91) rot=(0,0,1;0rad)
FEATURE [Part::Compound] Compound978
  Links = -> [Cylinder2223,Cylinder2224,Cylinder2225,Cylinder2226,Cylinder2227,Cylinder2228,Cylinder2229,Cylinder2230,Cylinder2231,Cylinder2232]
  Placement = pos=(0,0,-20) rot=(0,0,1;0rad)
FEATURE [Part::Cut] Cut804
  Base = -> Cylinder2212
  Tool = -> Compound978
FEATURE [Part::Cut] Cut805
  Base = -> Cut804
  Tool = -> Compound979
FEATURE [Part::Cut] Cut808
  Base = -> Cut805
  Tool = -> Box901
FEATURE [Part::Cut] Cut813
  Base = -> Cut808
  Tool = -> Compound984
FEATURE [Part::Cut] Cut814
  Base = -> Cut813
  Tool = -> Compound989
FEATURE [Part::Cut] Cut816
  Base = -> Cut814
  Tool = -> Compound986
FEATURE [Part::Cut] Cut817
  Base = -> Cut816
  Tool = -> Compound985
FEATURE [Part::Compound] Compound992
  Links = -> [Cylinder2277,Cylinder2276]
  Placement = pos=(26.5,0,-100) rot=(0,0,1;0rad)
FEATURE [Part::Cut] Cut818
  Base = -> Cut815
  Tool = -> Compound991
FEATURE [Part::Cut] Cut819
  Base = -> Cut818
  Tool = -> Compound992
FEATURE [Part::Compound] Compound993  label="L-elb_major-conno_nomoto_cover"
  Links = -> [Cut817,Cut819]
  Placement = pos=(0,0,-4) rot=(0,0,1;0rad)
FEATURE [Mesh::Feature] Mesh015  label="L-elb_major-conno_nomoto_cover (Meshed)"
FEATURE [Part::Cylinder] Cylinder2125  label="Válec2125"
  Angle = 360
  AttacherType = Attacher::AttachEngine3D
  Height = 20
  Placement = pos=(-16,-48,-60) rot=(0,0,1;0rad)
  Radius = 1.5
FEATURE [Part::Cylinder] Cylinder2127  label="Válec2127"
  Angle = 360
  AttacherType = Attacher::AttachEngine3D
  Height = 3
  Placement = pos=(-37,-48,-60) rot=(0,0,1;0rad)
  Radius = 3
FEATURE [Part::Cylinder] Cylinder2129  label="Válec2129"
  Angle = 360
  AttacherType = Attacher::AttachEngine3D
  Height = 3
  Placement = pos=(-16,-60,-60) rot=(0,0,1;0rad)
  Radius = 3
FEATURE [Part::Cylinder] Cylinder2123  label="Válec2123"
  Angle = 360
  AttacherType = Attacher::AttachEngine3D
  Height = 20
  Placement = pos=(-37,-60,-60) rot=(0,0,1;0rad)
  Radius = 1.5
FEATURE [Part::Box] Box842  label="Krychle841"
  AttacherType = Attacher::AttachEngine3D
  Height = 4
  Length = 27
  Placement = pos=(-40,-66,-60) rot=(0,0,1;0rad)
  Width = 24
FEATURE [Part::Cylinder] Cylinder2126  label="Válec2126"
  Angle = 360
  AttacherType = Attacher::AttachEngine3D
  Height = 20
  Placement = pos=(-16,-60,-60) rot=(0,0,1;0rad)
  Radius = 1.5
FEATURE [Part::Cylinder] Cylinder2124  label="Válec2124"
  Angle = 360
  AttacherType = Attacher::AttachEngine3D
  Height = 20
  Placement = pos=(-37,-48,-60) rot=(0,0,1;0rad)
  Radius = 1.5
FEATURE [Part::Cylinder] Cylinder2128  label="Válec2128"
  Angle = 360
  AttacherType = Attacher::AttachEngine3D
  Height = 3
  Placement = pos=(-37,-60,-60) rot=(0,0,1;0rad)
  Radius = 3
FEATURE [Part::Cylinder] Cylinder2131  label="Válec2131"
  Angle = 360
  AttacherType = Attacher::AttachEngine3D
  Height = 4
  Placement = pos=(-26.5,-54,-62) rot=(0,0,1;0rad)
  Radius = 4
FEATURE [Part::Cylinder] Cylinder2132  label="Válec2132"
  Angle = 360
  AttacherType = Attacher::AttachEngine3D
  Height = 20
  Placement = pos=(-26.5,-54,-68) rot=(0,0,1;0rad)
  Radius = 2
FEATURE [Part::Cylinder] Cylinder2130  label="Válec2130"
  Angle = 360
  AttacherType = Attacher::AttachEngine3D
  Height = 3
  Placement = pos=(-16,-48,-60) rot=(0,0,1;0rad)
  Radius = 3
FEATURE [Part::Compound] Compound950
  Links = -> [Cylinder2125,Cylinder2126,Cylinder2124,Cylinder2123]
  Placement = pos=(0,0,-5) rot=(0,0,1;0rad)
FEATURE [Part::Compound] Compound951
  Links = -> [Cylinder2130,Cylinder2129,Cylinder2127,Cylinder2128]
  Placement = pos=(0,0,-1) rot=(0,0,1;0rad)
FEATURE [Part::Cut] Cut771
  Base = -> Box842
  Tool = -> Compound950
FEATURE [Part::Cut] Cut772
  Base = -> Cut771
  Tool = -> Compound951
FEATURE [Part::Cut] Cut773
  Base = -> Cut772
  Tool = -> Cylinder2131
FEATURE [Part::Cut] Cut774  label="ypsilon_kryto"
  Base = -> Cut773
  Tool = -> Cylinder2132
FEATURE [Part::Cylinder] Cylinder2306  label="Válec2306"
  Angle = 360
  AttacherType = Attacher::AttachEngine3D
  Height = 20
  Placement = pos=(-16,-60,-60) rot=(0,0,1;0rad)
  Radius = 1.5
FEATURE [Part::Cylinder] Cylinder2311  label="Válec2311"
  Angle = 360
  AttacherType = Attacher::AttachEngine3D
  Height = 4
  Placement = pos=(-26.5,-54,-62) rot=(0,0,1;0rad)
  Radius = 4
FEATURE [Part::Cylinder] Cylinder2319  label="Válec2319"
  Angle = 360
  AttacherType = Attacher::AttachEngine3D
  Height = 3
  Placement = pos=(-16,-60,-60) rot=(0,0,1;0rad)
  Radius = 3
FEATURE [Part::Cylinder] Cylinder2305  label="Válec2305"
  Angle = 360
  AttacherType = Attacher::AttachEngine3D
  Height = 20
  Placement = pos=(-16,-48,-60) rot=(0,0,1;0rad)
  Radius = 1.5
FEATURE [Part::Cylinder] Cylinder2318  label="Válec2318"
  Angle = 360
  AttacherType = Attacher::AttachEngine3D
  Height = 3
  Placement = pos=(-37,-60,-60) rot=(0,0,1;0rad)
  Radius = 3
FEATURE [Part::Box] Box903  label="Krychle902"
  AttacherType = Attacher::AttachEngine3D
  Height = 4
  Length = 27
  Placement = pos=(-40,-66,-60) rot=(0,0,1;0rad)
  Width = 24
FEATURE [Part::Cylinder] Cylinder2315  label="Válec2315"
  Angle = 360
  AttacherType = Attacher::AttachEngine3D
  Height = 20
  Placement = pos=(-16,-55,-60) rot=(0,0,1;0rad)
  Radius = 1.5
FEATURE [Part::Cylinder] Cylinder2303  label="Válec2303"
  Angle = 360
  AttacherType = Attacher::AttachEngine3D
  Height = 20
  Placement = pos=(-37,-60,-60) rot=(0,0,1;0rad)
  Radius = 1.5
FEATURE [Part::Cylinder] Cylinder2307  label="Válec2307"
  Angle = 360
  AttacherType = Attacher::AttachEngine3D
  Height = 3
  Placement = pos=(-37,-48,-60) rot=(0,0,1;0rad)
  Radius = 3
FEATURE [Part::Cylinder] Cylinder2308  label="Válec2308"
  Angle = 360
  AttacherType = Attacher::AttachEngine3D
  Height = 3
  Placement = pos=(-37,-60,-60) rot=(0,0,1;0rad)
  Radius = 3
FEATURE [Part::Cylinder] Cylinder2309  label="Válec2309"
  Angle = 360
  AttacherType = Attacher::AttachEngine3D
  Height = 3
  Placement = pos=(-16,-60,-60) rot=(0,0,1;0rad)
  Radius = 3
FEATURE [Part::Cylinder] Cylinder2310  label="Válec2310"
  Angle = 360
  AttacherType = Attacher::AttachEngine3D
  Height = 3
  Placement = pos=(-16,-48,-60) rot=(0,0,1;0rad)
  Radius = 3
FEATURE [Part::Cylinder] Cylinder2312  label="Válec2312"
  Angle = 360
  AttacherType = Attacher::AttachEngine3D
  Height = 20
  Placement = pos=(-26.5,-54,-68) rot=(0,0,1;0rad)
  Radius = 2
FEATURE [Part::Cylinder] Cylinder2304  label="Válec2304"
  Angle = 360
  AttacherType = Attacher::AttachEngine3D
  Height = 20
  Placement = pos=(-37,-48,-60) rot=(0,0,1;0rad)
  Radius = 1.5
FEATURE [Part::Cylinder] Cylinder2313  label="Válec2313"
  Angle = 360
  AttacherType = Attacher::AttachEngine3D
  Height = 20
  Placement = pos=(-37,-60,-60) rot=(0,0,1;0rad)
  Radius = 1.5
FEATURE [Part::Cylinder] Cylinder2314  label="Válec2314"
  Angle = 360
  AttacherType = Attacher::AttachEngine3D
  Height = 20
  Placement = pos=(-37,-48,-60) rot=(0,0,1;0rad)
  Radius = 1.5
FEATURE [Part::Cylinder] Cylinder2316  label="Válec2316"
  Angle = 360
  AttacherType = Attacher::AttachEngine3D
  Height = 20
  Placement = pos=(-16,-60,-60) rot=(0,0,1;0rad)
  Radius = 1.5
FEATURE [Part::Cylinder] Cylinder2317  label="Válec2317"
  Angle = 360
  AttacherType = Attacher::AttachEngine3D
  Height = 3
  Placement = pos=(-37,-48,-60) rot=(0,0,1;0rad)
  Radius = 3
FEATURE [Part::Cylinder] Cylinder2321  label="Válec2321"
  Angle = 360
  AttacherType = Attacher::AttachEngine3D
  Height = 4
  Placement = pos=(-26.5,-54,-62) rot=(0,0,1;0rad)
  Radius = 4
FEATURE [Part::Cylinder] Cylinder2331  label="Válec2331"
  Angle = 360
  AttacherType = Attacher::AttachEngine3D
  Height = 4
  Placement = pos=(-26.5,-54,-62) rot=(0,0,1;0rad)
  Radius = 4
FEATURE [Part::Cylinder] Cylinder2325  label="Válec2325"
  Angle = 360
  AttacherType = Attacher::AttachEngine3D
  Height = 20
  Placement = pos=(-16,-48,-60) rot=(0,0,1;0rad)
  Radius = 1.5
FEATURE [Part::Cylinder] Cylinder2320  label="Válec2320"
  Angle = 360
  AttacherType = Attacher::AttachEngine3D
  Height = 3
  Placement = pos=(-16,-55,-60) rot=(0,0,1;0rad)
  Radius = 3
FEATURE [Part::Cylinder] Cylinder2330  label="Válec2330"
  Angle = 360
  AttacherType = Attacher::AttachEngine3D
  Height = 3
  Placement = pos=(-16,-48,-60) rot=(0,0,1;0rad)
  Radius = 3
FEATURE [Part::Cylinder] Cylinder2332  label="Válec2332"
  Angle = 360
  AttacherType = Attacher::AttachEngine3D
  Height = 20
  Placement = pos=(-26.5,-54,-68) rot=(0,0,1;0rad)
  Radius = 2
FEATURE [Part::Cylinder] Cylinder2322  label="Válec2322"
  Angle = 360
  AttacherType = Attacher::AttachEngine3D
  Height = 20
  Placement = pos=(-26.5,-54,-68) rot=(0,0,1;0rad)
  Radius = 2
FEATURE [Part::Box] Box904  label="Krychle903"
  AttacherType = Attacher::AttachEngine3D
  Height = 4
  Length = 27
  Placement = pos=(-40,-66,-60) rot=(0,0,1;0rad)
  Width = 24
FEATURE [Part::Cylinder] Cylinder2327  label="Válec2327"
  Angle = 360
  AttacherType = Attacher::AttachEngine3D
  Height = 3
  Placement = pos=(-37,-55,-60) rot=(0,0,1;0rad)
  Radius = 3
FEATURE [Part::Cylinder] Cylinder2323  label="Válec2323"
  Angle = 360
  AttacherType = Attacher::AttachEngine3D
  Height = 20
  Placement = pos=(-37,-60,-60) rot=(0,0,1;0rad)
  Radius = 1.5
FEATURE [Part::Cylinder] Cylinder2324  label="Válec2324"
  Angle = 360
  AttacherType = Attacher::AttachEngine3D
  Height = 20
  Placement = pos=(-37,-55,-60) rot=(0,0,1;0rad)
  Radius = 1.5
FEATURE [Part::Cylinder] Cylinder2329  label="Válec2329"
  Angle = 360
  AttacherType = Attacher::AttachEngine3D
  Height = 3
  Placement = pos=(-16,-60,-60) rot=(0,0,1;0rad)
  Radius = 3
FEATURE [Part::Cylinder] Cylinder2326  label="Válec2326"
  Angle = 360
  AttacherType = Attacher::AttachEngine3D
  Height = 20
  Placement = pos=(-16,-60,-60) rot=(0,0,1;0rad)
  Radius = 1.5
FEATURE [Part::Cylinder] Cylinder2328  label="Válec2328"
  Angle = 360
  AttacherType = Attacher::AttachEngine3D
  Height = 3
  Placement = pos=(-37,-60,-60) rot=(0,0,1;0rad)
  Radius = 3
FEATURE [Part::Box] Box902  label="Krychle901"
  AttacherType = Attacher::AttachEngine3D
  Height = 4
  Length = 27
  Placement = pos=(-40,-66,-60) rot=(0,0,1;0rad)
  Width = 24
FEATURE [Part::Compound] Compound1004
  Links = -> [Cylinder2310,Cylinder2309,Cylinder2307,Cylinder2308]
  Placement = pos=(0,0,-1) rot=(0,0,1;0rad)
FEATURE [Part::Compound] Compound1007
  Links = -> [Cylinder2325,Cylinder2326,Cylinder2324]
  Placement = pos=(0,0,-5) rot=(0,0,1;0rad)
FEATURE [Part::Compound] Compound1008
  Links = -> [Cylinder2330,Cylinder2329,Cylinder2327]
  Placement = pos=(0,0,-1) rot=(0,0,1;0rad)
FEATURE [Part::Chamfer] Chamfer067
  Base = -> Cut774
  Edges = 2 edges r=2: [Edge1,Edge10]
FEATURE [Part::Compound] Compound1003
  Links = -> [Cylinder2305,Cylinder2306,Cylinder2304,Cylinder2303]
  Placement = pos=(0,0,-5) rot=(0,0,1;0rad)
FEATURE [Part::Cut] Cut824
  Base = -> Box902
  Tool = -> Compound1003
FEATURE [Part::Cut] Cut825
  Base = -> Cut824
  Tool = -> Compound1004
FEATURE [Part::Cut] Cut826
  Base = -> Cut825
  Tool = -> Cylinder2311
FEATURE [Part::Cut] Cut827  label="ypsilon_kryto001"
  Base = -> Cut826
  Tool = -> Cylinder2312
FEATURE [Part::Chamfer] Chamfer070
  Base = -> Cut827
  Edges = 2 edges r=2: [Edge1,Edge10]
FEATURE [Part::Chamfer] Chamfer118
  Base = -> Chamfer070
  Edges = 1 edges r=4: [Edge22]
FEATURE [Part::Chamfer] Chamfer120  label="L-elb_xorior-cover-B"
  Base = -> Chamfer118
  Edges = 1 edges r=3: [Edge24]
  Placement = pos=(61,-4,16) rot=(0,0,1;0rad)
FEATURE [Part::Chamfer] Chamfer068
  Base = -> Chamfer067
  Edges = 1 edges r=4: [Edge6]
FEATURE [Part::Chamfer] Chamfer069  label="L-elb_xorior-cover-A"
  Base = -> Chamfer068
  Edges = 1 edges r=3: [Edge24]
  Placement = pos=(-8,-4,16) rot=(0,0,1;0rad)
FEATURE [Part::Compound] Compound1006
  Links = -> [Cylinder2320,Cylinder2317,Cylinder2318]
  Placement = pos=(0,0,-1) rot=(0,0,1;0rad)
FEATURE [Part::Compound] Compound1005
  Links = -> [Cylinder2315,Cylinder2314,Cylinder2313]
  Placement = pos=(0,0,-5) rot=(0,0,1;0rad)
FEATURE [Part::Cut] Cut832
  Base = -> Box904
  Tool = -> Compound1007
FEATURE [Part::Cut] Cut828
  Base = -> Box903
  Tool = -> Compound1005
FEATURE [Part::Cut] Cut829
  Base = -> Cut828
  Tool = -> Compound1006
FEATURE [Part::Cut] Cut830
  Base = -> Cut829
  Tool = -> Cylinder2321
FEATURE [Part::Cut] Cut831  label="ypsilon_kryto002"
  Base = -> Cut830
  Placement = pos=(0,-4,-46) rot=(0,1,0;3.14159rad)
  Tool = -> Cylinder2322
FEATURE [Part::Cut] Cut833
  Base = -> Cut832
  Tool = -> Compound1008
FEATURE [Part::Cut] Cut834
  Base = -> Cut833
  Tool = -> Cylinder2331
FEATURE [Part::Cut] Cut835  label="ypsilon_kryto003"
  Base = -> Cut834
  Placement = pos=(-53,-4,-46) rot=(0,1,0;3.14159rad)
  Tool = -> Cylinder2332
FEATURE [Part::Cylinder] Cylinder2620  label="Válec2590"
  Angle = 360
  AttacherType = Attacher::AttachEngine3D
  Height = 10
  Radius = 2
FEATURE [Part::Compound] Compound1161
  Links = -> [Cylinder2620,Cylinder2316,Cylinder2319,Cylinder2328,Cylinder2323]
FEATURE [Part::Chamfer] Chamfer124
  Base = -> Cut831
  Edges = 2 edges r=2: [Edge1,Edge10]
FEATURE [Part::Chamfer] Chamfer125  label="L-elb_xorior-cover-C"
  Base = -> Chamfer124
  Edges = 1 edges r=3: [Edge20]
FEATURE [Part::Chamfer] Chamfer126
  Base = -> Cut835
  Edges = 2 edges r=2: [Edge1,Edge8]
FEATURE [Part::Chamfer] Chamfer127  label="L-elb_xorior-cover-D"
  Base = -> Chamfer126
  Edges = 1 edges r=3: [Edge18]
FEATURE [Mesh::Feature] Mesh016  label="L-elb_xorior-cover-A (Meshed)"
FEATURE [Mesh::Feature] Mesh017  label="L-elb_xorior-cover-B (Meshed)"
FEATURE [Mesh::Feature] Mesh018  label="L-elb_xorior-cover-C (Meshed)"
FEATURE [Mesh::Feature] Mesh019  label="L-elb_xorior-cover-D (Meshed)"
FEATURE [Part::Box] Box1066  label="Krychle1065"
  AttacherType = Attacher::AttachEngine3D
  Height = 10
  Length = 64
  Placement = pos=(-32,-86,15) rot=(0,0,1;0rad)
  Width = 64
FEATURE [Part::Cylinder] Cylinder2621  label="Válec2591"
  Angle = 360
  AttacherType = Attacher::AttachEngine3D
  Height = 4
  Placement = pos=(63.64,-63.64,76) rot=(0,0,1;3.92699rad)
  Radius = 4
FEATURE [Part::Cylinder] Cylinder2622  label="Válec2592"
  Angle = 360
  AttacherType = Attacher::AttachEngine3D
  Height = 60
  Placement = pos=(18,85,-57) rot=(0,0,1;0rad)
  Radius = 1.5
FEATURE [Part::Cylinder] Cylinder2623  label="Válec2593"
  Angle = 360
  AttacherType = Attacher::AttachEngine3D
  Height = 60
  Placement = pos=(-18,95,-57) rot=(0,0,1;0rad)
  Radius = 1.5
FEATURE [Part::Cylinder] Cylinder2624  label="Válec2594"
  Angle = 360
  AttacherType = Attacher::AttachEngine3D
  Height = 60
  Placement = pos=(18,95,-57) rot=(0,0,1;0rad)
  Radius = 1.5
FEATURE [Part::Box] Box1067  label="Krychle1066"
  AttacherType = Attacher::AttachEngine3D
  Height = 2
  Length = 42
  Placement = pos=(-21,-12,34) rot=(0,0,1;0rad)
  Width = 24
FEATURE [Part::Cylinder] Cylinder2625  label="Válec2595"
  Angle = 360
  AttacherType = Attacher::AttachEngine3D
  Height = 60
  Placement = pos=(-18,85,-57) rot=(0,0,1;0rad)
  Radius = 1.5
FEATURE [Part::Cylinder] Cylinder2626  label="Válec2596"
  Angle = 360
  AttacherType = Attacher::AttachEngine3D
  Height = 4
  Placement = pos=(63.64,-63.64,64) rot=(0,0,1;3.92699rad)
  Radius = 9
FEATURE [Part::Box] Box1068  label="Krychle1067"
  AttacherType = Attacher::AttachEngine3D
  Height = 4
  Length = 28.8
  Placement = pos=(-14.4,10,24) rot=(0,0,1;0rad)
  Width = 2
FEATURE [Part::Compound] Compound1162
  Links = -> [Box1068]
  Placement = pos=(63.64,-63.64,38) rot=(0,0,1;3.92699rad)
FEATURE [Part::Compound] Compound1163
  Links = -> [Box1067]
  Placement = pos=(63.64,-63.64,42) rot=(0,0,1;3.92699rad)
FEATURE [Part::Compound] Compound1164
  Links = -> [Cylinder2624,Cylinder2622,Cylinder2625,Cylinder2623]
  Placement = pos=(0,0,100) rot=(0,0,1;3.92699rad)
FEATURE [Part::Cut] Cut970
  Base = -> Compound1163
  Placement = pos=(0,0,-10) rot=(0,0,1;0rad)
  Tool = -> Cylinder2621
FEATURE [Part::Cut] Cut971  label="Base_encoder-washer002"
  Base = -> Cut970
  Placement = pos=(0,0,-3) rot=(0,0,1;0rad)
  Tool = -> Compound1164
FEATURE [Part::Cut] Cut969
  Base = -> Cut971
  Tool = -> Compound1162
FEATURE [Part::Cut] Cut972
  Base = -> Cut969
  Tool = -> Cylinder2626
FEATURE [Part::Chamfer] Chamfer128  label="L-elb_encoder-washer001"
  Base = -> Cut972
  Edges = 2 edges r=2: [Edge3,Edge31]
  Placement = pos=(0,6,48) rot=(-0.382683,0.92388,0;3.14159rad)
FEATURE [Part::Cylinder] Cylinder1239  label="Válec1239"
  Angle = 360
  AttacherType = Attacher::AttachEngine3D
  Height = 40
  Placement = pos=(-24,-130,-70) rot=(0,0,1;0rad)
  Radius = 1.5
FEATURE [Part::Cylinder] Cylinder1233  label="Válec1233"
  Angle = 360
  AttacherType = Attacher::AttachEngine3D
  Height = 4
  Placement = pos=(0,-160,-69) rot=(0,0,1;0rad)
  Radius = 48
FEATURE [Part::Cylinder] Cylinder1242  label="Válec1242"
  Angle = 360
  AttacherType = Attacher::AttachEngine3D
  Height = 40
  Placement = pos=(-45,-130,-70) rot=(0,0,1;0rad)
  Radius = 1.5
FEATURE [Part::Cylinder] Cylinder1234  label="Válec1234"
  Angle = 360
  AttacherType = Attacher::AttachEngine3D
  Height = 40
  Placement = pos=(24,-130,-70) rot=(0,0,1;0rad)
  Radius = 1.5
FEATURE [Part::Cylinder] Cylinder1235  label="Válec1235"
  Angle = 360
  AttacherType = Attacher::AttachEngine3D
  Height = 40
  Placement = pos=(24,-190,-70) rot=(0,0,1;0rad)
  Radius = 1.5
FEATURE [Part::Cylinder] Cylinder1236  label="Válec1236"
  Angle = 360
  AttacherType = Attacher::AttachEngine3D
  Height = 40
  Placement = pos=(24,-160,-70) rot=(0,0,1;0rad)
  Radius = 1.5
FEATURE [Part::Box] Box464  label="Krychle464"
  AttacherType = Attacher::AttachEngine3D
  Height = 4
  Length = 96
  Placement = pos=(-48,-160,-69) rot=(0,0,1;0rad)
  Width = 40
FEATURE [Part::Cylinder] Cylinder1237  label="Válec1237"
  Angle = 360
  AttacherType = Attacher::AttachEngine3D
  Height = 40
  Placement = pos=(45,-130,-70) rot=(0,0,1;0rad)
  Radius = 1.5
FEATURE [Part::Cylinder] Cylinder1238  label="Válec1238"
  Angle = 360
  AttacherType = Attacher::AttachEngine3D
  Height = 40
  Placement = pos=(45,-160,-70) rot=(0,0,1;0rad)
  Radius = 1.5
FEATURE [Part::Cylinder] Cylinder1240  label="Válec1240"
  Angle = 360
  AttacherType = Attacher::AttachEngine3D
  Height = 40
  Placement = pos=(-24,-190,-70) rot=(0,0,1;0rad)
  Radius = 1.5
FEATURE [Part::Cylinder] Cylinder1241  label="Válec1241"
  Angle = 360
  AttacherType = Attacher::AttachEngine3D
  Height = 40
  Placement = pos=(-24,-160,-70) rot=(0,0,1;0rad)
  Radius = 1.5
FEATURE [Part::Cylinder] Cylinder1244  label="Válec1244"
  Angle = 360
  AttacherType = Attacher::AttachEngine3D
  Height = 40
  Placement = pos=(24,-130,-70) rot=(0,0,1;0rad)
  Radius = 1.5
FEATURE [Part::Cylinder] Cylinder1243  label="Válec1243"
  Angle = 360
  AttacherType = Attacher::AttachEngine3D
  Height = 40
  Placement = pos=(-45,-160,-70) rot=(0,0,1;0rad)
  Radius = 1.5
FEATURE [Part::Cylinder] Cylinder1246  label="Válec1246"
  Angle = 360
  AttacherType = Attacher::AttachEngine3D
  Height = 40
  Placement = pos=(24,-160,-70) rot=(0,0,1;0rad)
  Radius = 1.5
FEATURE [Part::Cylinder] Cylinder1247  label="Válec1247"
  Angle = 360
  AttacherType = Attacher::AttachEngine3D
  Height = 40
  Placement = pos=(45,-130,-70) rot=(0,0,1;0rad)
  Radius = 1.5
FEATURE [Part::Cylinder] Cylinder1245  label="Válec1245"
  Angle = 360
  AttacherType = Attacher::AttachEngine3D
  Height = 40
  Placement = pos=(24,-190,-70) rot=(0,0,1;0rad)
  Radius = 1.5
FEATURE [Part::Cylinder] Cylinder1249  label="Válec1249"
  Angle = 360
  AttacherType = Attacher::AttachEngine3D
  Height = 40
  Placement = pos=(-24,-130,-70) rot=(0,0,1;0rad)
  Radius = 1.5
FEATURE [Part::Cylinder] Cylinder1250  label="Válec1250"
  Angle = 360
  AttacherType = Attacher::AttachEngine3D
  Height = 40
  Placement = pos=(-24,-190,-70) rot=(0,0,1;0rad)
  Radius = 1.5
FEATURE [Part::Cylinder] Cylinder1248  label="Válec1248"
  Angle = 360
  AttacherType = Attacher::AttachEngine3D
  Height = 40
  Placement = pos=(45,-160,-70) rot=(0,0,1;0rad)
  Radius = 1.5
FEATURE [Part::Compound] Compound662
  Links = -> [Cylinder1234,Cylinder1235,Cylinder1236,Cylinder1237,Cylinder1238,Cylinder1239,Cylinder1240,Cylinder1241,Cylinder1242,Cylinder1243]
  Placement = pos=(0,0,-20) rot=(0,0,1;0rad)
FEATURE [Part::Cylinder] Cylinder1253  label="Válec1253"
  Angle = 360
  AttacherType = Attacher::AttachEngine3D
  Height = 40
  Placement = pos=(-45,-160,-70) rot=(0,0,1;0rad)
  Radius = 1.5
FEATURE [Part::Cylinder] Cylinder1259  label="Válec1259"
  Angle = 360
  AttacherType = Attacher::AttachEngine3D
  Height = 3
  Placement = pos=(-24,-130,-70) rot=(0,0,1;0rad)
  Radius = 3
FEATURE [Part::Cylinder] Cylinder1263  label="Válec1263"
  Angle = 360
  AttacherType = Attacher::AttachEngine3D
  Height = 3
  Placement = pos=(-45,-160,-70) rot=(0,0,1;0rad)
  Radius = 3
FEATURE [Part::Cylinder] Cylinder1255  label="Válec1255"
  Angle = 360
  AttacherType = Attacher::AttachEngine3D
  Height = 3
  Placement = pos=(24,-190,-70) rot=(0,0,1;0rad)
  Radius = 3
FEATURE [Part::Cylinder] Cylinder1256  label="Válec1256"
  Angle = 360
  AttacherType = Attacher::AttachEngine3D
  Height = 3
  Placement = pos=(24,-160,-70) rot=(0,0,1;0rad)
  Radius = 3
FEATURE [Part::Cylinder] Cylinder1257  label="Válec1257"
  Angle = 360
  AttacherType = Attacher::AttachEngine3D
  Height = 3
  Placement = pos=(45,-130,-70) rot=(0,0,1;0rad)
  Radius = 3
FEATURE [Part::Cylinder] Cylinder1260  label="Válec1260"
  Angle = 360
  AttacherType = Attacher::AttachEngine3D
  Height = 3
  Placement = pos=(-24,-190,-70) rot=(0,0,1;0rad)
  Radius = 3
FEATURE [Part::Cylinder] Cylinder1270  label="Válec1270"
  Angle = 360
  AttacherType = Attacher::AttachEngine3D
  Height = 3
  Placement = pos=(-24,-190,-70) rot=(0,0,1;0rad)
  Radius = 3
FEATURE [Part::Cylinder] Cylinder1268  label="Válec1268"
  Angle = 360
  AttacherType = Attacher::AttachEngine3D
  Height = 3
  Placement = pos=(45,-160,-70) rot=(0,0,1;0rad)
  Radius = 3
FEATURE [Part::Cylinder] Cylinder1273  label="Válec1273"
  Angle = 360
  AttacherType = Attacher::AttachEngine3D
  Height = 3
  Placement = pos=(-45,-160,-70) rot=(0,0,1;0rad)
  Radius = 3
FEATURE [Part::Box] Box466  label="Krychle466"
  AttacherType = Attacher::AttachEngine3D
  Height = 30
  Length = 42
  Placement = pos=(-21,-290,-73) rot=(0,0,1;0rad)
  Width = 200
FEATURE [Part::Box] Box718  label="Krychle717"
  AttacherType = Attacher::AttachEngine3D
  Height = 51.3
  Length = 46.3
  Placement = pos=(-23.15,-126,-121.3) rot=(0,0,1;0rad)
  Width = 6
FEATURE [Part::Cylinder] Cylinder1261  label="Válec1261"
  Angle = 360
  AttacherType = Attacher::AttachEngine3D
  Height = 3
  Placement = pos=(-24,-160,-70) rot=(0,0,1;0rad)
  Radius = 3
FEATURE [Part::Cylinder] Cylinder1252  label="Válec1252"
  Angle = 360
  AttacherType = Attacher::AttachEngine3D
  Height = 40
  Placement = pos=(-45,-130,-70) rot=(0,0,1;0rad)
  Radius = 1.5
FEATURE [Part::Cylinder] Cylinder1254  label="Válec1254"
  Angle = 360
  AttacherType = Attacher::AttachEngine3D
  Height = 3
  Placement = pos=(24,-130,-70) rot=(0,0,1;0rad)
  Radius = 3
FEATURE [Part::Cylinder] Cylinder1251  label="Válec1251"
  Angle = 360
  AttacherType = Attacher::AttachEngine3D
  Height = 40
  Placement = pos=(-24,-160,-70) rot=(0,0,1;0rad)
  Radius = 1.5
FEATURE [Part::Compound] Compound663
  Links = -> [Cylinder1244,Cylinder1245,Cylinder1246,Cylinder1247,Cylinder1248,Cylinder1249,Cylinder1250,Cylinder1251,Cylinder1252,Cylinder1253]
  Placement = pos=(0,0,-20) rot=(0,0,1;0rad)
FEATURE [Part::Cylinder] Cylinder1258  label="Válec1258"
  Angle = 360
  AttacherType = Attacher::AttachEngine3D
  Height = 3
  Placement = pos=(45,-160,-70) rot=(0,0,1;0rad)
  Radius = 3
FEATURE [Part::Cylinder] Cylinder1262  label="Válec1262"
  Angle = 360
  AttacherType = Attacher::AttachEngine3D
  Height = 3
  Placement = pos=(-45,-130,-70) rot=(0,0,1;0rad)
  Radius = 3
FEATURE [Part::Compound] Compound664
  Links = -> [Cylinder1254,Cylinder1255,Cylinder1256,Cylinder1257,Cylinder1258,Cylinder1259,Cylinder1260,Cylinder1261,Cylinder1262,Cylinder1263]
FEATURE [Part::Cylinder] Cylinder1264  label="Válec1264"
  Angle = 360
  AttacherType = Attacher::AttachEngine3D
  Height = 3
  Placement = pos=(24,-130,-70) rot=(0,0,1;0rad)
  Radius = 3
FEATURE [Part::Cylinder] Cylinder1265  label="Válec1265"
  Angle = 360
  AttacherType = Attacher::AttachEngine3D
  Height = 3
  Placement = pos=(24,-190,-70) rot=(0,0,1;0rad)
  Radius = 3
FEATURE [Part::Cylinder] Cylinder1267  label="Válec1267"
  Angle = 360
  AttacherType = Attacher::AttachEngine3D
  Height = 3
  Placement = pos=(45,-130,-70) rot=(0,0,1;0rad)
  Radius = 3
FEATURE [Part::Cylinder] Cylinder1266  label="Válec1266"
  Angle = 360
  AttacherType = Attacher::AttachEngine3D
  Height = 3
  Placement = pos=(24,-160,-70) rot=(0,0,1;0rad)
  Radius = 3
FEATURE [Part::Cylinder] Cylinder1269  label="Válec1269"
  Angle = 360
  AttacherType = Attacher::AttachEngine3D
  Height = 3
  Placement = pos=(-24,-130,-70) rot=(0,0,1;0rad)
  Radius = 3
FEATURE [Part::Cylinder] Cylinder1271  label="Válec1271"
  Angle = 360
  AttacherType = Attacher::AttachEngine3D
  Height = 3
  Placement = pos=(-24,-160,-70) rot=(0,0,1;0rad)
  Radius = 3
FEATURE [Part::Cylinder] Cylinder1272  label="Válec1272"
  Angle = 360
  AttacherType = Attacher::AttachEngine3D
  Height = 3
  Placement = pos=(-45,-130,-70) rot=(0,0,1;0rad)
  Radius = 3
FEATURE [Part::Compound] Compound665
  Links = -> [Cylinder1264,Cylinder1265,Cylinder1266,Cylinder1267,Cylinder1268,Cylinder1269,Cylinder1270,Cylinder1271,Cylinder1272,Cylinder1273]
FEATURE [Part::Box] Box465  label="Krychle465"
  AttacherType = Attacher::AttachEngine3D
  Height = 30
  Length = 42
  Placement = pos=(-21,-290,-73) rot=(0,0,1;0rad)
  Width = 200
FEATURE [Part::Box] Box716  label="Krychle715"
  AttacherType = Attacher::AttachEngine3D
  Height = 4.85
  Length = 42
  Placement = pos=(-21,-160,-74.85) rot=(0,0,1;0rad)
  Width = 34
FEATURE [Part::Cylinder] Cylinder1838  label="Válec1838"
  Angle = 360
  AttacherType = Attacher::AttachEngine3D
  Height = 20
  Placement = pos=(19.5,19.5,-28) rot=(0,0,1;0rad)
  Radius = 1.5
FEATURE [Part::Cylinder] Cylinder1844  label="Válec1844"
  Angle = 360
  AttacherType = Attacher::AttachEngine3D
  Height = 3
  Placement = pos=(-19.5,19.5,-28) rot=(0,0,1;0rad)
  Radius = 3
FEATURE [Part::Cylinder] Cylinder2627  label="Válec2597"
  Angle = 360
  AttacherType = Attacher::AttachEngine3D
  Height = 20
  Placement = pos=(0,-160,20) rot=(0,0,1;0rad)
  Radius = 2
FEATURE [Part::Cylinder] Cylinder1841  label="Válec1841"
  Angle = 360
  AttacherType = Attacher::AttachEngine3D
  Height = 20
  Placement = pos=(19.5,-19.5,-28) rot=(0,0,1;0rad)
  Radius = 1.5
FEATURE [Part::Cylinder] Cylinder2628  label="Válec2598"
  Angle = 360
  AttacherType = Attacher::AttachEngine3D
  Height = 4
  Placement = pos=(0,-160,20) rot=(0,0,1;0rad)
  Radius = 4
FEATURE [Part::Cylinder] Cylinder2629  label="Válec2599"
  Angle = 360
  AttacherType = Attacher::AttachEngine3D
  Height = 20
  Placement = pos=(0,-160,20) rot=(0,0,1;0rad)
  Radius = 2
FEATURE [Part::Cylinder] Cylinder1895  label="Válec1895"
  Angle = 360
  AttacherType = Attacher::AttachEngine3D
  Height = 20
  Placement = pos=(0,-130,20) rot=(0,0,1;0rad)
  Radius = 2
FEATURE [Part::Cylinder] Cylinder1842  label="Válec1842"
  Angle = 360
  AttacherType = Attacher::AttachEngine3D
  Height = 3
  Placement = pos=(19.5,19.5,-28) rot=(0,0,1;0rad)
  Radius = 3
FEATURE [Part::Cylinder] Cylinder1839  label="Válec1839"
  Angle = 360
  AttacherType = Attacher::AttachEngine3D
  Height = 20
  Placement = pos=(-19.5,-19.5,-28) rot=(0,0,1;0rad)
  Radius = 1.5
FEATURE [Part::Cylinder] Cylinder1845  label="Válec1845"
  Angle = 360
  AttacherType = Attacher::AttachEngine3D
  Height = 3
  Placement = pos=(19.5,-19.5,-28) rot=(0,0,1;0rad)
  Radius = 3
FEATURE [Part::Cylinder] Cylinder1893  label="Válec1893"
  Angle = 360
  AttacherType = Attacher::AttachEngine3D
  Height = 4
  Placement = pos=(0,-160,20) rot=(0,0,1;0rad)
  Radius = 4
FEATURE [Part::Cylinder] Cylinder1892  label="Válec1892"
  Angle = 360
  AttacherType = Attacher::AttachEngine3D
  Height = 4
  Placement = pos=(0,-130,20) rot=(0,0,1;0rad)
  Radius = 4
FEATURE [Part::Compound] Compound1165
  Links = -> [Cylinder1893,Cylinder1892]
  Placement = pos=(-34.5,0,-91) rot=(0,0,1;0rad)
FEATURE [Part::Cylinder] Cylinder1840  label="Válec1840"
  Angle = 360
  AttacherType = Attacher::AttachEngine3D
  Height = 20
  Placement = pos=(-19.5,19.5,-28) rot=(0,0,1;0rad)
  Radius = 1.5
FEATURE [Part::Compound] Compound1167
  Links = -> [Cylinder1839,Cylinder1840,Cylinder1841,Cylinder1838]
  Placement = pos=(0,-140,-98) rot=(1,0,0;1.5708rad)
FEATURE [Part::Cylinder] Cylinder1846  label="Válec1846"
  Angle = 360
  AttacherType = Attacher::AttachEngine3D
  Height = 50
  Placement = pos=(0,-140,-98) rot=(-1,0,0;1.5708rad)
  Radius = 10
FEATURE [Part::Cylinder] Cylinder1843  label="Válec1843"
  Angle = 360
  AttacherType = Attacher::AttachEngine3D
  Height = 3
  Placement = pos=(-19.5,-19.5,-28) rot=(0,0,1;0rad)
  Radius = 3
FEATURE [Part::Compound] Compound834
  Links = -> [Cylinder1843,Cylinder1844,Cylinder1845,Cylinder1842]
  Placement = pos=(0,-148,-98) rot=(1,0,0;1.5708rad)
FEATURE [Part::Cylinder] Cylinder2630  label="Válec2600"
  Angle = 360
  AttacherType = Attacher::AttachEngine3D
  Height = 4
  Placement = pos=(0,-130,20) rot=(0,0,1;0rad)
  Radius = 4
FEATURE [Part::Cylinder] Cylinder1894  label="Válec1894"
  Angle = 360
  AttacherType = Attacher::AttachEngine3D
  Height = 20
  Placement = pos=(0,-160,20) rot=(0,0,1;0rad)
  Radius = 2
FEATURE [Part::Compound] Compound1166
  Links = -> [Cylinder1894,Cylinder1895]
  Placement = pos=(-34.5,0,-100) rot=(0,0,1;0rad)
FEATURE [Part::Cylinder] Cylinder2631  label="Válec2601"
  Angle = 360
  AttacherType = Attacher::AttachEngine3D
  Height = 20
  Placement = pos=(0,-130,20) rot=(0,0,1;0rad)
  Radius = 2
FEATURE [Part::Cylinder] Cylinder2632  label="Válec2602"
  Angle = 360
  AttacherType = Attacher::AttachEngine3D
  Height = 4
  Placement = pos=(0,-130,20) rot=(0,0,1;0rad)
  Radius = 4
FEATURE [Part::Cylinder] Cylinder2633  label="Válec2603"
  Angle = 360
  AttacherType = Attacher::AttachEngine3D
  Height = 4
  Placement = pos=(0,-160,20) rot=(0,0,1;0rad)
  Radius = 4
FEATURE [Part::Cylinder] Cylinder2634  label="Válec2604"
  Angle = 360
  AttacherType = Attacher::AttachEngine3D
  Height = 20
  Placement = pos=(0,-130,20) rot=(0,0,1;0rad)
  Radius = 2
FEATURE [Part::Box] Box898  label="Krychle897"
  AttacherType = Attacher::AttachEngine3D
  Height = 25
  Length = 96
  Placement = pos=(-48,-120,-80) rot=(0,0,1;0rad)
  Width = 40
FEATURE [Part::Cylinder] Cylinder2635  label="Válec2605"
  Angle = 360
  AttacherType = Attacher::AttachEngine3D
  Height = 4
  Placement = pos=(0,-130,20) rot=(0,0,1;0rad)
  Radius = 4
FEATURE [Part::Cylinder] Cylinder2636  label="Válec2606"
  Angle = 360
  AttacherType = Attacher::AttachEngine3D
  Height = 20
  Placement = pos=(0,-130,20) rot=(0,0,1;0rad)
  Radius = 2
FEATURE [Part::Cylinder] Cylinder2637  label="Válec2607"
  Angle = 360
  AttacherType = Attacher::AttachEngine3D
  Height = 4
  Placement = pos=(0,-160,20) rot=(0,0,1;0rad)
  Radius = 4
FEATURE [Part::Box] Box760  label="Krychle759"
  AttacherType = Attacher::AttachEngine3D
  Height = 10
  Length = 10
  Placement = pos=(23,-126,-83) rot=(0,0,1;0rad)
  Width = 6
FEATURE [Part::Cylinder] Cylinder2638  label="Válec2608"
  Angle = 360
  AttacherType = Attacher::AttachEngine3D
  Height = 20
  Placement = pos=(0,-160,20) rot=(0,0,1;0rad)
  Radius = 2
FEATURE [Part::Box] Box761  label="Krychle760"
  AttacherType = Attacher::AttachEngine3D
  Height = 10
  Length = 10
  Placement = pos=(-33,-126,-83) rot=(0,0,1;0rad)
  Width = 6
FEATURE [Part::Cut] Cut665
  Base = -> Box718
  Tool = -> Compound834
FEATURE [Part::Cut] Cut666
  Base = -> Cut665
  Tool = -> Compound1167
FEATURE [Part::Cut] Cut667
  Base = -> Cut666
  Tool = -> Cylinder1846
FEATURE [Part::Cut] Cut462
  Base = -> Box464
  Tool = -> Compound662
FEATURE [Part::Cut] Cut463
  Base = -> Cylinder1233
  Tool = -> Compound663
FEATURE [Part::Cut] Cut464
  Base = -> Cut463
  Tool = -> Compound664
FEATURE [Part::Cut] Cut467
  Base = -> Cut464
  Tool = -> Box466
FEATURE [Part::Cut] Cut465
  Base = -> Cut462
  Tool = -> Compound665
FEATURE [Part::Cut] Cut466
  Base = -> Cut465
  Tool = -> Box465
FEATURE [Part::Cut] Cut690
  Base = -> Cut466
  Tool = -> Compound1165
FEATURE [Part::Chamfer] Chamfer063
  Base = -> Box761
  Edges = 1 edges r=6: [Edge4]
FEATURE [Part::FeaturePython] Tube078  label="kruza"  # WARN: FeaturePython — macro-defined, semantics opaque (R4)
  AttacherType = Attacher::AttachEngine3D
  Height = 1
  InnerRadius = 10
  OuterRadius = 11
  Placement = pos=(0,-119,-98) rot=(1,0,0;1.5708rad)
FEATURE [Part::Cut] Cut691
  Base = -> Cut467
  Tool = -> Compound1166
FEATURE [Part::Chamfer] Chamfer062
  Base = -> Box760
  Edges = 1 edges r=6: [Edge8]
FEATURE [Part::Compound] Compound881
  Links = -> [Chamfer062,Chamfer063]
FEATURE [Part::Compound] Compound1168
  Links = -> [Cylinder2633,Cylinder2632]
  Placement = pos=(-34.5,0,-91) rot=(0,0,1;0rad)
FEATURE [Part::Cut] Cut973
  Base = -> Cut691
  Tool = -> Compound1168
FEATURE [Part::Compound] Compound857
  Links = -> [Cylinder2628,Cylinder2630]
  Placement = pos=(34.5,0,-91) rot=(0,0,1;0rad)
FEATURE [Part::Compound] Compound1169
  Links = -> [Cylinder2629,Cylinder2634]
  Placement = pos=(-34.5,0,-100) rot=(0,0,1;0rad)
FEATURE [Part::Cut] Cut974
  Base = -> Cut690
  Tool = -> Compound1169
FEATURE [Part::Compound] Compound858
  Links = -> [Cylinder2627,Cylinder2631]
  Placement = pos=(34.5,0,-100) rot=(0,0,1;0rad)
FEATURE [Part::Cut] Cut694
  Base = -> Cut973
  Tool = -> Compound858
FEATURE [Part::Cut] Cut695
  Base = -> Cut694
  Tool = -> Compound857
FEATURE [Part::Compound] Compound1170
  Links = -> [Cylinder2637,Cylinder2635]
  Placement = pos=(34.5,0,-91) rot=(0,0,1;0rad)
FEATURE [Part::Cut] Cut696
  Base = -> Cut974
  Tool = -> Compound1170
FEATURE [Part::Compound] Compound1171
  Links = -> [Cylinder2638,Cylinder2636]
  Placement = pos=(34.5,0,-100) rot=(0,0,1;0rad)
FEATURE [Part::Cut] Cut697
  Base = -> Cut696
  Placement = pos=(0,0,-4) rot=(0,0,1;0rad)
  Tool = -> Compound1171
FEATURE [Part::Compound] Compound859
  Links = -> [Cut667,Tube078]
FEATURE [Part::Compound] Compound860  label="moto_bokohold"
  Links = -> [Compound859,Box716]
FEATURE [Part::Chamfer] Chamfer056
  Base = -> Compound860
  Edges = 1 edges r=3: [Edge55]
FEATURE [Part::Chamfer] Chamfer057
  Base = -> Chamfer056
  Edges = 2 edges r=2: [Edge19,Edge37]
  Placement = pos=(0,0,1) rot=(0,0,1;0rad)
FEATURE [Part::Cylinder] Cylinder2338  label="Válec2338"
  Angle = 360
  AttacherType = Attacher::AttachEngine3D
  Height = 32
  Placement = pos=(0,-140,-74) rot=(0,0,1;0rad)
  Radius = 60
FEATURE [Part::Common] Common006
  Base = -> Cut695
  Tool = -> Cylinder2338
FEATURE [Part::Cut] Cut842
  Base = -> Common006
  Placement = pos=(0,0,-4) rot=(0,0,1;0rad)
  Tool = -> Box898
FEATURE [Part::Fillet] Fillet007
  Base = -> Cut842
  Edges = 2 edges r=36: [Edge2,Edge68]
FEATURE [Part::Compound] Compound1018  label="L-elb_major-moto-cavo-old"
  Links = -> [Cut697,Fillet007,Chamfer057,Compound881]
  Placement = pos=(0,92,29) rot=(0,0,1;0rad)
FEATURE [Part::Compound] Compound1173
  Placement = pos=(0,-146,-98) rot=(1,0,0;1.5708rad)
FEATURE [Part::Cylinder] Cylinder2639  label="Válec2609"
  Angle = 360
  AttacherType = Attacher::AttachEngine3D
  Height = 3
  Placement = pos=(-24,-130,-70) rot=(0,0,1;0rad)
  Radius = 3
FEATURE [Part::Cylinder] Cylinder2640  label="Válec2610"
  Angle = 360
  AttacherType = Attacher::AttachEngine3D
  Height = 40
  Placement = pos=(-24,-130,-70) rot=(0,0,1;0rad)
  Radius = 1.5
FEATURE [Part::Cylinder] Cylinder2641  label="Válec2611"
  Angle = 360
  AttacherType = Attacher::AttachEngine3D
  Height = 3
  Placement = pos=(-19.5,-19.5,-28) rot=(0,0,1;0rad)
  Radius = 3
FEATURE [Part::Cylinder] Cylinder2642  label="Válec2612"
  Angle = 360
  AttacherType = Attacher::AttachEngine3D
  Height = 40
  Placement = pos=(24,-190,-70) rot=(0,0,1;0rad)
  Radius = 1.5
FEATURE [Part::Cylinder] Cylinder2643  label="Válec2613"
  Angle = 360
  AttacherType = Attacher::AttachEngine3D
  Height = 3
  Placement = pos=(19.5,-19.5,-28) rot=(0,0,1;0rad)
  Radius = 3
FEATURE [Part::Cylinder] Cylinder2644  label="Válec2614"
  Angle = 360
  AttacherType = Attacher::AttachEngine3D
  Height = 3
  Placement = pos=(-45,-160,-70) rot=(0,0,1;0rad)
  Radius = 3
FEATURE [Part::Cylinder] Cylinder2645  label="Válec2615"
  Angle = 360
  AttacherType = Attacher::AttachEngine3D
  Height = 3
  Placement = pos=(-19.5,19.5,-28) rot=(0,0,1;0rad)
  Radius = 3
FEATURE [Part::Cylinder] Cylinder2646  label="Válec2616"
  Angle = 360
  AttacherType = Attacher::AttachEngine3D
  Height = 3
  Placement = pos=(19.5,19.5,-28) rot=(0,0,1;0rad)
  Radius = 3
FEATURE [Part::Cylinder] Cylinder2647  label="Válec2617"
  Angle = 360
  AttacherType = Attacher::AttachEngine3D
  Height = 3
  Placement = pos=(24,-190,-70) rot=(0,0,1;0rad)
  Radius = 3
FEATURE [Part::Cylinder] Cylinder2648  label="Válec2618"
  Angle = 360
  AttacherType = Attacher::AttachEngine3D
  Height = 3
  Placement = pos=(-24,-190,-70) rot=(0,0,1;0rad)
  Radius = 3
FEATURE [Part::Cylinder] Cylinder2649  label="Válec2619"
  Angle = 360
  AttacherType = Attacher::AttachEngine3D
  Height = 3
  Placement = pos=(-24,-160,-70) rot=(0,0,1;0rad)
  Radius = 3
FEATURE [Part::Cylinder] Cylinder2650  label="Válec2620"
  Angle = 360
  AttacherType = Attacher::AttachEngine3D
  Height = 3
  Placement = pos=(45,-160,-70) rot=(0,0,1;0rad)
  Radius = 3
FEATURE [Part::Box] Box1069  label="Krychle1068"
  AttacherType = Attacher::AttachEngine3D
  Height = 51.3
  Length = 46.3
  Placement = pos=(-23.15,-126,-121.3) rot=(0,0,1;0rad)
  Width = 8
FEATURE [Part::Cylinder] Cylinder2651  label="Válec2621"
  Angle = 360
  AttacherType = Attacher::AttachEngine3D
  Height = 3
  Placement = pos=(24,-130,-70) rot=(0,0,1;0rad)
  Radius = 3
FEATURE [Part::Cylinder] Cylinder2652  label="Válec2622"
  Angle = 360
  AttacherType = Attacher::AttachEngine3D
  Height = 3
  Placement = pos=(-24,-160,-70) rot=(0,0,1;0rad)
  Radius = 3
FEATURE [Part::Cylinder] Cylinder2653  label="Válec2623"
  Angle = 360
  AttacherType = Attacher::AttachEngine3D
  Height = 40
  Placement = pos=(-24,-160,-70) rot=(0,0,1;0rad)
  Radius = 1.5
FEATURE [Part::Cylinder] Cylinder2654  label="Válec2624"
  Angle = 360
  AttacherType = Attacher::AttachEngine3D
  Height = 20
  Placement = pos=(19.5,-19.5,-28) rot=(0,0,1;0rad)
  Radius = 1.5
FEATURE [Part::Cylinder] Cylinder2655  label="Válec2625"
  Angle = 360
  AttacherType = Attacher::AttachEngine3D
  Height = 3
  Placement = pos=(-24,-130,-70) rot=(0,0,1;0rad)
  Radius = 3
FEATURE [Part::Cylinder] Cylinder2656  label="Válec2626"
  Angle = 360
  AttacherType = Attacher::AttachEngine3D
  Height = 3
  Placement = pos=(24,-130,-70) rot=(0,0,1;0rad)
  Radius = 3
FEATURE [Part::Cylinder] Cylinder2657  label="Válec2627"
  Angle = 360
  AttacherType = Attacher::AttachEngine3D
  Height = 3
  Placement = pos=(-45,-160,-70) rot=(0,0,1;0rad)
  Radius = 3
FEATURE [Part::Cylinder] Cylinder2658  label="Válec2628"
  Angle = 360
  AttacherType = Attacher::AttachEngine3D
  Height = 3
  Placement = pos=(45,-130,-70) rot=(0,0,1;0rad)
  Radius = 3
FEATURE [Part::Cylinder] Cylinder2659  label="Válec2629"
  Angle = 360
  AttacherType = Attacher::AttachEngine3D
  Height = 3
  Placement = pos=(-45,-130,-70) rot=(0,0,1;0rad)
  Radius = 3
FEATURE [Part::Cylinder] Cylinder2660  label="Válec2630"
  Angle = 360
  AttacherType = Attacher::AttachEngine3D
  Height = 40
  Placement = pos=(-45,-130,-70) rot=(0,0,1;0rad)
  Radius = 1.5
FEATURE [Part::Cylinder] Cylinder2661  label="Válec2631"
  Angle = 360
  AttacherType = Attacher::AttachEngine3D
  Height = 4
  Placement = pos=(0,-160,20) rot=(0,0,1;0rad)
  Radius = 4
FEATURE [Part::Cylinder] Cylinder2662  label="Válec2632"
  Angle = 360
  AttacherType = Attacher::AttachEngine3D
  Height = 3
  Placement = pos=(45,-130,-70) rot=(0,0,1;0rad)
  Radius = 3
FEATURE [Part::Box] Box1070  label="Krychle1069"
  AttacherType = Attacher::AttachEngine3D
  Height = 30
  Length = 42
  Placement = pos=(-21,-290,-73) rot=(0,0,1;0rad)
  Width = 200
FEATURE [Part::Cylinder] Cylinder2663  label="Válec2633"
  Angle = 360
  AttacherType = Attacher::AttachEngine3D
  Height = 3
  Placement = pos=(-24,-190,-70) rot=(0,0,1;0rad)
  Radius = 3
FEATURE [Part::Cylinder] Cylinder2664  label="Válec2634"
  Angle = 360
  AttacherType = Attacher::AttachEngine3D
  Height = 3
  Placement = pos=(24,-190,-70) rot=(0,0,1;0rad)
  Radius = 3
FEATURE [Part::Cylinder] Cylinder2665  label="Válec2635"
  Angle = 360
  AttacherType = Attacher::AttachEngine3D
  Height = 3
  Placement = pos=(24,-160,-70) rot=(0,0,1;0rad)
  Radius = 3
FEATURE [Part::Box] Box1071  label="Krychle1070"
  AttacherType = Attacher::AttachEngine3D
  Height = 30
  Length = 42
  Placement = pos=(-21,-290,-73) rot=(0,0,1;0rad)
  Width = 200
FEATURE [Part::Cylinder] Cylinder2666  label="Válec2636"
  Angle = 360
  AttacherType = Attacher::AttachEngine3D
  Height = 3
  Placement = pos=(45,-160,-70) rot=(0,0,1;0rad)
  Radius = 3
FEATURE [Part::Cylinder] Cylinder2667  label="Válec2637"
  Angle = 360
  AttacherType = Attacher::AttachEngine3D
  Height = 4
  Placement = pos=(0,-130,20) rot=(0,0,1;0rad)
  Radius = 4
FEATURE [Part::Cylinder] Cylinder2668  label="Válec2638"
  Angle = 360
  AttacherType = Attacher::AttachEngine3D
  Height = 3
  Placement = pos=(-45,-130,-70) rot=(0,0,1;0rad)
  Radius = 3
FEATURE [Part::Compound] Compound1172
  Links = -> [Cylinder2656,Cylinder2664,Cylinder2665,Cylinder2658,Cylinder2666,Cylinder2655,Cylinder2648,Cylinder2649,Cylinder2668,Cylinder2657]
FEATURE [Part::Cylinder] Cylinder2669  label="Válec2639"
  Angle = 360
  AttacherType = Attacher::AttachEngine3D
  Height = 20
  Placement = pos=(0,-130,20) rot=(0,0,1;0rad)
  Radius = 2
FEATURE [Part::Cylinder] Cylinder2670  label="Válec2640"
  Angle = 360
  AttacherType = Attacher::AttachEngine3D
  Height = 20
  Placement = pos=(0,-130,20) rot=(0,0,1;0rad)
  Radius = 2
FEATURE [Part::Cylinder] Cylinder2671  label="Válec2641"
  Angle = 360
  AttacherType = Attacher::AttachEngine3D
  Height = 4
  Placement = pos=(0,-130,20) rot=(0,0,1;0rad)
  Radius = 4
FEATURE [Part::Cylinder] Cylinder2672  label="Válec2642"
  Angle = 360
  AttacherType = Attacher::AttachEngine3D
  Height = 20
  Placement = pos=(-19.5,-19.5,-28) rot=(0,0,1;0rad)
  Radius = 1.5
FEATURE [Part::Cylinder] Cylinder2673  label="Válec2643"
  Angle = 360
  AttacherType = Attacher::AttachEngine3D
  Height = 50
  Placement = pos=(0,-140,-98) rot=(-1,0,0;1.5708rad)
  Radius = 10
FEATURE [Part::Cylinder] Cylinder2674  label="Válec2644"
  Angle = 360
  AttacherType = Attacher::AttachEngine3D
  Height = 20
  Placement = pos=(0,-160,20) rot=(0,0,1;0rad)
  Radius = 2
FEATURE [Part::Cylinder] Cylinder2675  label="Válec2645"
  Angle = 360
  AttacherType = Attacher::AttachEngine3D
  Height = 20
  Placement = pos=(0,-160,20) rot=(0,0,1;0rad)
  Radius = 2
FEATURE [Part::Cylinder] Cylinder2676  label="Válec2646"
  Angle = 360
  AttacherType = Attacher::AttachEngine3D
  Height = 4
  Placement = pos=(0,-130,20) rot=(0,0,1;0rad)
  Radius = 4
FEATURE [Part::Compound] Compound1174
  Links = -> [Cylinder2661,Cylinder2676]
  Placement = pos=(34.5,0,-91) rot=(0,0,1;0rad)
FEATURE [Part::Box] Box1072  label="Krychle1071"
  AttacherType = Attacher::AttachEngine3D
  Height = 4.85
  Length = 42
  Placement = pos=(-21,-160,-74.85) rot=(0,0,1;0rad)
  Width = 34
FEATURE [Part::Box] Box1073  label="Krychle1072"
  AttacherType = Attacher::AttachEngine3D
  Height = 10
  Length = 10
  Placement = pos=(-33,-126,-83) rot=(0,0,1;0rad)
  Width = 6
FEATURE [Part::Chamfer] Chamfer129
  Base = -> Box1073
  Edges = 1 edges r=6: [Edge4]
FEATURE [Part::Cylinder] Cylinder2677  label="Válec2647"
  Angle = 360
  AttacherType = Attacher::AttachEngine3D
  Height = 20
  Placement = pos=(0,-160,20) rot=(0,0,1;0rad)
  Radius = 2
FEATURE [Part::Compound] Compound1182
  Links = -> [Cylinder2677,Cylinder2670]
  Placement = pos=(34.5,0,-100) rot=(0,0,1;0rad)
FEATURE [Part::Cylinder] Cylinder2678  label="Válec2648"
  Angle = 360
  AttacherType = Attacher::AttachEngine3D
  Height = 20
  Placement = pos=(0,-160,20) rot=(0,0,1;0rad)
  Radius = 2
FEATURE [Part::Compound] Compound1179
  Links = -> [Cylinder2678,Cylinder2669]
  Placement = pos=(-34.5,0,-100) rot=(0,0,1;0rad)
FEATURE [Part::Cylinder] Cylinder2679  label="Válec2649"
  Angle = 360
  AttacherType = Attacher::AttachEngine3D
  Height = 20
  Placement = pos=(19.5,19.5,-28) rot=(0,0,1;0rad)
  Radius = 1.5
FEATURE [Part::Cylinder] Cylinder2680  label="Válec2650"
  Angle = 360
  AttacherType = Attacher::AttachEngine3D
  Height = 20
  Placement = pos=(0,-130,20) rot=(0,0,1;0rad)
  Radius = 2
FEATURE [Part::Compound] Compound1185
  Links = -> [Cylinder2674,Cylinder2680]
  Placement = pos=(34.5,0,-100) rot=(0,0,1;0rad)
FEATURE [Part::Cylinder] Cylinder2681  label="Válec2651"
  Angle = 360
  AttacherType = Attacher::AttachEngine3D
  Height = 20
  Placement = pos=(-19.5,19.5,-28) rot=(0,0,1;0rad)
  Radius = 1.5
FEATURE [Part::Compound] Compound1178
  Links = -> [Cylinder2672,Cylinder2681,Cylinder2654,Cylinder2679]
  Placement = pos=(0,-140,-98) rot=(1,0,0;1.5708rad)
FEATURE [Part::Cylinder] Cylinder2682  label="Válec2652"
  Angle = 360
  AttacherType = Attacher::AttachEngine3D
  Height = 4
  Placement = pos=(0,-160,20) rot=(0,0,1;0rad)
  Radius = 4
FEATURE [Part::Cylinder] Cylinder2683  label="Válec2653"
  Angle = 360
  AttacherType = Attacher::AttachEngine3D
  Height = 4
  Placement = pos=(0,-160,20) rot=(0,0,1;0rad)
  Radius = 4
FEATURE [Part::Compound] Compound1187
  Links = -> [Cylinder2683,Cylinder2667]
  Placement = pos=(-34.5,0,-91) rot=(0,0,1;0rad)
FEATURE [Part::Box] Box1074  label="Krychle1073"
  AttacherType = Attacher::AttachEngine3D
  Height = 25
  Length = 96
  Placement = pos=(-48,-120,-80) rot=(0,0,1;0rad)
  Width = 40
FEATURE [Part::Cylinder] Cylinder2684  label="Válec2654"
  Angle = 360
  AttacherType = Attacher::AttachEngine3D
  Height = 4
  Placement = pos=(0,-130,20) rot=(0,0,1;0rad)
  Radius = 4
FEATURE [Part::Compound] Compound1184
  Links = -> [Cylinder2682,Cylinder2684]
  Placement = pos=(34.5,0,-91) rot=(0,0,1;0rad)
FEATURE [Part::Cylinder] Cylinder2685  label="Válec2655"
  Angle = 360
  AttacherType = Attacher::AttachEngine3D
  Height = 20
  Placement = pos=(0,-130,20) rot=(0,0,1;0rad)
  Radius = 2
FEATURE [Part::Compound] Compound1188
  Links = -> [Cylinder2675,Cylinder2685]
  Placement = pos=(-34.5,0,-100) rot=(0,0,1;0rad)
FEATURE [Part::Box] Box1075  label="Krychle1074"
  AttacherType = Attacher::AttachEngine3D
  Height = 10
  Length = 10
  Placement = pos=(23,-126,-83) rot=(0,0,1;0rad)
  Width = 6
FEATURE [Part::Chamfer] Chamfer130
  Base = -> Box1075
  Edges = 1 edges r=6: [Edge8]
FEATURE [Part::Compound] Compound1186
  Links = -> [Chamfer130,Chamfer129]
FEATURE [Part::Cylinder] Cylinder2686  label="Válec2656"
  Angle = 360
  AttacherType = Attacher::AttachEngine3D
  Height = 4
  Placement = pos=(0,-160,20) rot=(0,0,1;0rad)
  Radius = 4
FEATURE [Part::Compound] Compound1181
  Links = -> [Cylinder2686,Cylinder2671]
  Placement = pos=(-34.5,0,-91) rot=(0,0,1;0rad)
FEATURE [Part::Cylinder] Cylinder2687  label="Válec2657"
  Angle = 360
  AttacherType = Attacher::AttachEngine3D
  Height = 32
  Placement = pos=(0,-140,-74) rot=(0,0,1;0rad)
  Radius = 60
FEATURE [Part::Cylinder] Cylinder2688  label="Válec2658"
  Angle = 360
  AttacherType = Attacher::AttachEngine3D
  Height = 40
  Placement = pos=(45,-130,-70) rot=(0,0,1;0rad)
  Radius = 1.5
FEATURE [Part::Cylinder] Cylinder2689  label="Válec2659"
  Angle = 360
  AttacherType = Attacher::AttachEngine3D
  Height = 4
  Placement = pos=(0,-160,-69) rot=(0,0,1;0rad)
  Radius = 48
FEATURE [Part::Cylinder] Cylinder2690  label="Válec2660"
  Angle = 360
  AttacherType = Attacher::AttachEngine3D
  Height = 40
  Placement = pos=(-45,-130,-70) rot=(0,0,1;0rad)
  Radius = 1.5
FEATURE [Part::Cylinder] Cylinder2691  label="Válec2661"
  Angle = 360
  AttacherType = Attacher::AttachEngine3D
  Height = 40
  Placement = pos=(-24,-130,-70) rot=(0,0,1;0rad)
  Radius = 1.5
FEATURE [Part::Cylinder] Cylinder2692  label="Válec2662"
  Angle = 360
  AttacherType = Attacher::AttachEngine3D
  Height = 40
  Placement = pos=(24,-130,-70) rot=(0,0,1;0rad)
  Radius = 1.5
FEATURE [Part::Cylinder] Cylinder2693  label="Válec2663"
  Angle = 360
  AttacherType = Attacher::AttachEngine3D
  Height = 40
  Placement = pos=(24,-160,-70) rot=(0,0,1;0rad)
  Radius = 1.5
FEATURE [Part::Cylinder] Cylinder2694  label="Válec2664"
  Angle = 360
  AttacherType = Attacher::AttachEngine3D
  Height = 40
  Placement = pos=(24,-190,-70) rot=(0,0,1;0rad)
  Radius = 1.5
FEATURE [Part::Box] Box1076  label="Krychle1075"
  AttacherType = Attacher::AttachEngine3D
  Height = 4
  Length = 96
  Placement = pos=(-48,-160,-69) rot=(0,0,1;0rad)
  Width = 40
FEATURE [Part::Cylinder] Cylinder2695  label="Válec2665"
  Angle = 360
  AttacherType = Attacher::AttachEngine3D
  Height = 40
  Placement = pos=(-24,-190,-70) rot=(0,0,1;0rad)
  Radius = 1.5
FEATURE [Part::Cylinder] Cylinder2696  label="Válec2666"
  Angle = 360
  AttacherType = Attacher::AttachEngine3D
  Height = 40
  Placement = pos=(-24,-160,-70) rot=(0,0,1;0rad)
  Radius = 1.5
FEATURE [Part::Cylinder] Cylinder2697  label="Válec2667"
  Angle = 360
  AttacherType = Attacher::AttachEngine3D
  Height = 40
  Placement = pos=(45,-130,-70) rot=(0,0,1;0rad)
  Radius = 1.5
FEATURE [Part::Cylinder] Cylinder2698  label="Válec2668"
  Angle = 360
  AttacherType = Attacher::AttachEngine3D
  Height = 40
  Placement = pos=(-24,-190,-70) rot=(0,0,1;0rad)
  Radius = 1.5
FEATURE [Part::Cylinder] Cylinder2699  label="Válec2669"
  Angle = 360
  AttacherType = Attacher::AttachEngine3D
  Height = 40
  Placement = pos=(24,-130,-70) rot=(0,0,1;0rad)
  Radius = 1.5
FEATURE [Part::Cylinder] Cylinder2700  label="Válec2670"
  Angle = 360
  AttacherType = Attacher::AttachEngine3D
  Height = 40
  Placement = pos=(-45,-160,-70) rot=(0,0,1;0rad)
  Radius = 1.5
FEATURE [Part::Cylinder] Cylinder2701  label="Válec2671"
  Angle = 360
  AttacherType = Attacher::AttachEngine3D
  Height = 40
  Placement = pos=(45,-160,-70) rot=(0,0,1;0rad)
  Radius = 1.5
FEATURE [Part::Cylinder] Cylinder2702  label="Válec2672"
  Angle = 360
  AttacherType = Attacher::AttachEngine3D
  Height = 3
  Placement = pos=(24,-160,-70) rot=(0,0,1;0rad)
  Radius = 3
FEATURE [Part::Compound] Compound1180
  Links = -> [Cylinder2651,Cylinder2647,Cylinder2702,Cylinder2662,Cylinder2650,Cylinder2639,Cylinder2663,Cylinder2652,Cylinder2659,Cylinder2644]
FEATURE [Part::Cylinder] Cylinder2703  label="Válec2673"
  Angle = 360
  AttacherType = Attacher::AttachEngine3D
  Height = 40
  Placement = pos=(45,-160,-70) rot=(0,0,1;0rad)
  Radius = 1.5
FEATURE [Part::Cylinder] Cylinder2704  label="Válec2674"
  Angle = 360
  AttacherType = Attacher::AttachEngine3D
  Height = 40
  Placement = pos=(-45,-160,-70) rot=(0,0,1;0rad)
  Radius = 1.5
FEATURE [Part::Compound] Compound1176
  Links = -> [Cylinder2692,Cylinder2694,Cylinder2693,Cylinder2688,Cylinder2703,Cylinder2691,Cylinder2695,Cylinder2696,Cylinder2690,Cylinder2704]
  Placement = pos=(0,0,-20) rot=(0,0,1;0rad)
FEATURE [Part::Cylinder] Cylinder2705  label="Válec2675"
  Angle = 360
  AttacherType = Attacher::AttachEngine3D
  Height = 40
  Placement = pos=(24,-160,-70) rot=(0,0,1;0rad)
  Radius = 1.5
FEATURE [Part::Compound] Compound1183
  Links = -> [Cylinder2699,Cylinder2642,Cylinder2705,Cylinder2697,Cylinder2701,Cylinder2640,Cylinder2698,Cylinder2653,Cylinder2660,Cylinder2700]
  Placement = pos=(0,0,-20) rot=(0,0,1;0rad)
FEATURE [Part::Cut] Cut978
  Base = -> Box1076
  Tool = -> Compound1176
FEATURE [Part::Cut] Cut983
  Base = -> Cut978
  Tool = -> Compound1172
FEATURE [Part::Cut] Cut981
  Base = -> Cut983
  Tool = -> Box1071
FEATURE [Part::Cut] Cut987
  Base = -> Cut981
  Tool = -> Compound1187
FEATURE [Part::Cut] Cut988
  Base = -> Box1069
  Tool = -> Compound1173
FEATURE [Part::Cut] Cut984
  Base = -> Cut988
  Tool = -> Compound1178
FEATURE [Part::Cut] Cut979
  Base = -> Cut984
  Tool = -> Cylinder2673
FEATURE [Part::Cut] Cut990
  Base = -> Cylinder2689
  Tool = -> Compound1183
FEATURE [Part::Cut] Cut980
  Base = -> Cut990
  Tool = -> Compound1180
FEATURE [Part::Cut] Cut976
  Base = -> Cut980
  Tool = -> Box1070
FEATURE [Part::Cut] Cut985
  Base = -> Cut976
  Tool = -> Compound1179
FEATURE [Part::Cut] Cut977
  Base = -> Cut985
  Tool = -> Compound1181
FEATURE [Part::Cut] Cut986
  Base = -> Cut977
  Tool = -> Compound1182
FEATURE [Part::Cut] Cut991
  Base = -> Cut987
  Tool = -> Compound1188
FEATURE [Part::Cut] Cut989
  Base = -> Cut991
  Tool = -> Compound1184
FEATURE [Part::Cut] Cut982
  Base = -> Cut989
  Placement = pos=(0,0,-4) rot=(0,0,1;0rad)
  Tool = -> Compound1185
FEATURE [Part::Cut] Cut992
  Base = -> Cut986
  Tool = -> Compound1174
FEATURE [Part::Common] Common007
  Base = -> Cut992
  Tool = -> Cylinder2687
FEATURE [Part::Cut] Cut993
  Base = -> Common007
  Placement = pos=(0,0,-4) rot=(0,0,1;0rad)
  Tool = -> Box1074
FEATURE [Part::Fillet] Fillet008
  Base = -> Cut993
  Edges = 2 edges r=36: [Edge2,Edge68]
FEATURE [Part::FeaturePython] Tube115  label="kruza001"  # WARN: FeaturePython — macro-defined, semantics opaque (R4)
  AttacherType = Attacher::AttachEngine3D
  Height = 1
  InnerRadius = 10
  OuterRadius = 11
  Placement = pos=(0,-117,-98) rot=(1,0,0;1.5708rad)
FEATURE [Part::Compound] Compound1175
  Links = -> [Cut979,Tube115]
FEATURE [Part::Compound] Compound1177  label="moto_bokohold001"
  Links = -> [Compound1175,Box1072]
  Placement = pos=(0,0,1) rot=(0,0,1;0rad)
FEATURE [Part::Compound] Compound1190
  Links = -> [Cylinder2641,Cylinder2645,Cylinder2643,Cylinder2646]
  Placement = pos=(0,-146,-97) rot=(1,0,0;1.5708rad)
FEATURE [Part::Chamfer] Chamfer132
  Base = -> Compound1177
  Edges = 2 edges r=2: [Edge3,Edge16]
FEATURE [Part::Chamfer] Chamfer133
  Base = -> Chamfer132
  Edges = 2 edges r=2: [Edge3,Edge19]
FEATURE [Part::Cut] Cut975
  Base = -> Chamfer133
  Tool = -> Compound1190
FEATURE [Part::Chamfer] Chamfer131
  Base = -> Cut975
  Edges = 1 edges r=3: [Edge77]
FEATURE [Part::Compound] Compound1189  label="L-elb_major-moto-cavo-reinforced"
  Links = -> [Compound1186,Fillet008,Cut982,Chamfer131]
FEATURE [Mesh::Feature] Mesh020  label="L-elb_major-moto-cavo-reinforced (Meshed)"
FEATURE [Part::Box] Box105  label="Krychle105"
  AttacherType = Attacher::AttachEngine3D
  Height = 8
  Length = 42.3
  Placement = pos=(-21.15,-21.15,-70) rot=(0,0,1;0rad)
  Width = 42.3
FEATURE [Part::Cylinder] Cylinder335  label="Válec335"
  Angle = 360
  AttacherType = Attacher::AttachEngine3D
  Height = 20
  Placement = pos=(10.48,15.75,-50) rot=(0,0,1;0rad)
  Radius = 1.5
FEATURE [Part::Box] Box107  label="Krychle107"
  AttacherType = Attacher::AttachEngine3D
  Height = 4
  Length = 46.3
  Placement = pos=(-23.15,-23.15,-25) rot=(0,0,1;0rad)
  Width = 46.3
FEATURE [Part::Cylinder] Cylinder326  label="Válec326"
  Angle = 360
  AttacherType = Attacher::AttachEngine3D
  Height = 20
  Placement = pos=(-10.48,15.75,-50) rot=(0,0,1;0rad)
  Radius = 1.5
FEATURE [Part::Cylinder] Cylinder327  label="Válec327"
  Angle = 360
  AttacherType = Attacher::AttachEngine3D
  Height = 10
  Placement = pos=(19.5,-19.5,-28) rot=(0,0,1;0rad)
  Radius = 1.5
FEATURE [Part::Cylinder] Cylinder331  label="Válec331"
  Angle = 360
  AttacherType = Attacher::AttachEngine3D
  Height = 50
  Placement = pos=(0,0,-29) rot=(0,0,1;0rad)
  Radius = 8
FEATURE [Part::Cut] Cut115
  Base = -> Box107
  Tool = -> Cylinder331
FEATURE [Part::Box] Box111  label="Krychle111"
  AttacherType = Attacher::AttachEngine3D
  Height = 2
  Length = 8
  Placement = pos=(-24.5,16.5,-55) rot=(0,0,1;0rad)
  Width = 6
FEATURE [Part::Box] Box104  label="Krychle104"
  AttacherType = Attacher::AttachEngine3D
  Height = 8
  Length = 46.3
  Placement = pos=(-23.15,-23.15,-70) rot=(0,0,1;0rad)
  Width = 46.3
FEATURE [Part::Cut] Cut110
  Base = -> Box104
  Placement = pos=(0,0,-4) rot=(0,0,1;0rad)
  Tool = -> Box105
FEATURE [Part::Box] Box106  label="Krychle106"
  AttacherType = Attacher::AttachEngine3D
  Height = 20
  Length = 29
  Placement = pos=(-14.5,0,-75) rot=(0,0,1;0rad)
  Width = 45.5
FEATURE [Part::Cut] Cut109
  Base = -> Cut110
  Placement = pos=(0,0,9) rot=(0,0,1;0rad)
  Tool = -> Box106
FEATURE [Part::Cylinder] Cylinder339  label="Válec339"
  Angle = 360
  AttacherType = Attacher::AttachEngine3D
  Height = 10
  Placement = pos=(-19.5,19.5,-28) rot=(0,0,1;0rad)
  Radius = 1.5
FEATURE [Part::Box] Box112  label="Krychle112"
  AttacherType = Attacher::AttachEngine3D
  Height = 8
  Length = 7
  Placement = pos=(-22,15,-74) rot=(0,0,1;0rad)
  Width = 7
FEATURE [Part::Cylinder] Cylinder330  label="Válec330"
  Angle = 360
  AttacherType = Attacher::AttachEngine3D
  Height = 20
  Placement = pos=(-15.5,-15.5,-68) rot=(0,0,1;0rad)
  Radius = 1.5
FEATURE [Part::Cylinder] Cylinder336  label="Válec336"
  Angle = 360
  AttacherType = Attacher::AttachEngine3D
  Height = 3
  Placement = pos=(-15.5,-15.5,-54) rot=(0,0,1;0rad)
  Radius = 3
FEATURE [Part::Cylinder] Cylinder344  label="Válec344"
  Angle = 360
  AttacherType = Attacher::AttachEngine3D
  Height = 20
  Placement = pos=(19.5,-19.5,-28) rot=(0,0,1;0rad)
  Radius = 1.5
FEATURE [Part::Cylinder] Cylinder338  label="Válec338"
  Angle = 360
  AttacherType = Attacher::AttachEngine3D
  Height = 20
  Placement = pos=(-15.5,15.5,-68) rot=(0,0,1;0rad)
  Radius = 1.5
FEATURE [Part::Cylinder] Cylinder329  label="Válec329"
  Angle = 360
  AttacherType = Attacher::AttachEngine3D
  Height = 20
  Placement = pos=(15.5,15.5,-68) rot=(0,0,1;0rad)
  Radius = 1.5
FEATURE [Part::Cylinder] Cylinder342  label="Válec342"
  Angle = 360
  AttacherType = Attacher::AttachEngine3D
  Height = 20
  Placement = pos=(-19.5,-19.5,-28) rot=(0,0,1;0rad)
  Radius = 1.5
FEATURE [Part::Box] Box110  label="Krychle110"
  AttacherType = Attacher::AttachEngine3D
  Height = 2
  Length = 8
  Placement = pos=(-24.5,-22.5,-55) rot=(0,0,1;0rad)
  Width = 6
FEATURE [Part::Cylinder] Cylinder332  label="Válec332"
  Angle = 360
  AttacherType = Attacher::AttachEngine3D
  Height = 3
  Placement = pos=(15.5,-15.5,-54) rot=(0,0,1;0rad)
  Radius = 3
FEATURE [Part::Cylinder] Cylinder350  label="Válec350"
  Angle = 360
  AttacherType = Attacher::AttachEngine3D
  Height = 20
  Placement = pos=(-15.5,-15.5,-68) rot=(0,0,1;0rad)
  Radius = 1.5
FEATURE [Part::Cylinder] Cylinder337  label="Válec337"
  Angle = 360
  AttacherType = Attacher::AttachEngine3D
  Height = 10
  Placement = pos=(-19.5,-19.5,-28) rot=(0,0,1;0rad)
  Radius = 1.5
FEATURE [Part::Cylinder] Cylinder340  label="Válec340"
  Angle = 360
  AttacherType = Attacher::AttachEngine3D
  Height = 10
  Placement = pos=(19.5,19.5,-28) rot=(0,0,1;0rad)
  Radius = 1.5
FEATURE [Part::Box] Box109  label="Krychle109"
  AttacherType = Attacher::AttachEngine3D
  Height = 2
  Length = 8
  Placement = pos=(16.5,-22.5,-55) rot=(0,0,1;0rad)
  Width = 6
FEATURE [Part::Cylinder] Cylinder333  label="Válec333"
  Angle = 360
  AttacherType = Attacher::AttachEngine3D
  Height = 3
  Placement = pos=(15.5,15.5,-54) rot=(0,0,1;0rad)
  Radius = 3
FEATURE [Part::Cylinder] Cylinder341  label="Válec341"
  Angle = 360
  AttacherType = Attacher::AttachEngine3D
  Height = 8
  Placement = pos=(-15.15,15.15,-74) rot=(0,0,1;0rad)
  Radius = 6
FEATURE [Part::Cut] Cut120
  Base = -> Box112
  Tool = -> Cylinder341
FEATURE [Part::Cut] Cut118
  Base = -> Box112
  Placement = pos=(0,0,0) rot=(0,0,-1;1.5708rad)
  Tool = -> Cylinder341
FEATURE [Part::Cut] Cut119
  Base = -> Box112
  Placement = pos=(0,0,0) rot=(0,0,1;3.14159rad)
  Tool = -> Cylinder341
FEATURE [Part::Cut] Cut117
  Base = -> Box112
  Placement = pos=(0,0,0) rot=(0,0,1;1.5708rad)
  Tool = -> Cylinder341
FEATURE [Part::Box] Box108  label="Krychle108"
  AttacherType = Attacher::AttachEngine3D
  Height = 2
  Length = 8
  Placement = pos=(16.5,16.5,-55) rot=(0,0,1;0rad)
  Width = 6
FEATURE [Part::Cylinder] Cylinder328  label="Válec328"
  Angle = 360
  AttacherType = Attacher::AttachEngine3D
  Height = 20
  Placement = pos=(15.5,-15.5,-68) rot=(0,0,1;0rad)
  Radius = 1.5
FEATURE [Part::Cylinder] Cylinder334  label="Válec334"
  Angle = 360
  AttacherType = Attacher::AttachEngine3D
  Height = 3
  Placement = pos=(-15.5,15.5,-54) rot=(0,0,1;0rad)
  Radius = 3
FEATURE [Part::Cylinder] Cylinder345  label="Válec345"
  Angle = 360
  AttacherType = Attacher::AttachEngine3D
  Height = 20
  Placement = pos=(-19.5,19.5,-28) rot=(0,0,1;0rad)
  Radius = 1.5
FEATURE [Part::Box] Box115  label="Krychle115"
  AttacherType = Attacher::AttachEngine3D
  Height = 2
  Length = 8
  Placement = pos=(16.5,16.5,-55) rot=(0,0,1;0rad)
  Width = 6
FEATURE [Part::Cylinder] Cylinder343  label="Válec343"
  Angle = 360
  AttacherType = Attacher::AttachEngine3D
  Height = 20
  Placement = pos=(19.5,19.5,-28) rot=(0,0,1;0rad)
  Radius = 1.5
FEATURE [Part::Box] Box116  label="Krychle116"
  AttacherType = Attacher::AttachEngine3D
  Height = 2
  Length = 8
  Placement = pos=(16.5,-22.5,-55) rot=(0,0,1;0rad)
  Width = 6
FEATURE [Part::Box] Box114  label="Krychle114"
  AttacherType = Attacher::AttachEngine3D
  Height = 2
  Length = 8
  Placement = pos=(-24.5,16.5,-55) rot=(0,0,1;0rad)
  Width = 6
FEATURE [Part::Box] Box113  label="Krychle113"
  AttacherType = Attacher::AttachEngine3D
  Height = 2
  Length = 8
  Placement = pos=(-24.5,-22.5,-55) rot=(0,0,1;0rad)
  Width = 6
FEATURE [Part::Box] Box119  label="Krychle119"
  AttacherType = Attacher::AttachEngine3D
  Height = 11
  Length = 34
  Placement = pos=(-17,-17,-73) rot=(0,0,1;0rad)
  Width = 34
FEATURE [Part::Cylinder] Cylinder352  label="Válec352"
  Angle = 360
  AttacherType = Attacher::AttachEngine3D
  Height = 20
  Placement = pos=(15.5,-15.5,-68) rot=(0,0,1;0rad)
  Radius = 1.5
FEATURE [Part::Box] Box117  label="Krychle117"
  AttacherType = Attacher::AttachEngine3D
  Height = 20
  Length = 29
  Placement = pos=(-14.5,0,-75) rot=(0,0,1;0rad)
  Width = 45.5
FEATURE [Part::Cylinder] Cylinder353  label="Válec353"
  Angle = 360
  AttacherType = Attacher::AttachEngine3D
  Height = 20
  Placement = pos=(15.5,15.5,-68) rot=(0,0,1;0rad)
  Radius = 1.5
FEATURE [Part::Box] Box118  label="Krychle118"
  AttacherType = Attacher::AttachEngine3D
  Height = 2
  Length = 46.3
  Placement = pos=(-23.15,-23.15,-64) rot=(0,0,1;0rad)
  Width = 46.3
FEATURE [Part::Cut] Cut123
  Base = -> Box118
  Placement = pos=(0,0,7) rot=(0,0,1;0rad)
  Tool = -> Box119
FEATURE [Part::Cylinder] Cylinder351  label="Válec351"
  Angle = 360
  AttacherType = Attacher::AttachEngine3D
  Height = 20
  Placement = pos=(-15.5,15.5,-68) rot=(0,0,1;0rad)
  Radius = 1.5
FEATURE [Part::Compound] Compound108
  Links = -> [Cylinder326,Cylinder335]
  Placement = pos=(0,0,-10) rot=(0,0,1;0rad)
FEATURE [Part::Compound] Compound105
  Links = -> [Box108,Box111,Box109,Box110]
  Placement = pos=(0,0,10) rot=(0,0,1;0rad)
FEATURE [Part::Compound] Compound110
  Links = -> [Cylinder336,Cylinder332,Cylinder334,Cylinder333]
FEATURE [Part::Compound] Compound111
  Links = -> [Cut120,Cut117,Cut119,Cut118]
  Placement = pos=(0,0,9) rot=(0,0,1;0rad)
FEATURE [Part::Chamfer] Chamfer163
  Base = -> Cut109
  Edges = 4 edges r=2: [Edge1,Edge3,Edge6,Edge29]
FEATURE [Part::Compound] Compound106
  Links = -> [Cylinder329,Cylinder338,Cylinder328,Cylinder330]
FEATURE [Part::Compound] Compound113
  Links = -> [Box115,Box114,Box116,Box113]
  Placement = pos=(0,0,-2) rot=(0,0,1;0rad)
FEATURE [Part::Compound] Compound112
  Links = -> [Cylinder342,Cylinder345,Cylinder344,Cylinder343]
  Placement = pos=(0,0,-33) rot=(0,0,1;0rad)
FEATURE [Part::Cut] Cut1076
  Base = -> Compound111
  Tool = -> Compound112
FEATURE [Part::Compound] Compound109
  Links = -> [Cylinder337,Cylinder339,Cylinder327,Cylinder340]
FEATURE [Part::Cut] Cut114
  Base = -> Cut115
  Tool = -> Compound109
FEATURE [Part::Compound] Compound107
  Links = -> [Cut114]
  Placement = pos=(0,0,-30) rot=(0,0,1;0rad)
FEATURE [Part::Cut] Cut116
  Base = -> Compound107
  Tool = -> Compound105
FEATURE [Part::Cut] Cut112
  Base = -> Cut116
  Tool = -> Compound108
FEATURE [Part::Cut] Cut113
  Base = -> Cut112
  Tool = -> Compound106
FEATURE [Part::Cut] Cut111
  Base = -> Cut113
  Tool = -> Compound110
FEATURE [Part::Chamfer] Chamfer010
  Base = -> Cut111
  Edges = 4 edges r=2: [Edge1,Edge3,Edge6,Edge22]
FEATURE [Part::Compound] Compound115
  Links = -> [Cylinder353,Cylinder351,Cylinder352,Cylinder350]
FEATURE [Part::Cut] Cut121
  Base = -> Cut123
  Tool = -> Compound115
FEATURE [Part::Cut] Cut122
  Base = -> Cut121
  Tool = -> Box117
FEATURE [Part::Chamfer] Chamfer162
  Base = -> Cut122
  Edges = 2 edges r=2: [Edge1,Edge3]
FEATURE [Part::Chamfer] Chamfer009
  Base = -> Chamfer162
  Edges = 2 edges r=2: [Edge53,Edge55]
FEATURE [Part::Cut] Cut124
  Base = -> Chamfer009
  Tool = -> Compound113
FEATURE [Part::Chamfer] Chamfer012
  Base = -> Chamfer163
  Edges = 5 edges r=0.9: [Edge3,Edge24,Edge25,Edge27,Edge29]
FEATURE [Part::Compound] Compound1263  label="L-elb_moto-hold"
  Links = -> [Cut1076,Cut124,Chamfer010,Chamfer012]
  Placement = pos=(0,0,-80) rot=(0,0,1;0rad)
FEATURE [Part::FeaturePython] Tube116  # WARN: FeaturePython — macro-defined, semantics opaque (R4)
  AttacherType = Attacher::AttachEngine3D
  Height = 16
  InnerRadius = 4.2
  OuterRadius = 9
  Placement = pos=(200,0,-8) rot=(0,0,1;0rad)
FEATURE [Part::FeaturePython] Tube117  # WARN: FeaturePython — macro-defined, semantics opaque (R4)
  AttacherType = Attacher::AttachEngine3D
  Height = 50
  InnerRadius = 2.7
  OuterRadius = 6.5
  Placement = pos=(0,0,-42) rot=(0,0,1;0rad)
FEATURE [Part::Box] Box907  label="Krychle906"
  AttacherType = Attacher::AttachEngine3D
  Height = 6
  Length = 6
  Placement = pos=(196.5,-3,18) rot=(0,0,1;1.5708rad)
  Width = 2
FEATURE [Part::Cylinder] Cylinder2334  label="Válec2334"
  Angle = 360
  AttacherType = Attacher::AttachEngine3D
  Height = 100
  Placement = pos=(100,0,15) rot=(0.57735,0.57735,0.57735;2.0944rad)
  Radius = 1.5
FEATURE [Part::Cylinder] Cylinder2335  label="Válec2335"
  Angle = 360
  AttacherType = Attacher::AttachEngine3D
  Height = 100
  Placement = pos=(100,0,21) rot=(0.57735,0.57735,0.57735;2.0944rad)
  Radius = 1.5
FEATURE [Part::Box] Box906  label="Krychle905"
  AttacherType = Attacher::AttachEngine3D
  Height = 6
  Length = 6
  Placement = pos=(196.5,-3,12) rot=(0,0,1;1.5708rad)
  Width = 2
FEATURE [Part::Cylinder] Cylinder2336  label="Válec2336"
  Angle = 360
  AttacherType = Attacher::AttachEngine3D
  Height = 100
  Placement = pos=(-100,0,-36) rot=(0.57735,0.57735,0.57735;2.0944rad)
  Radius = 1.5
FEATURE [Part::Box] Box908  label="Krychle907"
  AttacherType = Attacher::AttachEngine3D
  Height = 9
  Length = 6
  Placement = pos=(-2,-3,-42) rot=(0,0,1;1.5708rad)
  Width = 2
FEATURE [Part::Compound] Compound1013
  Links = -> [Box907,Box906]
  Placement = pos=(0,0,-20) rot=(0,0,1;0rad)
FEATURE [Part::Cut] Cut838
  Base = -> Tube116
  Tool = -> Compound1013
FEATURE [Part::Compound] Compound1014
  Links = -> [Cylinder2335,Cylinder2334]
  Placement = pos=(0,0,-20) rot=(0,0,1;0rad)
FEATURE [Part::Cut] Cut839
  Base = -> Cut838
  Placement = pos=(-200,120,43) rot=(1,0,0;1.5708rad)
  Tool = -> Compound1014
FEATURE [Part::Compound] Compound1015
  Links = -> [Cylinder2336]
FEATURE [Part::Cut] Cut841
  Base = -> Tube117
  Tool = -> Compound1015
FEATURE [Part::Cut] Cut840
  Base = -> Cut841
  Placement = pos=(0,104,43) rot=(-1,0,0;1.5708rad)
  Tool = -> Box908
FEATURE [Part::Compound] Compound1016  label="L-elb_moto-shaft"
  Links = -> [Cut839,Cut840]
FEATURE [Part::Cylinder] Cylinder2706  label="Válec2676"
  Angle = 360
  AttacherType = Attacher::AttachEngine3D
  Height = 100
  Placement = pos=(100,0,15) rot=(0.57735,0.57735,0.57735;2.0944rad)
  Radius = 1.5
FEATURE [Part::Cylinder] Cylinder2707  label="Válec2677"
  Angle = 360
  AttacherType = Attacher::AttachEngine3D
  Height = 100
  Placement = pos=(-100,0,-36) rot=(0.57735,0.57735,0.57735;2.0944rad)
  Radius = 1.5
FEATURE [Part::Cylinder] Cylinder2708  label="Válec2678"
  Angle = 360
  AttacherType = Attacher::AttachEngine3D
  Height = 100
  Placement = pos=(100,0,21) rot=(0.57735,0.57735,0.57735;2.0944rad)
  Radius = 1.5
FEATURE [Part::Box] Box1077  label="Krychle1076"
  AttacherType = Attacher::AttachEngine3D
  Height = 6
  Length = 6
  Placement = pos=(196.5,-3,18) rot=(0,0,1;1.5708rad)
  Width = 2
FEATURE [Part::Box] Box1078  label="Krychle1077"
  AttacherType = Attacher::AttachEngine3D
  Height = 6
  Length = 6
  Placement = pos=(196.5,-3,12) rot=(0,0,1;1.5708rad)
  Width = 2
FEATURE [Part::Box] Box1079  label="Krychle1078"
  AttacherType = Attacher::AttachEngine3D
  Height = 9
  Length = 6
  Placement = pos=(-2,-3,-42) rot=(0,0,1;1.5708rad)
  Width = 2
FEATURE [Part::FeaturePython] Tube118  # WARN: FeaturePython — macro-defined, semantics opaque (R4)
  AttacherType = Attacher::AttachEngine3D
  Height = 16
  InnerRadius = 4.1
  OuterRadius = 9
  Placement = pos=(200,0,-8) rot=(0,0,1;0rad)
FEATURE [Part::FeaturePython] Tube119  # WARN: FeaturePython — macro-defined, semantics opaque (R4)
  AttacherType = Attacher::AttachEngine3D
  Height = 52
  InnerRadius = 2.6
  OuterRadius = 6
  Placement = pos=(0,0,-42) rot=(0,0,1;0rad)
FEATURE [Part::Compound] Compound1264
  Links = -> [Box1077,Box1078]
  Placement = pos=(0,0,-20) rot=(0,0,1;0rad)
FEATURE [Part::Cut] Cut1078
  Base = -> Tube118
  Tool = -> Compound1264
FEATURE [Part::Compound] Compound1266
  Links = -> [Cylinder2708,Cylinder2706]
  Placement = pos=(0,0,-20) rot=(0,0,1;0rad)
FEATURE [Part::Cut] Cut1080
  Base = -> Cut1078
  Placement = pos=(-200,120,43) rot=(1,0,0;1.5708rad)
  Tool = -> Compound1266
FEATURE [Part::Compound] Compound1267
  Links = -> [Cylinder2707]
FEATURE [Part::Cut] Cut1079
  Base = -> Tube119
  Tool = -> Compound1267
FEATURE [Part::Cut] Cut1077
  Base = -> Cut1079
  Placement = pos=(0,102,43) rot=(-1,0,0;1.5708rad)
  Tool = -> Box1079
FEATURE [Part::Compound] Compound1265  label="L-elb_moto-shaft-longer"
  Links = -> [Cut1080,Cut1077]
FEATURE [Mesh::Feature] Mesh021  label="L-elb_moto-shaft (Meshed)"
FEATURE [Mesh::Feature] Mesh022  label="L-elb_major-conno-moto (Meshed)001"
FEATURE [Mesh::Feature] Mesh023  label="L-elb_major-conno-nomoto (Meshed)001"
FEATURE [Mesh::Feature] Mesh024  label="L-elb_encoder-washer (Meshed)"
FEATURE [Mesh::Feature] Mesh025  label="L-elb_xorior-washer (Meshed)001"
FEATURE [Mesh::Feature] Mesh026  label="T-mini_washer (Meshed)"
FEATURE [Mesh::Feature] Mesh027  label="T-mini_box (Meshed)"
FEATURE [Mesh::Feature] Mesh028  label="L-elb_encoder-sidehold (Meshed)"
FEATURE [Mesh::Feature] Mesh029  label="L-elb_xorior-hole (Meshed)001"
FEATURE [Mesh::Feature] Mesh030  label="L-elb_xorior-cover (Meshed)001"
FEATURE [Mesh::Feature] Mesh031  label="J-mini_encoder-belt-ring_rear (Meshed)001"
FEATURE [Mesh::Feature] Mesh032  label="L-elb_encoder-uphold (Meshed)001"
FEATURE [Mesh::Feature] Mesh033  label="L-elb_encoder-bottomhold (Meshed)"
FEATURE [Mesh::Feature] Mesh034  label="J-mini_encoder-belt-ring_front (Meshed)"
FEATURE [Mesh::Feature] Mesh035  label="J-mini_wrist-side-rotator (Meshed)001"
FEATURE [Mesh::Feature] Mesh036  label="L-elb_major-conno_nomoto_cover (Meshed)001"
FEATURE [Mesh::Feature] Mesh037  label="L-elb_xorior-cover-A (Meshed)001"
FEATURE [Mesh::Feature] Mesh038  label="L-elb_xorior-cover-B (Meshed)001"
FEATURE [Mesh::Feature] Mesh039  label="L-elb_xorior-cover-C (Meshed)001"
FEATURE [Mesh::Feature] Mesh040  label="L-elb_xorior-cover-D (Meshed)001"
FEATURE [Mesh::Feature] Mesh041  label="L-elb_major-moto-cavo-reinforced (Meshed)001"
FEATURE [Mesh::Feature] Mesh042  label="L-elb_moto-hold (Meshed)"
FEATURE [Mesh::Feature] Mesh043  label="L-elb_moto-shaft (Meshed)001"
FEATURE [Part::Cylinder] Cylinder1809  label="Válec1809"
  Angle = 360
  AttacherType = Attacher::AttachEngine3D
  Height = 30
  Placement = pos=(58,11,26) rot=(0,0,1;0rad)
  Radius = 2.5
FEATURE [Part::Cylinder] Cylinder1806  label="Válec1806"
  Angle = 360
  AttacherType = Attacher::AttachEngine3D
  Height = 30
  Placement = pos=(58,11,26) rot=(0,0,1;0rad)
  Radius = 2.5
FEATURE [Part::Cylinder] Cylinder1807  label="Válec1807"
  Angle = 360
  AttacherType = Attacher::AttachEngine3D
  Height = 30
  Placement = pos=(58,-19,26) rot=(0,0,1;0rad)
  Radius = 2.5
FEATURE [Part::Cylinder] Cylinder1808  label="Válec1808"
  Angle = 360
  AttacherType = Attacher::AttachEngine3D
  Height = 30
  Placement = pos=(58,-19,26) rot=(0,0,1;0rad)
  Radius = 2.5
FEATURE [Part::Cylinder] Cylinder1827  label="Válec1827"
  Angle = 360
  AttacherType = Attacher::AttachEngine3D
  Height = 40
  Placement = pos=(75,16,42) rot=(1,0,0;1.5708rad)
  Radius = 14
FEATURE [Part::Cylinder] Cylinder1819  label="Válec1819"
  Angle = 360
  AttacherType = Attacher::AttachEngine3D
  Height = 20
  Placement = pos=(58,11,26) rot=(0,0,1;0rad)
  Radius = 1.25
FEATURE [Part::Cylinder] Cylinder1820  label="Válec1820"
  Angle = 360
  AttacherType = Attacher::AttachEngine3D
  Height = 3
  Placement = pos=(58,11,26) rot=(0,0,1;0rad)
  Radius = 2.5
FEATURE [Part::Cylinder] Cylinder1821  label="Válec1821"
  Angle = 360
  AttacherType = Attacher::AttachEngine3D
  Height = 3
  Placement = pos=(58,-19,26) rot=(0,0,1;0rad)
  Radius = 2.5
FEATURE [Part::Compound] Compound1268
  Links = -> [Cylinder1820,Cylinder1821]
  Placement = pos=(34,0,13) rot=(0,0,1;0rad)
FEATURE [Part::Cylinder] Cylinder1822  label="Válec1822"
  Angle = 360
  AttacherType = Attacher::AttachEngine3D
  Height = 3
  Placement = pos=(58,-19,26) rot=(0,0,1;0rad)
  Radius = 2.5
FEATURE [Part::Cylinder] Cylinder1823  label="Válec1823"
  Angle = 360
  AttacherType = Attacher::AttachEngine3D
  Height = 3
  Placement = pos=(58,11,26) rot=(0,0,1;0rad)
  Radius = 2.5
FEATURE [Part::Cylinder] Cylinder1825  label="Válec1825"
  Angle = 360
  AttacherType = Attacher::AttachEngine3D
  Height = 20
  Placement = pos=(58,-19,26) rot=(0,0,1;0rad)
  Radius = 1.25
FEATURE [Part::Cylinder] Cylinder1824  label="Válec1824"
  Angle = 360
  AttacherType = Attacher::AttachEngine3D
  Height = 20
  Placement = pos=(58,-19,26) rot=(0,0,1;0rad)
  Radius = 1.25
FEATURE [Part::Compound] Compound898
  Links = -> [Cylinder1819,Cylinder1824]
  Placement = pos=(34,0,0) rot=(0,0,1;0rad)
FEATURE [Part::Box] Box1080  label="Krychle716"
  AttacherType = Attacher::AttachEngine3D
  Height = 100
  Length = 100
  Placement = pos=(32,-54,-63) rot=(0,0,1;0rad)
  Width = 100
FEATURE [Part::Cylinder] Cylinder1826  label="Válec1826"
  Angle = 360
  AttacherType = Attacher::AttachEngine3D
  Height = 20
  Placement = pos=(58,11,26) rot=(0,0,1;0rad)
  Radius = 1.25
FEATURE [Part::Box] Box717  label="Krychle1079"
  AttacherType = Attacher::AttachEngine3D
  Height = 4
  Length = 40
  Placement = pos=(55,-24,37) rot=(0,0,1;0rad)
  Width = 40
FEATURE [Part::Compound] Compound914
  Links = -> [Cylinder1806,Cylinder1807]
  Placement = pos=(34,0,13) rot=(0,0,1;0rad)
FEATURE [Part::Compound] Compound909
  Links = -> [Cylinder1823,Cylinder1822]
  Placement = pos=(0,0,13) rot=(0,0,1;0rad)
FEATURE [Part::Compound] Compound1270
  Links = -> [Compound909,Compound1268]
FEATURE [Part::Compound] Compound916
  Links = -> [Cylinder1809,Cylinder1808]
  Placement = pos=(0,0,13) rot=(0,0,1;0rad)
FEATURE [Part::Compound] Compound915
  Links = -> [Compound916,Compound914]
FEATURE [Part::Compound] Compound1271
  Links = -> [Cylinder1826,Cylinder1825]
FEATURE [Part::Compound] Compound1269
  Links = -> [Compound1271,Compound898]
FEATURE [Part::FeaturePython] Tube090  # WARN: FeaturePython — macro-defined, semantics opaque (R4)
  AttacherType = Attacher::AttachEngine3D
  Height = 40
  InnerRadius = 13
  OuterRadius = 17
  Placement = pos=(75,16,42) rot=(1,0,0;1.5708rad)
FEATURE [Part::Chamfer] Chamfer164
  Base = -> Tube090
  Edges = 2 edges r=2: [Edge1,Edge3]
  Placement = pos=(0,0,-5) rot=(0,0,1;0rad)
FEATURE [Part::Cut] Cut533
  Base = -> Chamfer164
  Tool = -> Box1080
FEATURE [Part::Cut] Cut538
  Base = -> Box717
  Tool = -> Cylinder1827
FEATURE [Part::Cut] Cut539
  Base = -> Cut538
  Tool = -> Compound1269
FEATURE [Part::Cut] Cut540
  Base = -> Cut539
  Tool = -> Compound1270
FEATURE [Part::Chamfer] Chamfer165
  Base = -> Cut540
  Edges = 4 edges r=4: [Edge1,Edge3,Edge26,Edge35]
FEATURE [Part::Cut] Cut541
  Base = -> Cut533
  Tool = -> Compound915
FEATURE [Part::Cylinder] Cylinder2709  label="Válec2679"
  Angle = 360
  AttacherType = Attacher::AttachEngine3D
  Height = 40
  Placement = pos=(75,16,42) rot=(1,0,0;1.5708rad)
  Radius = 13
FEATURE [Part::Cylinder] Cylinder2710  label="Válec2680"
  Angle = 360
  AttacherType = Attacher::AttachEngine3D
  Height = 20
  Placement = pos=(58,11,26) rot=(0,0,1;0rad)
  Radius = 1.25
FEATURE [Part::Cylinder] Cylinder2711  label="Válec2681"
  Angle = 360
  AttacherType = Attacher::AttachEngine3D
  Height = 20
  Placement = pos=(58,11,26) rot=(0,0,1;0rad)
  Radius = 1.25
FEATURE [Part::Cylinder] Cylinder2712  label="Válec2682"
  Angle = 360
  AttacherType = Attacher::AttachEngine3D
  Height = 20
  Placement = pos=(58,-19,26) rot=(0,0,1;0rad)
  Radius = 1.25
FEATURE [Part::Cylinder] Cylinder2713  label="Válec2683"
  Angle = 360
  AttacherType = Attacher::AttachEngine3D
  Height = 20
  Placement = pos=(58,-19,26) rot=(0,0,1;0rad)
  Radius = 1.25
FEATURE [Part::Compound] Compound1272
  Links = -> [Cylinder2711,Cylinder2713]
  Placement = pos=(34,0,0) rot=(0,0,1;0rad)
FEATURE [Part::Compound] Compound1274
  Links = -> [Cylinder2710,Cylinder2712]
FEATURE [Part::Compound] Compound1273
  Links = -> [Compound1274,Compound1272]
FEATURE [Part::Cut] Cut1081
  Base = -> Cut541
  Tool = -> Compound1273
FEATURE [Part::Compound] Compound1275  label="L-elb_cable-organizer"
  Links = -> [Chamfer165,Cut1081]
FEATURE [Mesh::Feature] Mesh044  label="L-elb_cable-organizer (Meshed)"
